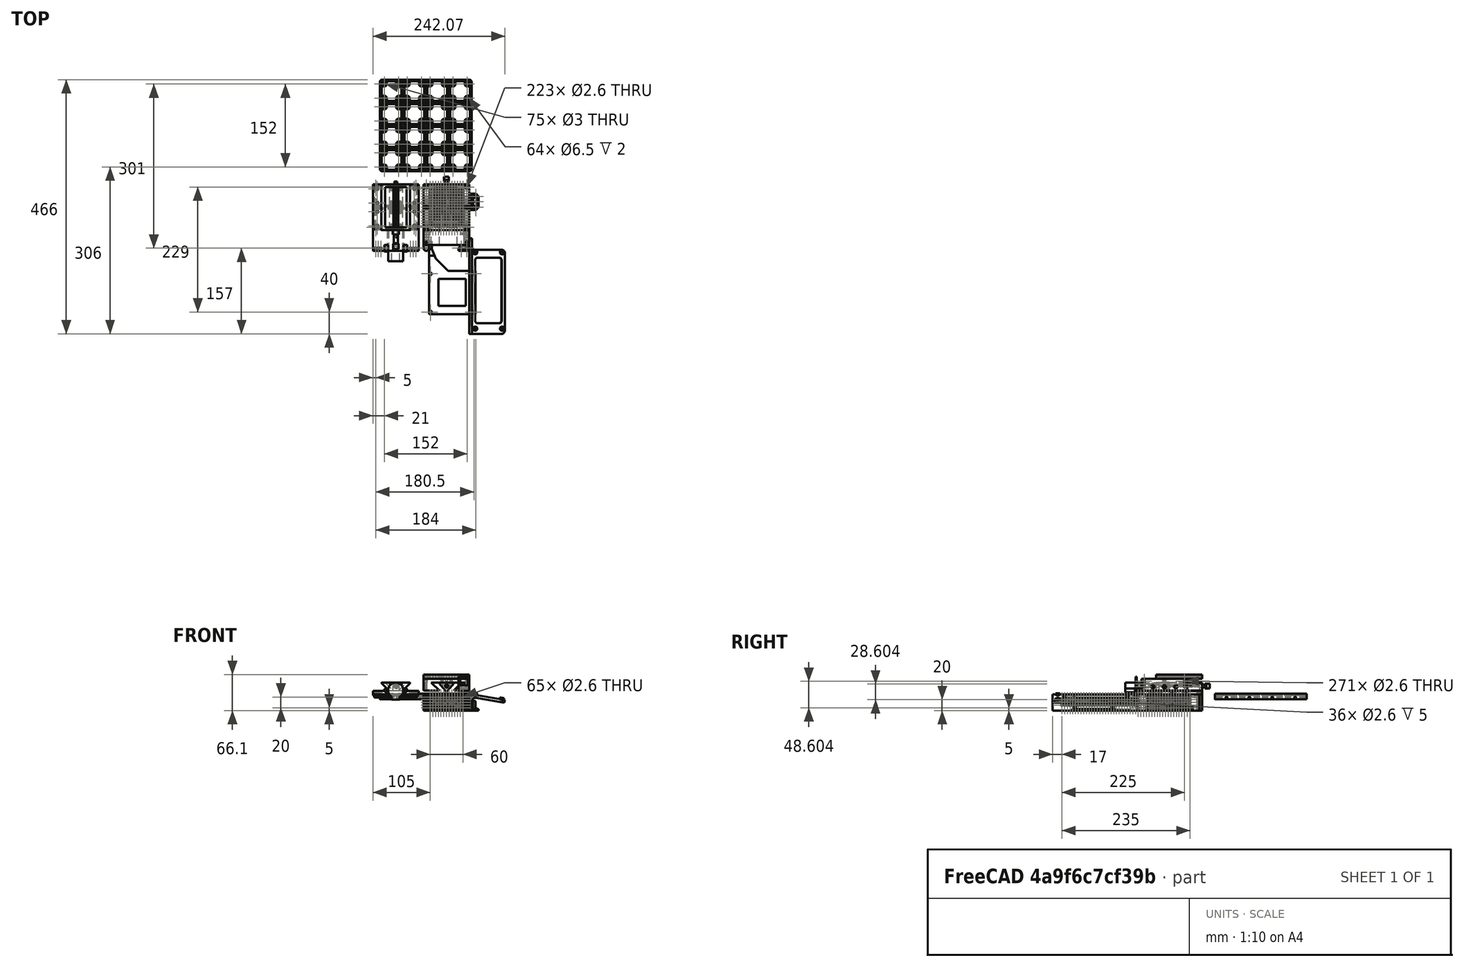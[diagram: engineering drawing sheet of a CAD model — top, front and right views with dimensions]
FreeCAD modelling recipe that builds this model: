
FCSTD DOCUMENT  (FreeCAD 1.0R39109 (Git))
Label: Linear Stage Motorised B Field Version
License: All rights reserved
LicenseURL: https://en.wikipedia.org/wiki/All_rights_reserved
objects: Sketcher::SketchObject×110, PartDesign::Pocket×58, PartDesign::Pad×54, PartDesign::Chamfer×31, PartDesign::Plane×19, PartDesign::Body×18, PartDesign::ShapeBinder×17, PartDesign::Fillet×6, PartDesign::SubShapeBinder×5, PartDesign::LinearPattern×4, PartDesign::Hole×3, PartDesign::FeatureBase×3, PartDesign::Point×1, Part::Part2DObjectPython×1, Part::Helix×1, PartDesign::AdditivePipe×1, Part::FeaturePython×1, App::VarSet×1, PartDesign::FeaturePython×1
note: 758 computed .brp shape members not serialized (recipe doc carries the construction recipe); baked Part::Feature solids carry a one-line shape summary decoded from their .brp

FEATURE [Sketcher::SketchObject] Sketch
  ArcFitTolerance = 1e-06
  AttachmentSupport = -> [XZ_Plane]
  FullyConstrained = true
  MakeInternals = false
  MapMode = 5
  Placement = pos=(0,0,0) rot=(1,0,0;1.5708rad)
  sketch-geometry (8):
    g0: LineSegment StartX=0 StartY=0 StartZ=0 EndX=84 EndY=0 EndZ=0
    g1: LineSegment StartX=0 StartY=0 StartZ=0 EndX=0 EndY=5 EndZ=0
    g2: LineSegment StartX=84 StartY=0 StartZ=0 EndX=84 EndY=5 EndZ=0
    g3: LineSegment StartX=0 StartY=5 StartZ=0 EndX=30 EndY=5 EndZ=0
    g4: LineSegment StartX=84 StartY=5 StartZ=0 EndX=54 EndY=5 EndZ=0
    g5: LineSegment StartX=30 StartY=5 StartZ=0 EndX=15 EndY=20 EndZ=0
    g6: LineSegment StartX=54 StartY=5 StartZ=0 EndX=69 EndY=20 EndZ=0
    g7: LineSegment StartX=15 StartY=20 StartZ=0 EndX=69 EndY=20 EndZ=0
  constraints (24):
    c: Distance(g0) = 84
    c: Distance(g1) = 5
    c: Coincident(g1,g0)
    c: PointOnObject(g1,g-2)
    c: Vertical(g1)
    c: Distance(g2) = 5
    c: Vertical(g2)
    c: Tangent(g0,g-1)
    c: PointOnObject(g2,g0)
    c: PointOnObject(g0,g2)
    c: Coincident(g3,g1)
    c: Horizontal(g3)
    c: Coincident(g4,g2)
    c: Horizontal(g4)
    c: DistanceX(g3,g3) = 30
    c: DistanceX(g4,g4) = 30
    c: Angle(g-1,g5) = 2.35619
    c: Coincident(g5,g3)
    c: Angle(g-1,g6) = 0.785398
    c: Coincident(g6,g4)
    c: DistanceY(g-1,g5) = 20
    c: DistanceY(g-1,g6) = 20
    c: Coincident(g7,g5)
    c: Coincident(g7,g6)
FEATURE [PartDesign::Pad] Pad
  Direction = (0,-1,2e-16)
  Length = 5
  Length2 = 10
  Placement = pos=(0,0,0) rot=(1,0,0;1.5708rad)
  Profile = -> Sketch
  ReferenceAxis = -> Sketch [N_Axis]
  Refine = true
  Suppressed = false
  Type = 0
FEATURE [Sketcher::SketchObject] Sketch001
  ArcFitTolerance = 1e-06
  AttachmentSupport = -> [Pad]
  ExternalGeometry = -> [Pad]
  FullyConstrained = true
  MakeInternals = false
  MapMode = 5
  Placement = pos=(0,-5,0) rot=(1,0,0;1.5708rad)
  sketch-geometry (14):
    g0: LineSegment StartX=15 StartY=20 StartZ=0 EndX=22.5 EndY=20 EndZ=0
    g1: LineSegment [constr] StartX=30 StartY=5 StartZ=0 EndX=37.5 EndY=5 EndZ=0
    g2: LineSegment StartX=22.5 StartY=20 StartZ=0 EndX=37.5 EndY=5 EndZ=0
    g3: LineSegment StartX=69 StartY=20 StartZ=0 EndX=61.5 EndY=20 EndZ=0
    g4: LineSegment [constr] StartX=54 StartY=5 StartZ=0 EndX=46.5 EndY=5 EndZ=0
    g5: LineSegment StartX=46.5 StartY=5 StartZ=0 EndX=61.5 EndY=20 EndZ=0
    g6: LineSegment StartX=46.5 StartY=5 StartZ=0 EndX=37.5 EndY=5 EndZ=0
    g7: LineSegment StartX=15 StartY=20 StartZ=0 EndX=30 EndY=5 EndZ=0
    g8: LineSegment StartX=30 StartY=5 StartZ=0 EndX=0 EndY=5 EndZ=0
    g9: LineSegment StartX=0 StartY=5 StartZ=0 EndX=0 EndY=0 EndZ=0
    g10: LineSegment StartX=0 StartY=0 StartZ=0 EndX=84 EndY=0 EndZ=0
    g11: LineSegment StartX=84 StartY=0 StartZ=0 EndX=84 EndY=5 EndZ=0
    g12: LineSegment StartX=84 StartY=5 StartZ=0 EndX=54 EndY=5 EndZ=0
    g13: LineSegment StartX=54 StartY=5 StartZ=0 EndX=69 EndY=20 EndZ=0
  constraints (32):
    c: Distance(g0) = 7.5
    c: Coincident(g0,g-4)
    c: PointOnObject(g0,g-3)
    c: Distance(g1) = 7.5
    c: Coincident(g1,g-5)
    c: Horizontal(g1)
    c: Coincident(g2,g0)
    c: Coincident(g2,g1)
    c: Distance(g3) = 7.5
    c: Coincident(g3,g-3)
    c: PointOnObject(g3,g-3)
    c: Distance(g4) = 7.5
    c: Coincident(g4,g-6)
    c: Horizontal(g4)
    c: Coincident(g5,g4)
    c: Coincident(g5,g3)
    c: Coincident(g6,g4)
    c: Coincident(g6,g1)
    c: Coincident(g7,g0)
    c: Coincident(g7,g1)
    c: Coincident(g8,g1)
    c: Coincident(g8,g-8)
    c: Coincident(g9,g8)
    c: Coincident(g9,g-1)
    c: Coincident(g10,g9)
    c: Coincident(g10,g-9)
    c: Coincident(g11,g10)
    c: Coincident(g11,g-7)
    c: Coincident(g12,g11)
    c: Coincident(g12,g4)
    c: Coincident(g13,g4)
    c: Coincident(g13,g3)
FEATURE [PartDesign::Pad] Pad001
  BaseFeature = -> Pad
  Direction = (0,-1,2e-16)
  Length = 74
  Length2 = 10
  Placement = pos=(0,0,0) rot=(1,0,0;1.5708rad)
  Profile = -> Sketch001
  ReferenceAxis = -> Sketch001 [N_Axis]
  Refine = true
  Suppressed = false
  Type = 0
FEATURE [Sketcher::SketchObject] Sketch002
  ArcFitTolerance = 1e-06
  AttachmentSupport = -> [Pad001]
  ExternalGeometry = -> [Pad001]
  FullyConstrained = true
  MakeInternals = false
  MapMode = 5
  Placement = pos=(0,-5,0) rot=(1,0,0;1.5708rad)
  sketch-geometry (2):
    g0: LineSegment [constr] StartX=42 StartY=20 StartZ=0 EndX=42 EndY=14 EndZ=0
    g1: Circle CenterX=42 CenterY=14 CenterZ=0 NormalX=0 NormalY=0 NormalZ=1 AngleXU=0 Radius=3
  constraints (5):
    c: Distance(g0) = 6
    c: Symmetric(g-3,g-3,g0)
    c: Vertical(g0)
    c: Diameter(g1) = 6
    c: Coincident(g1,g0)
FEATURE [PartDesign::Hole] Hole
  BaseFeature = -> Pad001
  CustomThreadClearance = 0
  Depth = 25
  DepthType = 0
  Diameter = 6
  DrillForDepth = false
  DrillPoint = 1
  DrillPointAngle = 118
  HoleCutCountersinkAngle = 90
  HoleCutCustomValues = false
  HoleCutDepth = 0
  HoleCutDiameter = 6.1
  HoleCutType = 0
  ModelThread = false
  Placement = pos=(0,0,0) rot=(1,0,0;1.5708rad)
  Profile = -> Sketch002
  Refine = true
  Suppressed = false
  Tapered = false
  TaperedAngle = 90
  ThreadClass = 0
  ThreadDepth = 25
  ThreadDepthType = 0
  ThreadDirection = 0
  ThreadFit = 0
  ThreadSize = 0
  ThreadType = 0
  Threaded = false
  UseCustomThreadClearance = false
FEATURE [Sketcher::SketchObject] Sketch003
  ArcFitTolerance = 1e-06
  AttachmentSupport = -> [Hole]
  ExternalGeometry = -> [Hole]
  FullyConstrained = true
  MakeInternals = false
  MapMode = 5
  Placement = pos=(0,-79,1.74e-14) rot=(1,0,0;1.5708rad)
  sketch-geometry (16):
    g0: LineSegment StartX=15 StartY=20 StartZ=0 EndX=69 EndY=20 EndZ=0
    g1: LineSegment StartX=15 StartY=20 StartZ=0 EndX=30 EndY=5 EndZ=0
    g2: LineSegment StartX=30 StartY=5 StartZ=0 EndX=0 EndY=5 EndZ=0
    g3: LineSegment StartX=0 StartY=5 StartZ=0 EndX=0 EndY=0 EndZ=0
    g4: LineSegment StartX=0 StartY=0 StartZ=0 EndX=84 EndY=0 EndZ=0
    g5: LineSegment StartX=84 StartY=0 StartZ=0 EndX=84 EndY=5 EndZ=0
    g6: LineSegment StartX=84 StartY=5 StartZ=0 EndX=54 EndY=5 EndZ=0
    g7: LineSegment StartX=54 StartY=5 StartZ=0 EndX=69 EndY=20 EndZ=0
    g8: LineSegment [constr] StartX=42 StartY=20 StartZ=0 EndX=42 EndY=14 EndZ=0
    g9: Circle CenterX=42 CenterY=14 CenterZ=0 NormalX=0 NormalY=0 NormalZ=1 AngleXU=0 Radius=3
    g10: LineSegment [constr] StartX=42 StartY=14 StartZ=0 EndX=22.5 EndY=20 EndZ=0
    g11: LineSegment [constr] StartX=42 StartY=14 StartZ=0 EndX=61.5 EndY=20 EndZ=0
    g12: GeomPoint [constr] X=32.25 Y=17 Z=0
    g13: GeomPoint [constr] X=51.75 Y=17 Z=0
    g14: Circle CenterX=32.25 CenterY=17 CenterZ=0 NormalX=0 NormalY=0 NormalZ=1 AngleXU=0 Radius=1.25
    g15: Circle CenterX=51.75 CenterY=17 CenterZ=0 NormalX=0 NormalY=0 NormalZ=1 AngleXU=0 Radius=1.25
  constraints (31):
    c: Coincident(g0,g-4)
    c: Coincident(g0,g-11)
    c: Coincident(g1,g0)
    c: Coincident(g1,g-5)
    c: Coincident(g2,g1)
    c: Coincident(g2,g-6)
    c: Coincident(g3,g2)
    c: Coincident(g3,g-1)
    c: Coincident(g4,g3)
    c: Coincident(g4,g-8)
    c: Coincident(g5,g4)
    c: Coincident(g5,g-9)
    c: Coincident(g6,g5)
    c: Coincident(g6,g-10)
    c: Coincident(g7,g6)
    c: Coincident(g7,g0)
    c: Distance(g8) = 6
    c: Symmetric(g0,g0,g8)
    c: Vertical(g8)
    c: Diameter(g9) = 6
    c: Coincident(g9,g8)
    c: Coincident(g10,g8)
    c: Coincident(g10,g-14)
    c: Coincident(g11,g8)
    c: Coincident(g11,g-12)
    c: Symmetric(g10,g10,g12)
    c: Symmetric(g11,g11,g13)
    c: Diameter(g14) = 2.5
    c: Coincident(g14,g12)
    c: Diameter(g15) = 2.5
    c: Coincident(g15,g13)
FEATURE [PartDesign::Pad] Pad002
  BaseFeature = -> Hole
  Direction = (0,-1,2e-16)
  Length = 5
  Length2 = 10
  Placement = pos=(0,0,0) rot=(1,0,0;1.5708rad)
  Profile = -> Sketch003
  ReferenceAxis = -> Sketch003 [N_Axis]
  Refine = true
  Suppressed = false
  Type = 0
FEATURE [PartDesign::Plane] DatumPlane
  AttachmentSupport = -> [Pad002]
  Length = 131.586
  MapMode = 5
  Placement = pos=(0,0,-5e-16) rot=(1,0,0;3.14159rad)
  ResizeMode = 0
  Width = 139.586
FEATURE [Sketcher::SketchObject] Sketch004
  ArcFitTolerance = 1e-06
  AttachmentSupport = -> [Pad002]
  ExternalGeometry = -> [Pad002]
  FullyConstrained = true
  MakeInternals = false
  MapMode = 5
  Placement = pos=(0,0,-5e-16) rot=(1,0,0;3.14159rad)
  sketch-geometry (23):
    g0: LineSegment [constr] StartX=0 StartY=84 StartZ=0 EndX=84 EndY=0 EndZ=0
    g1: LineSegment [constr] StartX=41.75 StartY=41.75 StartZ=0 EndX=42.25 EndY=41.75 EndZ=0
    g2: LineSegment [constr] StartX=42.25 StartY=41.75 StartZ=0 EndX=42.25 EndY=42.25 EndZ=0
    g3: LineSegment [constr] StartX=42.25 StartY=42.25 StartZ=0 EndX=41.75 EndY=42.25 EndZ=0
    g4: LineSegment [constr] StartX=41.75 StartY=42.25 StartZ=0 EndX=41.75 EndY=41.75 EndZ=0
    g5: GeomPoint [constr] X=42 Y=42 Z=0
    g6: LineSegment [constr] StartX=0 StartY=0 StartZ=0 EndX=84 EndY=84 EndZ=0
    g7: LineSegment StartX=42.25 StartY=42.25 StartZ=0 EndX=83.75 EndY=42.25 EndZ=0
    g8: LineSegment StartX=83.75 StartY=42.25 StartZ=0 EndX=83.75 EndY=83.75 EndZ=0
    g9: LineSegment StartX=83.75 StartY=83.75 StartZ=0 EndX=42.25 EndY=83.75 EndZ=0
    g10: LineSegment StartX=42.25 StartY=83.75 StartZ=0 EndX=42.25 EndY=42.25 EndZ=0
    g11: LineSegment StartX=41.75 StartY=42.25 StartZ=0 EndX=41.75 EndY=83.75 EndZ=0
    g12: LineSegment StartX=41.75 StartY=83.75 StartZ=0 EndX=0.25 EndY=83.75 EndZ=0
    g13: LineSegment StartX=0.25 StartY=83.75 StartZ=0 EndX=0.25 EndY=42.25 EndZ=0
    g14: LineSegment StartX=0.25 StartY=42.25 StartZ=0 EndX=41.75 EndY=42.25 EndZ=0
    g15: LineSegment StartX=42.25 StartY=41.75 StartZ=0 EndX=42.25 EndY=0.25 EndZ=0
    g16: LineSegment StartX=42.25 StartY=0.25 StartZ=0 EndX=83.75 EndY=0.25 EndZ=0
    g17: LineSegment StartX=83.75 StartY=0.25 StartZ=0 EndX=83.75 EndY=41.75 EndZ=0
    g18: LineSegment StartX=83.75 StartY=41.75 StartZ=0 EndX=42.25 EndY=41.75 EndZ=0
    g19: LineSegment StartX=41.75 StartY=41.75 StartZ=0 EndX=0.25 EndY=41.75 EndZ=0
    g20: LineSegment StartX=0.25 StartY=41.75 StartZ=0 EndX=0.25 EndY=0.25 EndZ=0
    g21: LineSegment StartX=0.25 StartY=0.25 StartZ=0 EndX=41.75 EndY=0.25 EndZ=0
    g22: LineSegment StartX=41.75 StartY=0.25 StartZ=0 EndX=41.75 EndY=41.75 EndZ=0
  constraints (61):
    c: Coincident(g0,g-6)
    c: Coincident(g0,g-5)
    c: Coincident(g1,g2)
    c: Coincident(g2,g3)
    c: Coincident(g3,g4)
    c: Coincident(g4,g1)
    c: Horizontal(g1)
    c: Horizontal(g3)
    c: Vertical(g2)
    c: Vertical(g4)
    c: Symmetric(g3,g1,g5)
    c: Distance(g2,g4) = 0.5
    c: Distance(g1,g3) = 0.5
    c: PointOnObject(g5,g0)
    c: Coincident(g6,g-1)
    c: Coincident(g6,g-4)
    c: PointOnObject(g5,g6)
    c: Coincident(g7,g8)
    c: Coincident(g8,g9)
    c: Coincident(g9,g10)
    c: Coincident(g10,g7)
    c: Horizontal(g7)
    c: Horizontal(g9)
    c: Vertical(g8)
    c: Vertical(g10)
    c: Distance(g8,g10) = 41.5
    c: Coincident(g7,g2)
    c: PointOnObject(g8,g6)
    c: Coincident(g11,g12)
    c: Coincident(g12,g13)
    c: Coincident(g13,g14)
    c: Coincident(g14,g11)
    c: Vertical(g11)
    c: Vertical(g13)
    c: Horizontal(g12)
    c: Horizontal(g14)
    c: Distance(g11,g13) = 41.5
    c: Coincident(g11,g3)
    c: PointOnObject(g12,g0)
    c: Coincident(g15,g16)
    c: Coincident(g16,g17)
    c: Coincident(g17,g18)
    c: Coincident(g18,g15)
    c: Vertical(g15)
    c: Vertical(g17)
    c: Horizontal(g16)
    c: Horizontal(g18)
    c: Distance(g15,g17) = 41.5
    c: Coincident(g15,g1)
    c: PointOnObject(g16,g0)
    c: Coincident(g19,g20)
    c: Coincident(g20,g21)
    c: Coincident(g21,g22)
    c: Coincident(g22,g19)
    c: Horizontal(g19)
    c: Horizontal(g21)
    c: Vertical(g20)
    c: Vertical(g22)
    c: Distance(g20,g22) = 41.5
    c: Coincident(g19,g1)
    c: PointOnObject(g20,g6)
FEATURE [PartDesign::Pad] Pad003
  BaseFeature = -> Pad002
  Direction = (0,0,-1)
  Length = 1
  Length2 = 10
  Placement = pos=(0,0,0) rot=(1,0,0;1.5708rad)
  Profile = -> Sketch004
  ReferenceAxis = -> Sketch004 [N_Axis]
  Refine = true
  Suppressed = false
  Type = 0
FEATURE [PartDesign::Plane] DatumPlane001
  AttachmentSupport = -> [Pad003]
  Length = 131.586
  MapMode = 5
  Placement = pos=(0,0,-1) rot=(1,0,0;3.14159rad)
  ResizeMode = 0
  Width = 139.586
FEATURE [Sketcher::SketchObject] Sketch005
  ArcFitTolerance = 1e-06
  AttachmentSupport = -> [DatumPlane001]
  ExternalGeometry = -> [Pad003]
  FullyConstrained = true
  MakeInternals = false
  MapMode = 5
  Placement = pos=(0,0,-1) rot=(1,0,0;3.14159rad)
  sketch-geometry (28):
    g0: LineSegment [constr] StartX=41.75 StartY=42.25 StartZ=0 EndX=0.25 EndY=83.75 EndZ=0
    g1: GeomPoint [constr] X=21 Y=63 Z=0
    g2: LineSegment StartX=2.4 StartY=44.4 StartZ=0 EndX=39.6 EndY=44.4 EndZ=0
    g3: LineSegment StartX=39.6 StartY=44.4 StartZ=0 EndX=39.6 EndY=81.6 EndZ=0
    g4: LineSegment StartX=39.6 StartY=81.6 StartZ=0 EndX=2.4 EndY=81.6 EndZ=0
    g5: LineSegment StartX=2.4 StartY=81.6 StartZ=0 EndX=2.4 EndY=44.4 EndZ=0
    g6: GeomPoint [constr] X=21 Y=63 Z=0
    g7: LineSegment [constr] StartX=42.25 StartY=83.75 StartZ=0 EndX=83.75 EndY=42.25 EndZ=0
    g8: LineSegment [constr] StartX=83.75 StartY=41.75 StartZ=0 EndX=42.25 EndY=0.25 EndZ=0
    g9: LineSegment [constr] StartX=41.75 StartY=0.25 StartZ=0 EndX=0.25 EndY=41.75 EndZ=0
    g10: GeomPoint [constr] X=63 Y=63 Z=0
    g11: GeomPoint [constr] X=63 Y=21 Z=0
    g12: GeomPoint [constr] X=21 Y=21 Z=0
    g13: LineSegment StartX=44.4 StartY=44.4 StartZ=0 EndX=81.6 EndY=44.4 EndZ=0
    g14: LineSegment StartX=81.6 StartY=44.4 StartZ=0 EndX=81.6 EndY=81.6 EndZ=0
    g15: LineSegment StartX=81.6 StartY=81.6 StartZ=0 EndX=44.4 EndY=81.6 EndZ=0
    g16: LineSegment StartX=44.4 StartY=81.6 StartZ=0 EndX=44.4 EndY=44.4 EndZ=0
    g17: GeomPoint [constr] X=63 Y=63 Z=0
    g18: LineSegment StartX=44.4 StartY=2.4 StartZ=0 EndX=81.6 EndY=2.4 EndZ=0
    g19: LineSegment StartX=81.6 StartY=2.4 StartZ=0 EndX=81.6 EndY=39.6 EndZ=0
    g20: LineSegment StartX=81.6 StartY=39.6 StartZ=0 EndX=44.4 EndY=39.6 EndZ=0
    g21: LineSegment StartX=44.4 StartY=39.6 StartZ=0 EndX=44.4 EndY=2.4 EndZ=0
    g22: GeomPoint [constr] X=63 Y=21 Z=0
    g23: LineSegment StartX=2.4 StartY=2.4 StartZ=0 EndX=39.6 EndY=2.4 EndZ=0
    g24: LineSegment StartX=39.6 StartY=2.4 StartZ=0 EndX=39.6 EndY=39.6 EndZ=0
    g25: LineSegment StartX=39.6 StartY=39.6 StartZ=0 EndX=2.4 EndY=39.6 EndZ=0
    g26: LineSegment StartX=2.4 StartY=39.6 StartZ=0 EndX=2.4 EndY=2.4 EndZ=0
    g27: GeomPoint [constr] X=21 Y=21 Z=0
  constraints (60):
    c: Coincident(g0,g-14)
    c: Coincident(g0,g-16)
    c: Symmetric(g0,g0,g1)
    c: Coincident(g2,g3)
    c: Coincident(g3,g4)
    c: Coincident(g4,g5)
    c: Coincident(g5,g2)
    c: Horizontal(g2)
    c: Horizontal(g4)
    c: Vertical(g3)
    c: Vertical(g5)
    c: Symmetric(g4,g2,g6)
    c: Distance(g3,g5) = 37.2
    c: Distance(g2,g4) = 37.2
    c: Coincident(g6,g1)
    c: Coincident(g7,g-18)
    c: Coincident(g7,g-17)
    c: Coincident(g8,g-9)
    c: Coincident(g8,g-10)
    c: Coincident(g9,g-4)
    c: Coincident(g9,g-6)
    c: Symmetric(g7,g7,g10)
    c: Symmetric(g8,g8,g11)
    c: Symmetric(g9,g9,g12)
    c: Coincident(g13,g14)
    c: Coincident(g14,g15)
    c: Coincident(g15,g16)
    c: Coincident(g16,g13)
    c: Horizontal(g13)
    c: Horizontal(g15)
    c: Vertical(g14)
    c: Vertical(g16)
    c: Symmetric(g15,g13,g17)
    c: Distance(g14,g16) = 37.2
    c: Distance(g13,g15) = 37.2
    c: Coincident(g17,g10)
    c: Coincident(g18,g19)
    c: Coincident(g19,g20)
    c: Coincident(g20,g21)
    c: Coincident(g21,g18)
    c: Horizontal(g18)
    c: Horizontal(g20)
    c: Vertical(g19)
    c: Vertical(g21)
    c: Symmetric(g20,g18,g22)
    c: Distance(g19,g21) = 37.2
    c: Coincident(g22,g11)
    c: PointOnObject(g19,g8)
    c: Coincident(g23,g24)
    c: Coincident(g24,g25)
    c: Coincident(g25,g26)
    c: Coincident(g26,g23)
    c: Horizontal(g23)
    c: Horizontal(g25)
    c: Vertical(g24)
    c: Vertical(g26)
    c: Symmetric(g25,g23,g27)
    c: Distance(g24,g26) = 37.2
    c: Distance(g23,g25) = 37.2
    c: Coincident(g27,g12)
FEATURE [PartDesign::Pad] Pad004
  BaseFeature = -> Pad003
  Direction = (0,0,-1)
  Length = 3.5
  Length2 = 10
  Placement = pos=(0,0,0) rot=(1,0,0;1.5708rad)
  Profile = -> Sketch005
  ReferenceAxis = -> Sketch005 [N_Axis]
  Refine = true
  Suppressed = false
  Type = 0
FEATURE [PartDesign::Chamfer] Chamfer
  Angle = 45
  Base = -> Pad004 [Edge114]
  BaseFeature = -> Pad004
  ChamferType = 0
  FlipDirection = false
  Placement = pos=(0,0,0) rot=(1,0,0;1.5708rad)
  Refine = true
  Size = 7
  Size2 = 1
  SupportTransform = false
  Suppressed = false
  UseAllEdges = false
FEATURE [PartDesign::Chamfer] Chamfer001
  Angle = 45
  Base = -> Chamfer [Edge23]
  BaseFeature = -> Chamfer
  ChamferType = 0
  FlipDirection = false
  Placement = pos=(0,0,0) rot=(1,0,0;1.5708rad)
  Refine = true
  Size = 7
  Size2 = 1
  SupportTransform = false
  Suppressed = false
  UseAllEdges = false
FEATURE [PartDesign::Chamfer] Chamfer002
  Angle = 45
  Base = -> Chamfer001 [Edge136,Edge28,Edge143,Edge22,Edge135,Edge128,Edge144,Edge148,Edge140,Edge127,Edge132,Edge138,Edge26,Edge130]
  BaseFeature = -> Chamfer001
  ChamferType = 0
  FlipDirection = false
  Placement = pos=(0,0,0) rot=(1,0,0;1.5708rad)
  Refine = true
  Size = 7
  Size2 = 1
  SupportTransform = false
  Suppressed = false
  UseAllEdges = false
FEATURE [PartDesign::Chamfer] Chamfer003
  Angle = 45
  Base = -> Chamfer002 [Edge77,Edge79,Edge93,Edge81,Edge95,Edge38,Edge76,Edge32,Edge92,Edge84,Edge97,Edge85,Edge87,Edge89,Edge35]
  BaseFeature = -> Chamfer002
  ChamferType = 0
  FlipDirection = false
  Placement = pos=(0,0,0) rot=(1,0,0;1.5708rad)
  Refine = true
  Size = 8
  Size2 = 1
  SupportTransform = false
  Suppressed = false
  UseAllEdges = false
FEATURE [PartDesign::Chamfer] Chamfer004
  Angle = 45
  Base = -> Chamfer003 [Edge231]
  BaseFeature = -> Chamfer003
  ChamferType = 0
  FlipDirection = false
  Placement = pos=(0,0,0) rot=(1,0,0;1.5708rad)
  Refine = true
  Size = 7
  Size2 = 1
  SupportTransform = false
  Suppressed = false
  UseAllEdges = false
FEATURE [PartDesign::Chamfer] Chamfer005
  Angle = 45
  Base = -> Chamfer004 [Edge1,Edge2,Edge4,Edge6,Edge8,Edge7,Edge5,Edge3]
  BaseFeature = -> Chamfer004
  ChamferType = 0
  FlipDirection = false
  Placement = pos=(0,0,0) rot=(1,0,0;1.5708rad)
  Refine = true
  Size = 2
  Size2 = 1
  SupportTransform = false
  Suppressed = false
  UseAllEdges = false
FEATURE [PartDesign::Chamfer] Chamfer006
  Angle = 45
  Base = -> Chamfer005 [Edge60,Edge64,Edge62,Edge58,Edge55,Edge50,Edge52,Edge56]
  BaseFeature = -> Chamfer005
  ChamferType = 0
  FlipDirection = false
  Placement = pos=(0,0,0) rot=(1,0,0;1.5708rad)
  Refine = true
  Size = 0.8
  Size2 = 1
  SupportTransform = false
  Suppressed = false
  UseAllEdges = false
FEATURE [PartDesign::Chamfer] Chamfer007
  Angle = 45
  Base = -> Chamfer006 [Edge207,Edge208,Edge205,Edge206,Edge204,Edge202,Edge203,Edge201]
  BaseFeature = -> Chamfer006
  ChamferType = 0
  FlipDirection = false
  Placement = pos=(0,0,0) rot=(1,0,0;1.5708rad)
  Refine = true
  Size = 2
  Size2 = 1
  SupportTransform = false
  Suppressed = false
  UseAllEdges = false
FEATURE [PartDesign::Chamfer] Chamfer008
  Angle = 45
  Base = -> Chamfer007 [Edge63,Edge64,Edge60,Edge57,Edge52,Edge50,Edge55,Edge59]
  BaseFeature = -> Chamfer007
  ChamferType = 0
  FlipDirection = false
  Placement = pos=(0,0,0) rot=(1,0,0;1.5708rad)
  Refine = true
  Size = 0.8
  Size2 = 1
  SupportTransform = false
  Suppressed = false
  UseAllEdges = false
FEATURE [PartDesign::Chamfer] Chamfer009
  Angle = 45
  Base = -> Chamfer008 [Edge179,Edge177,Edge178,Edge181,Edge180,Edge182,Edge184,Edge183]
  BaseFeature = -> Chamfer008
  ChamferType = 0
  FlipDirection = false
  Placement = pos=(0,0,0) rot=(1,0,0;1.5708rad)
  Refine = true
  Size = 2
  Size2 = 1
  SupportTransform = false
  Suppressed = false
  UseAllEdges = false
FEATURE [PartDesign::Chamfer] Chamfer010
  Angle = 45
  Base = -> Chamfer009 [Edge55,Edge58,Edge62,Edge64,Edge61,Edge56,Edge53,Edge50]
  BaseFeature = -> Chamfer009
  ChamferType = 0
  FlipDirection = false
  Placement = pos=(0,0,0) rot=(1,0,0;1.5708rad)
  Refine = true
  Size = 0.8
  Size2 = 1
  SupportTransform = false
  Suppressed = false
  UseAllEdges = false
FEATURE [PartDesign::Chamfer] Chamfer011
  Angle = 45
  Base = -> Chamfer010 [Edge203,Edge205,Edge201,Edge202,Edge204,Edge206,Edge208,Edge207]
  BaseFeature = -> Chamfer010
  ChamferType = 0
  FlipDirection = false
  Placement = pos=(0,0,0) rot=(1,0,0;1.5708rad)
  Refine = true
  Size = 2
  Size2 = 1
  SupportTransform = false
  Suppressed = false
  UseAllEdges = false
FEATURE [PartDesign::Chamfer] Chamfer012
  Angle = 45
  Base = -> Chamfer011 [Edge62,Edge59,Edge54,Edge50,Edge53,Edge56,Edge61,Edge64]
  BaseFeature = -> Chamfer011
  ChamferType = 0
  FlipDirection = false
  Placement = pos=(0,0,0) rot=(1,0,0;1.5708rad)
  Refine = true
  Size = 0.8
  Size2 = 1
  SupportTransform = false
  Suppressed = false
  UseAllEdges = false
FEATURE [PartDesign::Fillet] Fillet
  Base = -> Chamfer012 [Edge188,Edge187]
  BaseFeature = -> Chamfer012
  Placement = pos=(0,0,0) rot=(1,0,0;1.5708rad)
  Radius = 0.5
  Refine = true
  SupportTransform = false
  Suppressed = false
  UseAllEdges = false
FEATURE [PartDesign::ShapeBinder] ShapeBinder
  Support = -> [Fillet]
  TraceSupport = false
FEATURE [PartDesign::ShapeBinder] CopyFillet
  Placement = pos=(0,-5,2e-15) rot=(0,0,1;0rad)
  TraceSupport = false
FEATURE [PartDesign::Plane] DatumPlane002
  AttachmentSupport = -> [CopyFillet]
  Length = 111.71
  MapMode = 5
  Placement = pos=(0,-84,2e-15) rot=(1,0,0;1.5708rad)
  ResizeMode = 0
  Width = 63.9806
FEATURE [Sketcher::SketchObject] Sketch006
  ArcFitTolerance = 1e-06
  AttachmentSupport = -> [DatumPlane002]
  ExternalGeometry = -> [ShapeBinder]
  FullyConstrained = true
  MakeInternals = false
  MapMode = 5
  Placement = pos=(0,-84,2e-15) rot=(1,0,0;1.5708rad)
  sketch-geometry (16):
    g0: LineSegment [constr] StartX=68.1465 StartY=19.1464 StartZ=0 EndX=69 EndY=20 EndZ=0
    g1: LineSegment [constr] StartX=67.7929 StartY=20 StartZ=0 EndX=69 EndY=20 EndZ=0
    g2: LineSegment [constr] StartX=69 StartY=20 StartZ=0 EndX=69.5 EndY=20 EndZ=0
    g3: LineSegment [constr] StartX=69.5 StartY=20 StartZ=0 EndX=74.5 EndY=20 EndZ=0
    g4: LineSegment [constr] StartX=54 StartY=5 StartZ=0 EndX=54.5 EndY=5 EndZ=0
    g5: LineSegment [constr] StartX=54.5 StartY=5 StartZ=0 EndX=59.5 EndY=5 EndZ=0
    g6: LineSegment [constr] StartX=59.5 StartY=5 StartZ=0 EndX=74.5 EndY=20 EndZ=0
    g7: LineSegment [constr] StartX=54.5 StartY=5 StartZ=0 EndX=69.5 EndY=20 EndZ=0
    g8: LineSegment [constr] StartX=59.5 StartY=5 StartZ=0 EndX=59.8536 EndY=5.35355 EndZ=0
    g9: LineSegment [constr] StartX=54.5 StartY=5 StartZ=0 EndX=54.8536 EndY=5.35355 EndZ=0
    g10: LineSegment [constr] StartX=74.5 StartY=20 StartZ=0 EndX=74.1465 EndY=19.6464 EndZ=0
    g11: LineSegment [constr] StartX=69.5 StartY=20 StartZ=0 EndX=69.1465 EndY=19.6464 EndZ=0
    g12: LineSegment StartX=54.8536 StartY=5.35355 StartZ=0 EndX=59.8536 EndY=5.35355 EndZ=0
    g13: LineSegment StartX=59.8536 StartY=5.35355 StartZ=0 EndX=74.1465 EndY=19.6464 EndZ=0
    g14: LineSegment StartX=74.1465 StartY=19.6464 StartZ=0 EndX=69.1465 EndY=19.6464 EndZ=0
    g15: LineSegment StartX=69.1465 StartY=19.6464 StartZ=0 EndX=54.8536 EndY=5.35355 EndZ=0
  constraints (41):
    c: Coincident(g0,g-3)
    c: Coincident(g1,g-4)
    c: Coincident(g1,g0)
    c: Angle(g-4,g1) = 3.14159
    c: Angle(g-3,g0) = 3.14159
    c: Distance(g2) = 0.5
    c: Coincident(g2,g0)
    c: Horizontal(g2)
    c: Distance(g3) = 5
    c: Coincident(g3,g2)
    c: Horizontal(g3)
    c: Distance(g4) = 0.5
    c: Coincident(g4,g-3)
    c: Horizontal(g4)
    c: Distance(g5) = 5
    c: Coincident(g5,g4)
    c: Horizontal(g5)
    c: Coincident(g6,g5)
    c: Coincident(g6,g3)
    c: Coincident(g7,g4)
    c: Coincident(g7,g2)
    c: Distance(g8) = 0.5
    c: Coincident(g8,g5)
    c: PointOnObject(g8,g6)
    c: Distance(g9) = 0.5
    c: Coincident(g9,g4)
    c: PointOnObject(g9,g7)
    c: Distance(g10) = 0.5
    c: Coincident(g10,g3)
    c: PointOnObject(g10,g6)
    c: Distance(g11) = 0.5
    c: Coincident(g11,g2)
    c: PointOnObject(g11,g7)
    c: Coincident(g12,g9)
    c: Coincident(g12,g8)
    c: Coincident(g13,g8)
    c: Coincident(g13,g10)
    c: Coincident(g14,g10)
    c: Coincident(g14,g11)
    c: Coincident(g15,g11)
    c: Coincident(g15,g9)
FEATURE [PartDesign::Pad] Pad005
  Direction = (0,-1,2e-16)
  Length = 84
  Length2 = 10
  Placement = pos=(0,-84,2e-15) rot=(1,0,0;1.5708rad)
  Profile = -> Sketch006
  ReferenceAxis = -> Sketch006 [N_Axis]
  Refine = true
  Reversed = true
  Suppressed = false
  Type = 0
FEATURE [PartDesign::Plane] DatumPlane003
  AttachmentSupport = -> [Pad005]
  Length = 125.801
  MapMode = 5
  Placement = pos=(27.25,-84,-27.25) rot=(0.92388,0,0.382683;3.14159rad)
  ResizeMode = 0
  Width = 130.341
FEATURE [Sketcher::SketchObject] Sketch007
  ArcFitTolerance = 1e-06
  AttachmentSupport = -> [DatumPlane003]
  ExternalGeometry = -> [Pad005]
  FullyConstrained = true
  MakeInternals = false
  MapMode = 5
  Placement = pos=(27.25,-84,-27.25) rot=(0.92388,0,0.382683;3.14159rad)
  sketch-geometry (8):
    g0: LineSegment [constr] StartX=46.1084 StartY=-42 StartZ=0 EndX=66.3216 EndY=-42 EndZ=0
    g1: LineSegment [constr] StartX=56.215 StartY=-42 StartZ=0 EndX=56.215 EndY=-1.42e-14 EndZ=0
    g2: LineSegment [constr] StartX=56.215 StartY=-42 StartZ=0 EndX=56.215 EndY=-84 EndZ=0
    g3: GeomPoint [constr] X=56.215 Y=-63 Z=0
    g4: GeomPoint [constr] X=56.215 Y=-21 Z=0
    g5: Circle CenterX=56.215 CenterY=-21 CenterZ=0 NormalX=0 NormalY=0 NormalZ=1 AngleXU=0 Radius=1.55
    g6: Circle CenterX=56.215 CenterY=-42 CenterZ=0 NormalX=0 NormalY=0 NormalZ=1 AngleXU=0 Radius=1.55
    g7: Circle CenterX=56.215 CenterY=-63 CenterZ=0 NormalX=0 NormalY=0 NormalZ=1 AngleXU=0 Radius=1.55
  constraints (14):
    c: Symmetric(g-4,g-4,g0)
    c: Symmetric(g-3,g-3,g0)
    c: Symmetric(g0,g0,g1)
    c: Symmetric(g-5,g-5,g1)
    c: Coincident(g2,g1)
    c: Symmetric(g-6,g-6,g2)
    c: Symmetric(g2,g2,g3)
    c: Symmetric(g1,g1,g4)
    c: Diameter(g5) = 3.1
    c: Coincident(g5,g4)
    c: Diameter(g6) = 3.1
    c: Coincident(g6,g1)
    c: Diameter(g7) = 3.1
    c: Coincident(g7,g3)
FEATURE [PartDesign::Pocket] Pocket
  BaseFeature = -> Pad005
  Direction = (-0.707107,0,0.707107)
  Length = 1
  Length2 = 5
  Placement = pos=(0,-84,2e-15) rot=(1,0,0;1.5708rad)
  Profile = -> Sketch007
  ReferenceAxis = -> Sketch007 [N_Axis]
  Refine = true
  Suppressed = false
  Type = 0
FEATURE [PartDesign::Fillet] Fillet001
  Base = -> Pocket [Edge5,Edge10,Edge1,Edge2]
  BaseFeature = -> Pocket
  Placement = pos=(0,-84,2e-15) rot=(1,0,0;1.5708rad)
  Radius = 1
  Refine = true
  SupportTransform = false
  Suppressed = false
  UseAllEdges = false
FEATURE [PartDesign::Fillet] Fillet002
  Base = -> Fillet001 [Edge24,Edge25,Edge23]
  BaseFeature = -> Fillet001
  Placement = pos=(0,-84,2e-15) rot=(1,0,0;1.5708rad)
  Radius = 0.3
  Refine = true
  SupportTransform = false
  Suppressed = false
  UseAllEdges = false
FEATURE [PartDesign::Fillet] Fillet003
  Base = -> Fillet002 [Edge31,Edge37,Edge39]
  BaseFeature = -> Fillet002
  Placement = pos=(0,-84,2e-15) rot=(1,0,0;1.5708rad)
  Radius = 0.3
  Refine = true
  SupportTransform = false
  Suppressed = false
  UseAllEdges = false
FEATURE [PartDesign::Body] Body001  label="Shim"
  AllowCompound = false
  Group = -> [ShapeBinder,DatumPlane002,CopyFillet,Sketch006,Pad005,DatumPlane003,Sketch007,Pocket,Fillet001,Fillet002,Fillet003]
  Origin = -> Origin001
  Tip = -> Fillet003
FEATURE [PartDesign::ShapeBinder] ShapeBinder001
  Support = -> [Fillet]
  TraceSupport = false
FEATURE [PartDesign::ShapeBinder] CopyFillet001
  Placement = pos=(0,-5,2e-15) rot=(0,0,1;0rad)
  TraceSupport = false
FEATURE [PartDesign::Plane] DatumPlane004
  AttachmentSupport = -> [CopyFillet001]
  Length = 124.108
  MapMode = 5
  Placement = pos=(0,-84,2e-15) rot=(1,0,0;1.5708rad)
  ResizeMode = 0
  Width = 67.4619
FEATURE [Sketcher::SketchObject] Sketch008
  ArcFitTolerance = 1e-06
  AttachmentSupport = -> [DatumPlane004]
  ExternalGeometry = -> [ShapeBinder001]
  FullyConstrained = true
  MakeInternals = false
  MapMode = 5
  Placement = pos=(0,-84,2e-15) rot=(1,0,0;1.5708rad)
  sketch-geometry (21):
    g0: LineSegment [constr] StartX=54 StartY=5 StartZ=0 EndX=61 EndY=5 EndZ=0
    g1: LineSegment [constr] StartX=68.1465 StartY=19.1464 StartZ=0 EndX=69 EndY=20 EndZ=0
    g2: LineSegment [constr] StartX=67.7929 StartY=20 StartZ=0 EndX=69 EndY=20 EndZ=0
    g3: LineSegment [constr] StartX=69 StartY=20 StartZ=0 EndX=76 EndY=20 EndZ=0
    g4: LineSegment [constr] StartX=61 StartY=5 StartZ=0 EndX=61.3536 EndY=5.35355 EndZ=0
    g5: LineSegment [constr] StartX=76 StartY=20 StartZ=0 EndX=76.3536 EndY=20.3536 EndZ=0
    g6: LineSegment StartX=76.3536 StartY=20.3536 StartZ=0 EndX=61.3536 EndY=5.35355 EndZ=0
    g7: LineSegment [constr] StartX=84 StartY=5 StartZ=0 EndX=84 EndY=5.5 EndZ=0
    g8: LineSegment StartX=61.3536 StartY=5.35355 StartZ=0 EndX=84 EndY=5.35355 EndZ=0
    g9: LineSegment StartX=84 StartY=5.35355 StartZ=0 EndX=84 EndY=25.3536 EndZ=0
    g10: LineSegment [constr] StartX=30 StartY=5 StartZ=0 EndX=29.5 EndY=5 EndZ=0
    g11: LineSegment [constr] StartX=16.2071 StartY=20 StartZ=0 EndX=14.5 EndY=20 EndZ=0
    g12: LineSegment [constr] StartX=29.5 StartY=5 StartZ=0 EndX=14.5 EndY=20 EndZ=0
    g13: LineSegment [constr] StartX=14.5 StartY=20 StartZ=0 EndX=14.1465 EndY=20.3536 EndZ=0
    g14: LineSegment [constr] StartX=29.5 StartY=5 StartZ=0 EndX=29.1464 EndY=5.35355 EndZ=0
    g15: LineSegment StartX=29.1464 StartY=5.35355 StartZ=0 EndX=14.1465 EndY=20.3536 EndZ=0
    g16: LineSegment [constr] StartX=0 StartY=5 StartZ=0 EndX=0 EndY=15 EndZ=0
    g17: LineSegment StartX=29.1464 StartY=5.35355 StartZ=0 EndX=0 EndY=5.35355 EndZ=0
    g18: LineSegment StartX=0 StartY=5.35355 StartZ=0 EndX=0 EndY=25.3536 EndZ=0
    g19: LineSegment StartX=0 StartY=25.3536 StartZ=0 EndX=84 EndY=25.3536 EndZ=0
    g20: LineSegment StartX=14.1465 StartY=20.3536 StartZ=0 EndX=76.3536 EndY=20.3536 EndZ=0
  constraints (58):
    c: Distance(g0) = 7
    c: Coincident(g0,g-8)
    c: PointOnObject(g0,g-8)
    c: Coincident(g1,g-7)
    c: Coincident(g2,g-6)
    c: Coincident(g2,g1)
    c: Parallel(g2,g-6)
    c: Parallel(g1,g-7)
    c: Distance(g3) = 7
    c: Coincident(g3,g1)
    c: Parallel(g3,g-6)
    c: Distance(g4) = 0.5
    c: Coincident(g4,g0)
    c: Parallel(g-7,g4)
    c: Distance(g5) = 0.5
    c: Coincident(g5,g3)
    c: Parallel(g5,g1)
    c: Coincident(g6,g5)
    c: Coincident(g6,g4)
    c: Distance(g7) = 0.5
    c: Coincident(g7,g-9)
    c: Vertical(g7)
    c: Coincident(g8,g4)
    c: PointOnObject(g8,g7)
    c: Horizontal(g8)
    c: Distance(g9) = 20
    c: Coincident(g9,g8)
    c: Vertical(g9)
    c: Distance(g10) = 0.5
    c: Coincident(g10,g-5)
    c: PointOnObject(g10,g-3)
    c: Coincident(g11,g-6)
    c: Horizontal(g11)
    c: Coincident(g12,g10)
    c: PointOnObject(g12,g11)
    c: Parallel(g12,g-5)
    c: PointOnObject(g11,g12)
    c: Distance(g13) = 0.5
    c: Coincident(g13,g11)
    c: Parallel(g12,g13)
    c: Distance(g14) = 0.5
    c: Coincident(g14,g10)
    c: PointOnObject(g14,g12)
    c: Coincident(g15,g14)
    c: Coincident(g15,g13)
    c: Distance(g16) = 10
    c: Coincident(g16,g-4)
    c: PointOnObject(g16,g-2)
    c: Coincident(g17,g14)
    c: PointOnObject(g17,g16)
    c: Parallel(g17,g-3)
    c: Distance(g18) = 20
    c: Coincident(g18,g17)
    c: PointOnObject(g18,g-2)
    c: Coincident(g19,g18)
    c: Coincident(g19,g9)
    c: Coincident(g20,g13)
    c: Coincident(g20,g5)
FEATURE [PartDesign::Pad] Pad006
  Direction = (0,-1,2e-16)
  Length = 84
  Length2 = 10
  Placement = pos=(0,-84,2e-15) rot=(1,0,0;1.5708rad)
  Profile = -> Sketch008
  ReferenceAxis = -> Sketch008 [N_Axis]
  Refine = true
  Reversed = true
  Suppressed = false
  Type = 0
FEATURE [Sketcher::SketchObject] Sketch009
  ArcFitTolerance = 1e-06
  AttachmentSupport = -> [Pad006]
  ExternalGeometry = -> [Pad006]
  FullyConstrained = true
  MakeInternals = false
  MapMode = 5
  Placement = pos=(84,-84,2e-15) rot=(0.707107,0,0.707107;3.14159rad)
  sketch-geometry (11):
    g0: GeomPoint [constr] X=25.3536 Y=-42 Z=0
    g1: GeomPoint [constr] X=5.35355 Y=-42 Z=0
    g2: LineSegment [constr] StartX=5.35355 StartY=-42 StartZ=0 EndX=25.3536 EndY=-42 EndZ=0
    g3: LineSegment [constr] StartX=5.35355 StartY=-42 StartZ=0 EndX=12.3536 EndY=-42 EndZ=0
    g4: LineSegment [constr] StartX=12.3536 StartY=-42 StartZ=0 EndX=12.3536 EndY=-7.1e-15 EndZ=0
    g5: LineSegment [constr] StartX=12.3536 StartY=-42 StartZ=0 EndX=12.3536 EndY=-84 EndZ=0
    g6: GeomPoint [constr] X=12.3536 Y=-21 Z=0
    g7: GeomPoint [constr] X=12.3536 Y=-63 Z=0
    g8: Circle CenterX=12.3536 CenterY=-21 CenterZ=0 NormalX=0 NormalY=0 NormalZ=1 AngleXU=0 Radius=1.325
    g9: Circle CenterX=12.3536 CenterY=-42 CenterZ=0 NormalX=0 NormalY=0 NormalZ=1 AngleXU=0 Radius=1.325
    g10: Circle CenterX=12.3536 CenterY=-63 CenterZ=0 NormalX=0 NormalY=0 NormalZ=1 AngleXU=0 Radius=1.325
  constraints (21):
    c: Symmetric(g-3,g-3,g0)
    c: Symmetric(g-5,g-5,g1)
    c: Coincident(g2,g1)
    c: Coincident(g2,g0)
    c: Distance(g3) = 7
    c: Coincident(g3,g1)
    c: PointOnObject(g3,g2)
    c: Coincident(g4,g3)
    c: PointOnObject(g4,g-6)
    c: Parallel(g4,g-5)
    c: Coincident(g5,g3)
    c: PointOnObject(g5,g-4)
    c: Vertical(g5)
    c: Symmetric(g4,g4,g6)
    c: Symmetric(g5,g5,g7)
    c: Diameter(g8) = 2.65
    c: Coincident(g8,g6)
    c: Diameter(g9) = 2.65
    c: Coincident(g9,g3)
    c: Diameter(g10) = 2.65
    c: Coincident(g10,g7)
FEATURE [PartDesign::Pocket] Pocket001
  BaseFeature = -> Pad006
  Direction = (-1,0,2e-16)
  Length = 20
  Length2 = 5
  Placement = pos=(0,-84,2e-15) rot=(1,0,0;1.5708rad)
  Profile = -> Sketch009
  ReferenceAxis = -> Sketch009 [N_Axis]
  Refine = true
  Suppressed = false
  Type = 0
FEATURE [Sketcher::SketchObject] Sketch010
  ArcFitTolerance = 1e-06
  AttachmentSupport = -> [Pocket001]
  ExternalGeometry = -> [Pocket001]
  FullyConstrained = true
  MakeInternals = false
  MapMode = 5
  Placement = pos=(7.71195e-08,-84,20.3536) rot=(1,0,0;3.14159rad)
  sketch-geometry (8):
    g0: LineSegment [constr] StartX=14.1465 StartY=0 StartZ=0 EndX=41.9965 EndY=0 EndZ=0
    g1: LineSegment [constr] StartX=41.9965 StartY=0 StartZ=0 EndX=41.9965 EndY=-84 EndZ=0
    g2: GeomPoint [constr] X=41.9965 Y=-42 Z=0
    g3: LineSegment StartX=35.4965 StartY=-47 StartZ=0 EndX=48.4965 EndY=-47 EndZ=0
    g4: LineSegment StartX=48.4965 StartY=-47 StartZ=0 EndX=48.4965 EndY=-37 EndZ=0
    g5: LineSegment StartX=48.4965 StartY=-37 StartZ=0 EndX=35.4965 EndY=-37 EndZ=0
    g6: LineSegment StartX=35.4965 StartY=-37 StartZ=0 EndX=35.4965 EndY=-47 EndZ=0
    g7: GeomPoint [constr] X=41.9965 Y=-42 Z=0
  constraints (19):
    c: Distance(g0) = 27.85
    c: Coincident(g0,g-3)
    c: PointOnObject(g0,g-3)
    c: Coincident(g1,g0)
    c: PointOnObject(g1,g-4)
    c: Vertical(g1)
    c: Symmetric(g1,g1,g2)
    c: Coincident(g3,g4)
    c: Coincident(g4,g5)
    c: Coincident(g5,g6)
    c: Coincident(g6,g3)
    c: Horizontal(g3)
    c: Horizontal(g5)
    c: Vertical(g4)
    c: Vertical(g6)
    c: Symmetric(g5,g3,g7)
    c: Distance(g4,g6) = 13
    c: Distance(g3,g5) = 10
    c: Coincident(g7,g2)
FEATURE [PartDesign::Pocket] Pocket002
  BaseFeature = -> Pocket001
  Direction = (3.78899e-09,0,1)
  Length = 0.5
  Length2 = 5
  Placement = pos=(0,-84,2e-15) rot=(1,0,0;1.5708rad)
  Profile = -> Sketch010
  ReferenceAxis = -> Sketch010 [N_Axis]
  Refine = true
  Suppressed = false
  Type = 0
FEATURE [Sketcher::SketchObject] Sketch011
  ArcFitTolerance = 1e-06
  AttachmentSupport = -> [Pocket002]
  FullyConstrained = true
  MakeInternals = false
  MapMode = 5
  Placement = pos=(7.9014e-08,-84,20.8536) rot=(1,0,0;3.14159rad)
  sketch-geometry (2):
    g0: LineSegment [constr] StartX=41.9965 StartY=-37 StartZ=0 EndX=41.9965 EndY=-47 EndZ=0
    g1: Circle CenterX=41.9965 CenterY=-42 CenterZ=0 NormalX=0 NormalY=0 NormalZ=1 AngleXU=0 Radius=1.55
  constraints (4):
    c: Symmetric(g-3,g-3,g0)
    c: Symmetric(g-5,g-5,g0)
    c: Diameter(g1) = 3.1
    c: Symmetric(g0,g0,g1)
FEATURE [PartDesign::Pocket] Pocket003
  BaseFeature = -> Pocket002
  Direction = (3.78899e-09,0,1)
  Length = 5
  Length2 = 5
  Placement = pos=(0,-84,2e-15) rot=(1,0,0;1.5708rad)
  Profile = -> Sketch011
  ReferenceAxis = -> Sketch011 [N_Axis]
  Refine = true
  Suppressed = false
  Type = 0
FEATURE [Sketcher::SketchObject] Sketch012
  ArcFitTolerance = 1e-06
  AttachmentSupport = -> [Pocket003]
  ExternalGeometry = -> [Pocket003]
  FullyConstrained = true
  MakeInternals = false
  MapMode = 5
  Placement = pos=(7.11416e-08,-84,25.3536) rot=(0,0,1;3.14159rad)
  sketch-geometry (20):
    g0: LineSegment [constr] StartX=-84 StartY=1.42e-14 StartZ=0 EndX=-84 EndY=-5 EndZ=0
    g1: LineSegment [constr] StartX=-84 StartY=-5 StartZ=0 EndX=-79 EndY=-5 EndZ=0
    g2: LineSegment [constr] StartX=-79 StartY=-5 StartZ=0 EndX=-79 EndY=1.42e-14 EndZ=0
    g3: LineSegment [constr] StartX=-79 StartY=1.42e-14 StartZ=0 EndX=-84 EndY=1.42e-14 EndZ=0
    g4: LineSegment [constr] StartX=-84 StartY=-84 StartZ=0 EndX=-79 EndY=-84 EndZ=0
    g5: LineSegment [constr] StartX=-79 StartY=-84 StartZ=0 EndX=-79 EndY=-79 EndZ=0
    g6: LineSegment [constr] StartX=-79 StartY=-79 StartZ=0 EndX=-84 EndY=-79 EndZ=0
    g7: LineSegment [constr] StartX=-84 StartY=-79 StartZ=0 EndX=-84 EndY=-84 EndZ=0
    g8: LineSegment [constr] StartX=0 StartY=0 StartZ=0 EndX=-5 EndY=0 EndZ=0
    g9: LineSegment [constr] StartX=-5 StartY=0 StartZ=0 EndX=-5 EndY=-5 EndZ=0
    g10: LineSegment [constr] StartX=-5 StartY=-5 StartZ=0 EndX=0 EndY=-5 EndZ=0
    g11: LineSegment [constr] StartX=0 StartY=-5 StartZ=0 EndX=0 EndY=0 EndZ=0
    g12: LineSegment [constr] StartX=7.11416e-08 StartY=-84 StartZ=0 EndX=7.11416e-08 EndY=-79 EndZ=0
    g13: LineSegment [constr] StartX=7.11416e-08 StartY=-79 StartZ=0 EndX=-5 EndY=-79 EndZ=0
    g14: LineSegment [constr] StartX=-5 StartY=-79 StartZ=0 EndX=-5 EndY=-84 EndZ=0
    g15: LineSegment [constr] StartX=-5 StartY=-84 StartZ=0 EndX=7.11416e-08 EndY=-84 EndZ=0
    g16: Circle CenterX=-79 CenterY=-5 CenterZ=0 NormalX=0 NormalY=0 NormalZ=1 AngleXU=0 Radius=1.35
    g17: Circle CenterX=-79 CenterY=-79 CenterZ=0 NormalX=0 NormalY=0 NormalZ=1 AngleXU=0 Radius=1.35
    g18: Circle CenterX=-5 CenterY=-79 CenterZ=0 NormalX=0 NormalY=0 NormalZ=1 AngleXU=0 Radius=1.35
    g19: Circle CenterX=-5 CenterY=-5 CenterZ=0 NormalX=0 NormalY=0 NormalZ=1 AngleXU=0 Radius=1.35
  constraints (52):
    c: Coincident(g0,g1)
    c: Coincident(g1,g2)
    c: Coincident(g2,g3)
    c: Coincident(g3,g0)
    c: Vertical(g0)
    c: Vertical(g2)
    c: Horizontal(g1)
    c: Horizontal(g3)
    c: Distance(g0,g2) = 5
    c: Distance(g1,g3) = 5
    c: Coincident(g0,g-4)
    c: Coincident(g4,g5)
    c: Coincident(g5,g6)
    c: Coincident(g6,g7)
    c: Coincident(g7,g4)
    c: Horizontal(g4)
    c: Horizontal(g6)
    c: Vertical(g5)
    c: Vertical(g7)
    c: Distance(g5,g7) = 5
    c: Distance(g4,g6) = 5
    c: Coincident(g4,g-6)
    c: Coincident(g8,g9)
    c: Coincident(g9,g10)
    c: Coincident(g10,g11)
    c: Coincident(g11,g8)
    c: Horizontal(g8)
    c: Horizontal(g10)
    c: Vertical(g9)
    c: Vertical(g11)
    c: Distance(g9,g11) = 5
    c: Distance(g8,g10) = 5
    c: Coincident(g8,g-1)
    c: Coincident(g12,g13)
    c: Coincident(g13,g14)
    c: Coincident(g14,g15)
    c: Coincident(g15,g12)
    c: Vertical(g12)
    c: Vertical(g14)
    c: Horizontal(g13)
    c: Horizontal(g15)
    c: Distance(g12,g14) = 5
    c: Distance(g13,g15) = 5
    c: Coincident(g12,g-6)
    c: Diameter(g16) = 2.7
    c: Coincident(g16,g1)
    c: Diameter(g17) = 2.7
    c: Coincident(g17,g5)
    c: Diameter(g18) = 2.7
    c: Coincident(g18,g13)
    c: Diameter(g19) = 2.7
    c: Coincident(g19,g9)
FEATURE [PartDesign::Pocket] Pocket004
  BaseFeature = -> Pocket003
  Direction = (-2.80598e-09,0,-1)
  Length = 5
  Length2 = 5
  Placement = pos=(0,-84,2e-15) rot=(1,0,0;1.5708rad)
  Profile = -> Sketch012
  ReferenceAxis = -> Sketch012 [N_Axis]
  Refine = true
  Suppressed = false
  Type = 0
FEATURE [Sketcher::SketchObject] Sketch013
  ArcFitTolerance = 1e-06
  AttachmentSupport = -> [Pocket004]
  ExternalGeometry = -> [Pocket004]
  FullyConstrained = true
  MakeInternals = false
  MapMode = 5
  Placement = pos=(7.11416e-08,-84,25.3536) rot=(0,0,1;3.14159rad)
  sketch-geometry (4):
    g0: LineSegment [constr] StartX=7.11416e-08 StartY=-42 StartZ=0 EndX=-5 EndY=-42 EndZ=0
    g1: Circle CenterX=-5 CenterY=-42 CenterZ=0 NormalX=0 NormalY=0 NormalZ=1 AngleXU=0 Radius=1.35
    g2: LineSegment [constr] StartX=-84 StartY=-42 StartZ=0 EndX=-79 EndY=-42 EndZ=0
    g3: Circle CenterX=-79 CenterY=-42 CenterZ=0 NormalX=0 NormalY=0 NormalZ=1 AngleXU=0 Radius=1.35
  constraints (10):
    c: Distance(g0) = 5
    c: Symmetric(g-3,g-3,g0)
    c: Horizontal(g0)
    c: Diameter(g1) = 2.7
    c: Coincident(g1,g0)
    c: Distance(g2) = 5
    c: Symmetric(g-4,g-4,g2)
    c: Horizontal(g2)
    c: Diameter(g3) = 2.7
    c: Coincident(g3,g2)
FEATURE [PartDesign::Pocket] Pocket005
  BaseFeature = -> Pocket004
  Direction = (-2.80598e-09,0,-1)
  Length = 22
  Length2 = 5
  Placement = pos=(0,-84,2e-15) rot=(1,0,0;1.5708rad)
  Profile = -> Sketch013
  ReferenceAxis = -> Sketch013 [N_Axis]
  Refine = true
  Suppressed = false
  Type = 0
FEATURE [PartDesign::ShapeBinder] CopyPocket005
  Placement = pos=(0,-84,2e-15) rot=(1,0,0;1.5708rad)
  TraceSupport = false
FEATURE [PartDesign::Plane] DatumPlane005
  AttachmentSupport = -> [CopyPocket005]
  Length = 91.117
  MapMode = 5
  Placement = pos=(7.9014e-08,-84,20.8536) rot=(1,0,0;3.14159rad)
  ResizeMode = 0
  Width = 126.87
FEATURE [Sketcher::SketchObject] Sketch014
  ArcFitTolerance = 1e-06
  AttachmentSupport = -> [DatumPlane005]
  FullyConstrained = true
  MakeInternals = false
  MapMode = 5
  Placement = pos=(7.9014e-08,-84,20.8536) rot=(1,0,0;3.14159rad)
  sketch-geometry (6):
    g0: Circle CenterX=41.9965 CenterY=-42 CenterZ=0 NormalX=0 NormalY=0 NormalZ=1 AngleXU=0 Radius=1.35
    g1: LineSegment StartX=35.7465 StartY=-46.75 StartZ=0 EndX=48.2465 EndY=-46.75 EndZ=0
    g2: LineSegment StartX=48.2465 StartY=-46.75 StartZ=0 EndX=48.2465 EndY=-37.25 EndZ=0
    g3: LineSegment StartX=48.2465 StartY=-37.25 StartZ=0 EndX=35.7465 EndY=-37.25 EndZ=0
    g4: LineSegment StartX=35.7465 StartY=-37.25 StartZ=0 EndX=35.7465 EndY=-46.75 EndZ=0
    g5: GeomPoint [constr] X=41.9965 Y=-42 Z=0
  constraints (14):
    c: Diameter(g0) = 2.7
    c: Coincident(g0,g-4)
    c: Coincident(g1,g2)
    c: Coincident(g2,g3)
    c: Coincident(g3,g4)
    c: Coincident(g4,g1)
    c: Horizontal(g1)
    c: Horizontal(g3)
    c: Vertical(g2)
    c: Vertical(g4)
    c: Symmetric(g3,g1,g5)
    c: Distance(g2,g4) = 12.5
    c: Distance(g1,g3) = 9.5
    c: Coincident(g5,g0)
FEATURE [PartDesign::Pad] Pad007
  Direction = (-3.78899e-09,0,-1)
  Length = 3
  Length2 = 10
  Placement = pos=(7.9014e-08,-84,20.8536) rot=(1,0,0;3.14159rad)
  Profile = -> Sketch014
  ReferenceAxis = -> Sketch014 [N_Axis]
  Refine = true
  Suppressed = false
  Type = 0
FEATURE [Sketcher::SketchObject] Sketch015
  ArcFitTolerance = 1e-06
  AttachmentSupport = -> [Pad007]
  ExternalGeometry = -> [Pad007]
  FullyConstrained = true
  MakeInternals = false
  MapMode = 5
  Placement = pos=(6.7647e-08,-84,17.8536) rot=(1,0,0;3.14159rad)
  sketch-geometry (4):
    g0: LineSegment StartX=35.7465 StartY=-37.25 StartZ=0 EndX=35.7465 EndY=-46.75 EndZ=0
    g1: LineSegment StartX=35.7465 StartY=-46.75 StartZ=0 EndX=48.2465 EndY=-46.75 EndZ=0
    g2: LineSegment StartX=48.2465 StartY=-46.75 StartZ=0 EndX=48.2465 EndY=-37.25 EndZ=0
    g3: LineSegment StartX=48.2465 StartY=-37.25 StartZ=0 EndX=35.7465 EndY=-37.25 EndZ=0
  constraints (10):
    c: Coincident(g0,g1)
    c: Coincident(g1,g2)
    c: Coincident(g2,g3)
    c: Coincident(g3,g0)
    c: Vertical(g0)
    c: Vertical(g2)
    c: Horizontal(g1)
    c: Horizontal(g3)
    c: Coincident(g0,g-6)
    c: Coincident(g1,g-5)
FEATURE [PartDesign::Pad] Pad008
  BaseFeature = -> Pad007
  Direction = (-3.78899e-09,0,-1)
  Length = 8
  Length2 = 10
  Placement = pos=(7.9014e-08,-84,20.8536) rot=(1,0,0;3.14159rad)
  Profile = -> Sketch015
  ReferenceAxis = -> Sketch015 [N_Axis]
  Refine = true
  Suppressed = false
  Type = 0
FEATURE [Sketcher::SketchObject] Sketch016
  ArcFitTolerance = 1e-06
  AttachmentSupport = -> [Pad008]
  ExternalGeometry = -> [Pad008]
  FullyConstrained = true
  MakeInternals = false
  MapMode = 5
  Placement = pos=(7.9014e-08,-46.75,20.8536) rot=(0,0.707107,-0.707107;3.14159rad)
  sketch-geometry (2):
    g0: LineSegment [constr] StartX=-41.9965 StartY=0 StartZ=0 EndX=-41.9965 EndY=7 EndZ=0
    g1: Circle CenterX=-41.9965 CenterY=7 CenterZ=0 NormalX=0 NormalY=0 NormalZ=1 AngleXU=0 Radius=2.5
  constraints (5):
    c: Distance(g0) = 7
    c: Symmetric(g-6,g-6,g0)
    c: Vertical(g0)
    c: Diameter(g1) = 5
    c: Coincident(g1,g0)
FEATURE [PartDesign::Hole] Hole001
  BaseFeature = -> Pad008
  CustomThreadClearance = 0
  Depth = 12.72
  DepthType = 0
  Diameter = 4.2
  DrillForDepth = false
  DrillPoint = 1
  DrillPointAngle = 118
  HoleCutCountersinkAngle = 90
  HoleCutCustomValues = false
  HoleCutDepth = 0
  HoleCutDiameter = 6.1
  HoleCutType = 0
  ModelThread = false
  Placement = pos=(7.9014e-08,-84,20.8536) rot=(1,0,0;3.14159rad)
  Profile = -> Sketch016
  Refine = true
  Suppressed = false
  Tapered = false
  TaperedAngle = 90
  ThreadClass = 0
  ThreadDepth = 12.72
  ThreadDepthType = 0
  ThreadDirection = 0
  ThreadFit = 0
  ThreadSize = 13
  ThreadType = 1
  Threaded = true
  UseCustomThreadClearance = false
FEATURE [Sketcher::SketchObject] Sketch017
  ArcFitTolerance = 1e-06
  AttachmentSupport = -> [Hole001]
  ExternalGeometry = -> [Hole001]
  FullyConstrained = true
  MakeInternals = false
  MapMode = 5
  Placement = pos=(7.9014e-08,-46.75,20.8536) rot=(0,0.707107,-0.707107;3.14159rad)
  sketch-geometry (4):
    g0: LineSegment [constr] StartX=-48.2465 StartY=0 StartZ=0 EndX=-48.2465 EndY=2.5 EndZ=0
    g1: LineSegment [constr] StartX=-35.7465 StartY=0 StartZ=0 EndX=-35.7465 EndY=2.5 EndZ=0
    g2: Circle CenterX=-48.2465 CenterY=2.5 CenterZ=0 NormalX=0 NormalY=0 NormalZ=1 AngleXU=0 Radius=1
    g3: Circle CenterX=-35.7465 CenterY=2.5 CenterZ=0 NormalX=0 NormalY=0 NormalZ=1 AngleXU=0 Radius=1
  constraints (10):
    c: Distance(g0) = 2.5
    c: Coincident(g0,g-6)
    c: PointOnObject(g0,g-3)
    c: Distance(g1) = 2.5
    c: Coincident(g1,g-6)
    c: PointOnObject(g1,g-5)
    c: Diameter(g2) = 2
    c: Coincident(g2,g0)
    c: Diameter(g3) = 2
    c: Coincident(g3,g1)
FEATURE [PartDesign::Pocket] Pocket006
  BaseFeature = -> Hole001
  Direction = (0,1,2e-16)
  Length = 10
  Length2 = 5
  Placement = pos=(7.9014e-08,-84,20.8536) rot=(1,0,0;3.14159rad)
  Profile = -> Sketch017
  ReferenceAxis = -> Sketch017 [N_Axis]
  Refine = true
  Suppressed = false
  Type = 0
FEATURE [PartDesign::Chamfer] Chamfer013
  Angle = 45
  Base = -> Pocket006 [Edge30,Edge29]
  BaseFeature = -> Pocket006
  ChamferType = 0
  FlipDirection = false
  Placement = pos=(7.9014e-08,-84,20.8536) rot=(1,0,0;3.14159rad)
  Refine = true
  Size = 3
  Size2 = 1
  SupportTransform = false
  Suppressed = false
  UseAllEdges = false
FEATURE [PartDesign::Body] Body003  label="PlateThreadBlock OLD"
  AllowCompound = false
  Group = -> [DatumPlane005,CopyPocket005,Sketch014,Pad007,Sketch015,Pad008,Sketch016,Hole001,Sketch017,Pocket006,Chamfer013]
  Origin = -> Origin003
  Tip = -> Chamfer013
FEATURE [PartDesign::FeatureBase] Clone
  BaseFeature = -> Body003
  Suppressed = false
FEATURE [Sketcher::SketchObject] Sketch018
  ArcFitTolerance = 1e-06
  AttachmentSupport = -> [Clone]
  ExternalGeometry = -> [Clone]
  FullyConstrained = true
  MakeInternals = false
  MapMode = 5
  Placement = pos=(0,-46.75,0) rot=(1,0,0;1.5708rad)
  sketch-geometry (1):
    g0: Circle CenterX=41.9965 CenterY=13.8536 CenterZ=0 NormalX=0 NormalY=0 NormalZ=1 AngleXU=0 Radius=2.5
  constraints (2):
    c: Diameter(g0) = 5
    c: Coincident(g0,g-3)
FEATURE [PartDesign::Hole] Hole002
  BaseFeature = -> Clone
  CustomThreadClearance = 0.2
  Depth = 25
  DepthType = 0
  Diameter = 5.2
  DrillForDepth = false
  DrillPoint = 1
  DrillPointAngle = 118
  HoleCutCountersinkAngle = 90
  HoleCutCustomValues = false
  HoleCutDepth = 0
  HoleCutDiameter = 6.1
  HoleCutType = 0
  ModelThread = true
  Profile = -> Sketch018
  Refine = true
  Suppressed = false
  Tapered = false
  TaperedAngle = 90
  ThreadClass = 0
  ThreadDepth = 25
  ThreadDepthType = 0
  ThreadDirection = 0
  ThreadFit = 0
  ThreadSize = 14
  ThreadType = 1
  Threaded = true
  UseCustomThreadClearance = true
FEATURE [PartDesign::ShapeBinder] ShapeBinder003
  Placement = pos=(0,-84,2e-14) rot=(1,0,0;1.5708rad)
  Support = -> [Fillet]
  TraceSupport = false
FEATURE [PartDesign::Plane] DatumPlane006
  AttachmentSupport = -> [ShapeBinder003]
  Length = 61.997
  MapMode = 11
  Placement = pos=(42,-84,14) rot=(0.57735,-0.57735,0.57735;2.0944rad)
  ResizeMode = 0
  Width = 83.9605
FEATURE [Sketcher::SketchObject] Sketch019
  ArcFitTolerance = 1e-06
  AttachmentSupport = -> [DatumPlane006]
  ExternalGeometry = -> [ShapeBinder003]
  FullyConstrained = true
  MakeInternals = false
  MapMode = 5
  Placement = pos=(42,-84,14) rot=(0.57735,-0.57735,0.57735;2.0944rad)
  sketch-geometry (1):
    g0: Circle CenterX=0 CenterY=0 CenterZ=0 NormalX=0 NormalY=0 NormalZ=1 AngleXU=0 Radius=2.9
  constraints (2):
    c: Diameter(g0) = 5.8
    c: Coincident(g0,g-1)
FEATURE [PartDesign::Pad] Pad009
  Direction = (0,-1,0)
  Length = 5
  Length2 = 10
  Placement = pos=(42,-84,14) rot=(0.57735,-0.57735,0.57735;2.0944rad)
  Profile = -> Sketch019
  ReferenceAxis = -> Sketch019 [N_Axis]
  Refine = true
  Reversed = true
  Suppressed = false
  Type = 0
FEATURE [Sketcher::SketchObject] Sketch020
  ArcFitTolerance = 1e-06
  AttachmentSupport = -> [Pad009]
  ExternalGeometry = -> [Pad009]
  FullyConstrained = true
  MakeInternals = false
  MapMode = 5
  Placement = pos=(42,-84,14) rot=(0.57735,-0.57735,0.57735;2.0944rad)
  sketch-geometry (1):
    g0: Circle CenterX=0 CenterY=0 CenterZ=0 NormalX=0 NormalY=0 NormalZ=1 AngleXU=0 Radius=3
  constraints (2):
    c: Diameter(g0) = 6
    c: Coincident(g0,g-1)
FEATURE [PartDesign::Pad] Pad010
  BaseFeature = -> Pad009
  Direction = (0,-1,0)
  Length = 15
  Length2 = 10
  Placement = pos=(42,-84,14) rot=(0.57735,-0.57735,0.57735;2.0944rad)
  Profile = -> Sketch020
  ReferenceAxis = -> Sketch020 [N_Axis]
  Refine = true
  Suppressed = false
  Type = 0
FEATURE [Sketcher::SketchObject] Sketch021
  ArcFitTolerance = 1e-06
  AttachmentSupport = -> [Pad010]
  ExternalGeometry = -> [Pad010]
  FullyConstrained = true
  MakeInternals = false
  MapMode = 5
  Placement = pos=(42,-99,14) rot=(0.57735,-0.57735,0.57735;2.0944rad)
  sketch-geometry (1):
    g0: Circle CenterX=0 CenterY=0 CenterZ=0 NormalX=0 NormalY=0 NormalZ=1 AngleXU=0 Radius=7.5
  constraints (2):
    c: Diameter(g0) = 15
    c: Coincident(g0,g-1)
FEATURE [PartDesign::Pad] Pad011
  BaseFeature = -> Pad010
  Direction = (0,-1,0)
  Length = 20
  Length2 = 10
  Placement = pos=(42,-84,14) rot=(0.57735,-0.57735,0.57735;2.0944rad)
  Profile = -> Sketch021
  ReferenceAxis = -> Sketch021 [N_Axis]
  Refine = true
  Suppressed = false
  Type = 0
FEATURE [Sketcher::SketchObject] Sketch022
  ArcFitTolerance = 1e-06
  AttachmentSupport = -> [Pad011]
  ExternalGeometry = -> [Pad011]
  FullyConstrained = true
  MakeInternals = false
  MapMode = 5
  Placement = pos=(42,-119,14) rot=(0.57735,-0.57735,0.57735;2.0944rad)
  sketch-geometry (17):
    g0: LineSegment [constr] StartX=-5.29923e-11 StartY=5.2929e-11 StartZ=0 EndX=-5.29923e-11 EndY=7.5 EndZ=0
    g1: LineSegment [constr] StartX=-5.29923e-11 StartY=5.2929e-11 StartZ=0 EndX=7.5 EndY=5.2929e-11 EndZ=0
    g2: LineSegment [constr] StartX=-5.29923e-11 StartY=5.2929e-11 StartZ=0 EndX=-5.29923e-11 EndY=-7.5 EndZ=0
    g3: LineSegment [constr] StartX=-5.29923e-11 StartY=5.2929e-11 StartZ=0 EndX=-7.5 EndY=5.2929e-11 EndZ=0
    g4: LineSegment [constr] StartX=-5.29923e-11 StartY=5.2929e-11 StartZ=0 EndX=-5.3033 EndY=5.3033 EndZ=0
    g5: LineSegment [constr] StartX=-5.29923e-11 StartY=5.2929e-11 StartZ=0 EndX=5.3033 EndY=5.3033 EndZ=0
    g6: LineSegment [constr] StartX=-5.29923e-11 StartY=5.2929e-11 StartZ=0 EndX=5.3033 EndY=-5.3033 EndZ=0
    g7: LineSegment [constr] StartX=-5.29923e-11 StartY=5.2929e-11 StartZ=0 EndX=-5.3033 EndY=-5.3033 EndZ=0
    g8: Circle CenterX=-5.3033 CenterY=5.3033 CenterZ=0 NormalX=0 NormalY=0 NormalZ=1 AngleXU=0 Radius=1.34e-13
    g9: Circle CenterX=-5.3033 CenterY=5.3033 CenterZ=0 NormalX=0 NormalY=0 NormalZ=1 AngleXU=0 Radius=1.75
    g10: Circle CenterX=-7.5 CenterY=5.2929e-11 CenterZ=0 NormalX=0 NormalY=0 NormalZ=1 AngleXU=0 Radius=1.75
    g11: Circle CenterX=-5.3033 CenterY=-5.3033 CenterZ=0 NormalX=0 NormalY=0 NormalZ=1 AngleXU=0 Radius=1.75
    g12: Circle CenterX=-5.29923e-11 CenterY=-7.5 CenterZ=0 NormalX=0 NormalY=0 NormalZ=1 AngleXU=0 Radius=1.75
    g13: Circle CenterX=5.3033 CenterY=-5.3033 CenterZ=0 NormalX=0 NormalY=0 NormalZ=1 AngleXU=0 Radius=1.75
    g14: Circle CenterX=7.5 CenterY=5.2929e-11 CenterZ=0 NormalX=0 NormalY=0 NormalZ=1 AngleXU=0 Radius=1.75
    g15: Circle CenterX=5.3033 CenterY=5.3033 CenterZ=0 NormalX=0 NormalY=0 NormalZ=1 AngleXU=0 Radius=1.75
    g16: Circle CenterX=-5.29923e-11 CenterY=7.5 CenterZ=0 NormalX=0 NormalY=0 NormalZ=1 AngleXU=0 Radius=1.75
  constraints (42):
    c: Coincident(g0,g-1)
    c: PointOnObject(g0,g-3)
    c: Vertical(g0)
    c: Coincident(g1,g0)
    c: PointOnObject(g1,g-3)
    c: Horizontal(g1)
    c: Coincident(g2,g0)
    c: PointOnObject(g2,g-3)
    c: Vertical(g2)
    c: Coincident(g3,g0)
    c: PointOnObject(g3,g-3)
    c: Horizontal(g3)
    c: Angle(g-1,g4) = 2.35619
    c: Coincident(g4,g0)
    c: PointOnObject(g4,g-3)
    c: Angle(g-1,g5) = 0.785398
    c: Coincident(g5,g0)
    c: PointOnObject(g5,g-3)
    c: Angle(g-1,g6) = -0.785398
    c: Coincident(g6,g0)
    c: PointOnObject(g6,g-3)
    c: Angle(g-1,g7) = -2.35619
    c: Coincident(g7,g0)
    c: PointOnObject(g7,g-3)
    c: Coincident(g8,g4)
    c: Tangent(g8,g-3)
    c: Diameter(g9) = 3.5
    c: Coincident(g9,g4)
    c: Diameter(g10) = 3.5
    c: Coincident(g10,g3)
    c: Diameter(g11) = 3.5
    c: Coincident(g11,g7)
    c: Diameter(g12) = 3.5
    c: Coincident(g12,g2)
    c: Diameter(g13) = 3.5
    c: Coincident(g13,g6)
    c: Diameter(g14) = 3.5
    c: Coincident(g14,g1)
    c: Diameter(g15) = 3.5
    c: Coincident(g15,g5)
    c: Diameter(g16) = 3.5
    c: Coincident(g16,g0)
FEATURE [PartDesign::Pocket] Pocket007
  BaseFeature = -> Pad011
  Direction = (0,1,0)
  Length = 50
  Length2 = 5
  Placement = pos=(42,-84,14) rot=(0.57735,-0.57735,0.57735;2.0944rad)
  Profile = -> Sketch022
  ReferenceAxis = -> Sketch022 [N_Axis]
  Refine = true
  Suppressed = false
  Type = 1
FEATURE [PartDesign::Fillet] Fillet004
  Base = -> Pocket007 [Edge23]
  BaseFeature = -> Pocket007
  Placement = pos=(42,-84,14) rot=(0.57735,-0.57735,0.57735;2.0944rad)
  Radius = 4
  Refine = true
  SupportTransform = false
  Suppressed = false
  UseAllEdges = false
FEATURE [PartDesign::Point] DatumPoint
  AttacherType = Attacher::AttachEnginePoint
  AttachmentSupport = -> [Fillet004]
  MapMode = 36
  Placement = pos=(42,-79,14) rot=(0.707107,0,0.707107;3.14159rad)
FEATURE [Part::Part2DObjectPython] VThreadProfile  # Draft 2D object (typed FeaturePython)
  Area = 21.5626
  Closed = true
  Continuity = C2
  Deviation = 0.1
  Height = 74
  Helix = Helix
  Instructions = Expand this with the ... button to view instructions | Sweep this object along a helix of the same pitch to produce your thread. | It is recommended to make the helix in the ThreadProfile workbench. | If there is an active Body the ThreadProfile object will be put into it.,If not it can be dragged and dropped into the body later. | If there is an active Body when the helix is made there will be made a ShapeBinder for it | For internal threads you will need to cut the Sweep object out of a cylinder, or if using Part Design sweep it as a Subtractive Pipe. | Always use Frenet mode | I have provided some presets, but it is possible there could be some errors.  Double check for mission critical applications. | Also, the tolerances might be different from what you wish to have.  I believe the internal minor diameters are all minimum and the external are all maximum.
  InternalOrExternal = 1
  MakeFace = true
  MinorDiameter = 4.773
  Parameterization = 1
  Pitch = 1
  Placement = pos=(42,-79,14) rot=(1,0,0;-1.5708rad)
  Points = (66) [(2.37314,0.228827,0),(2.31975,0.451556,0),(2.25136,0.667864,0),(2.16643,0.876642,0),(2.06474,1.07659,0),(1.94661,1.26636,0),(1.81267,1.44463,0),+59 more]
  Presets = 16
  Quality = 11
  ThreadCount = 74
  Variants = 0
  Version = 1.92
  external2S_data = [-0.00461051,-0.00886426,-0.0128148,-0.0165028,-0.0199596,-0.0232105,-0.0262759,-0.0291725,-0.0319145,-0.0345137,-0.0369805,-0.0393235,-0.0415505,-0.0436681,-0.0456823,-0.0475981,-0.0494204,-0.0511532,-0.0528003,-0.0543649,-0.0558502,+698 more]
  external3S_data = [-0.00677828,-0.0128149,-0.0182584,-0.0232106,-0.0277444,-0.0319145,-0.0357632,-0.0393236,-0.0426227,-0.0456823,-0.0485208,-0.0511533,-0.0535928,-0.0558503,-0.0579353,-0.059856,-0.0616195,-0.0632319,-0.0646984,-0.0660239,-0.0672123,+698 more]
  external45_data = [-0.00137363,-0.00271738,-0.00403219,-0.00531893,-0.00657844,-0.00781148,-0.00901878,-0.010201,-0.0113589,-0.012493,-0.0136039,-0.0146921,-0.0157583,-0.0168028,-0.0178261,-0.0188288,-0.0198112,-0.0207738,-0.0217169,-0.0226409,-0.0235462,+698 more]
  external_data = [-0.00235387,-0.00461052,-0.00677828,-0.00886428,-0.0108747,-0.0128149,-0.0146895,-0.0165028,-0.0182584,-0.0199597,-0.0216095,-0.0232106,-0.0247653,-0.0262759,-0.0277444,-0.0291725,-0.0305621,-0.0319145,-0.0332313,-0.0345138,-0.0357632,+698 more]
  internal2S_data = [0,0,0,0,0,0,0,0,0,0,0,0,0,0,0,0,0,0,0,0,0,0,0,0,0,0,0,0,0,0,0,0,0,0,0,0,0,0,0,0,0,0,0,0,0,0,0,0,0,0,0,0,0,0,0,0,0,0,0,0,0,0,0,0,0,0,0,0,0,0,0,0,0,0,0,0,0,0,0,0,0,0,0,0,0,0,0,0,0,0,0.00481128,0.00962256,0.0144338,0.0192451,0.0240564,+624 more]
  internal3S_data = [0,0,0,0,0,0,0,0,0,0,0,0,0,0,0,0,0,0,0,0,0,0,0,0,0,0,0,0,0,0,0,0,0,0,0,0,0,0,0,0,0,0,0,0,0,0,0,0,0,0,0,0,0,0,0,0,0,0,0,0,0.00721688,0.0144338,0.0216506,0.0288675,0.0360844,0.0433013,0.0505181,0.057735,0.0649519,0.0721688,0.0793857,0.0866025,+647 more]
  internal45_data = [0,0,0,0,0,0,0,0,0,0,0,0,0,0,0,0,0,0,0,0,0,0,0,0,0,0,0,0,0,0,0,0,0,0,0,0,0,0,0,0,0,0,0,0,0,0,0,0,0,0,0,0,0,0,0,0,0,0,0,0,0,0,0,0,0,0,0,0,0,0,0,0,0,0,0,0,0,0,0,0,0,0,0,0,0,0,0,0,0,0,0,0,0,0,0,0,0,0,0,0,0,0,0,0,0,0,0,0,0,0,0,0,0,0,0,0,0,0,0,0,+599 more]
  internal_data = [0,0,0,0,0,0,0,0,0,0,0,0,0,0,0,0,0,0,0,0,0,0,0,0,0,0,0,0,0,0,0,0,0,0,0,0,0,0,0,0,0,0,0,0,0,0,0,0,0,0,0,0,0,0,0,0,0,0,0,0,0,0,0,0,0,0,0,0,0,0,0,0,0,0,0,0,0,0,0,0,0,0,0,0,0,0,0,0,0,0,0,0,0,0,0,0,0,0,0,0,0,0,0,0,0,0,0,0,0,0,0,0,0,0,0,0,0,0,0,0,+599 more]
  preset_names = <blob: 3959 chars omitted>
  presets_data = [0,0,0,2.20878,24.1173,24.6888,0.25,0.693,0.729,0.25,0.793,0.829,0.25,0.893,0.929,0.3,1.032,1.075,0.35,1.171,1.221,0.35,1.371,1.421,0.4,1.509,1.567,0.45,1.648,1.713,0.45,1.948,2.013,0.5,2.387,2.459,0.6,2.764,2.85,0.7,3.141,3.242,0.75,3.58,+712 more]
FEATURE [Part::Helix] Helix
  Angle = 0
  AttacherType = Attacher::AttachEngine3D
  Height = 74
  Length = 470.808
  LocalCoord = 0
  Pitch = 1
  Placement = pos=(42,-79,14) rot=(1,0,0;-1.5708rad)
  Radius = 1
  SegmentLength = 1
  Style = 0
  expr: AttachmentOffset = VThreadProfile.AttachmentOffset
  expr: AttachmentSupport = VThreadProfile.AttachmentSupport
  expr: Height = VThreadProfile.ThreadCount * VThreadProfile.Pitch
  expr: MapMode = VThreadProfile.MapMode
  expr: MapPathParameter = VThreadProfile.MapPathParameter
  expr: MapReversed = VThreadProfile.MapReversed
  expr: Pitch = VThreadProfile.Pitch
  expr: SegmentLength = 1
FEATURE [PartDesign::AdditivePipe] AdditivePipe
  AuxilleryCurvelinear = true
  AuxillerySpineTangent = false
  BaseFeature = -> Fillet004
  Binormal = (0,0,0)
  Mode = 2
  Placement = pos=(42,-84,14) rot=(0.57735,-0.57735,0.57735;2.0944rad)
  Profile = -> VThreadProfile
  Refine = true
  Spine = -> Helix [Edge1,Edge2,Edge3,Edge4,Edge5,Edge6,Edge7,Edge8,Edge9,Edge10,Edge11,Edge12,Edge13,Edge14,Edge15,Edge16,Edge17,Edge18,Edge19,Edge20,Edge21,Edge22,Edge23,Edge24,Edge25,Edge26,Edge27,Edge28,Edge29,Edge30,Edge31,Edge32,Edge33,Edge34,Edge35,Edge36,Edge37,Edge38,Edge39,Edge40,+34 more]
  SpineTangent = false
  Suppressed = false
  Transformation = 0
  Transition = 0
FEATURE [PartDesign::ShapeBinder] ShapeBinder004
  Support = -> [Fillet]
  TraceSupport = false
FEATURE [PartDesign::Plane] DatumPlane007
  AttachmentSupport = -> [AdditivePipe]
  Length = 61.9972
  MapMode = 5
  Placement = pos=(42.0014,-4.99998,14) rot=(0.577354,0.577344,0.577354;4.18878rad)
  ResizeMode = 0
  Width = 83.9633
FEATURE [Sketcher::SketchObject] Sketch023
  ArcFitTolerance = 1e-06
  AttachmentSupport = -> [DatumPlane007]
  FullyConstrained = true
  MakeInternals = false
  MapMode = 5
  Placement = pos=(42.0014,-4.99998,14) rot=(0.577354,0.577344,0.577354;4.18878rad)
  sketch-geometry (1):
    g0: Circle CenterX=0 CenterY=0 CenterZ=0 NormalX=0 NormalY=0 NormalZ=1 AngleXU=0 Radius=2.9
  constraints (2):
    c: Diameter(g0) = 5.8
    c: Coincident(g0,g-1)
FEATURE [PartDesign::Pad] Pad012
  BaseFeature = -> AdditivePipe
  Direction = (1.755e-05,1,1.0234e-10)
  Length = 10
  Length2 = 10
  Placement = pos=(42,-84,14) rot=(0.57735,-0.57735,0.57735;2.0944rad)
  Profile = -> Sketch023
  ReferenceAxis = -> Sketch023 [N_Axis]
  Refine = true
  Suppressed = false
  Type = 0
FEATURE [PartDesign::ShapeBinder] CopyPocket008
  Placement = pos=(42,-84,14) rot=(0.57735,-0.57735,0.57735;2.0944rad)
  TraceSupport = false
FEATURE [PartDesign::Plane] DatumPlane008
  AttachmentSupport = -> [CopyPocket008]
  Length = 61.9575
  MapMode = 5
  Placement = pos=(41.9985,5.00002,14) rot=(-0.577347,-0.577357,-0.577347;2.09438rad)
  ResizeMode = 0
  Width = 83.4479
FEATURE [Sketcher::SketchObject] Sketch025
  ArcFitTolerance = 1e-06
  AttachmentSupport = -> [DatumPlane008]
  ExternalGeometry = -> [CopyPocket008]
  FullyConstrained = true
  MakeInternals = false
  MapMode = 5
  Placement = pos=(41.9985,5.00002,14) rot=(-0.577347,-0.577357,-0.577347;2.09438rad)
  sketch-geometry (2):
    g0: Circle CenterX=0 CenterY=0 CenterZ=0 NormalX=0 NormalY=0 NormalZ=1 AngleXU=0 Radius=1.55
    g1: Circle CenterX=0 CenterY=0 CenterZ=0 NormalX=0 NormalY=0 NormalZ=1 AngleXU=0 Radius=4.5
  constraints (4):
    c: Diameter(g0) = 3.1
    c: Coincident(g0,g-1)
    c: Diameter(g1) = 9
    c: Coincident(g1,g0)
FEATURE [PartDesign::Pad] Pad013
  Direction = (-1.75232e-05,1,-4.99912e-10)
  Length = 3
  Length2 = 10
  Placement = pos=(41.9985,5.00002,14) rot=(-0.577347,-0.577357,-0.577347;2.09438rad)
  Profile = -> Sketch025
  ReferenceAxis = -> Sketch025 [N_Axis]
  Refine = true
  Suppressed = false
  Type = 0
FEATURE [PartDesign::Plane] DatumPlane009
  AttachmentSupport = -> [Pad013]
  Length = 61.9575
  MapMode = 5
  Placement = pos=(41.9984,8.00002,14) rot=(-0.577347,-0.577357,-0.577347;2.09438rad)
  ResizeMode = 0
  Width = 83.4479
FEATURE [Sketcher::SketchObject] Sketch026
  ArcFitTolerance = 1e-06
  AttachmentSupport = -> [DatumPlane009]
  ExternalGeometry = -> [Pad013]
  FullyConstrained = true
  MakeInternals = false
  MapMode = 5
  Placement = pos=(41.9984,8.00002,14) rot=(-0.577347,-0.577357,-0.577347;2.09438rad)
  sketch-geometry (2):
    g0: Circle CenterX=0 CenterY=0 CenterZ=0 NormalX=0 NormalY=0 NormalZ=1 AngleXU=0 Radius=4.50001
    g1: Circle CenterX=0 CenterY=0 CenterZ=0 NormalX=0 NormalY=0 NormalZ=1 AngleXU=0 Radius=3.1
  constraints (4):
    c: Coincident(g0,g-1)
    c: Tangent(g0,g-3)
    c: Diameter(g1) = 6.2
    c: Coincident(g1,g0)
FEATURE [PartDesign::Pad] Pad014
  BaseFeature = -> Pad013
  Direction = (-1.75232e-05,1,-4.99912e-10)
  Length = 6
  Length2 = 10
  Placement = pos=(41.9985,5.00002,14) rot=(-0.577347,-0.577357,-0.577347;2.09438rad)
  Profile = -> Sketch026
  ReferenceAxis = -> Sketch026 [N_Axis]
  Refine = true
  Suppressed = false
  Type = 0
FEATURE [PartDesign::Chamfer] Chamfer014
  Angle = 45
  Base = -> Pad014 [Edge11]
  BaseFeature = -> Pad014
  ChamferType = 0
  FlipDirection = false
  Placement = pos=(41.9985,5.00002,14) rot=(-0.577347,-0.577357,-0.577347;2.09438rad)
  Refine = true
  Size = 0.5
  Size2 = 1
  SupportTransform = false
  Suppressed = false
  UseAllEdges = false
FEATURE [PartDesign::Body] Body006  label="Adjuster Cap"
  AllowCompound = false
  Group = -> [DatumPlane008,CopyPocket008,Sketch025,Pad013,DatumPlane009,Sketch026,Pad014,Chamfer014]
  Origin = -> Origin006
  Tip = -> Chamfer014
FEATURE [Sketcher::SketchObject] Sketch027
  ArcFitTolerance = 1e-06
  AttachmentSupport = -> [Fillet]
  ExternalGeometry = -> [Fillet]
  FullyConstrained = true
  MakeInternals = false
  MapMode = 5
  Placement = pos=(0,-84,0) rot=(1,0,0;1.5708rad)
  sketch-geometry (2):
    g0: Circle CenterX=42 CenterY=14 CenterZ=0 NormalX=0 NormalY=0 NormalZ=1 AngleXU=0 Radius=3.125
    g1: Circle CenterX=42 CenterY=14 CenterZ=0 NormalX=0 NormalY=0 NormalZ=1 AngleXU=0 Radius=3.75
  constraints (4):
    c: Coincident(g0,g-3)
    c: Diameter(g1) = 7.5
    c: Coincident(g1,g0)
    c: Diameter(g0) = 6.25
FEATURE [PartDesign::Pad] Pad015
  BaseFeature = -> Fillet
  Direction = (0,-1,2e-16)
  Length = 8
  Length2 = 10
  Placement = pos=(0,0,0) rot=(1,0,0;1.5708rad)
  Profile = -> Sketch027
  ReferenceAxis = -> Sketch027 [N_Axis]
  Refine = true
  Suppressed = false
  Type = 0
FEATURE [PartDesign::Fillet] Fillet005
  Base = -> Pad015 [Edge70]
  BaseFeature = -> Pad015
  Placement = pos=(0,0,0) rot=(1,0,0;1.5708rad)
  Radius = 2
  Refine = true
  SupportTransform = false
  Suppressed = false
  UseAllEdges = false
FEATURE [Sketcher::SketchObject] Sketch030
  ArcFitTolerance = 1e-06
  AttachmentSupport = -> [Pocket005]
  ExternalGeometry = -> [Pocket005]
  FullyConstrained = true
  MakeInternals = false
  MapMode = 5
  Placement = pos=(7.11416e-08,-84,25.3536) rot=(0,0,1;3.14159rad)
  sketch-geometry (11):
    g0: LineSegment StartX=-84 StartY=0 StartZ=0 EndX=-84 EndY=-84 EndZ=0
    g1: LineSegment StartX=-84 StartY=-84 StartZ=0 EndX=7.11416e-08 EndY=-84 EndZ=0
    g2: LineSegment StartX=7.11416e-08 StartY=-84 StartZ=0 EndX=7.11416e-08 EndY=0 EndZ=0
    g3: LineSegment StartX=7.11416e-08 StartY=0 StartZ=0 EndX=-84 EndY=0 EndZ=0
    g4: Circle CenterX=-79 CenterY=-5 CenterZ=0 NormalX=0 NormalY=0 NormalZ=1 AngleXU=0 Radius=1.35
    g5: Circle CenterX=-79 CenterY=-42 CenterZ=0 NormalX=0 NormalY=0 NormalZ=1 AngleXU=0 Radius=1.35
    g6: Circle CenterX=-79 CenterY=-79 CenterZ=0 NormalX=0 NormalY=0 NormalZ=1 AngleXU=0 Radius=1.35
    g7: Circle CenterX=-41.9965 CenterY=-42 CenterZ=0 NormalX=0 NormalY=0 NormalZ=1 AngleXU=0 Radius=1.55
    g8: Circle CenterX=-5 CenterY=-5 CenterZ=0 NormalX=0 NormalY=0 NormalZ=1 AngleXU=0 Radius=1.35
    g9: Circle CenterX=-5 CenterY=-42 CenterZ=0 NormalX=0 NormalY=0 NormalZ=1 AngleXU=0 Radius=1.35
    g10: Circle CenterX=-5 CenterY=-79 CenterZ=0 NormalX=0 NormalY=0 NormalZ=1 AngleXU=0 Radius=1.35
  constraints (24):
    c: Coincident(g0,g1)
    c: Coincident(g1,g2)
    c: Coincident(g2,g3)
    c: Coincident(g3,g0)
    c: Vertical(g0)
    c: Vertical(g2)
    c: Horizontal(g1)
    c: Horizontal(g3)
    c: Coincident(g0,g-7)
    c: Coincident(g1,g-6)
    c: Coincident(g4,g-3)
    c: Equal(g4,g-3)
    c: Coincident(g5,g-10)
    c: Equal(g5,g-10)
    c: Coincident(g6,g-12)
    c: Equal(g6,g-12)
    c: Coincident(g7,g-9)
    c: Equal(g7,g-9)
    c: Coincident(g8,g-11)
    c: Equal(g8,g-11)
    c: Coincident(g9,g-8)
    c: Equal(g9,g-8)
    c: Coincident(g10,g-13)
    c: Equal(g10,g-13)
FEATURE [PartDesign::Pad] Pad016
  BaseFeature = -> Pocket005
  Direction = (2.80598e-09,0,1)
  Length = 2
  Length2 = 10
  Placement = pos=(0,-84,2e-15) rot=(1,0,0;1.5708rad)
  Profile = -> Sketch030
  ReferenceAxis = -> Sketch030 [N_Axis]
  Refine = true
  Suppressed = false
  Type = 0
FEATURE [Sketcher::SketchObject] Sketch031
  ArcFitTolerance = 1e-06
  AttachmentSupport = -> [Pad016]
  ExternalGeometry = -> [Pad016]
  FullyConstrained = true
  MakeInternals = false
  MapMode = 5
  Placement = pos=(7.67535e-08,-84,27.3536) rot=(0,0,1;3.14159rad)
  sketch-geometry (1):
    g0: Circle CenterX=-41.9965 CenterY=-42 CenterZ=0 NormalX=0 NormalY=0 NormalZ=1 AngleXU=0 Radius=3
  constraints (2):
    c: Diameter(g0) = 6
    c: Coincident(g0,g-3)
FEATURE [PartDesign::Pocket] Pocket011
  BaseFeature = -> Pad016
  Direction = (-2.80598e-09,0,-1)
  Length = 4
  Length2 = 5
  Placement = pos=(0,-84,2e-15) rot=(1,0,0;1.5708rad)
  Profile = -> Sketch031
  ReferenceAxis = -> Sketch031 [N_Axis]
  Refine = true
  Suppressed = false
  Type = 0
FEATURE [PartDesign::ShapeBinder] CopyPocket011
  Placement = pos=(0,-84,2e-15) rot=(1,0,0;1.5708rad)
  TraceSupport = false
FEATURE [PartDesign::Plane] DatumPlane010
  AttachmentSupport = -> [CopyPocket011]
  Length = 130.8
  MapMode = 5
  Placement = pos=(7.67535e-08,-84,27.3536) rot=(0,0,1;3.14159rad)
  ResizeMode = 0
  Width = 130.8
FEATURE [Sketcher::SketchObject] Sketch032
  ArcFitTolerance = 1e-06
  AttachmentSupport = -> [DatumPlane010]
  ExternalGeometry = -> [CopyPocket011]
  FullyConstrained = true
  MakeInternals = false
  MapMode = 5
  Placement = pos=(7.67535e-08,-84,27.3536) rot=(0,0,1;3.14159rad)
  sketch-geometry (10):
    g0: Circle CenterX=-79 CenterY=-42 CenterZ=0 NormalX=0 NormalY=0 NormalZ=1 AngleXU=0 Radius=3
    g1: Circle CenterX=-5 CenterY=-42 CenterZ=0 NormalX=0 NormalY=0 NormalZ=1 AngleXU=0 Radius=3
    g2: LineSegment StartX=-84 StartY=0 StartZ=0 EndX=-84 EndY=-84 EndZ=0
    g3: LineSegment StartX=-84 StartY=-84 StartZ=0 EndX=7.11416e-08 EndY=-84 EndZ=0
    g4: LineSegment StartX=7.11416e-08 StartY=-84 StartZ=0 EndX=7.11416e-08 EndY=0 EndZ=0
    g5: LineSegment StartX=7.11416e-08 StartY=0 StartZ=0 EndX=-84 EndY=0 EndZ=0
    g6: Circle CenterX=-79 CenterY=-5 CenterZ=0 NormalX=0 NormalY=0 NormalZ=1 AngleXU=0 Radius=1.6
    g7: Circle CenterX=-79 CenterY=-79 CenterZ=0 NormalX=0 NormalY=0 NormalZ=1 AngleXU=0 Radius=1.6
    g8: Circle CenterX=-5 CenterY=-5 CenterZ=0 NormalX=0 NormalY=0 NormalZ=1 AngleXU=0 Radius=1.6
    g9: Circle CenterX=-5 CenterY=-79 CenterZ=0 NormalX=0 NormalY=0 NormalZ=1 AngleXU=0 Radius=1.6
  constraints (22):
    c: Diameter(g0) = 6
    c: Coincident(g0,g-8)
    c: Diameter(g1) = 6
    c: Coincident(g1,g-10)
    c: Coincident(g2,g3)
    c: Coincident(g3,g4)
    c: Coincident(g4,g5)
    c: Coincident(g5,g2)
    c: Vertical(g2)
    c: Vertical(g4)
    c: Horizontal(g3)
    c: Horizontal(g5)
    c: Coincident(g2,g-4)
    c: Coincident(g3,g-6)
    c: Diameter(g6) = 3.2
    c: Coincident(g6,g-9)
    c: Coincident(g7,g-7)
    c: Diameter(g7) = 3.2
    c: Coincident(g8,g-12)
    c: Coincident(g9,g-11)
    c: Diameter(g9) = 3.2
    c: Diameter(g8) = 3.2
FEATURE [PartDesign::Pad] Pad017
  Direction = (2.80598e-09,0,1)
  Length = 4
  Length2 = 10
  Placement = pos=(7.67535e-08,-84,27.3536) rot=(0,0,1;3.14159rad)
  Profile = -> Sketch032
  ReferenceAxis = -> Sketch032 [N_Axis]
  Refine = true
  Suppressed = false
  Type = 0
FEATURE [Sketcher::SketchObject] Sketch033
  ArcFitTolerance = 1e-06
  AttachmentSupport = -> [Pad017]
  ExternalGeometry = -> [Pad017]
  FullyConstrained = true
  MakeInternals = false
  MapMode = 5
  Placement = pos=(8.79774e-08,-84,31.3536) rot=(0,0,1;3.14159rad)
  sketch-geometry (10):
    g0: Circle CenterX=-79 CenterY=-42 CenterZ=0 NormalX=0 NormalY=0 NormalZ=1 AngleXU=0 Radius=3
    g1: Circle CenterX=-5 CenterY=-42 CenterZ=0 NormalX=0 NormalY=0 NormalZ=1 AngleXU=0 Radius=3
    g2: Circle CenterX=-5 CenterY=-5 CenterZ=0 NormalX=0 NormalY=0 NormalZ=1 AngleXU=0 Radius=3
    g3: Circle CenterX=-5 CenterY=-79 CenterZ=0 NormalX=0 NormalY=0 NormalZ=1 AngleXU=0 Radius=3
    g4: Circle CenterX=-79 CenterY=-79 CenterZ=0 NormalX=0 NormalY=0 NormalZ=1 AngleXU=0 Radius=3
    g5: Circle CenterX=-79 CenterY=-5 CenterZ=0 NormalX=0 NormalY=0 NormalZ=1 AngleXU=0 Radius=3
    g6: LineSegment StartX=-84 StartY=0 StartZ=0 EndX=-84 EndY=-84 EndZ=0
    g7: LineSegment StartX=-84 StartY=-84 StartZ=0 EndX=7.11416e-08 EndY=-84 EndZ=0
    g8: LineSegment StartX=7.11416e-08 StartY=-84 StartZ=0 EndX=7.11416e-08 EndY=0 EndZ=0
    g9: LineSegment StartX=7.11416e-08 StartY=0 StartZ=0 EndX=-84 EndY=0 EndZ=0
  constraints (22):
    c: Coincident(g0,g-8)
    c: Equal(g0,g-8)
    c: Coincident(g1,g-11)
    c: Equal(g1,g-11)
    c: Diameter(g2) = 6
    c: Coincident(g2,g-10)
    c: Diameter(g3) = 6
    c: Coincident(g3,g-12)
    c: Diameter(g4) = 6
    c: Coincident(g4,g-7)
    c: Diameter(g5) = 6
    c: Coincident(g5,g-9)
    c: Coincident(g6,g7)
    c: Coincident(g7,g8)
    c: Coincident(g8,g9)
    c: Coincident(g9,g6)
    c: Vertical(g6)
    c: Vertical(g8)
    c: Horizontal(g7)
    c: Horizontal(g9)
    c: Coincident(g6,g-4)
    c: Coincident(g7,g-6)
FEATURE [PartDesign::Pad] Pad018
  BaseFeature = -> Pad017
  Direction = (2.80598e-09,0,1)
  Length = 3.5
  Length2 = 10
  Placement = pos=(7.67535e-08,-84,27.3536) rot=(0,0,1;3.14159rad)
  Profile = -> Sketch033
  ReferenceAxis = -> Sketch033 [N_Axis]
  Refine = true
  Suppressed = false
  Type = 0
FEATURE [Sketcher::SketchObject] Sketch034
  ArcFitTolerance = 1e-06
  AttachmentSupport = -> [Pad018]
  ExternalGeometry = -> [Pad018]
  FullyConstrained = false
  MakeInternals = false
  MapMode = 5
  Placement = pos=(9.77984e-08,-84,34.8536) rot=(0,0,1;3.14159rad)
  sketch-geometry (212):
    g0: LineSegment [constr] StartX=-42 StartY=-7.1e-15 StartZ=0 EndX=-42 EndY=-84 EndZ=0
    g1: GeomPoint X=-42 Y=-42 Z=0
    g2: Circle CenterX=-42 CenterY=-42 CenterZ=0 NormalX=0 NormalY=0 NormalZ=1 AngleXU=0 Radius=1.3
    g3: Circle CenterX=-37 CenterY=-42 CenterZ=0 NormalX=0 NormalY=0 NormalZ=1 AngleXU=0 Radius=1.3
    g4: Circle CenterX=-32 CenterY=-42 CenterZ=0 NormalX=0 NormalY=0 NormalZ=1 AngleXU=0 Radius=1.3
    g5: Circle CenterX=-27 CenterY=-42 CenterZ=0 NormalX=0 NormalY=0 NormalZ=1 AngleXU=0 Radius=1.3
    g6: Circle CenterX=-22 CenterY=-42 CenterZ=0 NormalX=0 NormalY=0 NormalZ=1 AngleXU=0 Radius=1.3
    g7: Circle CenterX=-17 CenterY=-42 CenterZ=0 NormalX=0 NormalY=0 NormalZ=1 AngleXU=0 Radius=1.3
    g8: Circle CenterX=-12 CenterY=-42 CenterZ=0 NormalX=0 NormalY=0 NormalZ=1 AngleXU=0 Radius=1.3
    g9: GeomPoint X=-42 Y=-37 Z=0
    g10: Circle CenterX=-42 CenterY=-37 CenterZ=0 NormalX=0 NormalY=0 NormalZ=1 AngleXU=0 Radius=1.3
    g11: Circle CenterX=-37 CenterY=-37 CenterZ=0 NormalX=0 NormalY=0 NormalZ=1 AngleXU=0 Radius=1.3
    g12: Circle CenterX=-32 CenterY=-37 CenterZ=0 NormalX=0 NormalY=0 NormalZ=1 AngleXU=0 Radius=1.3
    g13: Circle CenterX=-27 CenterY=-37 CenterZ=0 NormalX=0 NormalY=0 NormalZ=1 AngleXU=0 Radius=1.3
    g14: Circle CenterX=-22 CenterY=-37 CenterZ=0 NormalX=0 NormalY=0 NormalZ=1 AngleXU=0 Radius=1.3
    g15: Circle CenterX=-17 CenterY=-37 CenterZ=0 NormalX=0 NormalY=0 NormalZ=1 AngleXU=0 Radius=1.3
    g16: Circle CenterX=-12 CenterY=-37 CenterZ=0 NormalX=0 NormalY=0 NormalZ=1 AngleXU=0 Radius=1.3
    g17: GeomPoint X=-42 Y=-32 Z=0
    g18: Circle CenterX=-42 CenterY=-32 CenterZ=0 NormalX=0 NormalY=0 NormalZ=1 AngleXU=0 Radius=1.3
    g19: Circle CenterX=-37 CenterY=-32 CenterZ=0 NormalX=0 NormalY=0 NormalZ=1 AngleXU=0 Radius=1.3
    g20: Circle CenterX=-32 CenterY=-32 CenterZ=0 NormalX=0 NormalY=0 NormalZ=1 AngleXU=0 Radius=1.3
    g21: Circle CenterX=-27 CenterY=-32 CenterZ=0 NormalX=0 NormalY=0 NormalZ=1 AngleXU=0 Radius=1.3
    g22: Circle CenterX=-22 CenterY=-32 CenterZ=0 NormalX=0 NormalY=0 NormalZ=1 AngleXU=0 Radius=1.3
    g23: Circle CenterX=-17 CenterY=-32 CenterZ=0 NormalX=0 NormalY=0 NormalZ=1 AngleXU=0 Radius=1.3
    g24: Circle CenterX=-12 CenterY=-32 CenterZ=0 NormalX=0 NormalY=0 NormalZ=1 AngleXU=0 Radius=1.3
    g25: GeomPoint X=-42 Y=-27 Z=0
    g26: Circle CenterX=-42 CenterY=-27 CenterZ=0 NormalX=0 NormalY=0 NormalZ=1 AngleXU=0 Radius=1.3
    g27: Circle CenterX=-37 CenterY=-27 CenterZ=0 NormalX=0 NormalY=0 NormalZ=1 AngleXU=0 Radius=1.3
    g28: Circle CenterX=-32 CenterY=-27 CenterZ=0 NormalX=0 NormalY=0 NormalZ=1 AngleXU=0 Radius=1.3
    g29: Circle CenterX=-27 CenterY=-27 CenterZ=0 NormalX=0 NormalY=0 NormalZ=1 AngleXU=0 Radius=1.3
    g30: Circle CenterX=-22 CenterY=-27 CenterZ=0 NormalX=0 NormalY=0 NormalZ=1 AngleXU=0 Radius=1.3
    g31: Circle CenterX=-17 CenterY=-27 CenterZ=0 NormalX=0 NormalY=0 NormalZ=1 AngleXU=0 Radius=1.3
    g32: Circle CenterX=-12 CenterY=-27 CenterZ=0 NormalX=0 NormalY=0 NormalZ=1 AngleXU=0 Radius=1.3
    g33: GeomPoint X=-42 Y=-22 Z=0
    g34: Circle CenterX=-42 CenterY=-22 CenterZ=0 NormalX=0 NormalY=0 NormalZ=1 AngleXU=0 Radius=1.3
    g35: Circle CenterX=-37 CenterY=-22 CenterZ=0 NormalX=0 NormalY=0 NormalZ=1 AngleXU=0 Radius=1.3
    g36: Circle CenterX=-32 CenterY=-22 CenterZ=0 NormalX=0 NormalY=0 NormalZ=1 AngleXU=0 Radius=1.3
    g37: Circle CenterX=-27 CenterY=-22 CenterZ=0 NormalX=0 NormalY=0 NormalZ=1 AngleXU=0 Radius=1.3
    g38: Circle CenterX=-22 CenterY=-22 CenterZ=0 NormalX=0 NormalY=0 NormalZ=1 AngleXU=0 Radius=1.3
    g39: Circle CenterX=-17 CenterY=-22 CenterZ=0 NormalX=0 NormalY=0 NormalZ=1 AngleXU=0 Radius=1.3
    g40: Circle CenterX=-12 CenterY=-22 CenterZ=0 NormalX=0 NormalY=0 NormalZ=1 AngleXU=0 Radius=1.3
    g41: GeomPoint X=-42 Y=-17 Z=0
    g42: Circle CenterX=-42 CenterY=-17 CenterZ=0 NormalX=0 NormalY=0 NormalZ=1 AngleXU=0 Radius=1.3
    g43: Circle CenterX=-37 CenterY=-17 CenterZ=0 NormalX=0 NormalY=0 NormalZ=1 AngleXU=0 Radius=1.3
    g44: Circle CenterX=-32 CenterY=-17 CenterZ=0 NormalX=0 NormalY=0 NormalZ=1 AngleXU=0 Radius=1.3
    g45: Circle CenterX=-27 CenterY=-17 CenterZ=0 NormalX=0 NormalY=0 NormalZ=1 AngleXU=0 Radius=1.3
    g46: Circle CenterX=-22 CenterY=-17 CenterZ=0 NormalX=0 NormalY=0 NormalZ=1 AngleXU=0 Radius=1.3
    g47: Circle CenterX=-17 CenterY=-17 CenterZ=0 NormalX=0 NormalY=0 NormalZ=1 AngleXU=0 Radius=1.3
    g48: Circle CenterX=-12 CenterY=-17 CenterZ=0 NormalX=0 NormalY=0 NormalZ=1 AngleXU=0 Radius=1.3
    g49: GeomPoint X=-42 Y=-12 Z=0
    g50: Circle CenterX=-42 CenterY=-12 CenterZ=0 NormalX=0 NormalY=0 NormalZ=1 AngleXU=0 Radius=1.3
    g51: Circle CenterX=-37 CenterY=-12 CenterZ=0 NormalX=0 NormalY=0 NormalZ=1 AngleXU=0 Radius=1.3
    g52: Circle CenterX=-32 CenterY=-12 CenterZ=0 NormalX=0 NormalY=0 NormalZ=1 AngleXU=0 Radius=1.3
    g53: Circle CenterX=-27 CenterY=-12 CenterZ=0 NormalX=0 NormalY=0 NormalZ=1 AngleXU=0 Radius=1.3
    g54: Circle CenterX=-22 CenterY=-12 CenterZ=0 NormalX=0 NormalY=0 NormalZ=1 AngleXU=0 Radius=1.3
    g55: Circle CenterX=-17 CenterY=-12 CenterZ=0 NormalX=0 NormalY=0 NormalZ=1 AngleXU=0 Radius=1.3
    g56: Circle CenterX=-12 CenterY=-12 CenterZ=0 NormalX=0 NormalY=0 NormalZ=1 AngleXU=0 Radius=1.3
    g57: GeomPoint X=-42 Y=-7 Z=0
    g58: Circle CenterX=-42 CenterY=-7 CenterZ=0 NormalX=0 NormalY=0 NormalZ=1 AngleXU=0 Radius=1.3
    g59: Circle CenterX=-37 CenterY=-7 CenterZ=0 NormalX=0 NormalY=0 NormalZ=1 AngleXU=0 Radius=1.3
    g60: Circle CenterX=-32 CenterY=-7 CenterZ=0 NormalX=0 NormalY=0 NormalZ=1 AngleXU=0 Radius=1.3
    g61: Circle CenterX=-27 CenterY=-7 CenterZ=0 NormalX=0 NormalY=0 NormalZ=1 AngleXU=0 Radius=1.3
    g62: Circle CenterX=-22 CenterY=-7 CenterZ=0 NormalX=0 NormalY=0 NormalZ=1 AngleXU=0 Radius=1.3
    g63: Circle CenterX=-17 CenterY=-7 CenterZ=0 NormalX=0 NormalY=0 NormalZ=1 AngleXU=0 Radius=1.3
    g64: Circle CenterX=-12 CenterY=-7 CenterZ=0 NormalX=0 NormalY=0 NormalZ=1 AngleXU=0 Radius=1.3
    g65: LineSegment [constr] StartX=-84 StartY=-42 StartZ=0 EndX=7.11416e-08 EndY=-42 EndZ=0
    g66: Circle CenterX=-47 CenterY=-42 CenterZ=0 NormalX=0 NormalY=0 NormalZ=1 AngleXU=0 Radius=1.3
    g67: Circle CenterX=-52 CenterY=-42 CenterZ=0 NormalX=0 NormalY=0 NormalZ=1 AngleXU=0 Radius=1.3
    g68: Circle CenterX=-57 CenterY=-42 CenterZ=0 NormalX=0 NormalY=0 NormalZ=1 AngleXU=0 Radius=1.3
    g69: Circle CenterX=-62 CenterY=-42 CenterZ=0 NormalX=0 NormalY=0 NormalZ=1 AngleXU=0 Radius=1.3
    g70: Circle CenterX=-67 CenterY=-42 CenterZ=0 NormalX=0 NormalY=0 NormalZ=1 AngleXU=0 Radius=1.3
    g71: Circle CenterX=-72 CenterY=-42 CenterZ=0 NormalX=0 NormalY=0 NormalZ=1 AngleXU=0 Radius=1.3
    g72: Circle CenterX=-47 CenterY=-37 CenterZ=0 NormalX=0 NormalY=0 NormalZ=1 AngleXU=0 Radius=1.3
    g73: Circle CenterX=-52 CenterY=-37 CenterZ=0 NormalX=0 NormalY=0 NormalZ=1 AngleXU=0 Radius=1.3
    g74: Circle CenterX=-57 CenterY=-37 CenterZ=0 NormalX=0 NormalY=0 NormalZ=1 AngleXU=0 Radius=1.3
    g75: Circle CenterX=-62 CenterY=-37 CenterZ=0 NormalX=0 NormalY=0 NormalZ=1 AngleXU=0 Radius=1.3
    g76: Circle CenterX=-67 CenterY=-37 CenterZ=0 NormalX=0 NormalY=0 NormalZ=1 AngleXU=0 Radius=1.3
    g77: Circle CenterX=-72 CenterY=-37 CenterZ=0 NormalX=0 NormalY=0 NormalZ=1 AngleXU=0 Radius=1.3
    g78: Circle CenterX=-47 CenterY=-32 CenterZ=0 NormalX=0 NormalY=0 NormalZ=1 AngleXU=0 Radius=1.3
    g79: Circle CenterX=-52 CenterY=-32 CenterZ=0 NormalX=0 NormalY=0 NormalZ=1 AngleXU=0 Radius=1.3
    g80: Circle CenterX=-57 CenterY=-32 CenterZ=0 NormalX=0 NormalY=0 NormalZ=1 AngleXU=0 Radius=1.3
    g81: Circle CenterX=-62 CenterY=-32 CenterZ=0 NormalX=0 NormalY=0 NormalZ=1 AngleXU=0 Radius=1.3
    g82: Circle CenterX=-67 CenterY=-32 CenterZ=0 NormalX=0 NormalY=0 NormalZ=1 AngleXU=0 Radius=1.3
    g83: Circle CenterX=-72 CenterY=-32 CenterZ=0 NormalX=0 NormalY=0 NormalZ=1 AngleXU=0 Radius=1.3
    g84: Circle CenterX=-47 CenterY=-27 CenterZ=0 NormalX=0 NormalY=0 NormalZ=1 AngleXU=0 Radius=1.3
    g85: Circle CenterX=-52 CenterY=-27 CenterZ=0 NormalX=0 NormalY=0 NormalZ=1 AngleXU=0 Radius=1.3
    g86: Circle CenterX=-57 CenterY=-27 CenterZ=0 NormalX=0 NormalY=0 NormalZ=1 AngleXU=0 Radius=1.3
    g87: Circle CenterX=-62 CenterY=-27 CenterZ=0 NormalX=0 NormalY=0 NormalZ=1 AngleXU=0 Radius=1.3
    g88: Circle CenterX=-67 CenterY=-27 CenterZ=0 NormalX=0 NormalY=0 NormalZ=1 AngleXU=0 Radius=1.3
    g89: Circle CenterX=-72 CenterY=-27 CenterZ=0 NormalX=0 NormalY=0 NormalZ=1 AngleXU=0 Radius=1.3
    g90: Circle CenterX=-47 CenterY=-22 CenterZ=0 NormalX=0 NormalY=0 NormalZ=1 AngleXU=0 Radius=1.3
    g91: Circle CenterX=-52 CenterY=-22 CenterZ=0 NormalX=0 NormalY=0 NormalZ=1 AngleXU=0 Radius=1.3
    g92: Circle CenterX=-57 CenterY=-22 CenterZ=0 NormalX=0 NormalY=0 NormalZ=1 AngleXU=0 Radius=1.3
    g93: Circle CenterX=-62 CenterY=-22 CenterZ=0 NormalX=0 NormalY=0 NormalZ=1 AngleXU=0 Radius=1.3
    g94: Circle CenterX=-67 CenterY=-22 CenterZ=0 NormalX=0 NormalY=0 NormalZ=1 AngleXU=0 Radius=1.3
    g95: Circle CenterX=-72 CenterY=-22 CenterZ=0 NormalX=0 NormalY=0 NormalZ=1 AngleXU=0 Radius=1.3
    g96: Circle CenterX=-47 CenterY=-17 CenterZ=0 NormalX=0 NormalY=0 NormalZ=1 AngleXU=0 Radius=1.3
    g97: Circle CenterX=-52 CenterY=-17 CenterZ=0 NormalX=0 NormalY=0 NormalZ=1 AngleXU=0 Radius=1.3
    g98: Circle CenterX=-57 CenterY=-17 CenterZ=0 NormalX=0 NormalY=0 NormalZ=1 AngleXU=0 Radius=1.3
    g99: Circle CenterX=-62 CenterY=-17 CenterZ=0 NormalX=0 NormalY=0 NormalZ=1 AngleXU=0 Radius=1.3
    g100: Circle CenterX=-67 CenterY=-17 CenterZ=0 NormalX=0 NormalY=0 NormalZ=1 AngleXU=0 Radius=1.3
    g101: Circle CenterX=-72 CenterY=-17 CenterZ=0 NormalX=0 NormalY=0 NormalZ=1 AngleXU=0 Radius=1.3
    g102: Circle CenterX=-47 CenterY=-12 CenterZ=0 NormalX=0 NormalY=0 NormalZ=1 AngleXU=0 Radius=1.3
    g103: Circle CenterX=-52 CenterY=-12 CenterZ=0 NormalX=0 NormalY=0 NormalZ=1 AngleXU=0 Radius=1.3
    g104: Circle CenterX=-57 CenterY=-12 CenterZ=0 NormalX=0 NormalY=0 NormalZ=1 AngleXU=0 Radius=1.3
    g105: Circle CenterX=-62 CenterY=-12 CenterZ=0 NormalX=0 NormalY=0 NormalZ=1 AngleXU=0 Radius=1.3
    g106: Circle CenterX=-67 CenterY=-12 CenterZ=0 NormalX=0 NormalY=0 NormalZ=1 AngleXU=0 Radius=1.3
    g107: Circle CenterX=-72 CenterY=-12 CenterZ=0 NormalX=0 NormalY=0 NormalZ=1 AngleXU=0 Radius=1.3
    g108: Circle CenterX=-47 CenterY=-7 CenterZ=0 NormalX=0 NormalY=0 NormalZ=1 AngleXU=0 Radius=1.3
    g109: Circle CenterX=-52 CenterY=-7 CenterZ=0 NormalX=0 NormalY=0 NormalZ=1 AngleXU=0 Radius=1.3
    g110: Circle CenterX=-57 CenterY=-7 CenterZ=0 NormalX=0 NormalY=0 NormalZ=1 AngleXU=0 Radius=1.3
    g111: Circle CenterX=-62 CenterY=-7 CenterZ=0 NormalX=0 NormalY=0 NormalZ=1 AngleXU=0 Radius=1.3
    g112: Circle CenterX=-67 CenterY=-7 CenterZ=0 NormalX=0 NormalY=0 NormalZ=1 AngleXU=0 Radius=1.3
    g113: Circle CenterX=-72 CenterY=-7 CenterZ=0 NormalX=0 NormalY=0 NormalZ=1 AngleXU=0 Radius=1.3
    g114: GeomPoint X=-42 Y=-47 Z=0
    g115: Circle CenterX=-42 CenterY=-47 CenterZ=0 NormalX=0 NormalY=0 NormalZ=1 AngleXU=0 Radius=1.3
    g116: Circle CenterX=-37 CenterY=-47 CenterZ=0 NormalX=0 NormalY=0 NormalZ=1 AngleXU=0 Radius=1.3
    g117: Circle CenterX=-32 CenterY=-47 CenterZ=0 NormalX=0 NormalY=0 NormalZ=1 AngleXU=0 Radius=1.3
    g118: Circle CenterX=-27 CenterY=-47 CenterZ=0 NormalX=0 NormalY=0 NormalZ=1 AngleXU=0 Radius=1.3
    g119: Circle CenterX=-22 CenterY=-47 CenterZ=0 NormalX=0 NormalY=0 NormalZ=1 AngleXU=0 Radius=1.3
    g120: Circle CenterX=-17 CenterY=-47 CenterZ=0 NormalX=0 NormalY=0 NormalZ=1 AngleXU=0 Radius=1.3
    g121: Circle CenterX=-12 CenterY=-47 CenterZ=0 NormalX=0 NormalY=0 NormalZ=1 AngleXU=0 Radius=1.3
    g122: GeomPoint X=-42 Y=-52 Z=0
    g123: Circle CenterX=-42 CenterY=-52 CenterZ=0 NormalX=0 NormalY=0 NormalZ=1 AngleXU=0 Radius=1.3
    g124: Circle CenterX=-37 CenterY=-52 CenterZ=0 NormalX=0 NormalY=0 NormalZ=1 AngleXU=0 Radius=1.3
    g125: Circle CenterX=-32 CenterY=-52 CenterZ=0 NormalX=0 NormalY=0 NormalZ=1 AngleXU=0 Radius=1.3
    g126: Circle CenterX=-27 CenterY=-52 CenterZ=0 NormalX=0 NormalY=0 NormalZ=1 AngleXU=0 Radius=1.3
    g127: Circle CenterX=-22 CenterY=-52 CenterZ=0 NormalX=0 NormalY=0 NormalZ=1 AngleXU=0 Radius=1.3
    g128: Circle CenterX=-17 CenterY=-52 CenterZ=0 NormalX=0 NormalY=0 NormalZ=1 AngleXU=0 Radius=1.3
    g129: Circle CenterX=-12 CenterY=-52 CenterZ=0 NormalX=0 NormalY=0 NormalZ=1 AngleXU=0 Radius=1.3
    g130: GeomPoint X=-42 Y=-57 Z=0
    g131: Circle CenterX=-42 CenterY=-57 CenterZ=0 NormalX=0 NormalY=0 NormalZ=1 AngleXU=0 Radius=1.3
    g132: Circle CenterX=-37 CenterY=-57 CenterZ=0 NormalX=0 NormalY=0 NormalZ=1 AngleXU=0 Radius=1.3
    g133: Circle CenterX=-32 CenterY=-57 CenterZ=0 NormalX=0 NormalY=0 NormalZ=1 AngleXU=0 Radius=1.3
    g134: Circle CenterX=-27 CenterY=-57 CenterZ=0 NormalX=0 NormalY=0 NormalZ=1 AngleXU=0 Radius=1.3
    g135: Circle CenterX=-22 CenterY=-57 CenterZ=0 NormalX=0 NormalY=0 NormalZ=1 AngleXU=0 Radius=1.3
    g136: Circle CenterX=-17 CenterY=-57 CenterZ=0 NormalX=0 NormalY=0 NormalZ=1 AngleXU=0 Radius=1.3
    g137: Circle CenterX=-12 CenterY=-57 CenterZ=0 NormalX=0 NormalY=0 NormalZ=1 AngleXU=0 Radius=1.3
    g138: GeomPoint X=-42 Y=-62 Z=0
    g139: Circle CenterX=-42 CenterY=-62 CenterZ=0 NormalX=0 NormalY=0 NormalZ=1 AngleXU=0 Radius=1.3
    g140: Circle CenterX=-37 CenterY=-62 CenterZ=0 NormalX=0 NormalY=0 NormalZ=1 AngleXU=0 Radius=1.3
    g141: Circle CenterX=-32 CenterY=-62 CenterZ=0 NormalX=0 NormalY=0 NormalZ=1 AngleXU=0 Radius=1.3
    g142: Circle CenterX=-27 CenterY=-62 CenterZ=0 NormalX=0 NormalY=0 NormalZ=1 AngleXU=0 Radius=1.3
    g143: Circle CenterX=-22 CenterY=-62 CenterZ=0 NormalX=0 NormalY=0 NormalZ=1 AngleXU=0 Radius=1.3
    g144: Circle CenterX=-17 CenterY=-62 CenterZ=0 NormalX=0 NormalY=0 NormalZ=1 AngleXU=0 Radius=1.3
    g145: Circle CenterX=-12 CenterY=-62 CenterZ=0 NormalX=0 NormalY=0 NormalZ=1 AngleXU=0 Radius=1.3
    g146: GeomPoint X=-42 Y=-67 Z=0
    g147: Circle CenterX=-42 CenterY=-67 CenterZ=0 NormalX=0 NormalY=0 NormalZ=1 AngleXU=0 Radius=1.3
    g148: Circle CenterX=-37 CenterY=-67 CenterZ=0 NormalX=0 NormalY=0 NormalZ=1 AngleXU=0 Radius=1.3
    g149: Circle CenterX=-32 CenterY=-67 CenterZ=0 NormalX=0 NormalY=0 NormalZ=1 AngleXU=0 Radius=1.3
    g150: Circle CenterX=-27 CenterY=-67 CenterZ=0 NormalX=0 NormalY=0 NormalZ=1 AngleXU=0 Radius=1.3
    g151: Circle CenterX=-22 CenterY=-67 CenterZ=0 NormalX=0 NormalY=0 NormalZ=1 AngleXU=0 Radius=1.3
    g152: Circle CenterX=-17 CenterY=-67 CenterZ=0 NormalX=0 NormalY=0 NormalZ=1 AngleXU=0 Radius=1.3
    g153: Circle CenterX=-12 CenterY=-67 CenterZ=0 NormalX=0 NormalY=0 NormalZ=1 AngleXU=0 Radius=1.3
    g154: GeomPoint X=-42 Y=-72 Z=0
    g155: Circle CenterX=-42 CenterY=-72 CenterZ=0 NormalX=0 NormalY=0 NormalZ=1 AngleXU=0 Radius=1.3
    g156: Circle CenterX=-37 CenterY=-72 CenterZ=0 NormalX=0 NormalY=0 NormalZ=1 AngleXU=0 Radius=1.3
    g157: Circle CenterX=-32 CenterY=-72 CenterZ=0 NormalX=0 NormalY=0 NormalZ=1 AngleXU=0 Radius=1.3
    g158: Circle CenterX=-27 CenterY=-72 CenterZ=0 NormalX=0 NormalY=0 NormalZ=1 AngleXU=0 Radius=1.3
    g159: Circle CenterX=-22 CenterY=-72 CenterZ=0 NormalX=0 NormalY=0 NormalZ=1 AngleXU=0 Radius=1.3
    g160: Circle CenterX=-17 CenterY=-72 CenterZ=0 NormalX=0 NormalY=0 NormalZ=1 AngleXU=0 Radius=1.3
    g161: Circle CenterX=-12 CenterY=-72 CenterZ=0 NormalX=0 NormalY=0 NormalZ=1 AngleXU=0 Radius=1.3
    g162: GeomPoint X=-42 Y=-77 Z=0
    g163: Circle CenterX=-42 CenterY=-77 CenterZ=0 NormalX=0 NormalY=0 NormalZ=1 AngleXU=0 Radius=1.3
    g164: Circle CenterX=-37 CenterY=-77 CenterZ=0 NormalX=0 NormalY=0 NormalZ=1 AngleXU=0 Radius=1.3
    g165: Circle CenterX=-32 CenterY=-77 CenterZ=0 NormalX=0 NormalY=0 NormalZ=1 AngleXU=0 Radius=1.3
    g166: Circle CenterX=-27 CenterY=-77 CenterZ=0 NormalX=0 NormalY=0 NormalZ=1 AngleXU=0 Radius=1.3
    g167: Circle CenterX=-22 CenterY=-77 CenterZ=0 NormalX=0 NormalY=0 NormalZ=1 AngleXU=0 Radius=1.3
    g168: Circle CenterX=-17 CenterY=-77 CenterZ=0 NormalX=0 NormalY=0 NormalZ=1 AngleXU=0 Radius=1.3
    g169: Circle CenterX=-12 CenterY=-77 CenterZ=0 NormalX=0 NormalY=0 NormalZ=1 AngleXU=0 Radius=1.3
    g170: Circle CenterX=-47 CenterY=-47 CenterZ=0 NormalX=0 NormalY=0 NormalZ=1 AngleXU=0 Radius=1.3
    g171: Circle CenterX=-52 CenterY=-47 CenterZ=0 NormalX=0 NormalY=0 NormalZ=1 AngleXU=0 Radius=1.3
    g172: Circle CenterX=-57 CenterY=-47 CenterZ=0 NormalX=0 NormalY=0 NormalZ=1 AngleXU=0 Radius=1.3
    g173: Circle CenterX=-62 CenterY=-47 CenterZ=0 NormalX=0 NormalY=0 NormalZ=1 AngleXU=0 Radius=1.3
    g174: Circle CenterX=-67 CenterY=-47 CenterZ=0 NormalX=0 NormalY=0 NormalZ=1 AngleXU=0 Radius=1.3
    g175: Circle CenterX=-72 CenterY=-47 CenterZ=0 NormalX=0 NormalY=0 NormalZ=1 AngleXU=0 Radius=1.3
    g176: Circle CenterX=-47 CenterY=-52 CenterZ=0 NormalX=0 NormalY=0 NormalZ=1 AngleXU=0 Radius=1.3
    g177: Circle CenterX=-52 CenterY=-52 CenterZ=0 NormalX=0 NormalY=0 NormalZ=1 AngleXU=0 Radius=1.3
    g178: Circle CenterX=-57 CenterY=-52 CenterZ=0 NormalX=0 NormalY=0 NormalZ=1 AngleXU=0 Radius=1.3
    g179: Circle CenterX=-62 CenterY=-52 CenterZ=0 NormalX=0 NormalY=0 NormalZ=1 AngleXU=0 Radius=1.3
    g180: Circle CenterX=-67 CenterY=-52 CenterZ=0 NormalX=0 NormalY=0 NormalZ=1 AngleXU=0 Radius=1.3
    g181: Circle CenterX=-72 CenterY=-52 CenterZ=0 NormalX=0 NormalY=0 NormalZ=1 AngleXU=0 Radius=1.3
    g182: Circle CenterX=-47 CenterY=-57 CenterZ=0 NormalX=0 NormalY=0 NormalZ=1 AngleXU=0 Radius=1.3
    g183: Circle CenterX=-52 CenterY=-57 CenterZ=0 NormalX=0 NormalY=0 NormalZ=1 AngleXU=0 Radius=1.3
    g184: Circle CenterX=-57 CenterY=-57 CenterZ=0 NormalX=0 NormalY=0 NormalZ=1 AngleXU=0 Radius=1.3
    g185: Circle CenterX=-62 CenterY=-57 CenterZ=0 NormalX=0 NormalY=0 NormalZ=1 AngleXU=0 Radius=1.3
    g186: Circle CenterX=-67 CenterY=-57 CenterZ=0 NormalX=0 NormalY=0 NormalZ=1 AngleXU=0 Radius=1.3
    g187: Circle CenterX=-72 CenterY=-57 CenterZ=0 NormalX=0 NormalY=0 NormalZ=1 AngleXU=0 Radius=1.3
    g188: Circle CenterX=-47 CenterY=-62 CenterZ=0 NormalX=0 NormalY=0 NormalZ=1 AngleXU=0 Radius=1.3
    g189: Circle CenterX=-52 CenterY=-62 CenterZ=0 NormalX=0 NormalY=0 NormalZ=1 AngleXU=0 Radius=1.3
    g190: Circle CenterX=-57 CenterY=-62 CenterZ=0 NormalX=0 NormalY=0 NormalZ=1 AngleXU=0 Radius=1.3
    g191: Circle CenterX=-62 CenterY=-62 CenterZ=0 NormalX=0 NormalY=0 NormalZ=1 AngleXU=0 Radius=1.3
    g192: Circle CenterX=-67 CenterY=-62 CenterZ=0 NormalX=0 NormalY=0 NormalZ=1 AngleXU=0 Radius=1.3
    g193: Circle CenterX=-72 CenterY=-62 CenterZ=0 NormalX=0 NormalY=0 NormalZ=1 AngleXU=0 Radius=1.3
    g194: Circle CenterX=-47 CenterY=-67 CenterZ=0 NormalX=0 NormalY=0 NormalZ=1 AngleXU=0 Radius=1.3
    g195: Circle CenterX=-52 CenterY=-67 CenterZ=0 NormalX=0 NormalY=0 NormalZ=1 AngleXU=0 Radius=1.3
    g196: Circle CenterX=-57 CenterY=-67 CenterZ=0 NormalX=0 NormalY=0 NormalZ=1 AngleXU=0 Radius=1.3
    g197: Circle CenterX=-62 CenterY=-67 CenterZ=0 NormalX=0 NormalY=0 NormalZ=1 AngleXU=0 Radius=1.3
    g198: Circle CenterX=-67 CenterY=-67 CenterZ=0 NormalX=0 NormalY=0 NormalZ=1 AngleXU=0 Radius=1.3
    g199: Circle CenterX=-72 CenterY=-67 CenterZ=0 NormalX=0 NormalY=0 NormalZ=1 AngleXU=0 Radius=1.3
    g200: Circle CenterX=-47 CenterY=-72 CenterZ=0 NormalX=0 NormalY=0 NormalZ=1 AngleXU=0 Radius=1.3
    g201: Circle CenterX=-52 CenterY=-72 CenterZ=0 NormalX=0 NormalY=0 NormalZ=1 AngleXU=0 Radius=1.3
    g202: Circle CenterX=-57 CenterY=-72 CenterZ=0 NormalX=0 NormalY=0 NormalZ=1 AngleXU=0 Radius=1.3
    g203: Circle CenterX=-62 CenterY=-72 CenterZ=0 NormalX=0 NormalY=0 NormalZ=1 AngleXU=0 Radius=1.3
    g204: Circle CenterX=-67 CenterY=-72 CenterZ=0 NormalX=0 NormalY=0 NormalZ=1 AngleXU=0 Radius=1.3
    g205: Circle CenterX=-72 CenterY=-72 CenterZ=0 NormalX=0 NormalY=0 NormalZ=1 AngleXU=0 Radius=1.3
    g206: Circle CenterX=-47 CenterY=-77 CenterZ=0 NormalX=0 NormalY=0 NormalZ=1 AngleXU=0 Radius=1.3
    g207: Circle CenterX=-52 CenterY=-77 CenterZ=0 NormalX=0 NormalY=0 NormalZ=1 AngleXU=0 Radius=1.3
    g208: Circle CenterX=-57 CenterY=-77 CenterZ=0 NormalX=0 NormalY=0 NormalZ=1 AngleXU=0 Radius=1.3
    g209: Circle CenterX=-62 CenterY=-77 CenterZ=0 NormalX=0 NormalY=0 NormalZ=1 AngleXU=0 Radius=1.3
    g210: Circle CenterX=-67 CenterY=-77 CenterZ=0 NormalX=0 NormalY=0 NormalZ=1 AngleXU=0 Radius=1.3
    g211: Circle CenterX=-72 CenterY=-77 CenterZ=0 NormalX=0 NormalY=0 NormalZ=1 AngleXU=0 Radius=1.3
  constraints (215):
    c: Symmetric(g-4,g-4,g0)
    c: Symmetric(g-6,g-6,g0)
    c: Symmetric(g0,g0,g1)
    c: Diameter(g2) = 2.6
    c: Coincident(g2,g1)
    c: Diameter(g3) = 2.6
    c: Diameter(g4) = 2.6
    c: Diameter(g5) = 2.6
    c: Diameter(g6) = 2.6
    c: Diameter(g7) = 2.6
    c: Diameter(g8) = 2.6
    c: Diameter(g10) = 2.6
    c: Diameter(g18) = 2.6
    c: Diameter(g26) = 2.6
    c: Diameter(g34) = 2.6
    c: Diameter(g42) = 2.6
    c: Diameter(g50) = 2.6
    c: Diameter(g58) = 2.6
    c: Coincident(g10,g9)
    c: Coincident(g18,g17)
    c: Coincident(g26,g25)
    c: Coincident(g34,g33)
    c: Coincident(g42,g41)
    c: Coincident(g50,g49)
    c: Coincident(g58,g57)
    c: Diameter(g11) = 2.6
    c: Diameter(g19) = 2.6
    c: Diameter(g27) = 2.6
    c: Diameter(g35) = 2.6
    c: Diameter(g43) = 2.6
    c: Diameter(g51) = 2.6
    c: Diameter(g59) = 2.6
    c: Diameter(g12) = 2.6
    c: Diameter(g20) = 2.6
    c: Diameter(g28) = 2.6
    c: Diameter(g36) = 2.6
    c: Diameter(g44) = 2.6
    c: Diameter(g52) = 2.6
    c: Diameter(g60) = 2.6
    c: Diameter(g13) = 2.6
    c: Diameter(g21) = 2.6
    c: Diameter(g29) = 2.6
    c: Diameter(g37) = 2.6
    c: Diameter(g45) = 2.6
    c: Diameter(g53) = 2.6
    c: Diameter(g61) = 2.6
    c: Diameter(g14) = 2.6
    c: Diameter(g22) = 2.6
    c: Diameter(g30) = 2.6
    c: Diameter(g38) = 2.6
    c: Diameter(g46) = 2.6
    c: Diameter(g54) = 2.6
    c: Diameter(g62) = 2.6
    c: Diameter(g15) = 2.6
    c: Diameter(g23) = 2.6
    c: Diameter(g31) = 2.6
    c: Diameter(g39) = 2.6
    c: Diameter(g47) = 2.6
    c: Diameter(g55) = 2.6
    c: Diameter(g63) = 2.6
    c: Diameter(g16) = 2.6
    c: Diameter(g24) = 2.6
    c: Diameter(g32) = 2.6
    c: Diameter(g40) = 2.6
    c: Diameter(g48) = 2.6
    c: Diameter(g56) = 2.6
    c: Diameter(g64) = 2.6
    c: Symmetric(g-3,g-3,g65)
    c: Symmetric(g-5,g-5,g65)
    c: Diameter(g66) = 2.6
    c: Diameter(g67) = 2.6
    c: Diameter(g68) = 2.6
    c: Diameter(g69) = 2.6
    c: Diameter(g70) = 2.6
    c: Diameter(g71) = 2.6
    c: Diameter(g72) = 2.6
    c: Diameter(g78) = 2.6
    c: Diameter(g84) = 2.6
    c: Diameter(g90) = 2.6
    c: Diameter(g96) = 2.6
    c: Diameter(g102) = 2.6
    c: Diameter(g108) = 2.6
    c: Diameter(g73) = 2.6
    c: Diameter(g79) = 2.6
    c: Diameter(g85) = 2.6
    c: Diameter(g91) = 2.6
    c: Diameter(g97) = 2.6
    c: Diameter(g103) = 2.6
    c: Diameter(g109) = 2.6
    c: Diameter(g74) = 2.6
    c: Diameter(g80) = 2.6
    c: Diameter(g86) = 2.6
    c: Diameter(g92) = 2.6
    c: Diameter(g98) = 2.6
    c: Diameter(g104) = 2.6
    c: Diameter(g110) = 2.6
    c: Diameter(g75) = 2.6
    c: Diameter(g81) = 2.6
    c: Diameter(g87) = 2.6
    c: Diameter(g93) = 2.6
    c: Diameter(g99) = 2.6
    c: Diameter(g105) = 2.6
    c: Diameter(g111) = 2.6
    c: Diameter(g76) = 2.6
    c: Diameter(g82) = 2.6
    c: Diameter(g88) = 2.6
    c: Diameter(g94) = 2.6
    c: Diameter(g100) = 2.6
    c: Diameter(g106) = 2.6
    c: Diameter(g112) = 2.6
    c: Diameter(g77) = 2.6
    c: Diameter(g83) = 2.6
    c: Diameter(g89) = 2.6
    c: Diameter(g95) = 2.6
    c: Diameter(g101) = 2.6
    c: Diameter(g107) = 2.6
    c: Diameter(g113) = 2.6
    c: Diameter(g115) = 2.6
    c: Diameter(g123) = 2.6
    c: Diameter(g131) = 2.6
    c: Diameter(g139) = 2.6
    c: Diameter(g147) = 2.6
    c: Diameter(g155) = 2.6
    c: Diameter(g163) = 2.6
    c: Coincident(g115,g114)
    c: Coincident(g123,g122)
    c: Coincident(g131,g130)
    c: Coincident(g139,g138)
    c: Coincident(g147,g146)
    c: Coincident(g155,g154)
    c: Coincident(g163,g162)
    c: Diameter(g116) = 2.6
    c: Diameter(g124) = 2.6
    c: Diameter(g132) = 2.6
    c: Diameter(g140) = 2.6
    c: Diameter(g148) = 2.6
    c: Diameter(g156) = 2.6
    c: Diameter(g164) = 2.6
    c: Diameter(g117) = 2.6
    c: Diameter(g125) = 2.6
    c: Diameter(g133) = 2.6
    c: Diameter(g141) = 2.6
    c: Diameter(g149) = 2.6
    c: Diameter(g157) = 2.6
    c: Diameter(g165) = 2.6
    c: Diameter(g118) = 2.6
    c: Diameter(g126) = 2.6
    c: Diameter(g134) = 2.6
    c: Diameter(g142) = 2.6
    c: Diameter(g150) = 2.6
    c: Diameter(g158) = 2.6
    c: Diameter(g166) = 2.6
    c: Diameter(g119) = 2.6
    c: Diameter(g127) = 2.6
    c: Diameter(g135) = 2.6
    c: Diameter(g143) = 2.6
    c: Diameter(g151) = 2.6
    c: Diameter(g159) = 2.6
    c: Diameter(g167) = 2.6
    c: Diameter(g120) = 2.6
    c: Diameter(g128) = 2.6
    c: Diameter(g136) = 2.6
    c: Diameter(g144) = 2.6
    c: Diameter(g152) = 2.6
    c: Diameter(g160) = 2.6
    c: Diameter(g168) = 2.6
    c: Diameter(g121) = 2.6
    c: Diameter(g129) = 2.6
    c: Diameter(g137) = 2.6
    c: Diameter(g145) = 2.6
    c: Diameter(g153) = 2.6
    c: Diameter(g161) = 2.6
    c: Diameter(g169) = 2.6
    c: Diameter(g170) = 2.6
    c: Diameter(g176) = 2.6
    c: Diameter(g182) = 2.6
    c: Diameter(g188) = 2.6
    c: Diameter(g194) = 2.6
    c: Diameter(g200) = 2.6
    c: Diameter(g206) = 2.6
    c: Diameter(g171) = 2.6
    c: Diameter(g177) = 2.6
    c: Diameter(g183) = 2.6
    c: Diameter(g189) = 2.6
    c: Diameter(g195) = 2.6
    c: Diameter(g201) = 2.6
    c: Diameter(g207) = 2.6
    c: Diameter(g172) = 2.6
    c: Diameter(g178) = 2.6
    c: Diameter(g184) = 2.6
    c: Diameter(g190) = 2.6
    c: Diameter(g196) = 2.6
    c: Diameter(g202) = 2.6
    c: Diameter(g208) = 2.6
    c: Diameter(g173) = 2.6
    c: Diameter(g179) = 2.6
    c: Diameter(g185) = 2.6
    c: Diameter(g191) = 2.6
    c: Diameter(g197) = 2.6
    c: Diameter(g203) = 2.6
    c: Diameter(g209) = 2.6
    c: Diameter(g174) = 2.6
    c: Diameter(g180) = 2.6
    c: Diameter(g186) = 2.6
    c: Diameter(g192) = 2.6
    c: Diameter(g198) = 2.6
    c: Diameter(g204) = 2.6
    c: Diameter(g210) = 2.6
    c: Diameter(g175) = 2.6
    c: Diameter(g181) = 2.6
    c: Diameter(g187) = 2.6
    c: Diameter(g193) = 2.6
    c: Diameter(g199) = 2.6
    c: Diameter(g205) = 2.6
    c: Diameter(g211) = 2.6
FEATURE [PartDesign::Pocket] Pocket012
  BaseFeature = -> Pad018
  Direction = (-2.80598e-09,0,-1)
  Length = 8
  Length2 = 5
  Placement = pos=(7.67535e-08,-84,27.3536) rot=(0,0,1;3.14159rad)
  Profile = -> Sketch034
  ReferenceAxis = -> Sketch034 [N_Axis]
  Refine = true
  Suppressed = false
  Type = 0
FEATURE [PartDesign::Body] Body008  label="M3 5mm Spaced Mounting Plate"
  AllowCompound = false
  Group = -> [DatumPlane010,CopyPocket011,Sketch032,Pad017,Sketch033,Pad018,Sketch034,Pocket012]
  Origin = -> Origin008
  Tip = -> Pocket012
FEATURE [Sketcher::SketchObject] Sketch035
  ArcFitTolerance = 1e-06
  AttachmentSupport = -> [Pad012]
  FullyConstrained = true
  MakeInternals = false
  MapMode = 5
  Placement = pos=(42.0016,5.00002,14) rot=(0.577354,0.577344,0.577354;4.18878rad)
  sketch-geometry (1):
    g0: Circle CenterX=0 CenterY=0 CenterZ=0 NormalX=0 NormalY=0 NormalZ=1 AngleXU=0 Radius=1.35
  constraints (2):
    c: Diameter(g0) = 2.7
    c: Coincident(g0,g-1)
FEATURE [PartDesign::Pocket] Pocket013
  BaseFeature = -> Pad012
  Direction = (-1.755e-05,-1,-1.0234e-10)
  Length = 5
  Length2 = 5
  Placement = pos=(42,-84,14) rot=(0.57735,-0.57735,0.57735;2.0944rad)
  Profile = -> Sketch035
  ReferenceAxis = -> Sketch035 [N_Axis]
  Refine = true
  Suppressed = false
  Type = 0
FEATURE [Sketcher::SketchObject] Sketch036
  ArcFitTolerance = 1e-06
  AttachmentSupport = -> [Pocket013]
  ExternalGeometry = -> [Pocket013]
  FullyConstrained = true
  MakeInternals = false
  MapMode = 5
  Placement = pos=(42.0016,5.00002,14) rot=(0.577354,0.577344,0.577354;4.18878rad)
  sketch-geometry (2):
    g0: Circle CenterX=0 CenterY=0 CenterZ=0 NormalX=0 NormalY=0 NormalZ=1 AngleXU=0 Radius=2.5
    g1: Circle CenterX=0 CenterY=0 CenterZ=0 NormalX=0 NormalY=0 NormalZ=1 AngleXU=0 Radius=2.9
  constraints (4):
    c: Diameter(g0) = 5
    c: Coincident(g0,g-1)
    c: Coincident(g1,g0)
    c: Tangent(g1,g-3)
FEATURE [PartDesign::Pocket] Pocket014
  BaseFeature = -> Pocket013
  Direction = (-1.755e-05,-1,-1.0234e-10)
  Length = 10
  Length2 = 5
  Placement = pos=(42,-84,14) rot=(0.57735,-0.57735,0.57735;2.0944rad)
  Profile = -> Sketch036
  ReferenceAxis = -> Sketch036 [N_Axis]
  Refine = true
  Suppressed = false
  Type = 0
FEATURE [Sketcher::SketchObject] Sketch037
  ArcFitTolerance = 1e-06
  AttachmentSupport = -> [Pocket011]
  FullyConstrained = true
  MakeInternals = false
  MapMode = 5
  Placement = pos=(84,-84,-1.80021e-08) rot=(0.707107,0,0.707107;3.14159rad)
  sketch-geometry (3):
    g0: Circle CenterX=12.3536 CenterY=-21 CenterZ=0 NormalX=0 NormalY=0 NormalZ=1 AngleXU=0 Radius=3
    g1: Circle CenterX=12.3536 CenterY=-42 CenterZ=0 NormalX=0 NormalY=0 NormalZ=1 AngleXU=0 Radius=3
    g2: Circle CenterX=12.3536 CenterY=-63 CenterZ=0 NormalX=0 NormalY=0 NormalZ=1 AngleXU=0 Radius=3
  constraints (6):
    c: Diameter(g0) = 6
    c: Coincident(g0,g-3)
    c: Diameter(g1) = 6
    c: Coincident(g1,g-4)
    c: Diameter(g2) = 6
    c: Coincident(g2,g-5)
FEATURE [PartDesign::Pocket] Pocket015
  BaseFeature = -> Pocket011
  Direction = (-1,0,2.14311e-10)
  Length = 7
  Length2 = 5
  Placement = pos=(0,-84,2e-15) rot=(1,0,0;1.5708rad)
  Profile = -> Sketch037
  ReferenceAxis = -> Sketch037 [N_Axis]
  Refine = true
  Suppressed = false
  Type = 0
FEATURE [Sketcher::SketchObject] Sketch038
  ArcFitTolerance = 1e-06
  AttachmentSupport = -> [Fillet005]
  ExternalGeometry = -> [Fillet005]
  FullyConstrained = false
  MakeInternals = false
  MapMode = 5
  Placement = pos=(0,0,0) rot=(0.707107,0,-0.707107;3.14159rad)
  sketch-geometry (332):
    g0: LineSegment [constr] StartX=-5 StartY=0 StartZ=0 EndX=-5 EndY=1 EndZ=0
    g1: LineSegment StartX=-5 StartY=1 StartZ=0 EndX=-3.00761 EndY=1.17431 EndZ=0
    g2: LineSegment StartX=-5 StartY=1 StartZ=0 EndX=-3.00761 EndY=0.825689 EndZ=0
    g3: LineSegment StartX=-3.00761 StartY=0.825689 StartZ=0 EndX=-3.00761 EndY=1.17431 EndZ=0
    g4: LineSegment [constr] StartX=-5 StartY=1 StartZ=0 EndX=-5 EndY=2 EndZ=0
    g5: LineSegment StartX=-5 StartY=2 StartZ=0 EndX=-3.00761 EndY=2.17431 EndZ=0
    g6: LineSegment StartX=-5 StartY=2 StartZ=0 EndX=-3.00761 EndY=1.82569 EndZ=0
    g7: LineSegment StartX=-3.00761 StartY=1.82569 StartZ=0 EndX=-3.00761 EndY=2.17431 EndZ=0
    g8: LineSegment [constr] StartX=-5 StartY=2 StartZ=0 EndX=-5 EndY=3 EndZ=0
    g9: LineSegment StartX=-5 StartY=3 StartZ=0 EndX=-3.00761 EndY=3.17431 EndZ=0
    g10: LineSegment StartX=-5 StartY=3 StartZ=0 EndX=-3.00761 EndY=2.82569 EndZ=0
    g11: LineSegment StartX=-3.00761 StartY=2.82569 StartZ=0 EndX=-3.00761 EndY=3.17431 EndZ=0
    g12: LineSegment [constr] StartX=-5 StartY=3 StartZ=0 EndX=-5 EndY=4 EndZ=0
    g13: LineSegment StartX=-5 StartY=4 StartZ=0 EndX=-3.00761 EndY=4.17431 EndZ=0
    g14: LineSegment StartX=-5 StartY=4 StartZ=0 EndX=-3.00761 EndY=3.82569 EndZ=0
    g15: LineSegment StartX=-3.00761 StartY=3.82569 StartZ=0 EndX=-3.00761 EndY=4.17431 EndZ=0
    g16: LineSegment [constr] StartX=-5 StartY=4 StartZ=0 EndX=-5 EndY=5 EndZ=0
    g17: LineSegment StartX=-5 StartY=5 StartZ=0 EndX=-3.00761 EndY=5.17431 EndZ=0
    g18: LineSegment StartX=-5 StartY=5 StartZ=0 EndX=-3.00761 EndY=4.82569 EndZ=0
    g19: LineSegment StartX=-3.00761 StartY=4.82569 StartZ=0 EndX=-3.00761 EndY=5.17431 EndZ=0
    g20: LineSegment [constr] StartX=-5 StartY=5 StartZ=0 EndX=-5 EndY=6 EndZ=0
    g21: LineSegment StartX=-5 StartY=6 StartZ=0 EndX=-3.00761 EndY=6.17431 EndZ=0
    g22: LineSegment StartX=-5 StartY=6 StartZ=0 EndX=-3.00761 EndY=5.82569 EndZ=0
    g23: LineSegment StartX=-3.00761 StartY=5.82569 StartZ=0 EndX=-3.00761 EndY=6.17431 EndZ=0
    g24: LineSegment [constr] StartX=-5 StartY=6 StartZ=0 EndX=-5 EndY=7 EndZ=0
    g25: LineSegment StartX=-5 StartY=7 StartZ=0 EndX=-3.00761 EndY=7.17431 EndZ=0
    g26: LineSegment StartX=-5 StartY=7 StartZ=0 EndX=-3.00761 EndY=6.82569 EndZ=0
    g27: LineSegment StartX=-3.00761 StartY=6.82569 StartZ=0 EndX=-3.00761 EndY=7.17431 EndZ=0
    g28: LineSegment [constr] StartX=-5 StartY=7 StartZ=0 EndX=-5 EndY=8 EndZ=0
    g29: LineSegment StartX=-5 StartY=8 StartZ=0 EndX=-3.00761 EndY=8.17431 EndZ=0
    g30: LineSegment StartX=-5 StartY=8 StartZ=0 EndX=-3.00761 EndY=7.82569 EndZ=0
    g31: LineSegment StartX=-3.00761 StartY=7.82569 StartZ=0 EndX=-3.00761 EndY=8.17431 EndZ=0
    g32: LineSegment [constr] StartX=-5 StartY=8 StartZ=0 EndX=-5 EndY=9 EndZ=0
    g33: LineSegment StartX=-5 StartY=9 StartZ=0 EndX=-3.00761 EndY=9.17431 EndZ=0
    g34: LineSegment StartX=-5 StartY=9 StartZ=0 EndX=-3.00761 EndY=8.82569 EndZ=0
    g35: LineSegment StartX=-3.00761 StartY=8.82569 StartZ=0 EndX=-3.00761 EndY=9.17431 EndZ=0
    g36: LineSegment [constr] StartX=-5 StartY=9 StartZ=0 EndX=-5 EndY=10 EndZ=0
    g37: LineSegment StartX=-5 StartY=10 StartZ=0 EndX=-3.00761 EndY=10.1743 EndZ=0
    g38: LineSegment StartX=-5 StartY=10 StartZ=0 EndX=-3.00761 EndY=9.82569 EndZ=0
    g39: LineSegment StartX=-3.00761 StartY=9.82569 StartZ=0 EndX=-3.00761 EndY=10.1743 EndZ=0
    g40: LineSegment [constr] StartX=-5 StartY=10 StartZ=0 EndX=-5 EndY=11 EndZ=0
    g41: LineSegment StartX=-5 StartY=11 StartZ=0 EndX=-3.00761 EndY=11.1743 EndZ=0
    g42: LineSegment StartX=-5 StartY=11 StartZ=0 EndX=-3.00761 EndY=10.8257 EndZ=0
    g43: LineSegment StartX=-3.00761 StartY=10.8257 StartZ=0 EndX=-3.00761 EndY=11.1743 EndZ=0
    g44: LineSegment [constr] StartX=-5 StartY=11 StartZ=0 EndX=-5 EndY=12 EndZ=0
    g45: LineSegment StartX=-5 StartY=12 StartZ=0 EndX=-3.00761 EndY=12.1743 EndZ=0
    g46: LineSegment StartX=-5 StartY=12 StartZ=0 EndX=-3.00761 EndY=11.8257 EndZ=0
    g47: LineSegment StartX=-3.00761 StartY=11.8257 StartZ=0 EndX=-3.00761 EndY=12.1743 EndZ=0
    g48: LineSegment [constr] StartX=-5 StartY=12 StartZ=0 EndX=-5 EndY=13 EndZ=0
    g49: LineSegment StartX=-5 StartY=13 StartZ=0 EndX=-3.00761 EndY=13.1743 EndZ=0
    g50: LineSegment StartX=-5 StartY=13 StartZ=0 EndX=-3.00761 EndY=12.8257 EndZ=0
    g51: LineSegment StartX=-3.00761 StartY=12.8257 StartZ=0 EndX=-3.00761 EndY=13.1743 EndZ=0
    g52: LineSegment [constr] StartX=-5 StartY=13 StartZ=0 EndX=-5 EndY=14 EndZ=0
    g53: LineSegment StartX=-5 StartY=14 StartZ=0 EndX=-3.00761 EndY=14.1743 EndZ=0
    g54: LineSegment StartX=-5 StartY=14 StartZ=0 EndX=-3.00761 EndY=13.8257 EndZ=0
    g55: LineSegment StartX=-3.00761 StartY=13.8257 StartZ=0 EndX=-3.00761 EndY=14.1743 EndZ=0
    g56: LineSegment [constr] StartX=-5 StartY=14 StartZ=0 EndX=-5 EndY=15 EndZ=0
    g57: LineSegment StartX=-5 StartY=15 StartZ=0 EndX=-3.00761 EndY=15.1743 EndZ=0
    g58: LineSegment StartX=-5 StartY=15 StartZ=0 EndX=-3.00761 EndY=14.8257 EndZ=0
    g59: LineSegment StartX=-3.00761 StartY=14.8257 StartZ=0 EndX=-3.00761 EndY=15.1743 EndZ=0
    g60: LineSegment [constr] StartX=-5 StartY=15 StartZ=0 EndX=-5 EndY=16 EndZ=0
    g61: LineSegment StartX=-5 StartY=16 StartZ=0 EndX=-3.00761 EndY=16.1743 EndZ=0
    g62: LineSegment StartX=-5 StartY=16 StartZ=0 EndX=-3.00761 EndY=15.8257 EndZ=0
    g63: LineSegment StartX=-3.00761 StartY=15.8257 StartZ=0 EndX=-3.00761 EndY=16.1743 EndZ=0
    g64: LineSegment [constr] StartX=-5 StartY=16 StartZ=0 EndX=-5 EndY=17 EndZ=0
    g65: LineSegment StartX=-5 StartY=17 StartZ=0 EndX=-3.00761 EndY=17.1743 EndZ=0
    g66: LineSegment StartX=-5 StartY=17 StartZ=0 EndX=-3.00761 EndY=16.8257 EndZ=0
    g67: LineSegment StartX=-3.00761 StartY=16.8257 StartZ=0 EndX=-3.00761 EndY=17.1743 EndZ=0
    g68: LineSegment [constr] StartX=-5 StartY=17 StartZ=0 EndX=-5 EndY=18 EndZ=0
    g69: LineSegment StartX=-5 StartY=18 StartZ=0 EndX=-3.00761 EndY=18.1743 EndZ=0
    g70: LineSegment StartX=-5 StartY=18 StartZ=0 EndX=-3.00761 EndY=17.8257 EndZ=0
    g71: LineSegment StartX=-3.00761 StartY=17.8257 StartZ=0 EndX=-3.00761 EndY=18.1743 EndZ=0
    g72: LineSegment [constr] StartX=-5 StartY=18 StartZ=0 EndX=-5 EndY=19 EndZ=0
    g73: LineSegment StartX=-5 StartY=19 StartZ=0 EndX=-3.00761 EndY=19.1743 EndZ=0
    g74: LineSegment StartX=-5 StartY=19 StartZ=0 EndX=-3.00761 EndY=18.8257 EndZ=0
    g75: LineSegment StartX=-3.00761 StartY=18.8257 StartZ=0 EndX=-3.00761 EndY=19.1743 EndZ=0
    g76: LineSegment [constr] StartX=-5 StartY=19 StartZ=0 EndX=-5 EndY=20 EndZ=0
    g77: LineSegment StartX=-5 StartY=20 StartZ=0 EndX=-3.00761 EndY=20.1743 EndZ=0
    g78: LineSegment StartX=-5 StartY=20 StartZ=0 EndX=-3.00761 EndY=19.8257 EndZ=0
    g79: LineSegment StartX=-3.00761 StartY=19.8257 StartZ=0 EndX=-3.00761 EndY=20.1743 EndZ=0
    g80: LineSegment [constr] StartX=-5 StartY=20 StartZ=0 EndX=-5 EndY=21 EndZ=0
    g81: LineSegment StartX=-5 StartY=21 StartZ=0 EndX=-3.00761 EndY=21.1743 EndZ=0
    g82: LineSegment StartX=-5 StartY=21 StartZ=0 EndX=-3.00761 EndY=20.8257 EndZ=0
    g83: LineSegment StartX=-3.00761 StartY=20.8257 StartZ=0 EndX=-3.00761 EndY=21.1743 EndZ=0
    g84: LineSegment [constr] StartX=-5 StartY=21 StartZ=0 EndX=-5 EndY=22 EndZ=0
    g85: LineSegment StartX=-5 StartY=22 StartZ=0 EndX=-3.00761 EndY=22.1743 EndZ=0
    g86: LineSegment StartX=-5 StartY=22 StartZ=0 EndX=-3.00761 EndY=21.8257 EndZ=0
    g87: LineSegment StartX=-3.00761 StartY=21.8257 StartZ=0 EndX=-3.00761 EndY=22.1743 EndZ=0
    g88: LineSegment [constr] StartX=-5 StartY=22 StartZ=0 EndX=-5 EndY=23 EndZ=0
    g89: LineSegment StartX=-5 StartY=23 StartZ=0 EndX=-3.00761 EndY=23.1743 EndZ=0
    g90: LineSegment StartX=-5 StartY=23 StartZ=0 EndX=-3.00761 EndY=22.8257 EndZ=0
    g91: LineSegment StartX=-3.00761 StartY=22.8257 StartZ=0 EndX=-3.00761 EndY=23.1743 EndZ=0
    g92: LineSegment [constr] StartX=-5 StartY=23 StartZ=0 EndX=-5 EndY=24 EndZ=0
    g93: LineSegment StartX=-5 StartY=24 StartZ=0 EndX=-3.00761 EndY=24.1743 EndZ=0
    g94: LineSegment StartX=-5 StartY=24 StartZ=0 EndX=-3.00761 EndY=23.8257 EndZ=0
    g95: LineSegment StartX=-3.00761 StartY=23.8257 StartZ=0 EndX=-3.00761 EndY=24.1743 EndZ=0
    g96: LineSegment [constr] StartX=-5 StartY=24 StartZ=0 EndX=-5 EndY=25 EndZ=0
    g97: LineSegment StartX=-5 StartY=25 StartZ=0 EndX=-3.00761 EndY=25.1743 EndZ=0
    g98: LineSegment StartX=-5 StartY=25 StartZ=0 EndX=-3.00761 EndY=24.8257 EndZ=0
    g99: LineSegment StartX=-3.00761 StartY=24.8257 StartZ=0 EndX=-3.00761 EndY=25.1743 EndZ=0
    g100: LineSegment [constr] StartX=-5 StartY=25 StartZ=0 EndX=-5 EndY=26 EndZ=0
    g101: LineSegment StartX=-5 StartY=26 StartZ=0 EndX=-3.00761 EndY=26.1743 EndZ=0
    g102: LineSegment StartX=-5 StartY=26 StartZ=0 EndX=-3.00761 EndY=25.8257 EndZ=0
    g103: LineSegment StartX=-3.00761 StartY=25.8257 StartZ=0 EndX=-3.00761 EndY=26.1743 EndZ=0
    g104: LineSegment [constr] StartX=-5 StartY=26 StartZ=0 EndX=-5 EndY=27 EndZ=0
    g105: LineSegment StartX=-5 StartY=27 StartZ=0 EndX=-3.00761 EndY=27.1743 EndZ=0
    g106: LineSegment StartX=-5 StartY=27 StartZ=0 EndX=-3.00761 EndY=26.8257 EndZ=0
    g107: LineSegment StartX=-3.00761 StartY=26.8257 StartZ=0 EndX=-3.00761 EndY=27.1743 EndZ=0
    g108: LineSegment [constr] StartX=-5 StartY=27 StartZ=0 EndX=-5 EndY=28 EndZ=0
    g109: LineSegment StartX=-5 StartY=28 StartZ=0 EndX=-3.00761 EndY=28.1743 EndZ=0
    g110: LineSegment StartX=-5 StartY=28 StartZ=0 EndX=-3.00761 EndY=27.8257 EndZ=0
    g111: LineSegment StartX=-3.00761 StartY=27.8257 StartZ=0 EndX=-3.00761 EndY=28.1743 EndZ=0
    g112: LineSegment [constr] StartX=-5 StartY=28 StartZ=0 EndX=-5 EndY=29 EndZ=0
    g113: LineSegment StartX=-5 StartY=29 StartZ=0 EndX=-3.00761 EndY=29.1743 EndZ=0
    g114: LineSegment StartX=-5 StartY=29 StartZ=0 EndX=-3.00761 EndY=28.8257 EndZ=0
    g115: LineSegment StartX=-3.00761 StartY=28.8257 StartZ=0 EndX=-3.00761 EndY=29.1743 EndZ=0
    g116: LineSegment [constr] StartX=-5 StartY=29 StartZ=0 EndX=-5 EndY=30 EndZ=0
    g117: LineSegment StartX=-5 StartY=30 StartZ=0 EndX=-3.00761 EndY=30.1743 EndZ=0
    g118: LineSegment StartX=-5 StartY=30 StartZ=0 EndX=-3.00761 EndY=29.8257 EndZ=0
    g119: LineSegment StartX=-3.00761 StartY=29.8257 StartZ=0 EndX=-3.00761 EndY=30.1743 EndZ=0
    g120: LineSegment [constr] StartX=-5 StartY=30 StartZ=0 EndX=-5 EndY=31 EndZ=0
    g121: LineSegment StartX=-5 StartY=31 StartZ=0 EndX=-3.00761 EndY=31.1743 EndZ=0
    g122: LineSegment StartX=-5 StartY=31 StartZ=0 EndX=-3.00761 EndY=30.8257 EndZ=0
    g123: LineSegment StartX=-3.00761 StartY=30.8257 StartZ=0 EndX=-3.00761 EndY=31.1743 EndZ=0
    g124: LineSegment [constr] StartX=-5 StartY=31 StartZ=0 EndX=-5 EndY=32 EndZ=0
    g125: LineSegment StartX=-5 StartY=32 StartZ=0 EndX=-3.00761 EndY=32.1743 EndZ=0
    g126: LineSegment StartX=-5 StartY=32 StartZ=0 EndX=-3.00761 EndY=31.8257 EndZ=0
    g127: LineSegment StartX=-3.00761 StartY=31.8257 StartZ=0 EndX=-3.00761 EndY=32.1743 EndZ=0
    g128: LineSegment [constr] StartX=-5 StartY=32 StartZ=0 EndX=-5 EndY=33 EndZ=0
    g129: LineSegment StartX=-5 StartY=33 StartZ=0 EndX=-3.00761 EndY=33.1743 EndZ=0
    g130: LineSegment StartX=-5 StartY=33 StartZ=0 EndX=-3.00761 EndY=32.8257 EndZ=0
    g131: LineSegment StartX=-3.00761 StartY=32.8257 StartZ=0 EndX=-3.00761 EndY=33.1743 EndZ=0
    g132: LineSegment [constr] StartX=-5 StartY=33 StartZ=0 EndX=-5 EndY=34 EndZ=0
    g133: LineSegment StartX=-5 StartY=34 StartZ=0 EndX=-3.00761 EndY=34.1743 EndZ=0
    g134: LineSegment StartX=-5 StartY=34 StartZ=0 EndX=-3.00761 EndY=33.8257 EndZ=0
    g135: LineSegment StartX=-3.00761 StartY=33.8257 StartZ=0 EndX=-3.00761 EndY=34.1743 EndZ=0
    g136: LineSegment [constr] StartX=-5 StartY=34 StartZ=0 EndX=-5 EndY=35 EndZ=0
    g137: LineSegment StartX=-5 StartY=35 StartZ=0 EndX=-3.00761 EndY=35.1743 EndZ=0
    g138: LineSegment StartX=-5 StartY=35 StartZ=0 EndX=-3.00761 EndY=34.8257 EndZ=0
    g139: LineSegment StartX=-3.00761 StartY=34.8257 StartZ=0 EndX=-3.00761 EndY=35.1743 EndZ=0
    g140: LineSegment [constr] StartX=-5 StartY=35 StartZ=0 EndX=-5 EndY=36 EndZ=0
    g141: LineSegment StartX=-5 StartY=36 StartZ=0 EndX=-3.00761 EndY=36.1743 EndZ=0
    g142: LineSegment StartX=-5 StartY=36 StartZ=0 EndX=-3.00761 EndY=35.8257 EndZ=0
    g143: LineSegment StartX=-3.00761 StartY=35.8257 StartZ=0 EndX=-3.00761 EndY=36.1743 EndZ=0
    g144: LineSegment [constr] StartX=-5 StartY=36 StartZ=0 EndX=-5 EndY=37 EndZ=0
    g145: LineSegment StartX=-5 StartY=37 StartZ=0 EndX=-3.00761 EndY=37.1743 EndZ=0
    g146: LineSegment StartX=-5 StartY=37 StartZ=0 EndX=-3.00761 EndY=36.8257 EndZ=0
    g147: LineSegment StartX=-3.00761 StartY=36.8257 StartZ=0 EndX=-3.00761 EndY=37.1743 EndZ=0
    g148: LineSegment [constr] StartX=-5 StartY=37 StartZ=0 EndX=-5 EndY=38 EndZ=0
    g149: LineSegment StartX=-5 StartY=38 StartZ=0 EndX=-3.00761 EndY=38.1743 EndZ=0
    g150: LineSegment StartX=-5 StartY=38 StartZ=0 EndX=-3.00761 EndY=37.8257 EndZ=0
    g151: LineSegment StartX=-3.00761 StartY=37.8257 StartZ=0 EndX=-3.00761 EndY=38.1743 EndZ=0
    g152: LineSegment [constr] StartX=-5 StartY=38 StartZ=0 EndX=-5 EndY=39 EndZ=0
    g153: LineSegment StartX=-5 StartY=39 StartZ=0 EndX=-3.00761 EndY=39.1743 EndZ=0
    g154: LineSegment StartX=-5 StartY=39 StartZ=0 EndX=-3.00761 EndY=38.8257 EndZ=0
    g155: LineSegment StartX=-3.00761 StartY=38.8257 StartZ=0 EndX=-3.00761 EndY=39.1743 EndZ=0
    g156: LineSegment [constr] StartX=-5 StartY=39 StartZ=0 EndX=-5 EndY=40 EndZ=0
    g157: LineSegment StartX=-5 StartY=40 StartZ=0 EndX=-3.00761 EndY=40.1743 EndZ=0
    g158: LineSegment StartX=-5 StartY=40 StartZ=0 EndX=-3.00761 EndY=39.8257 EndZ=0
    g159: LineSegment StartX=-3.00761 StartY=39.8257 StartZ=0 EndX=-3.00761 EndY=40.1743 EndZ=0
    g160: LineSegment [constr] StartX=-5 StartY=40 StartZ=0 EndX=-5 EndY=41 EndZ=0
    g161: LineSegment StartX=-5 StartY=41 StartZ=0 EndX=-3.00761 EndY=41.1743 EndZ=0
    g162: LineSegment StartX=-5 StartY=41 StartZ=0 EndX=-3.00761 EndY=40.8257 EndZ=0
    g163: LineSegment StartX=-3.00761 StartY=40.8257 StartZ=0 EndX=-3.00761 EndY=41.1743 EndZ=0
    g164: LineSegment [constr] StartX=-5 StartY=41 StartZ=0 EndX=-5 EndY=42 EndZ=0
    g165: LineSegment StartX=-5 StartY=42 StartZ=0 EndX=-3.00761 EndY=42.1743 EndZ=0
    g166: LineSegment StartX=-5 StartY=42 StartZ=0 EndX=-3.00761 EndY=41.8257 EndZ=0
    g167: LineSegment StartX=-3.00761 StartY=41.8257 StartZ=0 EndX=-3.00761 EndY=42.1743 EndZ=0
    g168: LineSegment [constr] StartX=-5 StartY=42 StartZ=0 EndX=-5 EndY=43 EndZ=0
    g169: LineSegment StartX=-5 StartY=43 StartZ=0 EndX=-3.00761 EndY=43.1743 EndZ=0
    g170: LineSegment StartX=-5 StartY=43 StartZ=0 EndX=-3.00761 EndY=42.8257 EndZ=0
    g171: LineSegment StartX=-3.00761 StartY=42.8257 StartZ=0 EndX=-3.00761 EndY=43.1743 EndZ=0
    g172: LineSegment [constr] StartX=-5 StartY=43 StartZ=0 EndX=-5 EndY=44 EndZ=0
    g173: LineSegment StartX=-5 StartY=44 StartZ=0 EndX=-3.00761 EndY=44.1743 EndZ=0
    g174: LineSegment StartX=-5 StartY=44 StartZ=0 EndX=-3.00761 EndY=43.8257 EndZ=0
    g175: LineSegment StartX=-3.00761 StartY=43.8257 StartZ=0 EndX=-3.00761 EndY=44.1743 EndZ=0
    g176: LineSegment [constr] StartX=-5 StartY=44 StartZ=0 EndX=-5 EndY=45 EndZ=0
    g177: LineSegment StartX=-5 StartY=45 StartZ=0 EndX=-3.00761 EndY=45.1743 EndZ=0
    g178: LineSegment StartX=-5 StartY=45 StartZ=0 EndX=-3.00761 EndY=44.8257 EndZ=0
    g179: LineSegment StartX=-3.00761 StartY=44.8257 StartZ=0 EndX=-3.00761 EndY=45.1743 EndZ=0
    g180: LineSegment [constr] StartX=-5 StartY=45 StartZ=0 EndX=-5 EndY=46 EndZ=0
    g181: LineSegment StartX=-5 StartY=46 StartZ=0 EndX=-3.00761 EndY=46.1743 EndZ=0
    g182: LineSegment StartX=-5 StartY=46 StartZ=0 EndX=-3.00761 EndY=45.8257 EndZ=0
    g183: LineSegment StartX=-3.00761 StartY=45.8257 StartZ=0 EndX=-3.00761 EndY=46.1743 EndZ=0
    g184: LineSegment [constr] StartX=-5 StartY=46 StartZ=0 EndX=-5 EndY=47 EndZ=0
    g185: LineSegment StartX=-5 StartY=47 StartZ=0 EndX=-3.00761 EndY=47.1743 EndZ=0
    g186: LineSegment StartX=-5 StartY=47 StartZ=0 EndX=-3.00761 EndY=46.8257 EndZ=0
    g187: LineSegment StartX=-3.00761 StartY=46.8257 StartZ=0 EndX=-3.00761 EndY=47.1743 EndZ=0
    g188: LineSegment [constr] StartX=-5 StartY=47 StartZ=0 EndX=-5 EndY=48 EndZ=0
    g189: LineSegment StartX=-5 StartY=48 StartZ=0 EndX=-3.00761 EndY=48.1743 EndZ=0
    g190: LineSegment StartX=-5 StartY=48 StartZ=0 EndX=-3.00761 EndY=47.8257 EndZ=0
    g191: LineSegment StartX=-3.00761 StartY=47.8257 StartZ=0 EndX=-3.00761 EndY=48.1743 EndZ=0
    g192: LineSegment [constr] StartX=-5 StartY=48 StartZ=0 EndX=-5 EndY=49 EndZ=0
    g193: LineSegment StartX=-5 StartY=49 StartZ=0 EndX=-3.00761 EndY=49.1743 EndZ=0
    g194: LineSegment StartX=-5 StartY=49 StartZ=0 EndX=-3.00761 EndY=48.8257 EndZ=0
    g195: LineSegment StartX=-3.00761 StartY=48.8257 StartZ=0 EndX=-3.00761 EndY=49.1743 EndZ=0
    g196: LineSegment [constr] StartX=-5 StartY=49 StartZ=0 EndX=-5 EndY=50 EndZ=0
    g197: LineSegment StartX=-5 StartY=50 StartZ=0 EndX=-3.00761 EndY=50.1743 EndZ=0
    g198: LineSegment StartX=-5 StartY=50 StartZ=0 EndX=-3.00761 EndY=49.8257 EndZ=0
    g199: LineSegment StartX=-3.00761 StartY=49.8257 StartZ=0 EndX=-3.00761 EndY=50.1743 EndZ=0
    g200: LineSegment [constr] StartX=-5 StartY=50 StartZ=0 EndX=-5 EndY=51 EndZ=0
    g201: LineSegment StartX=-5 StartY=51 StartZ=0 EndX=-3.00761 EndY=51.1743 EndZ=0
    g202: LineSegment StartX=-5 StartY=51 StartZ=0 EndX=-3.00761 EndY=50.8257 EndZ=0
    g203: LineSegment StartX=-3.00761 StartY=50.8257 StartZ=0 EndX=-3.00761 EndY=51.1743 EndZ=0
    g204: LineSegment [constr] StartX=-5 StartY=51 StartZ=0 EndX=-5 EndY=52 EndZ=0
    g205: LineSegment StartX=-5 StartY=52 StartZ=0 EndX=-3.00761 EndY=52.1743 EndZ=0
    g206: LineSegment StartX=-5 StartY=52 StartZ=0 EndX=-3.00761 EndY=51.8257 EndZ=0
    g207: LineSegment StartX=-3.00761 StartY=51.8257 StartZ=0 EndX=-3.00761 EndY=52.1743 EndZ=0
    g208: LineSegment [constr] StartX=-5 StartY=52 StartZ=0 EndX=-5 EndY=53 EndZ=0
    g209: LineSegment StartX=-5 StartY=53 StartZ=0 EndX=-3.00761 EndY=53.1743 EndZ=0
    g210: LineSegment StartX=-5 StartY=53 StartZ=0 EndX=-3.00761 EndY=52.8257 EndZ=0
    g211: LineSegment StartX=-3.00761 StartY=52.8257 StartZ=0 EndX=-3.00761 EndY=53.1743 EndZ=0
    g212: LineSegment [constr] StartX=-5 StartY=53 StartZ=0 EndX=-5 EndY=54 EndZ=0
    g213: LineSegment StartX=-5 StartY=54 StartZ=0 EndX=-3.00761 EndY=54.1743 EndZ=0
    g214: LineSegment StartX=-5 StartY=54 StartZ=0 EndX=-3.00761 EndY=53.8257 EndZ=0
    g215: LineSegment StartX=-3.00761 StartY=53.8257 StartZ=0 EndX=-3.00761 EndY=54.1743 EndZ=0
    g216: LineSegment [constr] StartX=-5 StartY=54 StartZ=0 EndX=-5 EndY=55 EndZ=0
    g217: LineSegment StartX=-5 StartY=55 StartZ=0 EndX=-3.00761 EndY=55.1743 EndZ=0
    g218: LineSegment StartX=-5 StartY=55 StartZ=0 EndX=-3.00761 EndY=54.8257 EndZ=0
    g219: LineSegment StartX=-3.00761 StartY=54.8257 StartZ=0 EndX=-3.00761 EndY=55.1743 EndZ=0
    g220: LineSegment [constr] StartX=-5 StartY=55 StartZ=0 EndX=-5 EndY=56 EndZ=0
    g221: LineSegment StartX=-5 StartY=56 StartZ=0 EndX=-3.00761 EndY=56.1743 EndZ=0
    g222: LineSegment StartX=-5 StartY=56 StartZ=0 EndX=-3.00761 EndY=55.8257 EndZ=0
    g223: LineSegment StartX=-3.00761 StartY=55.8257 StartZ=0 EndX=-3.00761 EndY=56.1743 EndZ=0
    g224: LineSegment [constr] StartX=-5 StartY=56 StartZ=0 EndX=-5 EndY=57 EndZ=0
    g225: LineSegment StartX=-5 StartY=57 StartZ=0 EndX=-3.00761 EndY=57.1743 EndZ=0
    g226: LineSegment StartX=-5 StartY=57 StartZ=0 EndX=-3.00761 EndY=56.8257 EndZ=0
    g227: LineSegment StartX=-3.00761 StartY=56.8257 StartZ=0 EndX=-3.00761 EndY=57.1743 EndZ=0
    g228: LineSegment [constr] StartX=-5 StartY=57 StartZ=0 EndX=-5 EndY=58 EndZ=0
    g229: LineSegment StartX=-5 StartY=58 StartZ=0 EndX=-3.00761 EndY=58.1743 EndZ=0
    g230: LineSegment StartX=-5 StartY=58 StartZ=0 EndX=-3.00761 EndY=57.8257 EndZ=0
    g231: LineSegment StartX=-3.00761 StartY=57.8257 StartZ=0 EndX=-3.00761 EndY=58.1743 EndZ=0
    g232: LineSegment [constr] StartX=-5 StartY=58 StartZ=0 EndX=-5 EndY=59 EndZ=0
    g233: LineSegment StartX=-5 StartY=59 StartZ=0 EndX=-3.00761 EndY=59.1743 EndZ=0
    g234: LineSegment StartX=-5 StartY=59 StartZ=0 EndX=-3.00761 EndY=58.8257 EndZ=0
    g235: LineSegment StartX=-3.00761 StartY=58.8257 StartZ=0 EndX=-3.00761 EndY=59.1743 EndZ=0
    g236: LineSegment [constr] StartX=-5 StartY=59 StartZ=0 EndX=-5 EndY=60 EndZ=0
    g237: LineSegment StartX=-5 StartY=60 StartZ=0 EndX=-3.00761 EndY=60.1743 EndZ=0
    g238: LineSegment StartX=-5 StartY=60 StartZ=0 EndX=-3.00761 EndY=59.8257 EndZ=0
    g239: LineSegment StartX=-3.00761 StartY=59.8257 StartZ=0 EndX=-3.00761 EndY=60.1743 EndZ=0
    g240: LineSegment [constr] StartX=-5 StartY=60 StartZ=0 EndX=-5 EndY=61 EndZ=0
    g241: LineSegment StartX=-5 StartY=61 StartZ=0 EndX=-3.00761 EndY=61.1743 EndZ=0
    g242: LineSegment StartX=-5 StartY=61 StartZ=0 EndX=-3.00761 EndY=60.8257 EndZ=0
    g243: LineSegment StartX=-3.00761 StartY=60.8257 StartZ=0 EndX=-3.00761 EndY=61.1743 EndZ=0
    g244: LineSegment [constr] StartX=-5 StartY=61 StartZ=0 EndX=-5 EndY=62 EndZ=0
    g245: LineSegment StartX=-5 StartY=62 StartZ=0 EndX=-3.00761 EndY=62.1743 EndZ=0
    g246: LineSegment StartX=-5 StartY=62 StartZ=0 EndX=-3.00761 EndY=61.8257 EndZ=0
    g247: LineSegment StartX=-3.00761 StartY=61.8257 StartZ=0 EndX=-3.00761 EndY=62.1743 EndZ=0
    g248: LineSegment [constr] StartX=-5 StartY=62 StartZ=0 EndX=-5 EndY=63 EndZ=0
    g249: LineSegment StartX=-5 StartY=63 StartZ=0 EndX=-3.00761 EndY=63.1743 EndZ=0
    g250: LineSegment StartX=-5 StartY=63 StartZ=0 EndX=-3.00761 EndY=62.8257 EndZ=0
    g251: LineSegment StartX=-3.00761 StartY=62.8257 StartZ=0 EndX=-3.00761 EndY=63.1743 EndZ=0
    g252: LineSegment [constr] StartX=-5 StartY=63 StartZ=0 EndX=-5 EndY=64 EndZ=0
    g253: LineSegment StartX=-5 StartY=64 StartZ=0 EndX=-3.00761 EndY=64.1743 EndZ=0
    g254: LineSegment StartX=-5 StartY=64 StartZ=0 EndX=-3.00761 EndY=63.8257 EndZ=0
    g255: LineSegment StartX=-3.00761 StartY=63.8257 StartZ=0 EndX=-3.00761 EndY=64.1743 EndZ=0
    g256: LineSegment [constr] StartX=-5 StartY=64 StartZ=0 EndX=-5 EndY=65 EndZ=0
    g257: LineSegment StartX=-5 StartY=65 StartZ=0 EndX=-3.00761 EndY=65.1743 EndZ=0
    g258: LineSegment StartX=-5 StartY=65 StartZ=0 EndX=-3.00761 EndY=64.8257 EndZ=0
    g259: LineSegment StartX=-3.00761 StartY=64.8257 StartZ=0 EndX=-3.00761 EndY=65.1743 EndZ=0
    g260: LineSegment [constr] StartX=-5 StartY=65 StartZ=0 EndX=-5 EndY=66 EndZ=0
    g261: LineSegment StartX=-5 StartY=66 StartZ=0 EndX=-3.00761 EndY=66.1743 EndZ=0
    g262: LineSegment StartX=-5 StartY=66 StartZ=0 EndX=-3.00761 EndY=65.8257 EndZ=0
    g263: LineSegment StartX=-3.00761 StartY=65.8257 StartZ=0 EndX=-3.00761 EndY=66.1743 EndZ=0
    g264: LineSegment [constr] StartX=-5 StartY=66 StartZ=0 EndX=-5 EndY=67 EndZ=0
    g265: LineSegment StartX=-5 StartY=67 StartZ=0 EndX=-3.00761 EndY=67.1743 EndZ=0
    g266: LineSegment StartX=-5 StartY=67 StartZ=0 EndX=-3.00761 EndY=66.8257 EndZ=0
    g267: LineSegment StartX=-3.00761 StartY=66.8257 StartZ=0 EndX=-3.00761 EndY=67.1743 EndZ=0
    g268: LineSegment [constr] StartX=-5 StartY=67 StartZ=0 EndX=-5 EndY=68 EndZ=0
    g269: LineSegment StartX=-5 StartY=68 StartZ=0 EndX=-3.00761 EndY=68.1743 EndZ=0
    g270: LineSegment StartX=-5 StartY=68 StartZ=0 EndX=-3.00761 EndY=67.8257 EndZ=0
    g271: LineSegment StartX=-3.00761 StartY=67.8257 StartZ=0 EndX=-3.00761 EndY=68.1743 EndZ=0
    g272: LineSegment [constr] StartX=-5 StartY=68 StartZ=0 EndX=-5 EndY=69 EndZ=0
    g273: LineSegment StartX=-5 StartY=69 StartZ=0 EndX=-3.00761 EndY=69.1743 EndZ=0
    g274: LineSegment StartX=-5 StartY=69 StartZ=0 EndX=-3.00761 EndY=68.8257 EndZ=0
    g275: LineSegment StartX=-3.00761 StartY=68.8257 StartZ=0 EndX=-3.00761 EndY=69.1743 EndZ=0
    g276: LineSegment [constr] StartX=-5 StartY=69 StartZ=0 EndX=-5 EndY=70 EndZ=0
    g277: LineSegment StartX=-5 StartY=70 StartZ=0 EndX=-3.00761 EndY=70.1743 EndZ=0
    g278: LineSegment StartX=-5 StartY=70 StartZ=0 EndX=-3.00761 EndY=69.8257 EndZ=0
    g279: LineSegment StartX=-3.00761 StartY=69.8257 StartZ=0 EndX=-3.00761 EndY=70.1743 EndZ=0
    g280: LineSegment [constr] StartX=-5 StartY=70 StartZ=0 EndX=-5 EndY=71 EndZ=0
    g281: LineSegment StartX=-5 StartY=71 StartZ=0 EndX=-3.00761 EndY=71.1743 EndZ=0
    g282: LineSegment StartX=-5 StartY=71 StartZ=0 EndX=-3.00761 EndY=70.8257 EndZ=0
    g283: LineSegment StartX=-3.00761 StartY=70.8257 StartZ=0 EndX=-3.00761 EndY=71.1743 EndZ=0
    g284: LineSegment [constr] StartX=-5 StartY=71 StartZ=0 EndX=-5 EndY=72 EndZ=0
    g285: LineSegment StartX=-5 StartY=72 StartZ=0 EndX=-3.00761 EndY=72.1743 EndZ=0
    g286: LineSegment StartX=-5 StartY=72 StartZ=0 EndX=-3.00761 EndY=71.8257 EndZ=0
    g287: LineSegment StartX=-3.00761 StartY=71.8257 StartZ=0 EndX=-3.00761 EndY=72.1743 EndZ=0
    g288: LineSegment [constr] StartX=-5 StartY=72 StartZ=0 EndX=-5 EndY=73 EndZ=0
    g289: LineSegment StartX=-5 StartY=73 StartZ=0 EndX=-3.00761 EndY=73.1743 EndZ=0
    g290: LineSegment StartX=-5 StartY=73 StartZ=0 EndX=-3.00761 EndY=72.8257 EndZ=0
    g291: LineSegment StartX=-3.00761 StartY=72.8257 StartZ=0 EndX=-3.00761 EndY=73.1743 EndZ=0
    g292: LineSegment [constr] StartX=-5 StartY=73 StartZ=0 EndX=-5 EndY=74 EndZ=0
    g293: LineSegment StartX=-5 StartY=74 StartZ=0 EndX=-3.00761 EndY=74.1743 EndZ=0
    g294: LineSegment StartX=-5 StartY=74 StartZ=0 EndX=-3.00761 EndY=73.8257 EndZ=0
    g295: LineSegment StartX=-3.00761 StartY=73.8257 StartZ=0 EndX=-3.00761 EndY=74.1743 EndZ=0
    g296: LineSegment [constr] StartX=-5 StartY=74 StartZ=0 EndX=-5 EndY=75 EndZ=0
    g297: LineSegment StartX=-5 StartY=75 StartZ=0 EndX=-3.00761 EndY=75.1743 EndZ=0
    g298: LineSegment StartX=-5 StartY=75 StartZ=0 EndX=-3.00761 EndY=74.8257 EndZ=0
    g299: LineSegment StartX=-3.00761 StartY=74.8257 StartZ=0 EndX=-3.00761 EndY=75.1743 EndZ=0
    g300: LineSegment [constr] StartX=-5 StartY=75 StartZ=0 EndX=-5 EndY=76 EndZ=0
    g301: LineSegment StartX=-5 StartY=76 StartZ=0 EndX=-3.00761 EndY=76.1743 EndZ=0
    g302: LineSegment StartX=-5 StartY=76 StartZ=0 EndX=-3.00761 EndY=75.8257 EndZ=0
    g303: LineSegment StartX=-3.00761 StartY=75.8257 StartZ=0 EndX=-3.00761 EndY=76.1743 EndZ=0
    g304: LineSegment [constr] StartX=-5 StartY=76 StartZ=0 EndX=-5 EndY=77 EndZ=0
    g305: LineSegment StartX=-5 StartY=77 StartZ=0 EndX=-3.00761 EndY=77.1743 EndZ=0
    g306: LineSegment StartX=-5 StartY=77 StartZ=0 EndX=-3.00761 EndY=76.8257 EndZ=0
    g307: LineSegment StartX=-3.00761 StartY=76.8257 StartZ=0 EndX=-3.00761 EndY=77.1743 EndZ=0
    g308: LineSegment [constr] StartX=-5 StartY=77 StartZ=0 EndX=-5 EndY=78 EndZ=0
    g309: LineSegment StartX=-5 StartY=78 StartZ=0 EndX=-3.00761 EndY=78.1743 EndZ=0
    g310: LineSegment StartX=-5 StartY=78 StartZ=0 EndX=-3.00761 EndY=77.8257 EndZ=0
    g311: LineSegment StartX=-3.00761 StartY=77.8257 StartZ=0 EndX=-3.00761 EndY=78.1743 EndZ=0
    g312: LineSegment [constr] StartX=-5 StartY=78 StartZ=0 EndX=-5 EndY=79 EndZ=0
    g313: LineSegment StartX=-5 StartY=79 StartZ=0 EndX=-3.00761 EndY=79.1743 EndZ=0
    g314: LineSegment StartX=-5 StartY=79 StartZ=0 EndX=-3.00761 EndY=78.8257 EndZ=0
    g315: LineSegment StartX=-3.00761 StartY=78.8257 StartZ=0 EndX=-3.00761 EndY=79.1743 EndZ=0
    g316: LineSegment [constr] StartX=-5 StartY=79 StartZ=0 EndX=-5 EndY=80 EndZ=0
    g317: LineSegment StartX=-5 StartY=80 StartZ=0 EndX=-3.00761 EndY=80.1743 EndZ=0
    g318: LineSegment StartX=-5 StartY=80 StartZ=0 EndX=-3.00761 EndY=79.8257 EndZ=0
    g319: LineSegment StartX=-3.00761 StartY=79.8257 StartZ=0 EndX=-3.00761 EndY=80.1743 EndZ=0
    g320: LineSegment [constr] StartX=-5 StartY=80 StartZ=0 EndX=-5 EndY=81 EndZ=0
    g321: LineSegment StartX=-5 StartY=81 StartZ=0 EndX=-3.00761 EndY=81.1743 EndZ=0
    g322: LineSegment StartX=-5 StartY=81 StartZ=0 EndX=-3.00761 EndY=80.8257 EndZ=0
    g323: LineSegment StartX=-3.00761 StartY=80.8257 StartZ=0 EndX=-3.00761 EndY=81.1743 EndZ=0
    g324: LineSegment [constr] StartX=-5 StartY=81 StartZ=0 EndX=-5 EndY=82 EndZ=0
    g325: LineSegment StartX=-5 StartY=82 StartZ=0 EndX=-3.00761 EndY=82.1743 EndZ=0
    g326: LineSegment StartX=-5 StartY=82 StartZ=0 EndX=-3.00761 EndY=81.8257 EndZ=0
    g327: LineSegment StartX=-3.00761 StartY=81.8257 StartZ=0 EndX=-3.00761 EndY=82.1743 EndZ=0
    g328: LineSegment [constr] StartX=-5 StartY=82 StartZ=0 EndX=-5 EndY=83 EndZ=0
    g329: LineSegment StartX=-5 StartY=83 StartZ=0 EndX=-3.00761 EndY=83.1743 EndZ=0
    g330: LineSegment StartX=-5 StartY=83 StartZ=0 EndX=-3.00761 EndY=82.8257 EndZ=0
    g331: LineSegment StartX=-3.00761 StartY=82.8257 StartZ=0 EndX=-3.00761 EndY=83.1743 EndZ=0
  constraints (339):
    c: Distance(g0) = 1
    c: Coincident(g0,g-4)
    c: PointOnObject(g0,g-3)
    c: Distance(g1) = 2
    c: Angle(g-1,g1) = 0.0872665
    c: Coincident(g1,g0)
    c: Distance(g2) = 2
    c: Angle(g-1,g2) = -0.0872665
    c: Coincident(g2,g0)
    c: Coincident(g3,g2)
    c: Coincident(g3,g1)
    c: Coincident(g5,g4)
    c: Coincident(g9,g8)
    c: Coincident(g13,g12)
    c: Coincident(g17,g16)
    c: Coincident(g21,g20)
    c: Coincident(g25,g24)
    c: Coincident(g29,g28)
    c: Coincident(g33,g32)
    c: Coincident(g37,g36)
    c: Coincident(g41,g40)
    c: Coincident(g45,g44)
    c: Coincident(g49,g48)
    c: Coincident(g53,g52)
    c: Coincident(g57,g56)
    c: Coincident(g61,g60)
    c: Coincident(g65,g64)
    c: Coincident(g69,g68)
    c: Coincident(g73,g72)
    c: Coincident(g77,g76)
    c: Coincident(g81,g80)
    c: Coincident(g85,g84)
    c: Coincident(g89,g88)
    c: Coincident(g93,g92)
    c: Coincident(g97,g96)
    c: Coincident(g101,g100)
    c: Coincident(g105,g104)
    c: Coincident(g109,g108)
    c: Coincident(g113,g112)
    c: Coincident(g117,g116)
    c: Coincident(g121,g120)
    c: Coincident(g125,g124)
    c: Coincident(g129,g128)
    c: Coincident(g133,g132)
    c: Coincident(g137,g136)
    c: Coincident(g141,g140)
    c: Coincident(g145,g144)
    c: Coincident(g149,g148)
    c: Coincident(g153,g152)
    c: Coincident(g157,g156)
    c: Coincident(g161,g160)
    c: Coincident(g165,g164)
    c: Coincident(g169,g168)
    c: Coincident(g173,g172)
    c: Coincident(g177,g176)
    c: Coincident(g181,g180)
    c: Coincident(g185,g184)
    c: Coincident(g189,g188)
    c: Coincident(g193,g192)
    c: Coincident(g197,g196)
    c: Coincident(g201,g200)
    c: Coincident(g205,g204)
    c: Coincident(g209,g208)
    c: Coincident(g213,g212)
    c: Coincident(g217,g216)
    c: Coincident(g221,g220)
    c: Coincident(g225,g224)
    c: Coincident(g229,g228)
    c: Coincident(g233,g232)
    c: Coincident(g237,g236)
    c: Coincident(g241,g240)
    c: Coincident(g245,g244)
    c: Coincident(g249,g248)
    c: Coincident(g253,g252)
    c: Coincident(g257,g256)
    c: Coincident(g261,g260)
    c: Coincident(g265,g264)
    c: Coincident(g269,g268)
    c: Coincident(g273,g272)
    c: Coincident(g277,g276)
    c: Coincident(g281,g280)
    c: Coincident(g285,g284)
    c: Coincident(g289,g288)
    c: Coincident(g293,g292)
    c: Coincident(g297,g296)
    c: Coincident(g301,g300)
    c: Coincident(g305,g304)
    c: Coincident(g309,g308)
    c: Coincident(g313,g312)
    c: Coincident(g317,g316)
    c: Coincident(g321,g320)
    c: Coincident(g325,g324)
    c: Coincident(g329,g328)
    c: Coincident(g6,g4)
    c: Coincident(g10,g8)
    c: Coincident(g14,g12)
    c: Coincident(g18,g16)
    c: Coincident(g22,g20)
    c: Coincident(g26,g24)
    c: Coincident(g30,g28)
    c: Coincident(g34,g32)
    c: Coincident(g38,g36)
    c: Coincident(g42,g40)
    c: Coincident(g46,g44)
    c: Coincident(g50,g48)
    c: Coincident(g54,g52)
    c: Coincident(g58,g56)
    c: Coincident(g62,g60)
    c: Coincident(g66,g64)
    c: Coincident(g70,g68)
    c: Coincident(g74,g72)
    c: Coincident(g78,g76)
    c: Coincident(g82,g80)
    c: Coincident(g86,g84)
    c: Coincident(g90,g88)
    c: Coincident(g94,g92)
    c: Coincident(g98,g96)
    c: Coincident(g102,g100)
    c: Coincident(g106,g104)
    c: Coincident(g110,g108)
    c: Coincident(g114,g112)
    c: Coincident(g118,g116)
    c: Coincident(g122,g120)
    c: Coincident(g126,g124)
    c: Coincident(g130,g128)
    c: Coincident(g134,g132)
    c: Coincident(g138,g136)
    c: Coincident(g142,g140)
    c: Coincident(g146,g144)
    c: Coincident(g150,g148)
    c: Coincident(g154,g152)
    c: Coincident(g158,g156)
    c: Coincident(g162,g160)
    c: Coincident(g166,g164)
    c: Coincident(g170,g168)
    c: Coincident(g174,g172)
    c: Coincident(g178,g176)
    c: Coincident(g182,g180)
    c: Coincident(g186,g184)
    c: Coincident(g190,g188)
    c: Coincident(g194,g192)
    c: Coincident(g198,g196)
    c: Coincident(g202,g200)
    c: Coincident(g206,g204)
    c: Coincident(g210,g208)
    c: Coincident(g214,g212)
    c: Coincident(g218,g216)
    c: Coincident(g222,g220)
    c: Coincident(g226,g224)
    c: Coincident(g230,g228)
    c: Coincident(g234,g232)
    c: Coincident(g238,g236)
    c: Coincident(g242,g240)
    c: Coincident(g246,g244)
    c: Coincident(g250,g248)
    c: Coincident(g254,g252)
    c: Coincident(g258,g256)
    c: Coincident(g262,g260)
    c: Coincident(g266,g264)
    c: Coincident(g270,g268)
    c: Coincident(g274,g272)
    c: Coincident(g278,g276)
    c: Coincident(g282,g280)
    c: Coincident(g286,g284)
    c: Coincident(g290,g288)
    c: Coincident(g294,g292)
    c: Coincident(g298,g296)
    c: Coincident(g302,g300)
    c: Coincident(g306,g304)
    c: Coincident(g310,g308)
    c: Coincident(g314,g312)
    c: Coincident(g318,g316)
    c: Coincident(g322,g320)
    c: Coincident(g326,g324)
    c: Coincident(g330,g328)
    c: Coincident(g7,g6)
    c: Coincident(g11,g10)
    c: Coincident(g15,g14)
    c: Coincident(g19,g18)
    c: Coincident(g23,g22)
    c: Coincident(g27,g26)
    c: Coincident(g31,g30)
    c: Coincident(g35,g34)
    c: Coincident(g39,g38)
    c: Coincident(g43,g42)
    c: Coincident(g47,g46)
    c: Coincident(g51,g50)
    c: Coincident(g55,g54)
    c: Coincident(g59,g58)
    c: Coincident(g63,g62)
    c: Coincident(g67,g66)
    c: Coincident(g71,g70)
    c: Coincident(g75,g74)
    c: Coincident(g79,g78)
    c: Coincident(g83,g82)
    c: Coincident(g87,g86)
    c: Coincident(g91,g90)
    c: Coincident(g95,g94)
    c: Coincident(g99,g98)
    c: Coincident(g103,g102)
    c: Coincident(g107,g106)
    c: Coincident(g111,g110)
    c: Coincident(g115,g114)
    c: Coincident(g119,g118)
    c: Coincident(g123,g122)
    c: Coincident(g127,g126)
    c: Coincident(g131,g130)
    c: Coincident(g135,g134)
    c: Coincident(g139,g138)
    c: Coincident(g143,g142)
    c: Coincident(g147,g146)
    c: Coincident(g151,g150)
    c: Coincident(g155,g154)
    c: Coincident(g159,g158)
    c: Coincident(g163,g162)
    c: Coincident(g167,g166)
    c: Coincident(g171,g170)
    c: Coincident(g175,g174)
    c: Coincident(g179,g178)
    c: Coincident(g183,g182)
    c: Coincident(g187,g186)
    c: Coincident(g191,g190)
    c: Coincident(g195,g194)
    c: Coincident(g199,g198)
    c: Coincident(g203,g202)
    c: Coincident(g207,g206)
    c: Coincident(g211,g210)
    c: Coincident(g215,g214)
    c: Coincident(g219,g218)
    c: Coincident(g223,g222)
    c: Coincident(g227,g226)
    c: Coincident(g231,g230)
    c: Coincident(g235,g234)
    c: Coincident(g239,g238)
    c: Coincident(g243,g242)
    c: Coincident(g247,g246)
    c: Coincident(g251,g250)
    c: Coincident(g255,g254)
    c: Coincident(g259,g258)
    c: Coincident(g263,g262)
    c: Coincident(g267,g266)
    c: Coincident(g271,g270)
    c: Coincident(g275,g274)
    c: Coincident(g279,g278)
    c: Coincident(g283,g282)
    c: Coincident(g287,g286)
    c: Coincident(g291,g290)
    c: Coincident(g295,g294)
    c: Coincident(g299,g298)
    c: Coincident(g303,g302)
    c: Coincident(g307,g306)
    c: Coincident(g311,g310)
    c: Coincident(g315,g314)
    c: Coincident(g319,g318)
    c: Coincident(g323,g322)
    c: Coincident(g327,g326)
    c: Coincident(g331,g330)
    c: Coincident(g7,g5)
    c: Coincident(g11,g9)
    c: Coincident(g15,g13)
    c: Coincident(g19,g17)
    c: Coincident(g23,g21)
    c: Coincident(g27,g25)
    c: Coincident(g31,g29)
    c: Coincident(g35,g33)
    c: Coincident(g39,g37)
    c: Coincident(g43,g41)
    c: Coincident(g47,g45)
    c: Coincident(g51,g49)
    c: Coincident(g55,g53)
    c: Coincident(g59,g57)
    c: Coincident(g63,g61)
    c: Coincident(g67,g65)
    c: Coincident(g71,g69)
    c: Coincident(g75,g73)
    c: Coincident(g79,g77)
    c: Coincident(g83,g81)
    c: Coincident(g87,g85)
    c: Coincident(g91,g89)
    c: Coincident(g95,g93)
    c: Coincident(g99,g97)
    c: Coincident(g103,g101)
    c: Coincident(g107,g105)
    c: Coincident(g111,g109)
    c: Coincident(g115,g113)
    c: Coincident(g119,g117)
    c: Coincident(g123,g121)
    c: Coincident(g127,g125)
    c: Coincident(g131,g129)
    c: Coincident(g135,g133)
    c: Coincident(g139,g137)
    c: Coincident(g143,g141)
    c: Coincident(g147,g145)
    c: Coincident(g151,g149)
    c: Coincident(g155,g153)
    c: Coincident(g159,g157)
    c: Coincident(g163,g161)
    c: Coincident(g167,g165)
    c: Coincident(g171,g169)
    c: Coincident(g175,g173)
    c: Coincident(g179,g177)
    c: Coincident(g183,g181)
    c: Coincident(g187,g185)
    c: Coincident(g191,g189)
    c: Coincident(g195,g193)
    c: Coincident(g199,g197)
    c: Coincident(g203,g201)
    c: Coincident(g207,g205)
    c: Coincident(g211,g209)
    c: Coincident(g215,g213)
    c: Coincident(g219,g217)
    c: Coincident(g223,g221)
    c: Coincident(g227,g225)
    c: Coincident(g231,g229)
    c: Coincident(g235,g233)
    c: Coincident(g239,g237)
    c: Coincident(g243,g241)
    c: Coincident(g247,g245)
    c: Coincident(g251,g249)
    c: Coincident(g255,g253)
    c: Coincident(g259,g257)
    c: Coincident(g263,g261)
    c: Coincident(g267,g265)
    c: Coincident(g271,g269)
    c: Coincident(g275,g273)
    c: Coincident(g279,g277)
    c: Coincident(g283,g281)
    c: Coincident(g287,g285)
    c: Coincident(g291,g289)
    c: Coincident(g295,g293)
    c: Coincident(g299,g297)
    c: Coincident(g303,g301)
    c: Coincident(g307,g305)
    c: Coincident(g311,g309)
    c: Coincident(g315,g313)
    c: Coincident(g319,g317)
    c: Coincident(g323,g321)
    c: Coincident(g327,g325)
    c: Coincident(g331,g329)
FEATURE [PartDesign::Pocket] Pocket016
  BaseFeature = -> Fillet005
  Direction = (1,0,2e-16)
  Length = 0.5
  Length2 = 5
  Placement = pos=(0,0,0) rot=(1,0,0;1.5708rad)
  Profile = -> Sketch038
  ReferenceAxis = -> Sketch038 [N_Axis]
  Refine = true
  Suppressed = false
  Type = 0
FEATURE [Sketcher::SketchObject] Sketch039
  ArcFitTolerance = 1e-06
  AttachmentSupport = -> [Pocket015]
  ExternalGeometry = -> [Pocket015]
  FullyConstrained = false
  MakeInternals = false
  MapMode = 5
  Placement = pos=(-1.2282e-09,-84,2e-15) rot=(-0.707107,0,0.707107;3.14159rad)
  sketch-geometry (68):
    g0: LineSegment [constr] StartX=-5.35355 StartY=-84 StartZ=0 EndX=-5.35355 EndY=-75 EndZ=0
    g1: LineSegment StartX=-5.35355 StartY=-75 StartZ=0 EndX=-7.34594 EndY=-74.8257 EndZ=0
    g2: LineSegment StartX=-5.35355 StartY=-75 StartZ=0 EndX=-7.34594 EndY=-75.1743 EndZ=0
    g3: LineSegment StartX=-7.34594 StartY=-75.1743 StartZ=0 EndX=-7.34594 EndY=-74.8257 EndZ=0
    g4: LineSegment StartX=-5.35355 StartY=-75.9 StartZ=0 EndX=-7.34594 EndY=-75.7257 EndZ=0
    g5: LineSegment StartX=-5.35355 StartY=-75.9 StartZ=0 EndX=-7.34594 EndY=-76.0743 EndZ=0
    g6: LineSegment StartX=-7.34594 StartY=-76.0743 StartZ=0 EndX=-7.34594 EndY=-75.7257 EndZ=0
    g7: LineSegment StartX=-5.35355 StartY=-76.8 StartZ=0 EndX=-7.34594 EndY=-76.6257 EndZ=0
    g8: LineSegment StartX=-5.35355 StartY=-76.8 StartZ=0 EndX=-7.34594 EndY=-76.9743 EndZ=0
    g9: LineSegment StartX=-7.34594 StartY=-76.9743 StartZ=0 EndX=-7.34594 EndY=-76.6257 EndZ=0
    g10: LineSegment StartX=-5.35355 StartY=-77.7 StartZ=0 EndX=-7.34594 EndY=-77.5257 EndZ=0
    g11: LineSegment StartX=-5.35355 StartY=-77.7 StartZ=0 EndX=-7.34594 EndY=-77.8743 EndZ=0
    g12: LineSegment StartX=-7.34594 StartY=-77.8743 StartZ=0 EndX=-7.34594 EndY=-77.5257 EndZ=0
    g13: LineSegment StartX=-5.35355 StartY=-78.6 StartZ=0 EndX=-7.34594 EndY=-78.4257 EndZ=0
    g14: LineSegment StartX=-5.35355 StartY=-78.6 StartZ=0 EndX=-7.34594 EndY=-78.7743 EndZ=0
    g15: LineSegment StartX=-7.34594 StartY=-78.7743 StartZ=0 EndX=-7.34594 EndY=-78.4257 EndZ=0
    g16: LineSegment StartX=-5.35355 StartY=-79.5 StartZ=0 EndX=-7.34594 EndY=-79.3257 EndZ=0
    g17: LineSegment StartX=-5.35355 StartY=-79.5 StartZ=0 EndX=-7.34594 EndY=-79.6743 EndZ=0
    g18: LineSegment StartX=-7.34594 StartY=-79.6743 StartZ=0 EndX=-7.34594 EndY=-79.3257 EndZ=0
    g19: LineSegment StartX=-5.35355 StartY=-80.4 StartZ=0 EndX=-7.34594 EndY=-80.2257 EndZ=0
    g20: LineSegment StartX=-5.35355 StartY=-80.4 StartZ=0 EndX=-7.34594 EndY=-80.5743 EndZ=0
    g21: LineSegment StartX=-7.34594 StartY=-80.5743 StartZ=0 EndX=-7.34594 EndY=-80.2257 EndZ=0
    g22: LineSegment StartX=-5.35355 StartY=-81.3 StartZ=0 EndX=-7.34594 EndY=-81.1257 EndZ=0
    g23: LineSegment StartX=-5.35355 StartY=-81.3 StartZ=0 EndX=-7.34594 EndY=-81.4743 EndZ=0
    g24: LineSegment StartX=-7.34594 StartY=-81.4743 StartZ=0 EndX=-7.34594 EndY=-81.1257 EndZ=0
    g25: LineSegment StartX=-5.35355 StartY=-82.2 StartZ=0 EndX=-7.34594 EndY=-82.0257 EndZ=0
    g26: LineSegment StartX=-5.35355 StartY=-82.2 StartZ=0 EndX=-7.34594 EndY=-82.3743 EndZ=0
    g27: LineSegment StartX=-7.34594 StartY=-82.3743 StartZ=0 EndX=-7.34594 EndY=-82.0257 EndZ=0
    g28: LineSegment StartX=-5.35355 StartY=-83.1 StartZ=0 EndX=-7.34594 EndY=-82.9257 EndZ=0
    g29: LineSegment StartX=-5.35355 StartY=-83.1 StartZ=0 EndX=-7.34594 EndY=-83.2743 EndZ=0
    g30: LineSegment StartX=-7.34594 StartY=-83.2743 StartZ=0 EndX=-7.34594 EndY=-82.9257 EndZ=0
    g31: LineSegment [constr] StartX=-5.35355 StartY=0 StartZ=0 EndX=-5.35355 EndY=-9 EndZ=0
    g32: LineSegment StartX=-5.35355 StartY=-9 StartZ=0 EndX=-7.34594 EndY=-9.17431 EndZ=0
    g33: LineSegment StartX=-5.35355 StartY=-9 StartZ=0 EndX=-7.34594 EndY=-8.82569 EndZ=0
    g34: LineSegment StartX=-7.34594 StartY=-8.82569 StartZ=0 EndX=-7.34594 EndY=-9.17431 EndZ=0
    g35: LineSegment StartX=-5.35355 StartY=-8.1 StartZ=0 EndX=-7.34594 EndY=-8.27431 EndZ=0
    g36: LineSegment StartX=-5.35355 StartY=-8.1 StartZ=0 EndX=-7.34594 EndY=-7.92569 EndZ=0
    g37: LineSegment StartX=-7.34594 StartY=-7.92569 StartZ=0 EndX=-7.34594 EndY=-8.27431 EndZ=0
    g38: LineSegment StartX=-5.35355 StartY=-7.2 StartZ=0 EndX=-7.34594 EndY=-7.37431 EndZ=0
    g39: LineSegment StartX=-5.35355 StartY=-7.2 StartZ=0 EndX=-7.34594 EndY=-7.02569 EndZ=0
    g40: LineSegment StartX=-7.34594 StartY=-7.02569 StartZ=0 EndX=-7.34594 EndY=-7.37431 EndZ=0
    g41: LineSegment StartX=-5.35355 StartY=-6.3 StartZ=0 EndX=-7.34594 EndY=-6.47431 EndZ=0
    g42: LineSegment StartX=-5.35355 StartY=-6.3 StartZ=0 EndX=-7.34594 EndY=-6.12569 EndZ=0
    g43: LineSegment StartX=-7.34594 StartY=-6.12569 StartZ=0 EndX=-7.34594 EndY=-6.47431 EndZ=0
    g44: LineSegment StartX=-5.35355 StartY=-5.4 StartZ=0 EndX=-7.34594 EndY=-5.57431 EndZ=0
    g45: LineSegment StartX=-5.35355 StartY=-5.4 StartZ=0 EndX=-7.34594 EndY=-5.22569 EndZ=0
    g46: LineSegment StartX=-7.34594 StartY=-5.22569 StartZ=0 EndX=-7.34594 EndY=-5.57431 EndZ=0
    g47: LineSegment StartX=-5.35355 StartY=-4.5 StartZ=0 EndX=-7.34594 EndY=-4.67431 EndZ=0
    g48: LineSegment StartX=-5.35355 StartY=-4.5 StartZ=0 EndX=-7.34594 EndY=-4.32569 EndZ=0
    g49: LineSegment StartX=-7.34594 StartY=-4.32569 StartZ=0 EndX=-7.34594 EndY=-4.67431 EndZ=0
    g50: LineSegment StartX=-5.35355 StartY=-3.6 StartZ=0 EndX=-7.34594 EndY=-3.77431 EndZ=0
    g51: LineSegment StartX=-5.35355 StartY=-3.6 StartZ=0 EndX=-7.34594 EndY=-3.42569 EndZ=0
    g52: LineSegment StartX=-7.34594 StartY=-3.42569 StartZ=0 EndX=-7.34594 EndY=-3.77431 EndZ=0
    g53: LineSegment StartX=-5.35355 StartY=-2.7 StartZ=0 EndX=-7.34594 EndY=-2.87431 EndZ=0
    g54: LineSegment StartX=-5.35355 StartY=-2.7 StartZ=0 EndX=-7.34594 EndY=-2.52569 EndZ=0
    g55: LineSegment StartX=-7.34594 StartY=-2.52569 StartZ=0 EndX=-7.34594 EndY=-2.87431 EndZ=0
    g56: LineSegment StartX=-5.35355 StartY=-1.8 StartZ=0 EndX=-7.34594 EndY=-1.97431 EndZ=0
    g57: LineSegment StartX=-5.35355 StartY=-1.8 StartZ=0 EndX=-7.34594 EndY=-1.62569 EndZ=0
    g58: LineSegment StartX=-7.34594 StartY=-1.62569 StartZ=0 EndX=-7.34594 EndY=-1.97431 EndZ=0
    g59: LineSegment StartX=-5.35355 StartY=-0.9 StartZ=0 EndX=-7.34594 EndY=-1.07431 EndZ=0
    g60: LineSegment StartX=-5.35355 StartY=-0.9 StartZ=0 EndX=-7.34594 EndY=-0.725689 EndZ=0
    g61: LineSegment StartX=-7.34594 StartY=-0.725689 StartZ=0 EndX=-7.34594 EndY=-1.07431 EndZ=0
    g62: LineSegment StartX=-5.35355 StartY=-84 StartZ=0 EndX=-7.34594 EndY=-83.8257 EndZ=0
    g63: LineSegment StartX=-7.34594 StartY=-83.8257 StartZ=0 EndX=-7.34594 EndY=-84 EndZ=0
    g64: LineSegment StartX=-7.34594 StartY=-84 StartZ=0 EndX=-5.35355 EndY=-84 EndZ=0
    g65: LineSegment StartX=-5.35355 StartY=0 StartZ=0 EndX=-7.34594 EndY=-0.174312 EndZ=0
    g66: LineSegment StartX=-7.34594 StartY=-0.174312 StartZ=0 EndX=-7.34594 EndY=0 EndZ=0
    g67: LineSegment StartX=-7.34594 StartY=0 StartZ=0 EndX=-5.35355 EndY=0 EndZ=0
  constraints (74):
    c: Distance(g0) = 9
    c: Coincident(g0,g-4)
    c: PointOnObject(g0,g-3)
    c: Distance(g1) = 2
    c: Angle(g-1,g1) = 3.05433
    c: Coincident(g1,g0)
    c: Distance(g2) = 2
    c: Angle(g-1,g2) = -3.05433
    c: Coincident(g2,g0)
    c: Coincident(g3,g2)
    c: Coincident(g3,g1)
    c: Coincident(g6,g5)
    c: Coincident(g9,g8)
    c: Coincident(g12,g11)
    c: Coincident(g15,g14)
    c: Coincident(g18,g17)
    c: Coincident(g21,g20)
    c: Coincident(g24,g23)
    c: Coincident(g27,g26)
    c: Coincident(g30,g29)
    c: Coincident(g6,g4)
    c: Coincident(g9,g7)
    c: Coincident(g12,g10)
    c: Coincident(g15,g13)
    c: Coincident(g18,g16)
    c: Coincident(g21,g19)
    c: Coincident(g24,g22)
    c: Coincident(g27,g25)
    c: Coincident(g30,g28)
    c: Distance(g31) = 9
    c: Coincident(g31,g-3)
    c: PointOnObject(g31,g-3)
    c: Distance(g32) = 2
    c: Angle(g-1,g32) = -3.05433
    c: Coincident(g32,g31)
    c: Distance(g33) = 2
    c: Angle(g-1,g33) = 3.05433
    c: Coincident(g33,g31)
    c: Coincident(g34,g33)
    c: Coincident(g34,g32)
    c: Coincident(g37,g36)
    c: Coincident(g40,g39)
    c: Coincident(g43,g42)
    c: Coincident(g46,g45)
    c: Coincident(g49,g48)
    c: Coincident(g52,g51)
    c: Coincident(g55,g54)
    c: Coincident(g58,g57)
    c: Coincident(g61,g60)
    c: Coincident(g37,g35)
    c: Coincident(g40,g38)
    c: Coincident(g43,g41)
    c: Coincident(g46,g44)
    c: Coincident(g49,g47)
    c: Coincident(g52,g50)
    c: Coincident(g55,g53)
    c: Coincident(g58,g56)
    c: Coincident(g61,g59)
    c: Distance(g62) = 2
    c: Angle(g-1,g62) = 3.05433
    c: Coincident(g62,g0)
    c: Coincident(g63,g62)
    c: PointOnObject(g63,g-4)
    c: Vertical(g63)
    c: Coincident(g64,g63)
    c: Coincident(g64,g0)
    c: Distance(g65) = 2
    c: Angle(g-1,g65) = -3.05433
    c: Coincident(g65,g31)
    c: Coincident(g66,g65)
    c: Vertical(g66)
    c: Coincident(g67,g66)
    c: Coincident(g67,g31)
    c: Horizontal(g67)
FEATURE [PartDesign::Pocket] Pocket017
  BaseFeature = -> Pocket015
  Direction = (1,0,-2.14311e-10)
  Length = 0.5
  Length2 = 5
  Placement = pos=(0,-84,2e-15) rot=(1,0,0;1.5708rad)
  Profile = -> Sketch039
  ReferenceAxis = -> Sketch039 [N_Axis]
  Refine = true
  Suppressed = false
  Type = 0
FEATURE [Sketcher::SketchObject] Sketch040
  ArcFitTolerance = 1e-06
  AttachmentSupport = -> [Hole002]
  ExternalGeometry = -> [Hole002]
  FullyConstrained = true
  MakeInternals = false
  MapMode = 5
  Placement = pos=(3.7335e-08,0,9.85355) rot=(1,0,0;3.14159rad)
  sketch-geometry (4):
    g0: LineSegment StartX=38.7465 StartY=46.75 StartZ=0 EndX=38.7465 EndY=37.25 EndZ=0
    g1: LineSegment StartX=38.7465 StartY=37.25 StartZ=0 EndX=45.2465 EndY=37.25 EndZ=0
    g2: LineSegment StartX=45.2465 StartY=37.25 StartZ=0 EndX=45.2465 EndY=46.75 EndZ=0
    g3: LineSegment StartX=45.2465 StartY=46.75 StartZ=0 EndX=38.7465 EndY=46.75 EndZ=0
  constraints (10):
    c: Coincident(g0,g1)
    c: Coincident(g1,g2)
    c: Coincident(g2,g3)
    c: Coincident(g3,g0)
    c: Vertical(g0)
    c: Vertical(g2)
    c: Horizontal(g1)
    c: Horizontal(g3)
    c: Coincident(g0,g-5)
    c: Coincident(g1,g-6)
FEATURE [PartDesign::Pad] Pad019
  BaseFeature = -> Hole002
  Direction = (-3.78899e-09,0,-1)
  Length = 4.65
  Length2 = 10
  Profile = -> Sketch040
  ReferenceAxis = -> Sketch040 [N_Axis]
  Refine = true
  Suppressed = false
  Type = 0
FEATURE [PartDesign::Chamfer] Chamfer015
  Angle = 45
  Base = -> Pad019 [Edge6]
  BaseFeature = -> Pad019
  ChamferType = 0
  FlipDirection = false
  Refine = true
  Size = 4
  Size2 = 1
  SupportTransform = false
  Suppressed = false
  UseAllEdges = false
FEATURE [PartDesign::Chamfer] Chamfer016
  Angle = 45
  Base = -> Chamfer015 [Edge47]
  BaseFeature = -> Chamfer015
  ChamferType = 0
  FlipDirection = false
  Refine = true
  Size = 4
  Size2 = 1
  SupportTransform = false
  Suppressed = false
  UseAllEdges = false
FEATURE [Sketcher::SketchObject] Sketch041
  ArcFitTolerance = 1e-06
  AttachmentSupport = -> [Chamfer016]
  ExternalGeometry = -> [Chamfer016]
  FullyConstrained = true
  MakeInternals = false
  MapMode = 5
  Placement = pos=(0,-37.25,0) rot=(0,0.707107,0.707107;3.14159rad)
  sketch-geometry (4):
    g0: LineSegment StartX=-48.2465 StartY=20.8536 StartZ=0 EndX=-48.2465 EndY=6.85355 EndZ=0
    g1: LineSegment StartX=-48.2465 StartY=6.85355 StartZ=0 EndX=-46.2465 EndY=6.85355 EndZ=0
    g2: LineSegment StartX=-46.2465 StartY=6.85355 StartZ=0 EndX=-46.2465 EndY=20.8536 EndZ=0
    g3: LineSegment StartX=-46.2465 StartY=20.8536 StartZ=0 EndX=-48.2465 EndY=20.8536 EndZ=0
  constraints (11):
    c: Coincident(g0,g1)
    c: Coincident(g1,g2)
    c: Coincident(g2,g3)
    c: Coincident(g3,g0)
    c: Vertical(g0)
    c: Vertical(g2)
    c: Horizontal(g1)
    c: Horizontal(g3)
    c: Distance(g0,g2) = 2
    c: Distance(g1,g3) = 14
    c: Coincident(g0,g-11)
FEATURE [PartDesign::Pocket] Pocket018
  BaseFeature = -> Chamfer016
  Direction = (0,-1,2e-16)
  Length = 10
  Length2 = 5
  Profile = -> Sketch041
  ReferenceAxis = -> Sketch041 [N_Axis]
  Refine = true
  Suppressed = false
  Type = 0
FEATURE [Sketcher::SketchObject] Sketch043
  ArcFitTolerance = 1e-06
  AttachmentSupport = -> [Pocket018]
  ExternalGeometry = -> [Pocket018]
  FullyConstrained = true
  MakeInternals = false
  MapMode = 5
  Placement = pos=(0,-37.25,0) rot=(0,0.707107,0.707107;3.14159rad)
  sketch-geometry (4):
    g0: LineSegment StartX=-35.7465 StartY=20.8536 StartZ=0 EndX=-37.7465 EndY=20.8536 EndZ=0
    g1: LineSegment StartX=-37.7465 StartY=20.8536 StartZ=0 EndX=-37.7465 EndY=7.85355 EndZ=0
    g2: LineSegment StartX=-37.7465 StartY=7.85355 StartZ=0 EndX=-35.7465 EndY=7.85355 EndZ=0
    g3: LineSegment StartX=-35.7465 StartY=7.85355 StartZ=0 EndX=-35.7465 EndY=20.8536 EndZ=0
  constraints (11):
    c: Coincident(g0,g1)
    c: Coincident(g1,g2)
    c: Coincident(g2,g3)
    c: Coincident(g3,g0)
    c: Horizontal(g0)
    c: Horizontal(g2)
    c: Vertical(g1)
    c: Vertical(g3)
    c: Distance(g1,g3) = 2
    c: Distance(g0,g2) = 13
    c: Coincident(g0,g-4)
FEATURE [PartDesign::Pocket] Pocket019
  BaseFeature = -> Pocket018
  Direction = (0,-1,2e-16)
  Length = 10
  Length2 = 5
  Profile = -> Sketch043
  ReferenceAxis = -> Sketch043 [N_Axis]
  Refine = true
  Suppressed = false
  Type = 0
FEATURE [Sketcher::SketchObject] Sketch044
  ArcFitTolerance = 1e-06
  AttachmentSupport = -> [Pocket019]
  ExternalGeometry = -> [Pocket019]
  FullyConstrained = true
  MakeInternals = false
  MapMode = 5
  Placement = pos=(0,-37.25,0) rot=(0,0.707107,0.707107;3.14159rad)
  sketch-geometry (4):
    g0: LineSegment StartX=-46.2465 StartY=20.8536 StartZ=0 EndX=-54.2465 EndY=20.8536 EndZ=0
    g1: LineSegment StartX=-54.2465 StartY=20.8536 StartZ=0 EndX=-54.2465 EndY=16.8536 EndZ=0
    g2: LineSegment StartX=-46.2465 StartY=8.26777 StartZ=0 EndX=-46.2465 EndY=20.8536 EndZ=0
    g3: LineSegment StartX=-54.2465 StartY=16.8536 StartZ=0 EndX=-46.2465 EndY=8.26777 EndZ=0
  constraints (10):
    c: Distance(g0) = 8
    c: Coincident(g0,g-4)
    c: Horizontal(g0)
    c: Distance(g1) = 4
    c: Coincident(g1,g0)
    c: Vertical(g1)
    c: Coincident(g2,g0)
    c: Coincident(g3,g1)
    c: Coincident(g3,g2)
    c: Coincident(g-4,g2)
FEATURE [PartDesign::Pad] Pad020
  BaseFeature = -> Pocket019
  Direction = (0,1,-2e-16)
  Length = 9.5
  Length2 = 10
  Profile = -> Sketch044
  ReferenceAxis = -> Sketch044 [N_Axis]
  Refine = true
  Reversed = true
  Suppressed = false
  Type = 0
FEATURE [Sketcher::SketchObject] Sketch045
  ArcFitTolerance = 1e-06
  AttachmentSupport = -> [Pad020]
  ExternalGeometry = -> [Pad020]
  FullyConstrained = true
  MakeInternals = false
  MapMode = 5
  Placement = pos=(2.2e-14,-37.25,1.23e-14) rot=(0,0.707107,0.707107;3.14159rad)
  sketch-geometry (4):
    g0: LineSegment StartX=-37.7465 StartY=20.8536 StartZ=0 EndX=-29.7465 EndY=20.8536 EndZ=0
    g1: LineSegment StartX=-29.7465 StartY=20.8536 StartZ=0 EndX=-29.7465 EndY=16.8536 EndZ=0
    g2: LineSegment StartX=-29.7465 StartY=16.8536 StartZ=0 EndX=-37.7465 EndY=8.26777 EndZ=0
    g3: LineSegment StartX=-37.7465 StartY=8.26777 StartZ=0 EndX=-37.7465 EndY=20.8536 EndZ=0
  constraints (10):
    c: Distance(g0) = 8
    c: Coincident(g0,g-4)
    c: Horizontal(g0)
    c: Distance(g1) = 4
    c: Coincident(g1,g0)
    c: Vertical(g1)
    c: Coincident(g2,g1)
    c: Coincident(g2,g-6)
    c: Coincident(g3,g2)
    c: Coincident(g3,g0)
FEATURE [PartDesign::Pad] Pad021
  BaseFeature = -> Pad020
  Direction = (0,1,-2e-16)
  Length = 9.5
  Length2 = 10
  Profile = -> Sketch045
  ReferenceAxis = -> Sketch045 [N_Axis]
  Refine = true
  Reversed = true
  Suppressed = false
  Type = 0
FEATURE [Sketcher::SketchObject] Sketch046
  ArcFitTolerance = 1e-06
  AttachmentSupport = -> [Pad021]
  ExternalGeometry = -> [Pad021]
  FullyConstrained = true
  MakeInternals = false
  MapMode = 5
  Placement = pos=(8.12e-14,-37.25,0) rot=(0,0.707107,0.707107;3.14159rad)
  sketch-geometry (2):
    g0: GeomPoint [constr] X=-54.2465 Y=18.8536 Z=0
    g1: Circle CenterX=-54.2465 CenterY=18.8536 CenterZ=0 NormalX=0 NormalY=0 NormalZ=1 AngleXU=0 Radius=1
  constraints (3):
    c: Symmetric(g-3,g-3,g0)
    c: Diameter(g1) = 2
    c: Coincident(g1,g0)
FEATURE [PartDesign::Pocket] Pocket020
  BaseFeature = -> Pad021
  Direction = (2.2e-15,-1,2e-16)
  Length = 10
  Length2 = 5
  Profile = -> Sketch046
  ReferenceAxis = -> Sketch046 [N_Axis]
  Refine = true
  Suppressed = false
  Type = 0
FEATURE [Sketcher::SketchObject] Sketch047
  ArcFitTolerance = 1e-06
  AttachmentSupport = -> [Pocket020]
  ExternalGeometry = -> [Pocket020]
  FullyConstrained = true
  MakeInternals = false
  MapMode = 5
  Placement = pos=(8.12e-14,-37.25,0) rot=(0,0.707107,0.707107;3.14159rad)
  sketch-geometry (2):
    g0: GeomPoint X=-29.7465 Y=18.8536 Z=0
    g1: Circle CenterX=-29.7465 CenterY=18.8536 CenterZ=0 NormalX=0 NormalY=0 NormalZ=1 AngleXU=0 Radius=1
  constraints (3):
    c: Symmetric(g-3,g-3,g0)
    c: Diameter(g1) = 2
    c: Coincident(g1,g0)
FEATURE [PartDesign::Pocket] Pocket021
  BaseFeature = -> Pocket020
  Direction = (2.2e-15,-1,2e-16)
  Length = 11
  Length2 = 5
  Profile = -> Sketch047
  ReferenceAxis = -> Sketch047 [N_Axis]
  Refine = true
  Suppressed = false
  Type = 0
FEATURE [Sketcher::SketchObject] Sketch048
  ArcFitTolerance = 1e-06
  AttachmentSupport = -> [Pocket021]
  ExternalGeometry = -> [Pocket021]
  FullyConstrained = true
  MakeInternals = false
  MapMode = 5
  Placement = pos=(6.7647e-08,0,17.8536) rot=(0,0,1;0rad)
  sketch-geometry (1):
    g0: Circle CenterX=41.9965 CenterY=-42 CenterZ=0 NormalX=0 NormalY=0 NormalZ=1 AngleXU=0 Radius=1.35
  constraints (2):
    c: Coincident(g0,g-3)
    c: Equal(g0,g-3)
FEATURE [PartDesign::Pad] Pad022
  BaseFeature = -> Pocket021
  Direction = (3.78899e-09,0,1)
  Length = 3
  Length2 = 10
  Profile = -> Sketch048
  ReferenceAxis = -> Sketch048 [N_Axis]
  Refine = true
  Suppressed = false
  Type = 0
FEATURE [Sketcher::SketchObject] Sketch049
  ArcFitTolerance = 1e-06
  AttachmentSupport = -> [Pad022]
  ExternalGeometry = -> [Pad022]
  FullyConstrained = true
  MakeInternals = false
  MapMode = 5
  Placement = pos=(3.93837e-08,0,20.8536) rot=(0,0,1;0rad)
  sketch-geometry (8):
    g0: GeomPoint X=33.7465 Y=-37.25 Z=0
    g1: GeomPoint X=33.7465 Y=-46.75 Z=0
    g2: GeomPoint X=50.2465 Y=-46.75 Z=0
    g3: GeomPoint X=50.2465 Y=-37.25 Z=0
    g4: LineSegment [constr] StartX=33.7465 StartY=-37.25 StartZ=0 EndX=33.7465 EndY=-46.75 EndZ=0
    g5: LineSegment [constr] StartX=50.2465 StartY=-37.25 StartZ=0 EndX=50.2465 EndY=-46.75 EndZ=0
    g6: Circle CenterX=33.7465 CenterY=-42 CenterZ=0 NormalX=0 NormalY=0 NormalZ=1 AngleXU=0 Radius=1.35
    g7: Circle CenterX=50.2465 CenterY=-42 CenterZ=0 NormalX=0 NormalY=0 NormalZ=1 AngleXU=0 Radius=1.35
  constraints (12):
    c: Symmetric(g-3,g-3,g0)
    c: Symmetric(g-6,g-6,g1)
    c: Symmetric(g-5,g-5,g2)
    c: Symmetric(g-4,g-4,g3)
    c: Coincident(g4,g0)
    c: Coincident(g4,g1)
    c: Coincident(g5,g3)
    c: Coincident(g5,g2)
    c: Diameter(g6) = 2.7
    c: Symmetric(g4,g4,g6)
    c: Diameter(g7) = 2.7
    c: Symmetric(g5,g5,g7)
FEATURE [PartDesign::Pocket] Pocket022
  BaseFeature = -> Pad022
  Direction = (-1.88858e-09,0,-1)
  Length = 13
  Length2 = 5
  Profile = -> Sketch049
  ReferenceAxis = -> Sketch049 [N_Axis]
  Refine = true
  Suppressed = false
  Type = 0
FEATURE [Sketcher::SketchObject] Sketch050
  ArcFitTolerance = 1e-06
  AttachmentSupport = -> [Pocket017]
  FullyConstrained = true
  MakeInternals = false
  MapMode = 5
  Placement = pos=(7.71195e-08,-84,20.3536) rot=(1,0,0;3.14159rad)
  sketch-geometry (10):
    g0: LineSegment [constr] StartX=35.4965 StartY=-37 StartZ=0 EndX=29.6465 EndY=-37 EndZ=0
    g1: LineSegment [constr] StartX=48.4965 StartY=-37 StartZ=0 EndX=54.3465 EndY=-37 EndZ=0
    g2: LineSegment StartX=29.6465 StartY=-37 StartZ=0 EndX=29.6465 EndY=-47 EndZ=0
    g3: LineSegment StartX=29.6465 StartY=-47 StartZ=0 EndX=35.4965 EndY=-47 EndZ=0
    g4: LineSegment StartX=35.4965 StartY=-47 StartZ=0 EndX=35.4965 EndY=-37 EndZ=0
    g5: LineSegment StartX=35.4965 StartY=-37 StartZ=0 EndX=29.6465 EndY=-37 EndZ=0
    g6: LineSegment StartX=54.3465 StartY=-37 StartZ=0 EndX=48.4965 EndY=-37 EndZ=0
    g7: LineSegment StartX=48.4965 StartY=-37 StartZ=0 EndX=48.4965 EndY=-47 EndZ=0
    g8: LineSegment StartX=48.4965 StartY=-47 StartZ=0 EndX=54.3465 EndY=-47 EndZ=0
    g9: LineSegment StartX=54.3465 StartY=-47 StartZ=0 EndX=54.3465 EndY=-37 EndZ=0
  constraints (26):
    c: Distance(g0) = 5.85
    c: Coincident(g0,g-4)
    c: Horizontal(g0)
    c: Distance(g1) = 5.85
    c: Coincident(g1,g-5)
    c: Horizontal(g1)
    c: Coincident(g2,g3)
    c: Coincident(g3,g4)
    c: Coincident(g4,g5)
    c: Coincident(g5,g2)
    c: Vertical(g2)
    c: Vertical(g4)
    c: Horizontal(g3)
    c: Horizontal(g5)
    c: Coincident(g2,g0)
    c: Coincident(g3,g-6)
    c: Coincident(g6,g7)
    c: Coincident(g7,g8)
    c: Coincident(g8,g9)
    c: Coincident(g9,g6)
    c: Horizontal(g6)
    c: Horizontal(g8)
    c: Vertical(g7)
    c: Vertical(g9)
    c: Coincident(g6,g1)
    c: Coincident(g7,g-6)
FEATURE [PartDesign::Pocket] Pocket023
  BaseFeature = -> Pocket017
  Direction = (3.78899e-09,1.1e-15,1)
  Length = 0.5
  Length2 = 5
  Placement = pos=(0,-84,2e-15) rot=(1,0,0;1.5708rad)
  Profile = -> Sketch050
  ReferenceAxis = -> Sketch050 [N_Axis]
  Refine = true
  Suppressed = false
  Type = 0
FEATURE [Sketcher::SketchObject] Sketch051
  ArcFitTolerance = 1e-06
  AttachmentSupport = -> [Pocket023]
  ExternalGeometry = -> [Pocket023]
  FullyConstrained = true
  MakeInternals = false
  MapMode = 5
  Placement = pos=(7.9014e-08,-84,20.8536) rot=(1,0,0;3.14159rad)
  sketch-geometry (4):
    g0: LineSegment [constr] StartX=41.9965 StartY=-42 StartZ=0 EndX=50.2465 EndY=-42 EndZ=0
    g1: LineSegment [constr] StartX=41.9965 StartY=-42 StartZ=0 EndX=33.7465 EndY=-42 EndZ=0
    g2: Circle CenterX=33.7465 CenterY=-42 CenterZ=0 NormalX=0 NormalY=0 NormalZ=1 AngleXU=0 Radius=1.5
    g3: Circle CenterX=50.2465 CenterY=-42 CenterZ=0 NormalX=0 NormalY=0 NormalZ=1 AngleXU=0 Radius=1.5
  constraints (10):
    c: Distance(g0) = 8.25
    c: Coincident(g0,g-3)
    c: Horizontal(g0)
    c: Distance(g1) = 8.25
    c: Coincident(g1,g0)
    c: Horizontal(g1)
    c: Diameter(g2) = 3
    c: Coincident(g2,g1)
    c: Diameter(g3) = 3
    c: Coincident(g3,g0)
FEATURE [PartDesign::Pocket] Pocket024
  BaseFeature = -> Pocket023
  Direction = (3.78899e-09,1.2e-15,1)
  Length = 11
  Length2 = 5
  Placement = pos=(0,-84,2e-15) rot=(1,0,0;1.5708rad)
  Profile = -> Sketch051
  ReferenceAxis = -> Sketch051 [N_Axis]
  Refine = true
  Suppressed = false
  Type = 0
FEATURE [Sketcher::SketchObject] Sketch052
  ArcFitTolerance = 1e-06
  AttachmentSupport = -> [Pocket024]
  ExternalGeometry = -> [Pocket024]
  FullyConstrained = true
  MakeInternals = false
  MapMode = 5
  Placement = pos=(6.55296e-08,-84,23.3536) rot=(0,0,1;3.14159rad)
  sketch-geometry (2):
    g0: Circle CenterX=-41.9965 CenterY=-42 CenterZ=0 NormalX=0 NormalY=0 NormalZ=1 AngleXU=0 Radius=1.55
    g1: Circle CenterX=-41.9965 CenterY=-42 CenterZ=0 NormalX=0 NormalY=0 NormalZ=1 AngleXU=0 Radius=3
  constraints (4):
    c: Diameter(g0) = 3.1
    c: Coincident(g0,g-4)
    c: Diameter(g1) = 6
    c: Coincident(g1,g0)
FEATURE [PartDesign::Pad] Pad023
  BaseFeature = -> Pocket024
  Direction = (2.80598e-09,0,1)
  Length = 4
  Length2 = 10
  Placement = pos=(0,-84,2e-15) rot=(1,0,0;1.5708rad)
  Profile = -> Sketch052
  ReferenceAxis = -> Sketch052 [N_Axis]
  Refine = true
  Suppressed = false
  Type = 0
FEATURE [Sketcher::SketchObject] Sketch053
  ArcFitTolerance = 1e-06
  AttachmentSupport = -> [Pad023]
  ExternalGeometry = -> [Pad023]
  FullyConstrained = true
  MakeInternals = false
  MapMode = 5
  Placement = pos=(7.67535e-08,-84,27.3536) rot=(0,0,1;3.14159rad)
  sketch-geometry (2):
    g0: Circle CenterX=-50.2465 CenterY=-42 CenterZ=0 NormalX=0 NormalY=0 NormalZ=1 AngleXU=0 Radius=3
    g1: Circle CenterX=-33.7465 CenterY=-42 CenterZ=0 NormalX=0 NormalY=0 NormalZ=1 AngleXU=0 Radius=3
  constraints (4):
    c: Diameter(g0) = 6
    c: Coincident(g0,g-4)
    c: Diameter(g1) = 6
    c: Coincident(g1,g-3)
FEATURE [PartDesign::Pocket] Pocket025
  BaseFeature = -> Pad023
  Direction = (-2.80598e-09,0,-1)
  Length = 3.5
  Length2 = 5
  Placement = pos=(0,-84,2e-15) rot=(1,0,0;1.5708rad)
  Profile = -> Sketch053
  ReferenceAxis = -> Sketch053 [N_Axis]
  Refine = true
  Suppressed = false
  Type = 0
FEATURE [Sketcher::SketchObject] Sketch054
  ArcFitTolerance = 1e-06
  AttachmentSupport = -> [Pocket022]
  ExternalGeometry = -> [Pocket022]
  FullyConstrained = true
  MakeInternals = false
  MapMode = 5
  Placement = pos=(3.93837e-08,0,20.8536) rot=(0,0,1;0rad)
  sketch-geometry (8):
    g0: GeomPoint X=41.9965 Y=-37.25 Z=0
    g1: GeomPoint X=41.9965 Y=-46.75 Z=0
    g2: LineSegment [constr] StartX=41.9965 StartY=-37.25 StartZ=0 EndX=41.9965 EndY=-46.75 EndZ=0
    g3: GeomPoint [constr] X=41.9965 Y=-42 Z=0
    g4: LineSegment StartX=41.9965 StartY=-41 StartZ=0 EndX=41.1304 EndY=-42.5 EndZ=0
    g5: LineSegment StartX=41.1304 StartY=-42.5 StartZ=0 EndX=42.8625 EndY=-42.5 EndZ=0
    g6: LineSegment StartX=42.8625 StartY=-42.5 StartZ=0 EndX=41.9965 EndY=-41 EndZ=0
    g7: Circle [constr] CenterX=41.9965 CenterY=-42 CenterZ=0 NormalX=0 NormalY=0 NormalZ=1 AngleXU=0 Radius=1
  constraints (16):
    c: Symmetric(g-3,g-3,g0)
    c: Symmetric(g-4,g-4,g1)
    c: Coincident(g2,g0)
    c: Coincident(g2,g1)
    c: Symmetric(g2,g2,g3)
    c: Coincident(g4,g5)
    c: Coincident(g5,g6)
    c: Coincident(g6,g4)
    c: Equal(g4,g5)
    c: Equal(g4,g6)
    c: PointOnObject(g4,g7)
    c: PointOnObject(g5,g7)
    c: PointOnObject(g6,g7)
    c: Radius(g7) = 1
    c: Coincident(g7,g3)
    c: PointOnObject(g6,g2)
FEATURE [PartDesign::Pocket] Pocket026
  BaseFeature = -> Pocket022
  Direction = (-1.88858e-09,0,-1)
  Length = 0.5
  Length2 = 5
  Profile = -> Sketch054
  ReferenceAxis = -> Sketch054 [N_Axis]
  Refine = true
  Suppressed = false
  Type = 0
FEATURE [PartDesign::Body] Body004  label="Thread Block Modelled"
  AllowCompound = false
  Group = -> [Clone,Sketch018,Hole002,Sketch040,Pad019,Chamfer015,Chamfer016,Sketch041,Pocket018,Sketch043,Pocket019,Sketch044,Pad020,Sketch045,Pad021,Sketch046,Pocket020,Sketch047,Pocket021,Sketch048,Pad022,Sketch049,Pocket022,Sketch054,Pocket026]
  Origin = -> Origin004
  Placement = pos=(0,-23,0) rot=(0,0,1;0rad)
  Tip = -> Pocket026
FEATURE [Sketcher::SketchObject] Sketch055
  ArcFitTolerance = 1e-06
  AttachmentSupport = -> [Pocket014]
  ExternalGeometry = -> [Pocket014]
  FullyConstrained = true
  MakeInternals = false
  MapMode = 5
  Placement = pos=(42,-84,14) rot=(0.57735,0.57735,0.57735;4.18879rad)
  sketch-geometry (2):
    g0: Circle CenterX=0 CenterY=-0.03 CenterZ=0 NormalX=0 NormalY=0 NormalZ=1 AngleXU=0 Radius=3.03
    g1: Circle CenterX=0 CenterY=-0.03 CenterZ=0 NormalX=0 NormalY=0 NormalZ=1 AngleXU=0 Radius=3.75
  constraints (5):
    c: PointOnObject(g0,g-2)
    c: Tangent(g0,g-3)
    c: Diameter(g0) = 6.06
    c: Diameter(g1) = 7.5
    c: Coincident(g1,g0)
FEATURE [PartDesign::Pad] Pad024
  BaseFeature = -> Pocket014
  Direction = (0,1,0)
  Length = 21
  Length2 = 10
  Placement = pos=(42,-84,14) rot=(0.57735,-0.57735,0.57735;2.0944rad)
  Profile = -> Sketch055
  ReferenceAxis = -> Sketch055 [N_Axis]
  Refine = true
  Reversed = true
  Suppressed = false
  Type = 0
FEATURE [Sketcher::SketchObject] Sketch056
  ArcFitTolerance = 1e-06
  AttachmentSupport = -> [Pad024]
  ExternalGeometry = -> [Pad024]
  FullyConstrained = true
  MakeInternals = false
  MapMode = 5
  Placement = pos=(42,-84,14) rot=(0.57735,0.57735,0.57735;4.18879rad)
  sketch-geometry (2):
    g0: Circle CenterX=0 CenterY=0 CenterZ=0 NormalX=0 NormalY=0 NormalZ=1 AngleXU=0 Radius=2.9
    g1: Circle CenterX=0 CenterY=-0.03 CenterZ=0 NormalX=0 NormalY=0 NormalZ=1 AngleXU=0 Radius=3.75
  constraints (4):
    c: Coincident(g0,g-1)
    c: Diameter(g0) = 5.8
    c: Coincident(g1,g-3)
    c: Equal(g1,g-3)
FEATURE [PartDesign::Pocket] Pocket027
  BaseFeature = -> Pad024
  Direction = (0,-1,0)
  Length = 8
  Length2 = 5
  Placement = pos=(42,-84,14) rot=(0.57735,-0.57735,0.57735;2.0944rad)
  Profile = -> Sketch056
  ReferenceAxis = -> Sketch056 [N_Axis]
  Refine = true
  Suppressed = false
  Type = 0
FEATURE [Part::FeaturePython] BinBase  label="2u Gridfinity Base Plate"  # WARN: FeaturePython — macro-defined, semantics opaque (R4)
  BaseProfileBottomChamfer = 0.8
  BaseProfileHeight = 4.75
  BaseProfileTopChamfer = 2.15
  BaseProfileVerticalSection = 1.8
  BinBottomRadius = 0.8
  BinOuterRadius = 3.75
  BinUnit = 41.5
  BinVerticalRadius = 1.6
  CustomHeight = 42
  GridSize = 42
  HeightUnitValue = 7
  HeightUnits = 1
  MagnetHoleDepth = 2.4
  MagnetHoleDiameter = 6.5
  MagnetHoleDistanceFromEdge = 8
  MagnetHoles = true
  NonStandardHeight = false
  Placement = pos=(-72,-63,-2) rot=(0,0,1;0rad)
  ScrewHoleDepth = 6
  ScrewHoleDiameter = 3
  ScrewHoles = true
  SequentialBridgingLayerHeight = 0.2
  StackingLip = false
  StackingLipBottomChamfer = 0.7
  StackingLipTopChamfer = 1.5
  StackingLipTopLedge = 0.4
  StackingLipVerticalSection = 1.8
  Tolerance = 0.25
  TotalHeight = 7
  WallThickness = 1
  version = 0.6.0
  xGridUnits = 2
  xTotalWidth = 83.5
  yGridUnits = 2
  yTotalWidth = 83.5
FEATURE [PartDesign::ShapeBinder] CopyBinBase
  Placement = pos=(-72,-63,-2) rot=(0,0,1;0rad)
  TraceSupport = false
FEATURE [PartDesign::Plane] DatumPlane011
  AttachmentSupport = -> [CopyBinBase]
  Length = 186.287
  MapMode = 5
  Placement = pos=(-72,-63,-9) rot=(1,0,0;3.14159rad)
  ResizeMode = 0
  Width = 177.287
FEATURE [PartDesign::SubShapeBinder] Binder
  BindCopyOnChange = 0
  BindMode = 0
  ClaimChildren = false
  Context = -> Body007 [Binder.]
  Fuse = false
  MakeFace = true
  OffsetFill = false
  OffsetIntersection = false
  OffsetJoinType = 0
  OffsetOpenResult = false
  PartialLoad = false
  Refine = true
  Relative = true
  Support = -> [BinBase]
  _Version = 2
FEATURE [PartDesign::SubShapeBinder] Binder001
  BindCopyOnChange = 0
  BindMode = 0
  ClaimChildren = false
  Context = -> Body007 [Binder001.]
  Fuse = false
  MakeFace = true
  OffsetFill = false
  OffsetIntersection = false
  OffsetJoinType = 0
  OffsetOpenResult = false
  PartialLoad = false
  Refine = true
  Relative = true
  Support = -> [BinBase[Face242]]
  _Version = 2
FEATURE [PartDesign::SubShapeBinder] Binder002
  BindCopyOnChange = 0
  BindMode = 0
  ClaimChildren = false
  Context = -> Body007 [Binder002.]
  Fuse = false
  MakeFace = true
  OffsetFill = false
  OffsetIntersection = false
  OffsetJoinType = 0
  OffsetOpenResult = false
  PartialLoad = false
  Refine = true
  Relative = true
  Support = -> [BinBase[Face2]]
  _Version = 2
FEATURE [PartDesign::SubShapeBinder] Binder003
  BindCopyOnChange = 0
  BindMode = 0
  ClaimChildren = false
  Context = -> Body007 [Binder003.]
  Fuse = false
  MakeFace = true
  OffsetFill = false
  OffsetIntersection = false
  OffsetJoinType = 0
  OffsetOpenResult = false
  PartialLoad = false
  Refine = true
  Relative = true
  Support = -> [BinBase[Face236]]
  _Version = 2
FEATURE [PartDesign::SubShapeBinder] Binder004
  BindCopyOnChange = 0
  BindMode = 0
  ClaimChildren = false
  Context = -> Body007 [Binder004.]
  Fuse = false
  MakeFace = true
  OffsetFill = false
  OffsetIntersection = false
  OffsetJoinType = 0
  OffsetOpenResult = false
  PartialLoad = false
  Refine = true
  Relative = true
  Support = -> [BinBase[Face234]]
  _Version = 2
FEATURE [Sketcher::SketchObject] Sketch060
  ArcFitTolerance = 1e-06
  AttachmentSupport = -> [DatumPlane011]
  ExternalGeometry = -> [Binder004,Binder001,Binder003,Binder002]
  FullyConstrained = true
  MakeInternals = false
  MapMode = 5
  Placement = pos=(-72,-63,-9) rot=(1,0,0;3.14159rad)
  sketch-geometry (8):
    g0: Circle CenterX=80 CenterY=13 CenterZ=0 NormalX=0 NormalY=0 NormalZ=1 AngleXU=0 Radius=1.3
    g1: Circle CenterX=80 CenterY=-13 CenterZ=0 NormalX=0 NormalY=0 NormalZ=1 AngleXU=0 Radius=1.3
    g2: Circle CenterX=80 CenterY=-29 CenterZ=0 NormalX=0 NormalY=0 NormalZ=1 AngleXU=0 Radius=1.3
    g3: Circle CenterX=80 CenterY=-55 CenterZ=0 NormalX=0 NormalY=0 NormalZ=1 AngleXU=0 Radius=1.3
    g4: Circle CenterX=148 CenterY=-55 CenterZ=0 NormalX=0 NormalY=0 NormalZ=1 AngleXU=0 Radius=1.3
    g5: Circle CenterX=148 CenterY=-29 CenterZ=0 NormalX=0 NormalY=0 NormalZ=1 AngleXU=0 Radius=1.3
    g6: Circle CenterX=148 CenterY=-13 CenterZ=0 NormalX=0 NormalY=0 NormalZ=1 AngleXU=0 Radius=1.3
    g7: Circle CenterX=148 CenterY=13 CenterZ=0 NormalX=0 NormalY=0 NormalZ=1 AngleXU=0 Radius=1.3
  constraints (16):
    c: Diameter(g0) = 2.6
    c: Coincident(g0,g-3)
    c: Diameter(g1) = 2.6
    c: Coincident(g1,g-8)
    c: Diameter(g2) = 2.6
    c: Coincident(g2,g-7)
    c: Diameter(g3) = 2.6
    c: Coincident(g3,g-6)
    c: Diameter(g4) = 2.6
    c: Coincident(g4,g-5)
    c: Diameter(g5) = 2.6
    c: Coincident(g5,g-10)
    c: Diameter(g6) = 2.6
    c: Coincident(g6,g-9)
    c: Diameter(g7) = 2.6
    c: Coincident(g7,g-4)
FEATURE [Sketcher::SketchObject] Sketch061
  ArcFitTolerance = 1e-06
  AttachmentSupport = -> [Pocket016]
  ExternalGeometry = -> [Pocket016]
  FullyConstrained = true
  MakeInternals = false
  MapMode = 5
  Placement = pos=(84,0,0) rot=(0.707107,0,0.707107;3.14159rad)
  expr: Constraints[19] = VarSet.HoleDiameter
  sketch-geometry (9):
    g0: LineSegment [constr] StartX=5 StartY=84 StartZ=0 EndX=5 EndY=56 EndZ=0
    g1: LineSegment [constr] StartX=5 StartY=56 StartZ=0 EndX=5 EndY=28 EndZ=0
    g2: LineSegment [constr] StartX=5 StartY=28 StartZ=0 EndX=5 EndY=0 EndZ=0
    g3: LineSegment [constr] StartX=5 StartY=56 StartZ=0 EndX=0 EndY=56 EndZ=0
    g4: LineSegment [constr] StartX=5 StartY=28 StartZ=0 EndX=0 EndY=28 EndZ=0
    g5: GeomPoint X=2.5 Y=56 Z=0
    g6: GeomPoint X=2.5 Y=28 Z=0
    g7: Circle CenterX=2.5 CenterY=56 CenterZ=0 NormalX=0 NormalY=0 NormalZ=1 AngleXU=0 Radius=1.3
    g8: Circle CenterX=2.5 CenterY=28 CenterZ=0 NormalX=0 NormalY=0 NormalZ=1 AngleXU=0 Radius=1.3
  constraints (20):
    c: Coincident(g0,g-4)
    c: PointOnObject(g0,g-4)
    c: Coincident(g1,g0)
    c: PointOnObject(g1,g-4)
    c: Coincident(g2,g1)
    c: Coincident(g2,g-4)
    c: Equal(g0,g1)
    c: Equal(g1,g2)
    c: Coincident(g3,g0)
    c: PointOnObject(g3,g-5)
    c: Horizontal(g3)
    c: Coincident(g4,g1)
    c: PointOnObject(g4,g-5)
    c: Horizontal(g4)
    c: Symmetric(g3,g3,g5)
    c: Symmetric(g4,g4,g6)
    c: Coincident(g7,g5)
    c: Coincident(g8,g6)
    c: Equal(g7,g8)
    c: Diameter(g8) = 2.6
FEATURE [App::VarSet] VarSet
  HoleDepth = 6
  HoleDiameter = 2.6
FEATURE [PartDesign::Pocket] Pocket031
  BaseFeature = -> Pocket016
  Direction = (-1,0,2e-16)
  Length = 6
  Length2 = 5
  Placement = pos=(0,0,0) rot=(1,0,0;1.5708rad)
  Profile = -> Sketch061
  ReferenceAxis = -> Sketch061 [N_Axis]
  Refine = true
  Suppressed = false
  Type = 0
  expr: Length = VarSet.HoleDepth
FEATURE [Sketcher::SketchObject] Sketch062
  ArcFitTolerance = 1e-06
  AttachmentSupport = -> [Pocket031]
  ExternalGeometry = -> [Pocket031]
  FullyConstrained = true
  MakeInternals = false
  MapMode = 5
  Placement = pos=(0,0,0) rot=(0.707107,0,-0.707107;3.14159rad)
  expr: Constraints[19] = VarSet.HoleDiameter
  sketch-geometry (9):
    g0: LineSegment [constr] StartX=-5 StartY=84 StartZ=0 EndX=-5 EndY=56 EndZ=0
    g1: LineSegment [constr] StartX=-5 StartY=56 StartZ=0 EndX=-5 EndY=28 EndZ=0
    g2: LineSegment [constr] StartX=-5 StartY=28 StartZ=0 EndX=-5 EndY=0 EndZ=0
    g3: LineSegment [constr] StartX=-5 StartY=56 StartZ=0 EndX=0 EndY=56 EndZ=0
    g4: LineSegment [constr] StartX=-5 StartY=28 StartZ=0 EndX=0 EndY=28 EndZ=0
    g5: GeomPoint [constr] X=-2.5 Y=56 Z=0
    g6: GeomPoint [constr] X=-2.5 Y=28 Z=0
    g7: Circle CenterX=-2.5 CenterY=56 CenterZ=0 NormalX=0 NormalY=0 NormalZ=1 AngleXU=0 Radius=1.3
    g8: Circle CenterX=-2.5 CenterY=28 CenterZ=0 NormalX=0 NormalY=0 NormalZ=1 AngleXU=0 Radius=1.3
  constraints (20):
    c: Coincident(g0,g-3)
    c: Vertical(g0)
    c: Coincident(g1,g0)
    c: Vertical(g1)
    c: Coincident(g2,g1)
    c: Coincident(g2,g-5)
    c: Equal(g2,g1)
    c: Equal(g1,g0)
    c: Coincident(g3,g0)
    c: PointOnObject(g3,g-4)
    c: Horizontal(g3)
    c: Coincident(g4,g1)
    c: PointOnObject(g4,g-4)
    c: Horizontal(g4)
    c: Symmetric(g3,g3,g5)
    c: Symmetric(g4,g4,g6)
    c: Coincident(g7,g5)
    c: Coincident(g8,g6)
    c: Equal(g8,g7)
    c: Diameter(g7) = 2.6
FEATURE [PartDesign::Pocket] Pocket032
  BaseFeature = -> Pocket031
  Direction = (1,0,2e-16)
  Length = 6
  Length2 = 5
  Placement = pos=(0,0,0) rot=(1,0,0;1.5708rad)
  Profile = -> Sketch062
  ReferenceAxis = -> Sketch062 [N_Axis]
  Refine = true
  Suppressed = false
  Type = 0
  expr: Length = VarSet.HoleDepth
FEATURE [Sketcher::SketchObject] Sketch063
  ArcFitTolerance = 1e-06
  AttachmentSupport = -> [Pocket032]
  ExternalGeometry = -> [Pocket032]
  FullyConstrained = true
  MakeInternals = false
  MapMode = 5
  Placement = pos=(0,-84,0) rot=(1,0,0;1.5708rad)
  expr: Constraints[19] = VarSet.HoleDiameter
  sketch-geometry (9):
    g0: LineSegment [constr] StartX=0 StartY=5 StartZ=0 EndX=28 EndY=5 EndZ=0
    g1: LineSegment [constr] StartX=28 StartY=5 StartZ=0 EndX=56 EndY=5 EndZ=0
    g2: LineSegment [constr] StartX=56 StartY=5 StartZ=0 EndX=84 EndY=5 EndZ=0
    g3: LineSegment [constr] StartX=28 StartY=5 StartZ=0 EndX=28 EndY=0 EndZ=0
    g4: LineSegment [constr] StartX=56 StartY=5 StartZ=0 EndX=56 EndY=0 EndZ=0
    g5: GeomPoint [constr] X=28 Y=2.5 Z=0
    g6: GeomPoint [constr] X=56 Y=2.5 Z=0
    g7: Circle CenterX=28 CenterY=2.5 CenterZ=0 NormalX=0 NormalY=0 NormalZ=1 AngleXU=0 Radius=1.3
    g8: Circle CenterX=56 CenterY=2.5 CenterZ=0 NormalX=0 NormalY=0 NormalZ=1 AngleXU=0 Radius=1.3
  constraints (20):
    c: Coincident(g0,g-3)
    c: Horizontal(g0)
    c: Coincident(g1,g0)
    c: Horizontal(g1)
    c: Coincident(g2,g1)
    c: Coincident(g2,g-4)
    c: Equal(g2,g1)
    c: Equal(g1,g0)
    c: Coincident(g3,g0)
    c: PointOnObject(g3,g-5)
    c: Vertical(g3)
    c: Coincident(g4,g1)
    c: PointOnObject(g4,g-5)
    c: Vertical(g4)
    c: Symmetric(g3,g3,g5)
    c: Symmetric(g4,g4,g6)
    c: Coincident(g7,g5)
    c: Coincident(g8,g6)
    c: Equal(g7,g8)
    c: Diameter(g7) = 2.6
FEATURE [PartDesign::Pocket] Pocket033
  BaseFeature = -> Pocket032
  Direction = (0,1,-2e-16)
  Length = 6
  Length2 = 5
  Placement = pos=(0,0,0) rot=(1,0,0;1.5708rad)
  Profile = -> Sketch063
  ReferenceAxis = -> Sketch063 [N_Axis]
  Refine = true
  Suppressed = false
  Type = 0
  expr: Length = VarSet.HoleDepth
FEATURE [Sketcher::SketchObject] Sketch064
  ArcFitTolerance = 1e-06
  AttachmentSupport = -> [Pocket033]
  ExternalGeometry = -> [Pocket033]
  FullyConstrained = true
  MakeInternals = false
  MapMode = 5
  Placement = pos=(0,1.7e-15,0) rot=(-1,0,0;1.5708rad)
  expr: Constraints[19] = VarSet.HoleDiameter
  sketch-geometry (9):
    g0: LineSegment [constr] StartX=0 StartY=-5 StartZ=0 EndX=28 EndY=-5 EndZ=0
    g1: LineSegment [constr] StartX=28 StartY=-5 StartZ=0 EndX=56 EndY=-5 EndZ=0
    g2: LineSegment [constr] StartX=56 StartY=-5 StartZ=0 EndX=84 EndY=-5 EndZ=0
    g3: LineSegment [constr] StartX=28 StartY=-5 StartZ=0 EndX=28 EndY=0 EndZ=0
    g4: LineSegment [constr] StartX=56 StartY=-5 StartZ=0 EndX=56 EndY=0 EndZ=0
    g5: GeomPoint [constr] X=28 Y=-2.5 Z=0
    g6: GeomPoint [constr] X=56 Y=-2.5 Z=0
    g7: Circle CenterX=28 CenterY=-2.5 CenterZ=0 NormalX=0 NormalY=0 NormalZ=1 AngleXU=0 Radius=1.3
    g8: Circle CenterX=56 CenterY=-2.5 CenterZ=0 NormalX=0 NormalY=0 NormalZ=1 AngleXU=0 Radius=1.3
  constraints (20):
    c: Coincident(g-4,g0)
    c: Horizontal(g0)
    c: Coincident(g0,g1)
    c: Horizontal(g1)
    c: Coincident(g1,g2)
    c: Coincident(g2,g-5)
    c: Equal(g0,g1)
    c: Equal(g1,g2)
    c: Coincident(g3,g0)
    c: PointOnObject(g3,g-3)
    c: Vertical(g3)
    c: Coincident(g4,g1)
    c: PointOnObject(g4,g-3)
    c: Vertical(g4)
    c: Symmetric(g3,g3,g5)
    c: Symmetric(g4,g4,g6)
    c: Coincident(g7,g5)
    c: Coincident(g8,g6)
    c: Equal(g7,g8)
    c: Diameter(g7) = 2.6
FEATURE [PartDesign::Pocket] Pocket034
  BaseFeature = -> Pocket033
  Direction = (0,-1,-2e-16)
  Length = 6
  Length2 = 5
  Placement = pos=(0,0,0) rot=(1,0,0;1.5708rad)
  Profile = -> Sketch064
  ReferenceAxis = -> Sketch064 [N_Axis]
  Refine = true
  Suppressed = false
  Type = 0
  expr: Length = VarSet.HoleDepth
FEATURE [PartDesign::Body] Body  label="Base with Integrated Gridfinity"
  AllowCompound = false
  Group = -> [Sketch,Pad,Sketch001,Pad001,Sketch002,Hole,Sketch003,Pad002,DatumPlane,Sketch004,Pad003,DatumPlane001,Sketch005,Pad004,Chamfer,Chamfer001,Chamfer002,Chamfer003,Chamfer004,Chamfer005,Chamfer006,Chamfer007,Chamfer008,Chamfer009,Chamfer010,Chamfer011,Chamfer012,Fillet,Sketch027,Pad015,Fillet005,Sketch038,Pocket016,Sketch061,VarSet,Pocket031,Sketch062,Pocket032,Sketch063,Pocket033,Sketch064,Pocket034]
  Origin = -> Origin
  Tip = -> Pocket034
FEATURE [PartDesign::FeatureBase] Clone001
  BaseFeature = -> Body
  Suppressed = false
FEATURE [Sketcher::SketchObject] Sketch028
  ArcFitTolerance = 1e-06
  AttachmentSupport = -> [Clone001]
  ExternalGeometry = -> [Clone001]
  FullyConstrained = true
  MakeInternals = false
  MapMode = 5
  Placement = pos=(0,1.7e-15,0) rot=(0,0.707107,0.707107;3.14159rad)
  sketch-geometry (4):
    g0: LineSegment StartX=-84 StartY=0 StartZ=0 EndX=-84 EndY=-7 EndZ=0
    g1: LineSegment StartX=-84 StartY=-7 StartZ=0 EndX=0 EndY=-7 EndZ=0
    g2: LineSegment StartX=0 StartY=-7 StartZ=0 EndX=0 EndY=0 EndZ=0
    g3: LineSegment StartX=0 StartY=0 StartZ=0 EndX=-84 EndY=0 EndZ=0
  constraints (11):
    c: Coincident(g0,g1)
    c: Coincident(g1,g2)
    c: Coincident(g2,g3)
    c: Coincident(g3,g0)
    c: Vertical(g0)
    c: Vertical(g2)
    c: Horizontal(g1)
    c: Horizontal(g3)
    c: Distance(g1,g3) = 7
    c: Coincident(g0,g-4)
    c: PointOnObject(g1,g-2)
FEATURE [PartDesign::Pocket] Pocket009
  BaseFeature = -> Clone001
  Direction = (0,-1,2e-16)
  Length = 5
  Length2 = 5
  Profile = -> Sketch028
  ReferenceAxis = -> Sketch028 [N_Axis]
  Refine = true
  Suppressed = false
  Type = 1
FEATURE [Sketcher::SketchObject] Sketch029
  ArcFitTolerance = 1e-06
  AttachmentSupport = -> [Pocket009]
  ExternalGeometry = -> [Pocket009]
  FullyConstrained = true
  MakeInternals = false
  MapMode = 5
  Placement = pos=(0,0,3e-16) rot=(1,0,0;3.14159rad)
  sketch-geometry (20):
    g0: LineSegment [constr] StartX=0 StartY=84 StartZ=0 EndX=0 EndY=79 EndZ=0
    g1: LineSegment [constr] StartX=0 StartY=79 StartZ=0 EndX=5 EndY=79 EndZ=0
    g2: LineSegment [constr] StartX=5 StartY=79 StartZ=0 EndX=5 EndY=84 EndZ=0
    g3: LineSegment [constr] StartX=5 StartY=84 StartZ=0 EndX=0 EndY=84 EndZ=0
    g4: LineSegment [constr] StartX=0 StartY=0 StartZ=0 EndX=5 EndY=0 EndZ=0
    g5: LineSegment [constr] StartX=5 StartY=0 StartZ=0 EndX=5 EndY=5 EndZ=0
    g6: LineSegment [constr] StartX=5 StartY=5 StartZ=0 EndX=0 EndY=5 EndZ=0
    g7: LineSegment [constr] StartX=0 StartY=5 StartZ=0 EndX=0 EndY=0 EndZ=0
    g8: LineSegment [constr] StartX=84 StartY=0 StartZ=0 EndX=84 EndY=5 EndZ=0
    g9: LineSegment [constr] StartX=84 StartY=5 StartZ=0 EndX=79 EndY=5 EndZ=0
    g10: LineSegment [constr] StartX=79 StartY=5 StartZ=0 EndX=79 EndY=0 EndZ=0
    g11: LineSegment [constr] StartX=79 StartY=0 StartZ=0 EndX=84 EndY=0 EndZ=0
    g12: LineSegment [constr] StartX=84 StartY=84 StartZ=0 EndX=79 EndY=84 EndZ=0
    g13: LineSegment [constr] StartX=79 StartY=84 StartZ=0 EndX=79 EndY=79 EndZ=0
    g14: LineSegment [constr] StartX=79 StartY=79 StartZ=0 EndX=84 EndY=79 EndZ=0
    g15: LineSegment [constr] StartX=84 StartY=79 StartZ=0 EndX=84 EndY=84 EndZ=0
    g16: Circle CenterX=5 CenterY=79 CenterZ=0 NormalX=0 NormalY=0 NormalZ=1 AngleXU=0 Radius=1.5
    g17: Circle CenterX=5 CenterY=5 CenterZ=0 NormalX=0 NormalY=0 NormalZ=1 AngleXU=0 Radius=1.5
    g18: Circle CenterX=79 CenterY=5 CenterZ=0 NormalX=0 NormalY=0 NormalZ=1 AngleXU=0 Radius=1.5
    g19: Circle CenterX=79 CenterY=79 CenterZ=0 NormalX=0 NormalY=0 NormalZ=1 AngleXU=0 Radius=1.5
  constraints (52):
    c: Coincident(g0,g1)
    c: Coincident(g1,g2)
    c: Coincident(g2,g3)
    c: Coincident(g3,g0)
    c: Vertical(g0)
    c: Vertical(g2)
    c: Horizontal(g1)
    c: Horizontal(g3)
    c: Distance(g0,g2) = 5
    c: Distance(g1,g3) = 5
    c: Coincident(g0,g-4)
    c: Coincident(g4,g5)
    c: Coincident(g5,g6)
    c: Coincident(g6,g7)
    c: Coincident(g7,g4)
    c: Horizontal(g4)
    c: Horizontal(g6)
    c: Vertical(g5)
    c: Vertical(g7)
    c: Distance(g5,g7) = 5
    c: Distance(g4,g6) = 5
    c: Coincident(g4,g-1)
    c: Coincident(g8,g9)
    c: Coincident(g9,g10)
    c: Coincident(g10,g11)
    c: Coincident(g11,g8)
    c: Vertical(g8)
    c: Vertical(g10)
    c: Horizontal(g9)
    c: Horizontal(g11)
    c: Distance(g8,g10) = 5
    c: Distance(g9,g11) = 5
    c: Coincident(g8,g-6)
    c: Coincident(g12,g13)
    c: Coincident(g13,g14)
    c: Coincident(g14,g15)
    c: Coincident(g15,g12)
    c: Horizontal(g12)
    c: Horizontal(g14)
    c: Vertical(g13)
    c: Vertical(g15)
    c: Distance(g13,g15) = 5
    c: Distance(g12,g14) = 5
    c: Coincident(g12,g-6)
    c: Diameter(g16) = 3
    c: Coincident(g16,g1)
    c: Diameter(g17) = 3
    c: Coincident(g17,g5)
    c: Diameter(g18) = 3
    c: Coincident(g18,g9)
    c: Diameter(g19) = 3
    c: Coincident(g19,g13)
FEATURE [PartDesign::Pocket] Pocket010
  BaseFeature = -> Pocket009
  Direction = (0,0,1)
  Length = 4
  Length2 = 5
  Profile = -> Sketch029
  ReferenceAxis = -> Sketch029 [N_Axis]
  Refine = true
  Suppressed = false
  Type = 0
FEATURE [Sketcher::SketchObject] Sketch057
  ArcFitTolerance = 1e-06
  AttachmentSupport = -> [Pocket010]
  ExternalGeometry = -> [Pocket010]
  FullyConstrained = true
  MakeInternals = false
  MapMode = 5
  Placement = pos=(0,0,3e-16) rot=(1,0,0;3.14159rad)
  sketch-geometry (4):
    g0: Circle CenterX=5 CenterY=79 CenterZ=0 NormalX=0 NormalY=0 NormalZ=1 AngleXU=0 Radius=1.5
    g1: Circle CenterX=79 CenterY=79 CenterZ=0 NormalX=0 NormalY=0 NormalZ=1 AngleXU=0 Radius=1.5
    g2: Circle CenterX=79 CenterY=5 CenterZ=0 NormalX=0 NormalY=0 NormalZ=1 AngleXU=0 Radius=1.5
    g3: Circle CenterX=5 CenterY=5 CenterZ=0 NormalX=0 NormalY=0 NormalZ=1 AngleXU=0 Radius=1.5
  constraints (8):
    c: Coincident(g0,g-3)
    c: Equal(g0,g-3)
    c: Coincident(g1,g-4)
    c: Equal(g1,g-4)
    c: Coincident(g2,g-5)
    c: Equal(g2,g-5)
    c: Coincident(g3,g-6)
    c: Equal(g3,g-6)
FEATURE [PartDesign::Pocket] Pocket028
  BaseFeature = -> Pocket010
  Direction = (0,0,1)
  Length = 10
  Length2 = 5
  Profile = -> Sketch057
  ReferenceAxis = -> Sketch057 [N_Axis]
  Refine = true
  Suppressed = false
  Type = 0
FEATURE [Sketcher::SketchObject] Sketch058
  ArcFitTolerance = 1e-06
  AttachmentSupport = -> [Pocket028]
  ExternalGeometry = -> [Pocket028]
  FullyConstrained = true
  MakeInternals = false
  MapMode = 5
  Placement = pos=(0,2.2e-15,5) rot=(0,0,1;0rad)
  sketch-geometry (4):
    g0: Circle CenterX=5 CenterY=-5 CenterZ=0 NormalX=0 NormalY=0 NormalZ=1 AngleXU=0 Radius=3
    g1: Circle CenterX=5 CenterY=-79 CenterZ=0 NormalX=0 NormalY=0 NormalZ=1 AngleXU=0 Radius=3
    g2: Circle CenterX=79 CenterY=-79 CenterZ=0 NormalX=0 NormalY=0 NormalZ=1 AngleXU=0 Radius=3
    g3: Circle CenterX=79 CenterY=-5 CenterZ=0 NormalX=0 NormalY=0 NormalZ=1 AngleXU=0 Radius=3
  constraints (8):
    c: Diameter(g0) = 6
    c: Coincident(g0,g-3)
    c: Diameter(g1) = 6
    c: Coincident(g1,g-4)
    c: Diameter(g2) = 6
    c: Coincident(g2,g-5)
    c: Diameter(g3) = 6
    c: Coincident(g3,g-6)
FEATURE [PartDesign::Pocket] Pocket029
  BaseFeature = -> Pocket028
  Direction = (0,0,-1)
  Length = 3.25
  Length2 = 5
  Profile = -> Sketch058
  ReferenceAxis = -> Sketch058 [N_Axis]
  Refine = true
  Suppressed = false
  Type = 0
FEATURE [Sketcher::SketchObject] Sketch059
  ArcFitTolerance = 1e-06
  AttachmentSupport = -> [Pocket029]
  ExternalGeometry = -> [Pocket029]
  FullyConstrained = true
  MakeInternals = false
  MapMode = 5
  Placement = pos=(0,0,3e-16) rot=(1,0,0;3.14159rad)
  sketch-geometry (8):
    g0: LineSegment StartX=0 StartY=84 StartZ=0 EndX=0 EndY=0 EndZ=0
    g1: LineSegment StartX=0 StartY=0 StartZ=0 EndX=84 EndY=0 EndZ=0
    g2: LineSegment StartX=84 StartY=0 StartZ=0 EndX=84 EndY=84 EndZ=0
    g3: LineSegment StartX=84 StartY=84 StartZ=0 EndX=0 EndY=84 EndZ=0
    g4: Circle CenterX=79 CenterY=5 CenterZ=0 NormalX=0 NormalY=0 NormalZ=1 AngleXU=0 Radius=1.5
    g5: Circle CenterX=5 CenterY=5 CenterZ=0 NormalX=0 NormalY=0 NormalZ=1 AngleXU=0 Radius=1.5
    g6: Circle CenterX=5 CenterY=79 CenterZ=0 NormalX=0 NormalY=0 NormalZ=1 AngleXU=0 Radius=1.5
    g7: Circle CenterX=79 CenterY=79 CenterZ=0 NormalX=0 NormalY=0 NormalZ=1 AngleXU=0 Radius=1.5
  constraints (18):
    c: Coincident(g0,g1)
    c: Coincident(g1,g2)
    c: Coincident(g2,g3)
    c: Coincident(g3,g0)
    c: Vertical(g0)
    c: Vertical(g2)
    c: Horizontal(g1)
    c: Horizontal(g3)
    c: Coincident(g0,g-3)
    c: Coincident(g1,g-4)
    c: Coincident(g4,g-8)
    c: Equal(g4,g-8)
    c: Coincident(g5,g-5)
    c: Equal(g5,g-5)
    c: Coincident(g6,g-6)
    c: Equal(g6,g-6)
    c: Coincident(g7,g-7)
    c: Equal(g7,g-7)
FEATURE [PartDesign::Pad] Pad025
  BaseFeature = -> Pocket029
  Direction = (0,0,-1)
  Length = 1.25
  Length2 = 10
  Profile = -> Sketch059
  ReferenceAxis = -> Sketch059 [N_Axis]
  Refine = true
  Suppressed = false
  Type = 0
FEATURE [PartDesign::Pocket] Pocket030
  BaseFeature = -> Pad025
  Direction = (0,0,1)
  Length = 12
  Length2 = 5
  Profile = -> Sketch060
  ReferenceAxis = -> Sketch060 [N_Axis]
  Refine = true
  Suppressed = false
  Type = 1
FEATURE [PartDesign::FeatureBase] BaseFeature
  BaseFeature = -> BinBase
  Suppressed = false
FEATURE [PartDesign::Pocket] Pocket035
  BaseFeature = -> BaseFeature
  Direction = (0,0,1)
  Length = 5
  Length2 = 5
  Profile = -> BaseFeature [Face632,Face631,Face636,Face635,Face232,Face231,Face630,Face629]
  Refine = true
  Suppressed = false
  Type = 2
FEATURE [PartDesign::Body] Body009  label="Gridfinity Bolt On Base"
  AllowCompound = false
  BaseFeature = -> BinBase
  Group = -> [BaseFeature,Pocket035]
  Origin = -> Origin009
  Placement = pos=(-72,-63,0) rot=(0,0,1;0rad)
  Tip = -> Pocket035
FEATURE [PartDesign::FeaturePython] ScrewTogetherBaseplate  # WARN: FeaturePython — macro-defined, semantics opaque (R4)
  BaseProfileBottomChamfer = 0.7
  BaseProfileHeight = 4.25
  BaseProfileTopChamfer = 1.75
  BaseProfileVerticalSection = 1.8
  BaseThickness = 6.4
  BaseplateProfileTotalHeight = 0
  BaseplateTopLedgeWidth = 0.4
  BinBottomRadius = 1.15
  BinOuterRadius = 4
  BinVerticalRadius = 1.85
  Clearance = 0.25
  ConnectionHoleDiameter = 3.2
  GridSize = 42
  HeightUnitValue = 7
  MagnetBaseHole = 3
  MagnetBottomChamfer = 2
  MagnetChamfer = 0.4
  MagnetEdgeThickness = 1.2
  MagnetHoleDepth = 2.4
  MagnetHoleDiameter = 6.5
  MagnetHoleDistanceFromEdge = 8
  MagnetHolesShape = 0
  ScrewHoleDiameter = 3
  SmallFillet = 1
  Suppressed = false
  TotalHeight = 10.65
  version = 0.8.0
  xGridUnits = 4
  xTotalWidth = 168
  yGridUnits = 4
  yTotalWidth = 168
FEATURE [PartDesign::Body] Body010  label="Gridfinity Bolt Together Mesh"
  AllowCompound = false
  Group = -> [ScrewTogetherBaseplate]
  Origin = -> Origin010
  Placement = pos=(-59,45,0) rot=(0,0,1;0rad)
  Tip = -> ScrewTogetherBaseplate
FEATURE [Sketcher::SketchObject] Sketch065
  ArcFitTolerance = 1e-06
  AttachmentSupport = -> [Pocket030]
  ExternalGeometry = -> [Pocket030]
  FullyConstrained = true
  MakeInternals = false
  MapMode = 5
  Placement = pos=(0,-84,-8.9e-14) rot=(1,0,0;1.5708rad)
  sketch-geometry (6):
    g0: Circle CenterX=28 CenterY=2.5 CenterZ=0 NormalX=0 NormalY=0 NormalZ=1 AngleXU=0 Radius=1.3
    g1: Circle CenterX=56 CenterY=2.5 CenterZ=0 NormalX=0 NormalY=0 NormalZ=1 AngleXU=0 Radius=1.3
    g2: LineSegment StartX=0 StartY=5 StartZ=0 EndX=0 EndY=-1.25 EndZ=0
    g3: LineSegment StartX=0 StartY=-1.25 StartZ=0 EndX=84 EndY=-1.25 EndZ=0
    g4: LineSegment StartX=84 StartY=-1.25 StartZ=0 EndX=84 EndY=5 EndZ=0
    g5: LineSegment StartX=84 StartY=5 StartZ=0 EndX=0 EndY=5 EndZ=0
  constraints (14):
    c: Coincident(g0,g-8)
    c: Equal(g0,g-8)
    c: Coincident(g1,g-7)
    c: Equal(g1,g-7)
    c: Coincident(g2,g3)
    c: Coincident(g3,g4)
    c: Coincident(g4,g5)
    c: Coincident(g5,g2)
    c: Vertical(g2)
    c: Vertical(g4)
    c: Horizontal(g3)
    c: Horizontal(g5)
    c: Coincident(g2,g-5)
    c: Coincident(g3,g-3)
FEATURE [PartDesign::Pad] Pad026
  BaseFeature = -> Pocket030
  Direction = (0,-1,-1.1e-15)
  Length = 38
  Length2 = 10
  Profile = -> Sketch065
  ReferenceAxis = -> Sketch065 [N_Axis]
  Refine = true
  Suppressed = false
  Type = 0
FEATURE [Sketcher::SketchObject] Sketch066
  ArcFitTolerance = 1e-06
  AttachmentSupport = -> [Pocket027]
  FullyConstrained = true
  MakeInternals = false
  MapMode = 5
  Placement = pos=(42,-119,14) rot=(0.57735,-0.57735,0.57735;2.0944rad)
  sketch-geometry (2):
    g0: Circle CenterX=0 CenterY=0 CenterZ=0 NormalX=0 NormalY=0 NormalZ=1 AngleXU=0 Radius=3.75
    g1: Circle CenterX=0 CenterY=0 CenterZ=0 NormalX=0 NormalY=0 NormalZ=1 AngleXU=0 Radius=8.25
  constraints (4):
    c: Coincident(g0,g-1)
    c: Diameter(g1) = 16.5
    c: Coincident(g1,g0)
    c: Diameter(g0) = 7.5
FEATURE [PartDesign::Pocket] Pocket036
  BaseFeature = -> Pocket027
  Direction = (0,1,0)
  Length = 25
  Length2 = 5
  Placement = pos=(42,-84,14) rot=(0.57735,-0.57735,0.57735;2.0944rad)
  Profile = -> Sketch066
  ReferenceAxis = -> Sketch066 [N_Axis]
  Refine = true
  Suppressed = false
  Type = 1
FEATURE [Sketcher::SketchObject] Sketch067
  ArcFitTolerance = 1e-06
  AttachmentSupport = -> [Pocket036]
  FullyConstrained = true
  MakeInternals = false
  MapMode = 5
  Placement = pos=(42,-119,14) rot=(0.57735,-0.57735,0.57735;2.0944rad)
  sketch-geometry (5):
    g0: LineSegment StartX=-1.55 StartY=-2.55 StartZ=0 EndX=1.55 EndY=-2.55 EndZ=0
    g1: LineSegment StartX=1.55 StartY=-2.55 StartZ=0 EndX=1.55 EndY=2.55 EndZ=0
    g2: LineSegment StartX=1.55 StartY=2.55 StartZ=0 EndX=-1.55 EndY=2.55 EndZ=0
    g3: LineSegment StartX=-1.55 StartY=2.55 StartZ=0 EndX=-1.55 EndY=-2.55 EndZ=0
    g4: GeomPoint [constr] X=0 Y=0 Z=0
  constraints (12):
    c: Coincident(g0,g1)
    c: Coincident(g1,g2)
    c: Coincident(g2,g3)
    c: Coincident(g3,g0)
    c: Horizontal(g0)
    c: Horizontal(g2)
    c: Vertical(g1)
    c: Vertical(g3)
    c: Symmetric(g2,g0,g4)
    c: Distance(g1,g3) = 3.1
    c: Distance(g0,g2) = 5.1
    c: Coincident(g4,g-1)
FEATURE [PartDesign::Pocket] Pocket037
  BaseFeature = -> Pocket036
  Direction = (0,1,0)
  Length = 6
  Length2 = 5
  Placement = pos=(42,-84,14) rot=(0.57735,-0.57735,0.57735;2.0944rad)
  Profile = -> Sketch067
  ReferenceAxis = -> Sketch067 [N_Axis]
  Refine = true
  Suppressed = false
  Type = 0
FEATURE [Sketcher::SketchObject] Sketch068
  ArcFitTolerance = 1e-06
  AttachmentSupport = -> [Pocket037]
  ExternalGeometry = -> [Pocket037]
  FullyConstrained = true
  MakeInternals = false
  MapMode = 5
  Placement = pos=(42,-119,14) rot=(0.57735,-0.57735,0.57735;2.0944rad)
  sketch-geometry (2):
    g0: Circle CenterX=0 CenterY=0 CenterZ=0 NormalX=0 NormalY=0 NormalZ=1 AngleXU=0 Radius=5
    g1: Circle CenterX=0 CenterY=0 CenterZ=0 NormalX=0 NormalY=0 NormalZ=1 AngleXU=0 Radius=3.75
  constraints (4):
    c: Diameter(g0) = 10
    c: Coincident(g0,g-1)
    c: Coincident(g1,g0)
    c: Diameter(g1) = 7.5
FEATURE [PartDesign::Pad] Pad027
  BaseFeature = -> Pocket037
  Direction = (0,-1,0)
  Length = 10
  Length2 = 10
  Placement = pos=(42,-84,14) rot=(0.57735,-0.57735,0.57735;2.0944rad)
  Profile = -> Sketch068
  ReferenceAxis = -> Sketch068 [N_Axis]
  Refine = true
  Reversed = true
  Suppressed = false
  Type = 0
FEATURE [PartDesign::Chamfer] Chamfer017
  Angle = 45
  Base = -> Pad027 [Edge106]
  BaseFeature = -> Pad027
  ChamferType = 0
  FlipDirection = false
  Placement = pos=(42,-84,14) rot=(0.57735,-0.57735,0.57735;2.0944rad)
  Refine = true
  Size = 1
  Size2 = 1
  SupportTransform = false
  Suppressed = false
  UseAllEdges = false
FEATURE [PartDesign::Body] Body005  label="Adjuster"
  AllowCompound = false
  Group = -> [ShapeBinder003,DatumPlane006,Sketch019,Pad009,Sketch020,Pad010,Sketch021,Pad011,Sketch022,Pocket007,Fillet004,DatumPoint,VThreadProfile,Helix,AdditivePipe,ShapeBinder004,DatumPlane007,Sketch023,Pad012,Sketch035,Pocket013,Sketch036,Pocket014,Sketch055,Pad024,Sketch056,Pocket027,Sketch066,Pocket036,Sketch067,Pocket037,Sketch068,Pad027,Chamfer017]
  Origin = -> Origin005
  Placement = pos=(-93,0,0) rot=(0,0,1;0rad)
  Tip = -> Chamfer017
FEATURE [PartDesign::ShapeBinder] CopyChamfer017
  Placement = pos=(42,-84,14) rot=(0.57735,-0.57735,0.57735;2.0944rad)
  TraceSupport = false
FEATURE [PartDesign::Plane] DatumPlane012
  AttachmentSupport = -> [CopyChamfer017]
  Length = 63.2646
  MapMode = 5
  Placement = pos=(42,-119,14) rot=(0.57735,-0.57735,0.57735;2.0944rad)
  ResizeMode = 0
  Width = 101.239
FEATURE [Sketcher::SketchObject] Sketch069
  ArcFitTolerance = 1e-06
  AttachmentSupport = -> [DatumPlane012]
  FullyConstrained = true
  MakeInternals = false
  MapMode = 5
  Placement = pos=(42,-119,14) rot=(0.57735,-0.57735,0.57735;2.0944rad)
  sketch-geometry (9):
    g0: ArcOfCircle CenterX=0 CenterY=0 CenterZ=0 NormalX=0 NormalY=0 NormalZ=1 AngleXU=0 Radius=2.5 StartAngle=0.927295 EndAngle=2.2143
    g1: LineSegment [constr] StartX=-1.5 StartY=-2.5 StartZ=0 EndX=1.5 EndY=-2.5 EndZ=0
    g2: LineSegment [constr] StartX=1.5 StartY=-2.5 StartZ=0 EndX=1.5 EndY=2.5 EndZ=0
    g3: LineSegment [constr] StartX=1.5 StartY=2.5 StartZ=0 EndX=-1.5 EndY=2.5 EndZ=0
    g4: LineSegment [constr] StartX=-1.5 StartY=2.5 StartZ=0 EndX=-1.5 EndY=-2.5 EndZ=0
    g5: GeomPoint [constr] X=0 Y=0 Z=0
    g6: ArcOfCircle CenterX=0 CenterY=0 CenterZ=0 NormalX=0 NormalY=0 NormalZ=1 AngleXU=0 Radius=2.5 StartAngle=4.06889 EndAngle=5.35589
    g7: LineSegment StartX=-1.5 StartY=2 StartZ=0 EndX=-1.5 EndY=-2 EndZ=0
    g8: LineSegment StartX=1.5 StartY=-2 StartZ=0 EndX=1.5 EndY=2 EndZ=0
  constraints (24):
    c: Diameter(g0) = 5
    c: Coincident(g0,g-1)
    c: Coincident(g1,g2)
    c: Coincident(g2,g3)
    c: Coincident(g3,g4)
    c: Coincident(g4,g1)
    c: Horizontal(g1)
    c: Horizontal(g3)
    c: Vertical(g2)
    c: Vertical(g4)
    c: Symmetric(g3,g1,g5)
    c: Distance(g2,g4) = 3
    c: Distance(g1,g3) = 5
    c: Coincident(g5,g0)
    c: PointOnObject(g6,g2)
    c: PointOnObject(g0,g2)
    c: Equal(g0,g6)
    c: PointOnObject(g0,g4)
    c: PointOnObject(g6,g4)
    c: Coincident(g0,g6)
    c: Coincident(g7,g0)
    c: Coincident(g7,g6)
    c: Coincident(g8,g6)
    c: Coincident(g8,g0)
FEATURE [PartDesign::Pad] Pad028
  Direction = (0,-1,0)
  Length = 6
  Length2 = 10
  Placement = pos=(42,-119,14) rot=(0.57735,-0.57735,0.57735;2.0944rad)
  Profile = -> Sketch069
  ReferenceAxis = -> Sketch069 [N_Axis]
  Refine = true
  Reversed = true
  Suppressed = false
  Type = 0
FEATURE [Sketcher::SketchObject] Sketch070
  ArcFitTolerance = 1e-06
  AttachmentSupport = -> [Pad028]
  FullyConstrained = true
  MakeInternals = false
  MapMode = 5
  Placement = pos=(42,-119,14) rot=(0.57735,-0.57735,0.57735;2.0944rad)
  sketch-geometry (1):
    g0: Circle CenterX=0 CenterY=0 CenterZ=0 NormalX=0 NormalY=0 NormalZ=1 AngleXU=0 Radius=2.5
  constraints (2):
    c: Diameter(g0) = 5
    c: Coincident(g0,g-1)
FEATURE [PartDesign::Pad] Pad029
  BaseFeature = -> Pad028
  Direction = (0,-1,0)
  Length = 1.5
  Length2 = 10
  Placement = pos=(42,-119,14) rot=(0.57735,-0.57735,0.57735;2.0944rad)
  Profile = -> Sketch070
  ReferenceAxis = -> Sketch070 [N_Axis]
  Refine = true
  Suppressed = false
  Type = 0
FEATURE [Sketcher::SketchObject] Sketch071
  ArcFitTolerance = 1e-06
  AttachmentSupport = -> [Pad029]
  FullyConstrained = true
  MakeInternals = false
  MapMode = 5
  Placement = pos=(42,-120.5,14) rot=(0.57735,-0.57735,0.57735;2.0944rad)
  sketch-geometry (1):
    g0: Circle CenterX=0 CenterY=0 CenterZ=0 NormalX=0 NormalY=0 NormalZ=1 AngleXU=0 Radius=4.75
  constraints (2):
    c: Diameter(g0) = 9.5
    c: Coincident(g0,g-1)
FEATURE [PartDesign::Pad] Pad030
  BaseFeature = -> Pad029
  Direction = (0,-1,0)
  Length = 1.5
  Length2 = 10
  Placement = pos=(42,-119,14) rot=(0.57735,-0.57735,0.57735;2.0944rad)
  Profile = -> Sketch071
  ReferenceAxis = -> Sketch071 [N_Axis]
  Refine = true
  Suppressed = false
  Type = 0
FEATURE [Sketcher::SketchObject] Sketch072
  ArcFitTolerance = 1e-06
  AttachmentSupport = -> [Pad030]
  FullyConstrained = true
  MakeInternals = false
  MapMode = 5
  Placement = pos=(42,-122,14) rot=(0.57735,-0.57735,0.57735;2.0944rad)
  sketch-geometry (18):
    g0: LineSegment [constr] StartX=0 StartY=0 StartZ=0 EndX=-8 EndY=0 EndZ=0
    g1: LineSegment [constr] StartX=-8 StartY=0 StartZ=0 EndX=-8 EndY=17.5 EndZ=0
    g2: LineSegment [constr] StartX=-8 StartY=0 StartZ=0 EndX=-8 EndY=-17.5 EndZ=0
    g3: Circle CenterX=-8 CenterY=17.5 CenterZ=0 NormalX=0 NormalY=0 NormalZ=1 AngleXU=0 Radius=2
    g4: Circle CenterX=-8 CenterY=-17.5 CenterZ=0 NormalX=0 NormalY=0 NormalZ=1 AngleXU=0 Radius=2
    g5: ArcOfCircle CenterX=-8 CenterY=17.5 CenterZ=0 NormalX=0 NormalY=0 NormalZ=1 AngleXU=0 Radius=3.5 StartAngle=0 EndAngle=3.14159
    g6: ArcOfCircle [constr] CenterX=-8 CenterY=0 CenterZ=0 NormalX=0 NormalY=0 NormalZ=1 AngleXU=0 Radius=14 StartAngle=1.82348 EndAngle=7.6013
    g7: LineSegment [constr] StartX=-8 StartY=-17.5 StartZ=0 EndX=-11.5 EndY=-17.5 EndZ=0
    g8: LineSegment [constr] StartX=-8 StartY=-17.5 StartZ=0 EndX=-4.5 EndY=-17.5 EndZ=0
    g9: LineSegment [constr] StartX=-8 StartY=17.5 StartZ=0 EndX=-4.5 EndY=17.5 EndZ=0
    g10: LineSegment [constr] StartX=-8 StartY=17.5 StartZ=0 EndX=-11.5 EndY=17.5 EndZ=0
    g11: LineSegment StartX=-4.5 StartY=17.5 StartZ=0 EndX=-4.5 EndY=13.5554 EndZ=0
    g12: LineSegment StartX=-11.5 StartY=17.5 StartZ=0 EndX=-11.5 EndY=13.5554 EndZ=0
    g13: ArcOfCircle CenterX=-8 CenterY=0 CenterZ=0 NormalX=0 NormalY=0 NormalZ=1 AngleXU=0 Radius=14 StartAngle=1.82348 EndAngle=4.45971
    g14: ArcOfCircle CenterX=-8 CenterY=0 CenterZ=0 NormalX=0 NormalY=0 NormalZ=1 AngleXU=0 Radius=14 StartAngle=4.96507 EndAngle=7.6013
    g15: ArcOfCircle CenterX=-8 CenterY=-17.5 CenterZ=0 NormalX=0 NormalY=0 NormalZ=1 AngleXU=0 Radius=3.5 StartAngle=3.14159 EndAngle=6.28319
    g16: LineSegment StartX=-11.5 StartY=-13.5554 StartZ=0 EndX=-11.5 EndY=-17.5 EndZ=0
    g17: LineSegment StartX=-4.5 StartY=-13.5554 StartZ=0 EndX=-4.5 EndY=-17.5 EndZ=0
  constraints (50):
    c: Distance(g0) = 8
    c: Coincident(g0,g-1)
    c: PointOnObject(g0,g-1)
    c: Coincident(g1,g0)
    c: Vertical(g1)
    c: Coincident(g2,g0)
    c: Vertical(g2)
    c: DistanceY(g1,g1) = 17.5
    c: Equal(g1,g2)
    c: Diameter(g3) = 4
    c: Coincident(g3,g1)
    c: Diameter(g4) = 4
    c: Coincident(g4,g2)
    c: Diameter(g5) = 7
    c: Coincident(g5,g1)
    c: Diameter(g6) = 28
    c: Coincident(g6,g0)
    c: Coincident(g7,g2)
    c: Horizontal(g7)
    c: Coincident(g8,g2)
    c: Horizontal(g8)
    c: Coincident(g9,g1)
    c: Horizontal(g9)
    c: Coincident(g10,g1)
    c: Horizontal(g10)
    c: PointOnObject(g13,g6)
    c: Coincident(g11,g9)
    c: Vertical(g11)
    c: Coincident(g12,g10)
    c: Vertical(g12)
    c: Coincident(g5,g9)
    c: Coincident(g5,g10)
    c: Coincident(g6,g12)
    c: Coincident(g6,g11)
    c: Coincident(g13,g0)
    c: PointOnObject(g13,g12)
    c: Coincident(g14,g6)
    c: Coincident(g14,g0)
    c: DistanceX(g8,g8) = 3.5
    c: Vertical(g14,g8)
    c: Vertical(g13,g7)
    c: Coincident(g15,g2)
    c: Coincident(g15,g8)
    c: Coincident(g15,g7)
    c: Coincident(g16,g13)
    c: Coincident(g16,g7)
    c: Coincident(g17,g14)
    c: Coincident(g17,g8)
    c: Vertical(g17)
    c: Tangent(g17,g15)
FEATURE [PartDesign::Pad] Pad031
  BaseFeature = -> Pad030
  Direction = (0,-1,0)
  Length = 19
  Length2 = 10
  Placement = pos=(42,-119,14) rot=(0.57735,-0.57735,0.57735;2.0944rad)
  Profile = -> Sketch072
  ReferenceAxis = -> Sketch072 [N_Axis]
  Refine = true
  Suppressed = false
  Type = 0
FEATURE [Sketcher::SketchObject] Sketch073
  ArcFitTolerance = 1e-06
  AttachmentSupport = -> [Pad031]
  ExternalGeometry = -> [Pad031]
  FullyConstrained = true
  MakeInternals = false
  MapMode = 5
  Placement = pos=(42,-141,14) rot=(0.57735,-0.57735,0.57735;2.0944rad)
  sketch-geometry (7):
    g0: LineSegment [constr] StartX=0 StartY=0 StartZ=0 EndX=-8 EndY=0 EndZ=0
    g1: LineSegment [constr] StartX=-8 StartY=0 StartZ=0 EndX=-25 EndY=0 EndZ=0
    g2: LineSegment StartX=-25 StartY=0 StartZ=0 EndX=-25 EndY=7.3 EndZ=0
    g3: LineSegment StartX=-25 StartY=0 StartZ=0 EndX=-25 EndY=-7.3 EndZ=0
    g4: LineSegment StartX=-25 StartY=7.3 StartZ=0 EndX=-19.9461 EndY=7.3 EndZ=0
    g5: LineSegment StartX=-25 StartY=-7.3 StartZ=0 EndX=-19.9461 EndY=-7.3 EndZ=0
    g6: LineSegment StartX=-19.9461 StartY=-7.3 StartZ=0 EndX=-19.9461 EndY=7.3 EndZ=0
  constraints (20):
    c: Distance(g0) = 8
    c: Coincident(g0,g-1)
    c: PointOnObject(g0,g-1)
    c: Distance(g1) = 17
    c: Coincident(g1,g0)
    c: PointOnObject(g1,g-1)
    c: Distance(g2) = 7.3
    c: Coincident(g2,g1)
    c: Vertical(g2)
    c: Coincident(g3,g1)
    c: Vertical(g3)
    c: Equal(g2,g3)
    c: Coincident(g4,g2)
    c: PointOnObject(g4,g-3)
    c: Horizontal(g4)
    c: Coincident(g5,g3)
    c: PointOnObject(g5,g-3)
    c: Horizontal(g5)
    c: Coincident(g6,g5)
    c: Coincident(g6,g4)
FEATURE [PartDesign::Pad] Pad032
  BaseFeature = -> Pad031
  Direction = (0,-1,0)
  Length = 10
  Length2 = 10
  Placement = pos=(42,-119,14) rot=(0.57735,-0.57735,0.57735;2.0944rad)
  Profile = -> Sketch073
  ReferenceAxis = -> Sketch073 [N_Axis]
  Refine = true
  Reversed = true
  Suppressed = false
  Type = 3
  UpToFace = -> Pad031 [Face9]
FEATURE [Sketcher::SketchObject] Sketch074
  ArcFitTolerance = 1e-06
  AttachmentSupport = -> [Pad032]
  ExternalGeometry = -> [Pad032]
  FullyConstrained = true
  MakeInternals = false
  MapMode = 5
  Placement = pos=(42,-141,14) rot=(0.57735,-0.57735,0.57735;2.0944rad)
  sketch-geometry (10):
    g0: LineSegment StartX=-11.5 StartY=21.4446 StartZ=0 EndX=-11.5 EndY=13.5554 EndZ=0
    g1: LineSegment StartX=-11.5 StartY=13.5554 StartZ=0 EndX=-4.5 EndY=13.5554 EndZ=0
    g2: LineSegment StartX=-4.5 StartY=13.5554 StartZ=0 EndX=-4.5 EndY=21.4446 EndZ=0
    g3: LineSegment StartX=-4.5 StartY=21.4446 StartZ=0 EndX=-11.5 EndY=21.4446 EndZ=0
    g4: GeomPoint [constr] X=-8 Y=17.5 Z=0
    g5: LineSegment StartX=-11.5 StartY=-21.4446 StartZ=0 EndX=-4.5 EndY=-21.4446 EndZ=0
    g6: LineSegment StartX=-4.5 StartY=-21.4446 StartZ=0 EndX=-4.5 EndY=-13.5554 EndZ=0
    g7: LineSegment StartX=-4.5 StartY=-13.5554 StartZ=0 EndX=-11.5 EndY=-13.5554 EndZ=0
    g8: LineSegment StartX=-11.5 StartY=-13.5554 StartZ=0 EndX=-11.5 EndY=-21.4446 EndZ=0
    g9: GeomPoint [constr] X=-8 Y=-17.5 Z=0
  constraints (22):
    c: Coincident(g0,g1)
    c: Coincident(g1,g2)
    c: Coincident(g2,g3)
    c: Coincident(g3,g0)
    c: Vertical(g0)
    c: Vertical(g2)
    c: Horizontal(g1)
    c: Horizontal(g3)
    c: Symmetric(g2,g0,g4)
    c: Coincident(g4,g-3)
    c: Coincident(g1,g-5)
    c: Coincident(g5,g6)
    c: Coincident(g6,g7)
    c: Coincident(g7,g8)
    c: Coincident(g8,g5)
    c: Horizontal(g5)
    c: Horizontal(g7)
    c: Vertical(g6)
    c: Vertical(g8)
    c: Symmetric(g7,g5,g9)
    c: Coincident(g9,g-4)
    c: Coincident(g6,g-5)
FEATURE [PartDesign::Pocket] Pocket038
  BaseFeature = -> Pad032
  Direction = (0,1,0)
  Length = 18
  Length2 = 5
  Placement = pos=(42,-119,14) rot=(0.57735,-0.57735,0.57735;2.0944rad)
  Profile = -> Sketch074
  ReferenceAxis = -> Sketch074 [N_Axis]
  Refine = true
  Suppressed = false
  Type = 0
FEATURE [PartDesign::Body] Body011  label="28BYJ-48 Stepper Motor"
  AllowCompound = false
  Group = -> [DatumPlane012,CopyChamfer017,Sketch069,Pad028,Sketch070,Pad029,Sketch071,Pad030,Sketch072,Pad031,Sketch073,Pad032,Sketch074,Pocket038]
  Origin = -> Origin011
  Placement = pos=(-93,0,0) rot=(0,0,1;0rad)
  Tip = -> Pocket038
FEATURE [Sketcher::SketchObject] Sketch075
  ArcFitTolerance = 1e-06
  AttachmentSupport = -> [Pad026]
  ExternalGeometry = -> [Pad026]
  FullyConstrained = true
  MakeInternals = false
  MapMode = 5
  Placement = pos=(0,-122,0) rot=(1,0,0;1.5708rad)
  sketch-geometry (14):
    g0: GeomPoint X=42 Y=5 Z=0
    g1: LineSegment [constr] StartX=42 StartY=5 StartZ=0 EndX=24.5 EndY=5 EndZ=0
    g2: LineSegment [constr] StartX=42 StartY=5 StartZ=0 EndX=59.5 EndY=5 EndZ=0
    g3: LineSegment [constr] StartX=24.5 StartY=5 StartZ=0 EndX=24.5 EndY=6 EndZ=0
    g4: LineSegment [constr] StartX=59.5 StartY=5 StartZ=0 EndX=59.5 EndY=6 EndZ=0
    g5: Circle CenterX=24.5 CenterY=6 CenterZ=0 NormalX=0 NormalY=0 NormalZ=1 AngleXU=0 Radius=1.7
    g6: Circle CenterX=59.5 CenterY=6 CenterZ=0 NormalX=0 NormalY=0 NormalZ=1 AngleXU=0 Radius=1.7
    g7: GeomPoint [constr] X=42 Y=5 Z=0
    g8: Circle CenterX=24.5 CenterY=6 CenterZ=0 NormalX=0 NormalY=0 NormalZ=1 AngleXU=0 Radius=3.64975
    g9: Circle CenterX=59.5 CenterY=6 CenterZ=0 NormalX=0 NormalY=0 NormalZ=1 AngleXU=0 Radius=3.64975
    g10: GeomPoint X=20.9899 Y=5 Z=0
    g11: GeomPoint X=28.0101 Y=5 Z=0
    g12: GeomPoint X=55.9899 Y=5 Z=0
    g13: GeomPoint X=63.0101 Y=5 Z=0
  constraints (30):
    c: Symmetric(g-3,g-3,g0)
    c: Distance(g1) = 17.5
    c: Coincident(g1,g0)
    c: PointOnObject(g1,g-3)
    c: Coincident(g2,g0)
    c: PointOnObject(g2,g-3)
    c: Equal(g1,g2)
    c: Distance(g3) = 1
    c: Coincident(g3,g1)
    c: Vertical(g3)
    c: Coincident(g4,g2)
    c: Vertical(g4)
    c: Equal(g3,g4)
    c: Diameter(g5) = 3.4
    c: Coincident(g5,g3)
    c: Coincident(g6,g4)
    c: Equal(g6,g5)
    c: Coincident(g7,g0)
    c: Coincident(g8,g3)
    c: Tangent(g8,g-5)
    c: Coincident(g9,g4)
    c: Tangent(g9,g-4)
    c: PointOnObject(g10,g8)
    c: PointOnObject(g11,g8)
    c: PointOnObject(g12,g2)
    c: PointOnObject(g13,g-3)
    c: PointOnObject(g13,g9)
    c: PointOnObject(g12,g9)
    c: PointOnObject(g10,g-3)
    c: PointOnObject(g11,g1)
FEATURE [PartDesign::Pad] Pad033
  BaseFeature = -> Pad026
  Direction = (0,-1,2e-16)
  Length = 11
  Length2 = 10
  Profile = -> Sketch075
  ReferenceAxis = -> Sketch075 [N_Axis]
  Refine = true
  Reversed = true
  Suppressed = false
  Type = 0
FEATURE [Sketcher::SketchObject] Sketch076
  ArcFitTolerance = 1e-06
  AttachmentSupport = -> [Pad033]
  ExternalGeometry = -> [Pad033]
  FullyConstrained = true
  MakeInternals = false
  MapMode = 5
  Placement = pos=(0,-122,9.27e-14) rot=(1,0,0;1.5708rad)
  sketch-geometry (2):
    g0: Circle CenterX=24.5 CenterY=6 CenterZ=0 NormalX=0 NormalY=0 NormalZ=1 AngleXU=0 Radius=1.7
    g1: Circle CenterX=59.5 CenterY=6 CenterZ=0 NormalX=0 NormalY=0 NormalZ=1 AngleXU=0 Radius=1.7
  constraints (4):
    c: Coincident(g0,g-3)
    c: Equal(g0,g-3)
    c: Coincident(g1,g-4)
    c: Equal(g1,g-4)
FEATURE [PartDesign::Pocket] Pocket039
  BaseFeature = -> Pad033
  Direction = (0,1,-2e-16)
  Length = 0
  Length2 = 5
  Profile = -> Sketch076
  ReferenceAxis = -> Sketch076 [N_Axis]
  Refine = true
  Suppressed = false
  Type = 3
  UpToFace = -> Pad033 [Face25]
FEATURE [PartDesign::ShapeBinder] CopyPocket039
  TraceSupport = false
FEATURE [PartDesign::Plane] DatumPlane013
  AttachmentSupport = -> [CopyPocket039]
  Length = 134.316
  MapMode = 5
  Placement = pos=(0,1.2e-15,-1.25) rot=(1,0,0;3.14159rad)
  ResizeMode = 0
  Width = 172.316
FEATURE [Sketcher::SketchObject] Sketch077
  ArcFitTolerance = 1e-06
  AttachmentSupport = -> [DatumPlane013]
  ExternalGeometry = -> [CopyPocket039]
  FullyConstrained = true
  MakeInternals = false
  MapMode = 5
  Placement = pos=(0,1.2e-15,-1.25) rot=(1,0,0;3.14159rad)
  sketch-geometry (15):
    g0: Circle CenterX=5 CenterY=79 CenterZ=0 NormalX=0 NormalY=0 NormalZ=1 AngleXU=0 Radius=1.3
    g1: Circle CenterX=79 CenterY=79 CenterZ=0 NormalX=0 NormalY=0 NormalZ=1 AngleXU=0 Radius=1.3
    g2: Circle CenterX=79 CenterY=5 CenterZ=0 NormalX=0 NormalY=0 NormalZ=1 AngleXU=0 Radius=1.3
    g3: Circle CenterX=5 CenterY=5 CenterZ=0 NormalX=0 NormalY=0 NormalZ=1 AngleXU=0 Radius=1.3
    g4: LineSegment StartX=0 StartY=122 StartZ=0 EndX=0 EndY=0 EndZ=0
    g5: LineSegment StartX=0 StartY=0 StartZ=0 EndX=84 EndY=1.2e-15 EndZ=0
    g6: LineSegment StartX=84 StartY=1.2e-15 StartZ=0 EndX=84 EndY=122 EndZ=0
    g7: LineSegment StartX=84 StartY=122 StartZ=0 EndX=74 EndY=122 EndZ=0
    g8: LineSegment StartX=0 StartY=122 StartZ=0 EndX=10 EndY=122 EndZ=0
    g9: LineSegment [constr] StartX=42 StartY=4e-16 StartZ=0 EndX=42 EndY=10 EndZ=0
    g10: LineSegment [constr] StartX=42 StartY=10 StartZ=0 EndX=0 EndY=10 EndZ=0
    g11: LineSegment [constr] StartX=42 StartY=10 StartZ=0 EndX=84 EndY=10 EndZ=0
    g12: LineSegment StartX=10 StartY=122 StartZ=0 EndX=10 EndY=10 EndZ=0
    g13: LineSegment StartX=74 StartY=122 StartZ=0 EndX=74 EndY=10 EndZ=0
    g14: LineSegment StartX=74 StartY=10 StartZ=0 EndX=10 EndY=10 EndZ=0
  constraints (37):
    c: Coincident(g0,g-5)
    c: Coincident(g1,g-6)
    c: Coincident(g2,g-4)
    c: Coincident(g3,g-3)
    c: Diameter(g3) = 2.6
    c: Equal(g2,g1)
    c: Equal(g1,g0)
    c: Equal(g0,g3)
    c: Coincident(g4,g-10)
    c: Coincident(g4,g-1)
    c: Coincident(g5,g4)
    c: Coincident(g5,g-9)
    c: Coincident(g6,g5)
    c: Coincident(g6,g-10)
    c: Distance(g7) = 10
    c: Coincident(g7,g6)
    c: PointOnObject(g7,g-10)
    c: Distance(g8) = 10
    c: Coincident(g8,g4)
    c: PointOnObject(g8,g-10)
    c: Distance(g9) = 10
    c: Symmetric(g5,g5,g9)
    c: Vertical(g9)
    c: Coincident(g10,g9)
    c: PointOnObject(g10,g4)
    c: Horizontal(g10)
    c: Coincident(g11,g9)
    c: PointOnObject(g11,g6)
    c: Horizontal(g11)
    c: Coincident(g12,g8)
    c: PointOnObject(g12,g10)
    c: Vertical(g12)
    c: Coincident(g13,g7)
    c: PointOnObject(g13,g11)
    c: Vertical(g13)
    c: Coincident(g14,g13)
    c: Coincident(g14,g12)
FEATURE [PartDesign::Pad] Pad034
  Direction = (0,0,-1)
  Length = 30
  Length2 = 10
  Placement = pos=(0,1.2e-15,-1.25) rot=(1,0,0;3.14159rad)
  Profile = -> Sketch077
  ReferenceAxis = -> Sketch077 [N_Axis]
  Refine = true
  Suppressed = false
  Type = 0
FEATURE [Sketcher::SketchObject] Sketch078
  ArcFitTolerance = 1e-06
  AttachmentSupport = -> [Pad034]
  ExternalGeometry = -> [Pad034,CopyPocket039]
  FullyConstrained = true
  MakeInternals = false
  MapMode = 5
  Placement = pos=(0,1.2e-15,-1.25) rot=(0.57735,0.57735,-0.57735;4.18879rad)
  sketch-geometry (11):
    g0: LineSegment [constr] StartX=-122 StartY=30 StartZ=0 EndX=-122 EndY=25 EndZ=0
    g1: LineSegment [constr] StartX=-122 StartY=25 StartZ=0 EndX=-117 EndY=25 EndZ=0
    g2: Circle CenterX=-117 CenterY=25 CenterZ=0 NormalX=0 NormalY=0 NormalZ=1 AngleXU=0 Radius=1.3
    g3: LineSegment [constr] StartX=-117 StartY=25 StartZ=0 EndX=-117 EndY=20 EndZ=0
    g4: LineSegment [constr] StartX=-117 StartY=20 StartZ=0 EndX=-117 EndY=15 EndZ=0
    g5: LineSegment [constr] StartX=-117 StartY=15 StartZ=0 EndX=-117 EndY=10 EndZ=0
    g6: LineSegment [constr] StartX=-117 StartY=10 StartZ=0 EndX=-117 EndY=5 EndZ=0
    g7: Circle CenterX=-117 CenterY=20 CenterZ=0 NormalX=0 NormalY=0 NormalZ=1 AngleXU=0 Radius=1.3
    g8: Circle CenterX=-117 CenterY=15 CenterZ=0 NormalX=0 NormalY=0 NormalZ=1 AngleXU=0 Radius=1.3
    g9: Circle CenterX=-117 CenterY=10 CenterZ=0 NormalX=0 NormalY=0 NormalZ=1 AngleXU=0 Radius=1.3
    g10: Circle CenterX=-117 CenterY=5 CenterZ=0 NormalX=0 NormalY=0 NormalZ=1 AngleXU=0 Radius=1.3
  constraints (28):
    c: Distance(g0) = 5
    c: Coincident(g0,g-4)
    c: PointOnObject(g0,g-4)
    c: Distance(g1) = 5
    c: Coincident(g1,g0)
    c: Horizontal(g1)
    c: Diameter(g2) = 2.6
    c: Coincident(g2,g1)
    c: Distance(g3) = 5
    c: Coincident(g3,g1)
    c: Vertical(g3)
    c: Distance(g4) = 5
    c: Coincident(g4,g3)
    c: Vertical(g4)
    c: Distance(g5) = 5
    c: Coincident(g5,g4)
    c: Vertical(g5)
    c: Distance(g6) = 5
    c: Coincident(g6,g5)
    c: Vertical(g6)
    c: Coincident(g7,g3)
    c: Coincident(g8,g4)
    c: Coincident(g9,g5)
    c: Coincident(g10,g6)
    c: Equal(g7,g8)
    c: Equal(g8,g9)
    c: Equal(g9,g10)
    c: Equal(g10,g2)
FEATURE [PartDesign::Pocket] Pocket040
  BaseFeature = -> Pad034
  Direction = (1,0,0)
  Length = 5
  Length2 = 5
  Placement = pos=(0,1.2e-15,-1.25) rot=(1,0,0;3.14159rad)
  Profile = -> Sketch078
  ReferenceAxis = -> Sketch078 [N_Axis]
  Refine = true
  Suppressed = false
  Type = 1
FEATURE [PartDesign::LinearPattern] LinearPattern
  BaseFeature = -> Pocket040
  Direction = -> Sketch078 [H_Axis]
  Length = 95
  Mode = 0
  Occurrences = 20
  Offset = 5
  Originals = -> [Pocket040]
  Placement = pos=(0,1.2e-15,-1.25) rot=(1,0,0;3.14159rad)
  Refine = true
  Suppressed = false
  TransformMode = 0
FEATURE [Sketcher::SketchObject] Sketch079
  ArcFitTolerance = 1e-06
  AttachmentSupport = -> [LinearPattern]
  ExternalGeometry = -> [LinearPattern]
  FullyConstrained = true
  MakeInternals = false
  MapMode = 5
  Placement = pos=(0,1e-15,-1.25) rot=(-1,0,0;1.5708rad)
  sketch-geometry (14):
    g0: LineSegment [constr] StartX=0 StartY=30 StartZ=0 EndX=0 EndY=25 EndZ=0
    g1: LineSegment [constr] StartX=0 StartY=25 StartZ=0 EndX=42 EndY=25 EndZ=0
    g2: LineSegment [constr] StartX=42 StartY=25 StartZ=0 EndX=42 EndY=30 EndZ=0
    g3: LineSegment [constr] StartX=42 StartY=30 StartZ=0 EndX=0 EndY=30 EndZ=0
    g4: Circle CenterX=42 CenterY=25 CenterZ=0 NormalX=0 NormalY=0 NormalZ=1 AngleXU=0 Radius=1.3
    g5: LineSegment [constr] StartX=42 StartY=25 StartZ=0 EndX=42 EndY=20 EndZ=0
    g6: LineSegment [constr] StartX=42 StartY=20 StartZ=0 EndX=42 EndY=15 EndZ=0
    g7: LineSegment [constr] StartX=42 StartY=15 StartZ=0 EndX=42 EndY=10 EndZ=0
    g8: LineSegment [constr] StartX=42 StartY=10 StartZ=0 EndX=42 EndY=5 EndZ=0
    g9: Circle CenterX=42 CenterY=20 CenterZ=0 NormalX=0 NormalY=0 NormalZ=1 AngleXU=0 Radius=1.3
    g10: Circle CenterX=42 CenterY=15 CenterZ=0 NormalX=0 NormalY=0 NormalZ=1 AngleXU=0 Radius=1.3
    g11: Circle CenterX=42 CenterY=10 CenterZ=0 NormalX=0 NormalY=0 NormalZ=1 AngleXU=0 Radius=1.3
    g12: Circle CenterX=42 CenterY=5 CenterZ=0 NormalX=0 NormalY=0 NormalZ=1 AngleXU=0 Radius=1.3
    g13: GeomPoint X=42 Y=30 Z=0
  constraints (33):
    c: Coincident(g0,g1)
    c: Coincident(g1,g2)
    c: Coincident(g2,g3)
    c: Coincident(g3,g0)
    c: Vertical(g0)
    c: Vertical(g2)
    c: Horizontal(g1)
    c: Distance(g1,g3) = 5
    c: Coincident(g0,g-4)
    c: Coincident(g4,g1)
    c: Diameter(g4) = 2.6
    c: Distance(g5) = 5
    c: Coincident(g5,g1)
    c: Vertical(g5)
    c: Distance(g6) = 5
    c: Coincident(g6,g5)
    c: Vertical(g6)
    c: Distance(g7) = 5
    c: Coincident(g7,g6)
    c: Parallel(g7,g6)
    c: Distance(g8) = 5
    c: Coincident(g8,g7)
    c: Vertical(g8)
    c: Coincident(g9,g5)
    c: Coincident(g10,g6)
    c: Coincident(g11,g7)
    c: Coincident(g12,g8)
    c: Equal(g11,g12)
    c: Equal(g12,g10)
    c: Equal(g10,g9)
    c: Equal(g9,g4)
    c: Symmetric(g-3,g-3,g13)
    c: Coincident(g2,g13)
FEATURE [PartDesign::Pocket] Pocket041
  BaseFeature = -> LinearPattern
  Direction = (0,-1,-2e-16)
  Length = 5
  Length2 = 5
  Placement = pos=(0,1.2e-15,-1.25) rot=(1,0,0;3.14159rad)
  Profile = -> Sketch079
  ReferenceAxis = -> Sketch079 [N_Axis]
  Refine = true
  Suppressed = false
  Type = 1
FEATURE [PartDesign::LinearPattern] LinearPattern001
  BaseFeature = -> Pocket041
  Direction = -> Sketch079 [H_Axis]
  Length = 30
  Mode = 0
  Occurrences = 7
  Offset = 5
  Originals = -> [Pocket041]
  Placement = pos=(0,1.2e-15,-1.25) rot=(1,0,0;3.14159rad)
  Refine = true
  Suppressed = false
  TransformMode = 0
FEATURE [PartDesign::LinearPattern] LinearPattern002
  BaseFeature = -> LinearPattern001
  Direction = -> Sketch079 [H_Axis]
  Length = 30
  Mode = 0
  Occurrences = 7
  Offset = 5
  Originals = -> [Pocket041]
  Placement = pos=(0,1.2e-15,-1.25) rot=(1,0,0;3.14159rad)
  Refine = true
  Reversed = true
  Suppressed = false
  TransformMode = 0
FEATURE [PartDesign::Chamfer] Chamfer018
  Angle = 45
  Base = -> LinearPattern002 [Edge4,Edge128]
  BaseFeature = -> LinearPattern002
  ChamferType = 0
  FlipDirection = false
  Placement = pos=(0,1.2e-15,-1.25) rot=(1,0,0;3.14159rad)
  Refine = true
  Size = 5
  Size2 = 1
  SupportTransform = false
  Suppressed = false
  UseAllEdges = false
FEATURE [PartDesign::Chamfer] Chamfer019
  Angle = 45
  Base = -> Chamfer018 [Edge472,Edge573,Edge120,Edge3]
  BaseFeature = -> Chamfer018
  ChamferType = 0
  FlipDirection = false
  Placement = pos=(0,1.2e-15,-1.25) rot=(1,0,0;3.14159rad)
  Refine = true
  Size = 3
  Size2 = 1
  SupportTransform = false
  Suppressed = false
  UseAllEdges = false
FEATURE [PartDesign::Body] Body012  label="Motorised Stage Base"
  AllowCompound = false
  Group = -> [DatumPlane013,CopyPocket039,Sketch077,Pad034,Sketch078,Pocket040,LinearPattern,Sketch079,Pocket041,LinearPattern001,LinearPattern002,Chamfer018,Chamfer019]
  Origin = -> Origin012
  Tip = -> Chamfer019
FEATURE [PartDesign::ShapeBinder] CopyChamfer019
  Placement = pos=(0,1.2e-15,-1.25) rot=(1,0,0;3.14159rad)
  TraceSupport = false
FEATURE [PartDesign::Plane] DatumPlane014
  AttachmentSupport = -> [CopyChamfer019]
  Length = 84.7279
  MapMode = 5
  Placement = pos=(84,1.2e-15,-1.25) rot=(0.57735,-0.57735,0.57735;4.18879rad)
  ResizeMode = 0
  Width = 68.9779
FEATURE [Sketcher::SketchObject] Sketch080
  ArcFitTolerance = 1e-06
  AttachmentSupport = -> [DatumPlane014]
  ExternalGeometry = -> [CopyChamfer019]
  FullyConstrained = true
  MakeInternals = false
  MapMode = 5
  Placement = pos=(84,1.2e-15,-1.25) rot=(0.57735,-0.57735,0.57735;4.18879rad)
  sketch-geometry (10):
    g0: LineSegment [constr] StartX=22 StartY=25 StartZ=0 EndX=22 EndY=30 EndZ=0
    g1: LineSegment [constr] StartX=42 StartY=25 StartZ=0 EndX=42 EndY=30 EndZ=0
    g2: LineSegment [constr] StartX=42 StartY=30 StartZ=0 EndX=47 EndY=30 EndZ=0
    g3: LineSegment [constr] StartX=22 StartY=30 StartZ=0 EndX=17 EndY=30 EndZ=0
    g4: LineSegment StartX=17 StartY=30 StartZ=0 EndX=17 EndY=22.5 EndZ=0
    g5: LineSegment StartX=17 StartY=22.5 StartZ=0 EndX=47 EndY=22.5 EndZ=0
    g6: LineSegment StartX=47 StartY=22.5 StartZ=0 EndX=47 EndY=30 EndZ=0
    g7: LineSegment StartX=47 StartY=30 StartZ=0 EndX=17 EndY=30 EndZ=0
    g8: Circle CenterX=22 CenterY=25 CenterZ=0 NormalX=0 NormalY=0 NormalZ=1 AngleXU=0 Radius=1.5
    g9: Circle CenterX=42 CenterY=25 CenterZ=0 NormalX=0 NormalY=0 NormalZ=1 AngleXU=0 Radius=1.5
  constraints (26):
    c: Coincident(g0,g-3)
    c: PointOnObject(g0,g-5)
    c: Vertical(g0)
    c: Coincident(g1,g-4)
    c: PointOnObject(g1,g-5)
    c: Vertical(g1)
    c: Distance(g2) = 5
    c: Coincident(g2,g1)
    c: PointOnObject(g2,g-5)
    c: Distance(g3) = 5
    c: Coincident(g3,g0)
    c: PointOnObject(g3,g-5)
    c: Distance(g4) = 7.5
    c: Vertical(g4)
    c: Coincident(g4,g3)
    c: Coincident(g4,g5)
    c: Horizontal(g5)
    c: Coincident(g5,g6)
    c: Coincident(g6,g2)
    c: Vertical(g6)
    c: Coincident(g6,g7)
    c: Coincident(g7,g3)
    c: Diameter(g8) = 3
    c: Coincident(g8,g0)
    c: Diameter(g9) = 3
    c: Coincident(g9,g1)
FEATURE [PartDesign::Pad] Pad035
  Direction = (1,0,0)
  Length = 3
  Length2 = 10
  Placement = pos=(84,1.2e-15,-1.25) rot=(0.57735,-0.57735,0.57735;4.18879rad)
  Profile = -> Sketch080
  ReferenceAxis = -> Sketch080 [N_Axis]
  Refine = true
  Suppressed = false
  Type = 0
FEATURE [Sketcher::SketchObject] Sketch081
  ArcFitTolerance = 1e-06
  AttachmentSupport = -> [Pad035]
  ExternalGeometry = -> [Pad035]
  FullyConstrained = true
  MakeInternals = false
  MapMode = 5
  Placement = pos=(87,1.2e-15,-1.25) rot=(0.57735,-0.57735,0.57735;4.18879rad)
  sketch-geometry (8):
    g0: ArcOfCircle CenterX=22 CenterY=25 CenterZ=0 NormalX=0 NormalY=0 NormalZ=1 AngleXU=0 Radius=3 StartAngle=5.29807 EndAngle=10.4099
    g1: ArcOfCircle CenterX=42 CenterY=25 CenterZ=0 NormalX=0 NormalY=0 NormalZ=1 AngleXU=0 Radius=3 StartAngle=5.29807 EndAngle=10.4099
    g2: LineSegment StartX=47 StartY=22.5 StartZ=0 EndX=43.6583 EndY=22.5 EndZ=0
    g3: LineSegment StartX=40.3417 StartY=22.5 StartZ=0 EndX=23.6583 EndY=22.5 EndZ=0
    g4: LineSegment StartX=20.3417 StartY=22.5 StartZ=0 EndX=17 EndY=22.5 EndZ=0
    g5: LineSegment StartX=17 StartY=22.5 StartZ=0 EndX=17 EndY=30 EndZ=0
    g6: LineSegment StartX=17 StartY=30 StartZ=0 EndX=47 EndY=30 EndZ=0
    g7: LineSegment StartX=47 StartY=30 StartZ=0 EndX=47 EndY=22.5 EndZ=0
  constraints (22):
    c: Diameter(g0) = 6
    c: Coincident(g0,g-3)
    c: Diameter(g1) = 6
    c: Coincident(g1,g-4)
    c: Coincident(g2,g-6)
    c: Coincident(g4,g-7)
    c: PointOnObject(g0,g4)
    c: PointOnObject(g1,g3)
    c: Coincident(g2,g1)
    c: PointOnObject(g3,g1)
    c: Coincident(g3,g0)
    c: PointOnObject(g4,g0)
    c: Horizontal(g0,g1)
    c: PointOnObject(g1,g-6)
    c: PointOnObject(g0,g-6)
    c: PointOnObject(g1,g-6)
    c: Coincident(g5,g4)
    c: Coincident(g5,g-8)
    c: Coincident(g6,g5)
    c: Coincident(g6,g-8)
    c: Coincident(g7,g6)
    c: Coincident(g7,g2)
FEATURE [PartDesign::Pad] Pad036
  BaseFeature = -> Pad035
  Direction = (1,0,0)
  Length = 4
  Length2 = 10
  Placement = pos=(84,1.2e-15,-1.25) rot=(0.57735,-0.57735,0.57735;4.18879rad)
  Profile = -> Sketch081
  ReferenceAxis = -> Sketch081 [N_Axis]
  Refine = true
  Suppressed = false
  Type = 0
FEATURE [Sketcher::SketchObject] Sketch082
  ArcFitTolerance = 1e-06
  AttachmentSupport = -> [Pad036]
  ExternalGeometry = -> [Pad036]
  FullyConstrained = true
  MakeInternals = false
  MapMode = 5
  Placement = pos=(91,1.2e-15,-1.25) rot=(0.57735,-0.57735,0.57735;4.18879rad)
  sketch-geometry (10):
    g0: GeomPoint [constr] X=17 Y=26.25 Z=0
    g1: LineSegment [constr] StartX=17 StartY=26.25 StartZ=0 EndX=47 EndY=26.25 EndZ=0
    g2: ArcOfCircle CenterX=22 CenterY=25 CenterZ=0 NormalX=0 NormalY=0 NormalZ=1 AngleXU=0 Radius=3 StartAngle=0.429775 EndAngle=2.71182
    g3: ArcOfCircle CenterX=42 CenterY=25 CenterZ=0 NormalX=0 NormalY=0 NormalZ=1 AngleXU=0 Radius=3 StartAngle=0.429775 EndAngle=2.71182
    g4: LineSegment StartX=17 StartY=26.25 StartZ=0 EndX=19.2728 EndY=26.25 EndZ=0
    g5: LineSegment StartX=17 StartY=26.25 StartZ=0 EndX=17 EndY=30 EndZ=0
    g6: LineSegment StartX=17 StartY=30 StartZ=0 EndX=47 EndY=30 EndZ=0
    g7: LineSegment StartX=47 StartY=30 StartZ=0 EndX=47 EndY=26.25 EndZ=0
    g8: LineSegment StartX=44.7272 StartY=26.25 StartZ=0 EndX=47 EndY=26.25 EndZ=0
    g9: LineSegment StartX=24.7272 StartY=26.25 StartZ=0 EndX=39.2728 EndY=26.25 EndZ=0
  constraints (23):
    c: Symmetric(g-3,g-3,g0)
    c: Coincident(g1,g0)
    c: Symmetric(g-5,g-5,g1)
    c: Coincident(g2,g-6)
    c: Equal(g2,g-6)
    c: Coincident(g3,g-7)
    c: Equal(g3,g-7)
    c: Coincident(g4,g0)
    c: Coincident(g8,g1)
    c: Coincident(g5,g0)
    c: Coincident(g5,g-4)
    c: Coincident(g6,g5)
    c: Coincident(g6,g-5)
    c: Coincident(g7,g6)
    c: Coincident(g7,g1)
    c: PointOnObject(g3,g1)
    c: PointOnObject(g3,g1)
    c: PointOnObject(g2,g1)
    c: PointOnObject(g2,g1)
    c: Coincident(g9,g3)
    c: Coincident(g9,g2)
    c: Coincident(g4,g2)
    c: Coincident(g8,g3)
FEATURE [PartDesign::Pad] Pad037
  BaseFeature = -> Pad036
  Direction = (1,0,0)
  Length = 10
  Length2 = 10
  Placement = pos=(84,1.2e-15,-1.25) rot=(0.57735,-0.57735,0.57735;4.18879rad)
  Profile = -> Sketch082
  ReferenceAxis = -> Sketch082 [N_Axis]
  Refine = true
  Suppressed = false
  Type = 0
FEATURE [Sketcher::SketchObject] Sketch083
  ArcFitTolerance = 1e-06
  AttachmentSupport = -> [Pad037]
  ExternalGeometry = -> [Pad037]
  FullyConstrained = true
  MakeInternals = false
  MapMode = 5
  Placement = pos=(84,-5.1e-15,-27.5) rot=(0,0,-1;1.5708rad)
  sketch-geometry (7):
    g0: LineSegment [constr] StartX=17 StartY=17 StartZ=0 EndX=17 EndY=12 EndZ=0
    g1: LineSegment [constr] StartX=17 StartY=12 StartZ=0 EndX=47 EndY=12 EndZ=0
    g2: GeomPoint [constr] X=32 Y=12 Z=0
    g3: LineSegment [constr] StartX=32 StartY=12 StartZ=0 EndX=42 EndY=12 EndZ=0
    g4: LineSegment [constr] StartX=32 StartY=12 StartZ=0 EndX=22 EndY=12 EndZ=0
    g5: Circle CenterX=22 CenterY=12 CenterZ=0 NormalX=0 NormalY=0 NormalZ=1 AngleXU=0 Radius=3
    g6: Circle CenterX=42 CenterY=12 CenterZ=0 NormalX=0 NormalY=0 NormalZ=1 AngleXU=0 Radius=3
  constraints (15):
    c: Coincident(g0,g-5)
    c: Symmetric(g-5,g-5,g0)
    c: Coincident(g1,g0)
    c: Symmetric(g-7,g-7,g1)
    c: Symmetric(g1,g1,g2)
    c: Distance(g3) = 10
    c: Coincident(g3,g2)
    c: PointOnObject(g3,g1)
    c: Distance(g4) = 10
    c: Coincident(g4,g2)
    c: PointOnObject(g4,g1)
    c: Diameter(g5) = 6
    c: Coincident(g5,g4)
    c: Diameter(g6) = 6
    c: Coincident(g6,g3)
FEATURE [PartDesign::Pocket] Pocket042
  BaseFeature = -> Pad037
  Direction = (0,0,-1)
  Length = 2
  Length2 = 5
  Placement = pos=(84,1.2e-15,-1.25) rot=(0.57735,-0.57735,0.57735;4.18879rad)
  Profile = -> Sketch083
  ReferenceAxis = -> Sketch083 [N_Axis]
  Refine = true
  Suppressed = false
  Type = 0
FEATURE [Sketcher::SketchObject] Sketch084
  ArcFitTolerance = 1e-06
  AttachmentSupport = -> [Pocket042]
  ExternalGeometry = -> [Pocket042]
  FullyConstrained = true
  MakeInternals = false
  MapMode = 5
  Placement = pos=(84,1.2e-15,-29.5) rot=(0,0,-1;1.5708rad)
  sketch-geometry (2):
    g0: Circle CenterX=22 CenterY=12 CenterZ=0 NormalX=0 NormalY=0 NormalZ=1 AngleXU=0 Radius=1.5
    g1: Circle CenterX=42 CenterY=12 CenterZ=0 NormalX=0 NormalY=0 NormalZ=1 AngleXU=0 Radius=1.5
  constraints (4):
    c: Diameter(g0) = 3
    c: Coincident(g0,g-3)
    c: Diameter(g1) = 3
    c: Coincident(g1,g-4)
FEATURE [PartDesign::Pocket] Pocket043
  BaseFeature = -> Pocket042
  Direction = (0,0,-1)
  Length = 4
  Length2 = 5
  Placement = pos=(84,1.2e-15,-1.25) rot=(0.57735,-0.57735,0.57735;4.18879rad)
  Profile = -> Sketch084
  ReferenceAxis = -> Sketch084 [N_Axis]
  Refine = true
  Suppressed = false
  Type = 0
FEATURE [PartDesign::Chamfer] Chamfer020
  Angle = 45
  Base = -> Pocket043 [Edge10,Edge23]
  BaseFeature = -> Pocket043
  ChamferType = 0
  FlipDirection = false
  Placement = pos=(84,1.2e-15,-1.25) rot=(0.57735,-0.57735,0.57735;4.18879rad)
  Refine = true
  Size = 5
  Size2 = 1
  SupportTransform = false
  Suppressed = false
  UseAllEdges = false
FEATURE [Sketcher::SketchObject] Sketch085
  ArcFitTolerance = 1e-06
  AttachmentSupport = -> [Chamfer020]
  ExternalGeometry = -> [Chamfer020]
  FullyConstrained = true
  MakeInternals = false
  MapMode = 5
  Placement = pos=(84,-5.1e-15,-27.5) rot=(0,0,-1;1.5708rad)
  sketch-geometry (3):
    g0: GeomPoint X=32 Y=17 Z=0
    g1: LineSegment [constr] StartX=32 StartY=17 StartZ=0 EndX=32 EndY=12 EndZ=0
    g2: Circle CenterX=32 CenterY=12 CenterZ=0 NormalX=0 NormalY=0 NormalZ=1 AngleXU=0 Radius=1.5
  constraints (6):
    c: Symmetric(g-3,g-3,g0)
    c: Distance(g1) = 5
    c: Coincident(g1,g0)
    c: Perpendicular(g-3,g1)
    c: Diameter(g2) = 3
    c: Coincident(g2,g1)
FEATURE [PartDesign::Pocket] Pocket044
  BaseFeature = -> Chamfer020
  Direction = (0,0,-1)
  Length = 5
  Length2 = 5
  Placement = pos=(84,1.2e-15,-1.25) rot=(0.57735,-0.57735,0.57735;4.18879rad)
  Profile = -> Sketch085
  ReferenceAxis = -> Sketch085 [N_Axis]
  Refine = true
  Suppressed = false
  Type = 0
FEATURE [PartDesign::Chamfer] Chamfer021
  Angle = 45
  Base = -> Pocket044 [Edge30,Edge26,Edge16]
  BaseFeature = -> Pocket044
  ChamferType = 0
  FlipDirection = false
  Placement = pos=(84,1.2e-15,-1.25) rot=(0.57735,-0.57735,0.57735;4.18879rad)
  Refine = true
  Size = 3.74
  Size2 = 1
  SupportTransform = false
  Suppressed = false
  UseAllEdges = false
FEATURE [PartDesign::Chamfer] Chamfer022
  Angle = 45
  Base = -> Chamfer021 [Edge70]
  BaseFeature = -> Chamfer021
  ChamferType = 0
  FlipDirection = false
  Placement = pos=(84,1.2e-15,-1.25) rot=(0.57735,-0.57735,0.57735;4.18879rad)
  Refine = true
  Size = 2
  Size2 = 1
  SupportTransform = false
  Suppressed = false
  UseAllEdges = false
FEATURE [PartDesign::Body] Body013  label="5mm grid boltdown"
  AllowCompound = false
  Group = -> [DatumPlane014,CopyChamfer019,Sketch080,Pad035,Sketch081,Pad036,Sketch082,Pad037,Sketch083,Pocket042,Sketch084,Pocket043,Chamfer020,Sketch085,Pocket044,Chamfer021,Chamfer022]
  Origin = -> Origin013
  Tip = -> Chamfer022
FEATURE [Sketcher::SketchObject] Sketch086
  ArcFitTolerance = 1e-06
  AttachmentSupport = -> [Pocket025]
  ExternalGeometry = -> [Pocket025]
  FullyConstrained = true
  MakeInternals = false
  MapMode = 5
  Placement = pos=(84,-84,-1.80021e-08) rot=(0.707107,0,0.707107;3.14159rad)
  sketch-geometry (7):
    g0: LineSegment [constr] StartX=27.3536 StartY=-1.42e-14 StartZ=0 EndX=27.3536 EndY=-5 EndZ=0
    g1: LineSegment [constr] StartX=27.3536 StartY=-5 StartZ=0 EndX=22.3536 EndY=-5 EndZ=0
    g2: LineSegment [constr] StartX=22.3536 StartY=-5 StartZ=0 EndX=17.3536 EndY=-5 EndZ=0
    g3: LineSegment [constr] StartX=17.3536 StartY=-5 StartZ=0 EndX=12.3536 EndY=-5 EndZ=0
    g4: Circle CenterX=12.3536 CenterY=-5 CenterZ=0 NormalX=0 NormalY=0 NormalZ=1 AngleXU=0 Radius=1.3
    g5: Circle CenterX=17.3536 CenterY=-5 CenterZ=0 NormalX=0 NormalY=0 NormalZ=1 AngleXU=0 Radius=1.3
    g6: Circle CenterX=22.3536 CenterY=-5 CenterZ=0 NormalX=0 NormalY=0 NormalZ=1 AngleXU=0 Radius=1.3
  constraints (18):
    c: Distance(g0) = 5
    c: PointOnObject(g0,g-4)
    c: Coincident(g0,g-5)
    c: Distance(g1) = 5
    c: Horizontal(g1)
    c: Coincident(g1,g0)
    c: Distance(g2) = 5
    c: Coincident(g2,g1)
    c: Horizontal(g2)
    c: Distance(g3) = 5
    c: Coincident(g3,g2)
    c: Horizontal(g3)
    c: Diameter(g4) = 2.6
    c: Coincident(g4,g3)
    c: Diameter(g5) = 2.6
    c: Coincident(g5,g2)
    c: Diameter(g6) = 2.6
    c: Coincident(g6,g1)
FEATURE [PartDesign::Pocket] Pocket045
  BaseFeature = -> Pocket025
  Direction = (-1,0,2.14311e-10)
  Length = 5
  Length2 = 5
  Placement = pos=(0,-84,2e-15) rot=(1,0,0;1.5708rad)
  Profile = -> Sketch086
  ReferenceAxis = -> Sketch086 [N_Axis]
  Refine = true
  Suppressed = false
  Type = 0
FEATURE [Sketcher::SketchObject] Sketch087
  ArcFitTolerance = 1e-06
  AttachmentSupport = -> [Pocket045]
  ExternalGeometry = -> [Pocket045]
  FullyConstrained = true
  MakeInternals = false
  MapMode = 5
  Placement = pos=(-1.2282e-09,-84,2e-15) rot=(-0.707107,0,0.707107;3.14159rad)
  sketch-geometry (7):
    g0: LineSegment [constr] StartX=-27.3536 StartY=-1.42e-14 StartZ=0 EndX=-27.3536 EndY=-5 EndZ=0
    g1: LineSegment [constr] StartX=-27.3536 StartY=-5 StartZ=0 EndX=-22.3536 EndY=-5 EndZ=0
    g2: LineSegment [constr] StartX=-22.3536 StartY=-5 StartZ=0 EndX=-17.3536 EndY=-5 EndZ=0
    g3: LineSegment [constr] StartX=-17.3536 StartY=-5 StartZ=0 EndX=-12.3536 EndY=-5 EndZ=0
    g4: Circle CenterX=-22.3536 CenterY=-5 CenterZ=0 NormalX=0 NormalY=0 NormalZ=1 AngleXU=0 Radius=1.3
    g5: Circle CenterX=-17.3536 CenterY=-5 CenterZ=0 NormalX=0 NormalY=0 NormalZ=1 AngleXU=0 Radius=1.3
    g6: Circle CenterX=-12.3536 CenterY=-5 CenterZ=0 NormalX=0 NormalY=0 NormalZ=1 AngleXU=0 Radius=1.3
  constraints (18):
    c: Distance(g0) = 5
    c: Coincident(g0,g-3)
    c: PointOnObject(g0,g-3)
    c: Distance(g1) = 5
    c: Coincident(g1,g0)
    c: Horizontal(g1)
    c: Distance(g2) = 5
    c: Coincident(g2,g1)
    c: Horizontal(g2)
    c: Distance(g3) = 5
    c: Coincident(g3,g2)
    c: Horizontal(g3)
    c: Diameter(g4) = 2.6
    c: Coincident(g4,g1)
    c: Diameter(g5) = 2.6
    c: Coincident(g5,g2)
    c: Diameter(g6) = 2.6
    c: Coincident(g6,g3)
FEATURE [PartDesign::Pocket] Pocket046
  BaseFeature = -> Pocket045
  Direction = (1,0,-2.14311e-10)
  Length = 5
  Length2 = 5
  Placement = pos=(0,-84,2e-15) rot=(1,0,0;1.5708rad)
  Profile = -> Sketch087
  ReferenceAxis = -> Sketch087 [N_Axis]
  Refine = true
  Suppressed = false
  Type = 0
FEATURE [Sketcher::SketchObject] Sketch088
  ArcFitTolerance = 1e-06
  AttachmentSupport = -> [Pocket046]
  ExternalGeometry = -> [Pocket046]
  FullyConstrained = true
  MakeInternals = false
  MapMode = 5
  Placement = pos=(84,-84,-1.80021e-08) rot=(0.707107,0,0.707107;3.14159rad)
  sketch-geometry (7):
    g0: LineSegment [constr] StartX=27.3536 StartY=-84 StartZ=0 EndX=27.3536 EndY=-79 EndZ=0
    g1: LineSegment [constr] StartX=27.3536 StartY=-79 StartZ=0 EndX=22.3536 EndY=-79 EndZ=0
    g2: LineSegment [constr] StartX=22.3536 StartY=-79 StartZ=0 EndX=17.3536 EndY=-79 EndZ=0
    g3: LineSegment [constr] StartX=17.3536 StartY=-79 StartZ=0 EndX=12.3536 EndY=-79 EndZ=0
    g4: Circle CenterX=12.3536 CenterY=-79 CenterZ=0 NormalX=0 NormalY=0 NormalZ=1 AngleXU=0 Radius=1.3
    g5: Circle CenterX=17.3536 CenterY=-79 CenterZ=0 NormalX=0 NormalY=0 NormalZ=1 AngleXU=0 Radius=1.3
    g6: Circle CenterX=22.3536 CenterY=-79 CenterZ=0 NormalX=0 NormalY=0 NormalZ=1 AngleXU=0 Radius=1.3
  constraints (18):
    c: Distance(g0) = 5
    c: Coincident(g0,g-3)
    c: PointOnObject(g0,g-3)
    c: Distance(g1) = 5
    c: Coincident(g1,g0)
    c: Horizontal(g1)
    c: Distance(g2) = 5
    c: Coincident(g2,g1)
    c: Horizontal(g2)
    c: Distance(g3) = 5
    c: Coincident(g3,g2)
    c: Horizontal(g3)
    c: Diameter(g4) = 2.6
    c: Coincident(g4,g3)
    c: Diameter(g5) = 2.6
    c: Coincident(g5,g2)
    c: Diameter(g6) = 2.6
    c: Coincident(g6,g1)
FEATURE [PartDesign::Pocket] Pocket047
  BaseFeature = -> Pocket046
  Direction = (-1,0,2.14311e-10)
  Length = 5
  Length2 = 5
  Placement = pos=(0,-84,2e-15) rot=(1,0,0;1.5708rad)
  Profile = -> Sketch088
  ReferenceAxis = -> Sketch088 [N_Axis]
  Refine = true
  Suppressed = false
  Type = 0
FEATURE [Sketcher::SketchObject] Sketch089
  ArcFitTolerance = 1e-06
  AttachmentSupport = -> [Pocket047]
  ExternalGeometry = -> [Pocket047]
  FullyConstrained = true
  MakeInternals = false
  MapMode = 5
  Placement = pos=(-1.2282e-09,-84,2e-15) rot=(-0.707107,0,0.707107;3.14159rad)
  sketch-geometry (7):
    g0: LineSegment [constr] StartX=-27.3536 StartY=-84 StartZ=0 EndX=-27.3536 EndY=-79 EndZ=0
    g1: LineSegment [constr] StartX=-27.3536 StartY=-79 StartZ=0 EndX=-22.3536 EndY=-79 EndZ=0
    g2: LineSegment [constr] StartX=-22.3536 StartY=-79 StartZ=0 EndX=-17.3536 EndY=-79 EndZ=0
    g3: LineSegment [constr] StartX=-17.3536 StartY=-79 StartZ=0 EndX=-12.3536 EndY=-79 EndZ=0
    g4: Circle CenterX=-22.3536 CenterY=-79 CenterZ=0 NormalX=0 NormalY=0 NormalZ=1 AngleXU=0 Radius=1.3
    g5: Circle CenterX=-17.3536 CenterY=-79 CenterZ=0 NormalX=0 NormalY=0 NormalZ=1 AngleXU=0 Radius=1.3
    g6: Circle CenterX=-12.3536 CenterY=-79 CenterZ=0 NormalX=0 NormalY=0 NormalZ=1 AngleXU=0 Radius=1.3
  constraints (18):
    c: Distance(g0) = 5
    c: Coincident(g0,g-3)
    c: PointOnObject(g0,g-3)
    c: Distance(g1) = 5
    c: Coincident(g1,g0)
    c: Horizontal(g1)
    c: Distance(g2) = 5
    c: Coincident(g2,g1)
    c: Horizontal(g2)
    c: Distance(g3) = 5
    c: Coincident(g3,g2)
    c: Horizontal(g3)
    c: Diameter(g4) = 2.6
    c: Coincident(g4,g1)
    c: Diameter(g5) = 2.6
    c: Coincident(g5,g2)
    c: Diameter(g6) = 2.6
    c: Coincident(g6,g3)
FEATURE [PartDesign::Pocket] Pocket048
  BaseFeature = -> Pocket047
  Direction = (1,0,-2.14311e-10)
  Length = 5
  Length2 = 5
  Placement = pos=(0,-84,2e-15) rot=(1,0,0;1.5708rad)
  Profile = -> Sketch089
  ReferenceAxis = -> Sketch089 [N_Axis]
  Refine = true
  Suppressed = false
  Type = 0
FEATURE [PartDesign::Body] Body002  label="Upper"
  AllowCompound = false
  Group = -> [ShapeBinder001,DatumPlane004,CopyFillet001,Sketch008,Pad006,Sketch009,Pocket001,Sketch010,Pocket002,Sketch011,Pocket003,Sketch012,Pocket004,Sketch013,Pocket005,Sketch030,Pad016,Sketch031,Pocket011,Sketch037,Pocket015,Sketch039,Pocket017,Sketch050,Pocket023,Sketch051,Pocket024,Sketch052,Pad023,Sketch053,Pocket025,Sketch086,Pocket045,Sketch087,Pocket046,Sketch088,Pocket047,Sketch089,Pocket048]
  Origin = -> Origin002
  Placement = pos=(0,-27,0) rot=(0,0,1;0rad)
  Tip = -> Pocket048
FEATURE [Sketcher::SketchObject] Sketch090
  ArcFitTolerance = 1e-06
  AttachmentSupport = -> [Pocket039]
  ExternalGeometry = -> [Pocket039]
  FullyConstrained = true
  MakeInternals = false
  MapMode = 5
  Placement = pos=(0,-4e-15,5) rot=(0,0,1;0rad)
  sketch-geometry (14):
    g0: LineSegment [constr] StartX=0 StartY=-122 StartZ=0 EndX=0 EndY=-117 EndZ=0
    g1: LineSegment [constr] StartX=84 StartY=-122 StartZ=0 EndX=84 EndY=-117 EndZ=0
    g2: LineSegment [constr] StartX=84 StartY=-117 StartZ=0 EndX=79 EndY=-117 EndZ=0
    g3: LineSegment [constr] StartX=79 StartY=-117 StartZ=0 EndX=74 EndY=-117 EndZ=0
    g4: LineSegment [constr] StartX=74 StartY=-117 StartZ=0 EndX=69 EndY=-117 EndZ=0
    g5: LineSegment [constr] StartX=0 StartY=-117 StartZ=0 EndX=5 EndY=-117 EndZ=0
    g6: LineSegment [constr] StartX=5 StartY=-117 StartZ=0 EndX=10 EndY=-117 EndZ=0
    g7: LineSegment [constr] StartX=10 StartY=-117 StartZ=0 EndX=15 EndY=-117 EndZ=0
    g8: Circle CenterX=15 CenterY=-117 CenterZ=0 NormalX=0 NormalY=0 NormalZ=1 AngleXU=0 Radius=1.3
    g9: Circle CenterX=10 CenterY=-117 CenterZ=0 NormalX=0 NormalY=0 NormalZ=1 AngleXU=0 Radius=1.3
    g10: Circle CenterX=5 CenterY=-117 CenterZ=0 NormalX=0 NormalY=0 NormalZ=1 AngleXU=0 Radius=1.3
    g11: Circle CenterX=69 CenterY=-117 CenterZ=0 NormalX=0 NormalY=0 NormalZ=1 AngleXU=0 Radius=1.3
    g12: Circle CenterX=74 CenterY=-117 CenterZ=0 NormalX=0 NormalY=0 NormalZ=1 AngleXU=0 Radius=1.3
    g13: Circle CenterX=79 CenterY=-117 CenterZ=0 NormalX=0 NormalY=0 NormalZ=1 AngleXU=0 Radius=1.3
  constraints (36):
    c: Distance(g0) = 5
    c: Coincident(g0,g-6)
    c: PointOnObject(g0,g-6)
    c: Distance(g1) = 5
    c: Coincident(g1,g-4)
    c: PointOnObject(g1,g-4)
    c: Distance(g2) = 5
    c: Coincident(g2,g1)
    c: Horizontal(g2)
    c: Distance(g3) = 5
    c: Coincident(g3,g2)
    c: Horizontal(g3)
    c: Distance(g4) = 5
    c: Coincident(g4,g3)
    c: Horizontal(g4)
    c: Distance(g5) = 5
    c: Coincident(g5,g0)
    c: Horizontal(g5)
    c: Distance(g6) = 5
    c: Coincident(g6,g5)
    c: Horizontal(g6)
    c: Distance(g7) = 5
    c: Coincident(g7,g6)
    c: Horizontal(g7)
    c: Coincident(g8,g7)
    c: Coincident(g9,g6)
    c: Diameter(g10) = 2.6
    c: Coincident(g10,g5)
    c: Coincident(g11,g4)
    c: Coincident(g12,g3)
    c: Coincident(g13,g2)
    c: Equal(g10,g9)
    c: Equal(g9,g8)
    c: Equal(g8,g11)
    c: Equal(g11,g12)
    c: Equal(g12,g13)
FEATURE [PartDesign::Pocket] Pocket049
  BaseFeature = -> Pocket039
  Direction = (0,0,-1)
  Length = 5
  Length2 = 5
  Profile = -> Sketch090
  ReferenceAxis = -> Sketch090 [N_Axis]
  Refine = true
  Suppressed = false
  Type = 1
FEATURE [PartDesign::ShapeBinder] CopyPocket049
  TraceSupport = false
FEATURE [PartDesign::Plane] DatumPlane015
  AttachmentSupport = -> [CopyPocket049]
  Length = 134.316
  MapMode = 5
  Placement = pos=(0,-4e-15,5) rot=(0,0,1;0rad)
  ResizeMode = 0
  Width = 172.316
FEATURE [Sketcher::SketchObject] Sketch091
  ArcFitTolerance = 1e-06
  AttachmentSupport = -> [DatumPlane015]
  ExternalGeometry = -> [CopyPocket049]
  FullyConstrained = true
  MakeInternals = false
  MapMode = 5
  Placement = pos=(0,-4e-15,5) rot=(0,0,1;0rad)
  sketch-geometry (6):
    g0: Circle CenterX=79 CenterY=-117 CenterZ=0 NormalX=0 NormalY=0 NormalZ=1 AngleXU=0 Radius=1.5
    g1: Circle CenterX=69 CenterY=-117 CenterZ=0 NormalX=0 NormalY=0 NormalZ=1 AngleXU=0 Radius=1.5
    g2: LineSegment StartX=84 StartY=-122 StartZ=0 EndX=84 EndY=-112 EndZ=0
    g3: LineSegment StartX=84 StartY=-112 StartZ=0 EndX=64 EndY=-112 EndZ=0
    g4: LineSegment StartX=64 StartY=-112 StartZ=0 EndX=64 EndY=-122 EndZ=0
    g5: LineSegment StartX=64 StartY=-122 StartZ=0 EndX=84 EndY=-122 EndZ=0
  constraints (15):
    c: Coincident(g0,g-10)
    c: Coincident(g1,g-8)
    c: Equal(g1,g0)
    c: Coincident(g2,g3)
    c: Coincident(g3,g4)
    c: Coincident(g4,g5)
    c: Coincident(g5,g2)
    c: Vertical(g2)
    c: Vertical(g4)
    c: Horizontal(g3)
    c: Horizontal(g5)
    c: Distance(g2,g4) = 20
    c: Distance(g3,g5) = 10
    c: Coincident(g2,g-4)
    c: Diameter(g1) = 3
FEATURE [PartDesign::Pad] Pad038
  Direction = (0,0,1)
  Length = 3
  Length2 = 10
  Placement = pos=(0,-4e-15,5) rot=(0,0,1;0rad)
  Profile = -> Sketch091
  ReferenceAxis = -> Sketch091 [N_Axis]
  Refine = true
  Suppressed = false
  Type = 0
FEATURE [Sketcher::SketchObject] Sketch092
  ArcFitTolerance = 1e-06
  AttachmentSupport = -> [Pad038]
  ExternalGeometry = -> [Pad038]
  FullyConstrained = true
  MakeInternals = false
  MapMode = 5
  Placement = pos=(0,-4e-15,8) rot=(0,0,1;0rad)
  sketch-geometry (5):
    g0: LineSegment [constr] StartX=64 StartY=-112 StartZ=0 EndX=64 EndY=-119.5 EndZ=0
    g1: LineSegment StartX=64 StartY=-119.5 StartZ=0 EndX=84 EndY=-119.5 EndZ=0
    g2: LineSegment StartX=64 StartY=-119.5 StartZ=0 EndX=64 EndY=-121 EndZ=0
    g3: LineSegment StartX=64 StartY=-121 StartZ=0 EndX=84 EndY=-121 EndZ=0
    g4: LineSegment StartX=84 StartY=-121 StartZ=0 EndX=84 EndY=-119.5 EndZ=0
  constraints (14):
    c: Distance(g0) = 7.5
    c: Coincident(g0,g-4)
    c: Vertical(g0)
    c: Coincident(g1,g0)
    c: PointOnObject(g1,g-5)
    c: Horizontal(g1)
    c: Distance(g2) = 1.5
    c: Coincident(g2,g0)
    c: Vertical(g2)
    c: Coincident(g3,g2)
    c: PointOnObject(g3,g-5)
    c: Horizontal(g3)
    c: Coincident(g4,g3)
    c: Coincident(g4,g1)
FEATURE [PartDesign::Pad] Pad039
  BaseFeature = -> Pad038
  Direction = (0,0,1)
  Length = 23
  Length2 = 10
  Placement = pos=(0,-4e-15,5) rot=(0,0,1;0rad)
  Profile = -> Sketch092
  ReferenceAxis = -> Sketch092 [N_Axis]
  Refine = true
  Suppressed = false
  Type = 0
FEATURE [Sketcher::SketchObject] Sketch093
  ArcFitTolerance = 1e-06
  AttachmentSupport = -> [Pad039]
  ExternalGeometry = -> [Pad039]
  FullyConstrained = true
  MakeInternals = false
  MapMode = 5
  Placement = pos=(0,-121,5) rot=(1,0,0;1.5708rad)
  sketch-geometry (7):
    g0: GeomPoint X=74 Y=26 Z=0
    g1: LineSegment [constr] StartX=74 StartY=26 StartZ=0 EndX=74 EndY=17 EndZ=0
    g2: LineSegment StartX=67 StartY=10 StartZ=0 EndX=81 EndY=10 EndZ=0
    g3: LineSegment StartX=81 StartY=10 StartZ=0 EndX=81 EndY=24 EndZ=0
    g4: LineSegment StartX=81 StartY=24 StartZ=0 EndX=67 EndY=24 EndZ=0
    g5: LineSegment StartX=67 StartY=24 StartZ=0 EndX=67 EndY=10 EndZ=0
    g6: GeomPoint [constr] X=74 Y=17 Z=0
  constraints (16):
    c: Symmetric(g-3,g-3,g0)
    c: Distance(g1) = 9
    c: Coincident(g1,g0)
    c: Vertical(g1)
    c: Coincident(g2,g3)
    c: Coincident(g3,g4)
    c: Coincident(g4,g5)
    c: Coincident(g5,g2)
    c: Horizontal(g2)
    c: Horizontal(g4)
    c: Vertical(g3)
    c: Vertical(g5)
    c: Symmetric(g4,g2,g6)
    c: Distance(g3,g5) = 14
    c: Distance(g2,g4) = 14
    c: Coincident(g6,g1)
FEATURE [PartDesign::Pocket] Pocket050
  BaseFeature = -> Pad039
  Direction = (0,1,-2e-16)
  Length = 5
  Length2 = 5
  Placement = pos=(0,-4e-15,5) rot=(0,0,1;0rad)
  Profile = -> Sketch093
  ReferenceAxis = -> Sketch093 [N_Axis]
  Refine = true
  Suppressed = false
  Type = 1
FEATURE [PartDesign::Pad] Pad040
  BaseFeature = -> Pocket050
  Direction = (0,-1,0)
  Length = 10
  Length2 = 10
  Placement = pos=(0,-4e-15,5) rot=(0,0,1;0rad)
  Profile = -> Pocket050 [Face9]
  Refine = true
  Suppressed = false
  Type = 3
  UpToFace = -> Pocket050 [Face6]
FEATURE [PartDesign::Chamfer] Chamfer023
  Angle = 45
  Base = -> Pad040 [Edge2,Edge1]
  BaseFeature = -> Pad040
  ChamferType = 0
  FlipDirection = false
  Placement = pos=(0,-4e-15,5) rot=(0,0,1;0rad)
  Refine = true
  Size = 5
  Size2 = 1
  SupportTransform = false
  Suppressed = false
  UseAllEdges = false
FEATURE [PartDesign::Body] Body014  label="CherryMXHolder"
  AllowCompound = false
  Group = -> [DatumPlane015,CopyPocket049,Sketch091,Pad038,Sketch092,Pad039,Sketch093,Pocket050,Pad040,Chamfer023]
  Origin = -> Origin014
  Tip = -> Chamfer023
FEATURE [Sketcher::SketchObject] Sketch094
  ArcFitTolerance = 1e-06
  AttachmentSupport = -> [Pocket049]
  ExternalGeometry = -> [Pocket049]
  FullyConstrained = true
  MakeInternals = false
  MapMode = 5
  Placement = pos=(0,-84,-8.9e-14) rot=(1,0,0;1.5708rad)
  sketch-geometry (7):
    g0: Circle CenterX=42 CenterY=14 CenterZ=0 NormalX=0 NormalY=0 NormalZ=1 AngleXU=0 Radius=3.125
    g1: ArcOfCircle CenterX=42 CenterY=14 CenterZ=0 NormalX=0 NormalY=0 NormalZ=1 AngleXU=0 Radius=5.75 StartAngle=0 EndAngle=3.14159
    g2: GeomPoint [constr] X=36.25 Y=14 Z=0
    g3: GeomPoint [constr] X=47.75 Y=14 Z=0
    g4: LineSegment StartX=36.25 StartY=14 StartZ=0 EndX=36.25 EndY=5 EndZ=0
    g5: LineSegment StartX=47.75 StartY=14 StartZ=0 EndX=47.75 EndY=5 EndZ=0
    g6: LineSegment StartX=47.75 StartY=5 StartZ=0 EndX=36.25 EndY=5 EndZ=0
  constraints (16):
    c: Coincident(g0,g-5)
    c: Equal(g0,g-5)
    c: Coincident(g1,g0)
    c: Tangent(g-4,g1)
    c: Horizontal(g3,g0)
    c: Horizontal(g0,g2)
    c: Coincident(g4,g2)
    c: PointOnObject(g4,g-6)
    c: Perpendicular(g-6,g4)
    c: Coincident(g5,g3)
    c: PointOnObject(g5,g-6)
    c: Vertical(g5)
    c: Coincident(g6,g5)
    c: Coincident(g6,g4)
    c: Coincident(g1,g4)
    c: Coincident(g1,g5)
FEATURE [PartDesign::Pad] Pad041
  BaseFeature = -> Pocket049
  Direction = (0,-1,-1.1e-15)
  Length = 8
  Length2 = 10
  Profile = -> Sketch094
  ReferenceAxis = -> Sketch094 [N_Axis]
  Refine = true
  Suppressed = false
  Type = 0
FEATURE [PartDesign::Body] Body007  label="Base"
  AllowCompound = false
  Group = -> [Clone001,Sketch028,Pocket009,Sketch029,Pocket010,Sketch057,Pocket028,Sketch058,Pocket029,Sketch059,Pad025,DatumPlane011,CopyBinBase,Binder,Binder001,Binder002,Binder003,Binder004,Sketch060,Pocket030,Sketch065,Pad026,Sketch075,Pad033,Sketch076,Pocket039,Sketch090,Pocket049,Sketch094,Pad041]
  Origin = -> Origin007
  Placement = pos=(-93,0,0) rot=(0,0,1;0rad)
  Tip = -> Pad041
FEATURE [PartDesign::ShapeBinder] CopyChamfer020
  Placement = pos=(0,1e-15,-1.25) rot=(1,0,0;3.14159rad)
  TraceSupport = false
FEATURE [PartDesign::Plane] DatumPlane016
  AttachmentSupport = -> [CopyChamfer020]
  Length = 92.8744
  MapMode = 5
  Placement = pos=(10,1e-15,-1.25) rot=(0.57735,-0.57735,0.57735;4.18879rad)
  ResizeMode = 0
  Width = 69.6244
FEATURE [Sketcher::SketchObject] Sketch095
  ArcFitTolerance = 1e-06
  AttachmentSupport = -> [DatumPlane016]
  ExternalGeometry = -> [CopyChamfer020]
  FullyConstrained = true
  MakeInternals = false
  MapMode = 5
  Placement = pos=(10,1e-15,-1.25) rot=(0.57735,-0.57735,0.57735;4.18879rad)
  sketch-geometry (16):
    g0: Circle CenterX=22 CenterY=25 CenterZ=0 NormalX=0 NormalY=0 NormalZ=1 AngleXU=0 Radius=1.3
    g1: Circle CenterX=52 CenterY=25 CenterZ=0 NormalX=0 NormalY=0 NormalZ=1 AngleXU=0 Radius=1.3
    g2: LineSegment [constr] StartX=19.5 StartY=22.5 StartZ=0 EndX=24.5 EndY=22.5 EndZ=0
    g3: LineSegment [constr] StartX=24.5 StartY=22.5 StartZ=0 EndX=24.5 EndY=27.5 EndZ=0
    g4: LineSegment [constr] StartX=24.5 StartY=27.5 StartZ=0 EndX=19.5 EndY=27.5 EndZ=0
    g5: LineSegment [constr] StartX=19.5 StartY=27.5 StartZ=0 EndX=19.5 EndY=22.5 EndZ=0
    g6: GeomPoint [constr] X=22 Y=25 Z=0
    g7: LineSegment [constr] StartX=49.5 StartY=22.5 StartZ=0 EndX=54.5 EndY=22.5 EndZ=0
    g8: LineSegment [constr] StartX=54.5 StartY=22.5 StartZ=0 EndX=54.5 EndY=27.5 EndZ=0
    g9: LineSegment [constr] StartX=54.5 StartY=27.5 StartZ=0 EndX=49.5 EndY=27.5 EndZ=0
    g10: LineSegment [constr] StartX=49.5 StartY=27.5 StartZ=0 EndX=49.5 EndY=22.5 EndZ=0
    g11: GeomPoint [constr] X=52 Y=25 Z=0
    g12: LineSegment StartX=19.5 StartY=22.5 StartZ=0 EndX=54.5 EndY=22.5 EndZ=0
    g13: LineSegment StartX=54.5 StartY=22.5 StartZ=0 EndX=54.5 EndY=30 EndZ=0
    g14: LineSegment StartX=19.5 StartY=22.5 StartZ=0 EndX=19.5 EndY=30 EndZ=0
    g15: LineSegment StartX=19.5 StartY=30 StartZ=0 EndX=54.5 EndY=30 EndZ=0
  constraints (38):
    c: Coincident(g0,g-4)
    c: Equal(g0,g-4)
    c: Coincident(g1,g-7)
    c: Equal(g1,g-7)
    c: Coincident(g2,g3)
    c: Coincident(g3,g4)
    c: Coincident(g4,g5)
    c: Coincident(g5,g2)
    c: Horizontal(g2)
    c: Horizontal(g4)
    c: Vertical(g3)
    c: Vertical(g5)
    c: Symmetric(g4,g2,g6)
    c: Distance(g3,g5) = 5
    c: Distance(g2,g4) = 5
    c: Coincident(g6,g0)
    c: Coincident(g7,g8)
    c: Coincident(g8,g9)
    c: Coincident(g9,g10)
    c: Coincident(g10,g7)
    c: Horizontal(g7)
    c: Horizontal(g9)
    c: Vertical(g8)
    c: Vertical(g10)
    c: Symmetric(g9,g7,g11)
    c: Distance(g8,g10) = 5
    c: Distance(g7,g9) = 5
    c: Coincident(g11,g1)
    c: Coincident(g12,g2)
    c: Coincident(g12,g7)
    c: Coincident(g13,g7)
    c: PointOnObject(g13,g-3)
    c: Vertical(g13)
    c: Coincident(g14,g2)
    c: PointOnObject(g14,g-3)
    c: Vertical(g14)
    c: Coincident(g15,g14)
    c: Coincident(g15,g13)
FEATURE [PartDesign::Pad] Pad042
  Direction = (1,0,0)
  Length = 3
  Length2 = 10
  Placement = pos=(10,1e-15,-1.25) rot=(0.57735,-0.57735,0.57735;4.18879rad)
  Profile = -> Sketch095
  ReferenceAxis = -> Sketch095 [N_Axis]
  Refine = true
  Suppressed = false
  Type = 0
FEATURE [Sketcher::SketchObject] Sketch096
  ArcFitTolerance = 1e-06
  AttachmentSupport = -> [Pad042]
  ExternalGeometry = -> [Pad042]
  FullyConstrained = true
  MakeInternals = false
  MapMode = 5
  Placement = pos=(13,1e-15,-1.25) rot=(0.57735,-0.57735,0.57735;4.18879rad)
  sketch-geometry (4):
    g0: LineSegment StartX=19.5 StartY=30 StartZ=0 EndX=19.5 EndY=22.5 EndZ=0
    g1: LineSegment StartX=19.5 StartY=22.5 StartZ=0 EndX=54.5 EndY=22.5 EndZ=0
    g2: LineSegment StartX=54.5 StartY=22.5 StartZ=0 EndX=54.5 EndY=30 EndZ=0
    g3: LineSegment StartX=54.5 StartY=30 StartZ=0 EndX=19.5 EndY=30 EndZ=0
  constraints (10):
    c: Coincident(g0,g1)
    c: Coincident(g1,g2)
    c: Coincident(g2,g3)
    c: Coincident(g3,g0)
    c: Vertical(g0)
    c: Vertical(g2)
    c: Horizontal(g1)
    c: Horizontal(g3)
    c: Coincident(g0,g-4)
    c: Coincident(g1,g-3)
FEATURE [PartDesign::Pad] Pad043
  BaseFeature = -> Pad042
  Direction = (1,0,0)
  Length = 35
  Length2 = 10
  Placement = pos=(10,1e-15,-1.25) rot=(0.57735,-0.57735,0.57735;4.18879rad)
  Profile = -> Sketch096
  ReferenceAxis = -> Sketch096 [N_Axis]
  Refine = true
  Suppressed = false
  Type = 0
FEATURE [Sketcher::SketchObject] Sketch097
  ArcFitTolerance = 1e-06
  AttachmentSupport = -> [Pad043]
  ExternalGeometry = -> [Pad043,CopyChamfer020]
  FullyConstrained = true
  MakeInternals = false
  MapMode = 5
  Placement = pos=(10,1e-15,-23.75) rot=(0,0,-1;1.5708rad)
  sketch-geometry (11):
    g0: LineSegment [constr] StartX=22.25 StartY=5.5 StartZ=0 EndX=51.75 EndY=5.5 EndZ=0
    g1: LineSegment [constr] StartX=51.75 StartY=5.5 StartZ=0 EndX=51.75 EndY=32.5 EndZ=0
    g2: LineSegment [constr] StartX=51.75 StartY=32.5 StartZ=0 EndX=22.25 EndY=32.5 EndZ=0
    g3: LineSegment [constr] StartX=22.25 StartY=32.5 StartZ=0 EndX=22.25 EndY=5.5 EndZ=0
    g4: GeomPoint [constr] X=37 Y=19 Z=0
    g5: GeomPoint X=37 Y=38 Z=0
    g6: GeomPoint X=19.5 Y=19 Z=0
    g7: Circle CenterX=22.25 CenterY=32.5 CenterZ=0 NormalX=0 NormalY=0 NormalZ=1 AngleXU=0 Radius=1.3
    g8: Circle CenterX=51.75 CenterY=32.5 CenterZ=0 NormalX=0 NormalY=0 NormalZ=1 AngleXU=0 Radius=1.3
    g9: Circle CenterX=51.75 CenterY=5.5 CenterZ=0 NormalX=0 NormalY=0 NormalZ=1 AngleXU=0 Radius=1.3
    g10: Circle CenterX=22.25 CenterY=5.5 CenterZ=0 NormalX=0 NormalY=0 NormalZ=1 AngleXU=0 Radius=1.3
  constraints (23):
    c: Coincident(g0,g1)
    c: Coincident(g1,g2)
    c: Coincident(g2,g3)
    c: Coincident(g3,g0)
    c: Horizontal(g0)
    c: Horizontal(g2)
    c: Vertical(g1)
    c: Vertical(g3)
    c: Symmetric(g2,g0,g4)
    c: Distance(g1,g3) = 29.5
    c: Distance(g0,g2) = 27
    c: Symmetric(g-3,g-3,g5)
    c: Symmetric(g-4,g-4,g6)
    c: Vertical(g4,g5)
    c: Horizontal(g4,g6)
    c: Diameter(g7) = 2.6
    c: Coincident(g7,g2)
    c: Coincident(g8,g1)
    c: Coincident(g9,g0)
    c: Coincident(g10,g0)
    c: Equal(g10,g7)
    c: Equal(g7,g8)
    c: Equal(g8,g9)
FEATURE [PartDesign::Pocket] Pocket051
  BaseFeature = -> Pad043
  Direction = (0,0,-1)
  Length = 5
  Length2 = 5
  Placement = pos=(10,1e-15,-1.25) rot=(0.57735,-0.57735,0.57735;4.18879rad)
  Profile = -> Sketch097
  ReferenceAxis = -> Sketch097 [N_Axis]
  Refine = true
  Suppressed = false
  Type = 1
FEATURE [Sketcher::SketchObject] Sketch098
  ArcFitTolerance = 1e-06
  AttachmentSupport = -> [Pocket051]
  ExternalGeometry = -> [Pocket051]
  FullyConstrained = true
  MakeInternals = false
  MapMode = 5
  Placement = pos=(10,1e-15,-23.75) rot=(0,0,-1;1.5708rad)
  sketch-geometry (7):
    g0: LineSegment StartX=24.5 StartY=6.5 StartZ=0 EndX=49.5 EndY=6.5 EndZ=0
    g1: LineSegment StartX=49.5 StartY=6.5 StartZ=0 EndX=49.5 EndY=31.5 EndZ=0
    g2: LineSegment StartX=49.5 StartY=31.5 StartZ=0 EndX=24.5 EndY=31.5 EndZ=0
    g3: LineSegment StartX=24.5 StartY=31.5 StartZ=0 EndX=24.5 EndY=6.5 EndZ=0
    g4: GeomPoint [constr] X=37 Y=19 Z=0
    g5: GeomPoint X=37 Y=38 Z=0
    g6: GeomPoint X=54.5 Y=19 Z=0
  constraints (15):
    c: Coincident(g0,g1)
    c: Coincident(g1,g2)
    c: Coincident(g2,g3)
    c: Coincident(g3,g0)
    c: Horizontal(g0)
    c: Horizontal(g2)
    c: Vertical(g1)
    c: Vertical(g3)
    c: Symmetric(g2,g0,g4)
    c: Distance(g1,g3) = 25
    c: Distance(g0,g2) = 25
    c: Symmetric(g-4,g-4,g5)
    c: Symmetric(g-3,g-3,g6)
    c: Horizontal(g4,g6)
    c: Vertical(g4,g5)
FEATURE [PartDesign::Pocket] Pocket052
  BaseFeature = -> Pocket051
  Direction = (0,0,-1)
  Length = 5
  Length2 = 5
  Placement = pos=(10,1e-15,-1.25) rot=(0.57735,-0.57735,0.57735;4.18879rad)
  Profile = -> Sketch098
  ReferenceAxis = -> Sketch098 [N_Axis]
  Refine = true
  Suppressed = false
  Type = 1
FEATURE [PartDesign::Chamfer] Chamfer024
  Angle = 45
  Base = -> Pocket052 [Edge19,Edge30]
  BaseFeature = -> Pocket052
  ChamferType = 0
  FlipDirection = false
  Placement = pos=(10,1e-15,-1.25) rot=(0.57735,-0.57735,0.57735;4.18879rad)
  Refine = true
  Size = 4
  Size2 = 1
  SupportTransform = false
  Suppressed = false
  UseAllEdges = false
FEATURE [PartDesign::Chamfer] Chamfer025
  Angle = 45
  Base = -> Chamfer024 [Edge37,Edge40,Edge35,Edge38]
  BaseFeature = -> Chamfer024
  ChamferType = 0
  FlipDirection = false
  Placement = pos=(10,1e-15,-1.25) rot=(0.57735,-0.57735,0.57735;4.18879rad)
  Refine = true
  Size = 3
  Size2 = 1
  SupportTransform = false
  Suppressed = false
  UseAllEdges = false
FEATURE [PartDesign::Body] Body015  label="ULN2003 Module Mount"
  AllowCompound = false
  Group = -> [DatumPlane016,CopyChamfer020,Sketch095,Pad042,Sketch096,Pad043,Sketch097,Pocket051,Sketch098,Pocket052,Chamfer024,Chamfer025]
  Origin = -> Origin015
  Tip = -> Chamfer025
FEATURE [PartDesign::ShapeBinder] CopyChamfer021
  Placement = pos=(0,1e-15,-1.25) rot=(1,0,0;3.14159rad)
  TraceSupport = false
FEATURE [PartDesign::Plane] DatumPlane017
  AttachmentSupport = -> [CopyChamfer021]
  Length = 324.937
  MapMode = 5
  Placement = pos=(84,1e-15,-1.25) rot=(0.57735,-0.57735,0.57735;4.18879rad)
  ResizeMode = 0
  Width = 82.1874
FEATURE [Sketcher::SketchObject] Sketch099
  ArcFitTolerance = 1e-06
  AttachmentSupport = -> [DatumPlane017]
  ExternalGeometry = -> [CopyChamfer021]
  FullyConstrained = true
  MakeInternals = false
  MapMode = 5
  Placement = pos=(84,1e-15,-1.25) rot=(0.57735,-0.57735,0.57735;4.18879rad)
  sketch-geometry (14):
    g0: Circle CenterX=102 CenterY=5 CenterZ=0 NormalX=0 NormalY=0 NormalZ=1 AngleXU=0 Radius=1.3
    g1: Circle CenterX=117 CenterY=5 CenterZ=0 NormalX=0 NormalY=0 NormalZ=1 AngleXU=0 Radius=1.3
    g2: Circle CenterX=117 CenterY=25 CenterZ=0 NormalX=0 NormalY=0 NormalZ=1 AngleXU=0 Radius=1.3
    g3: Circle CenterX=102 CenterY=25 CenterZ=0 NormalX=0 NormalY=0 NormalZ=1 AngleXU=0 Radius=1.3
    g4: LineSegment [constr] StartX=117 StartY=5 StartZ=0 EndX=102 EndY=5 EndZ=0
    g5: LineSegment [constr] StartX=102 StartY=5 StartZ=0 EndX=102 EndY=25 EndZ=0
    g6: LineSegment [constr] StartX=119 StartY=0 StartZ=0 EndX=119 EndY=30 EndZ=0
    g7: LineSegment StartX=119 StartY=30 StartZ=0 EndX=99 EndY=30 EndZ=0
    g8: LineSegment StartX=99 StartY=30 StartZ=0 EndX=99 EndY=0 EndZ=0
    g9: LineSegment StartX=99 StartY=0 StartZ=0 EndX=119 EndY=0 EndZ=0
    g10: LineSegment StartX=119 StartY=0 StartZ=0 EndX=129 EndY=0 EndZ=0
    g11: LineSegment StartX=129 StartY=0 StartZ=0 EndX=129 EndY=30 EndZ=0
    g12: LineSegment StartX=129 StartY=30 StartZ=0 EndX=119 EndY=30 EndZ=0
    g13: LineSegment [constr] StartX=119 StartY=30 StartZ=0 EndX=119 EndY=0 EndZ=0
  constraints (34):
    c: Coincident(g0,g-5)
    c: Equal(g0,g-5)
    c: Coincident(g1,g-4)
    c: Equal(g1,g-4)
    c: Coincident(g2,g-7)
    c: Equal(g2,g-7)
    c: Coincident(g3,g-6)
    c: Equal(g3,g-6)
    c: Coincident(g4,g1)
    c: Coincident(g4,g0)
    c: Coincident(g5,g0)
    c: Coincident(g5,g3)
    c: Coincident(g6,g7)
    c: Coincident(g7,g8)
    c: Coincident(g8,g9)
    c: Coincident(g9,g6)
    c: Vertical(g6)
    c: Vertical(g8)
    c: Horizontal(g7)
    c: Horizontal(g9)
    c: Distance(g6,g8) = 20
    c: Coincident(g6,g-3)
    c: PointOnObject(g7,g-8)
    c: Coincident(g10,g11)
    c: Coincident(g11,g12)
    c: Coincident(g12,g13)
    c: Coincident(g13,g10)
    c: Horizontal(g10)
    c: Horizontal(g12)
    c: Vertical(g11)
    c: Vertical(g13)
    c: Distance(g11,g13) = 10
    c: Distance(g10,g12) = 30
    c: Coincident(g10,g6)
FEATURE [PartDesign::Pad] Pad044
  Direction = (1,0,0)
  Length = 5
  Length2 = 10
  Placement = pos=(84,1e-15,-1.25) rot=(0.57735,-0.57735,0.57735;4.18879rad)
  Profile = -> Sketch099
  ReferenceAxis = -> Sketch099 [N_Axis]
  Refine = true
  Suppressed = false
  Type = 0
FEATURE [Sketcher::SketchObject] Sketch100
  ArcFitTolerance = 1e-06
  AttachmentSupport = -> [Pad044]
  ExternalGeometry = -> [Pad044]
  FullyConstrained = true
  MakeInternals = false
  MapMode = 5
  Placement = pos=(84,-129,-1.25) rot=(0.57735,0.57735,-0.57735;2.0944rad)
  sketch-geometry (7):
    g0: LineSegment StartX=0 StartY=5 StartZ=0 EndX=10.5925 EndY=65.0733 EndZ=0
    g1: LineSegment StartX=10.5925 StartY=65.0733 StartZ=0 EndX=15.5166 EndY=64.205 EndZ=0
    g2: LineSegment StartX=15.5166 StartY=64.205 StartZ=0 EndX=6.40736 EndY=12.5441 EndZ=0
    g3: LineSegment [constr] StartX=12.7376 StartY=5 StartZ=0 EndX=30 EndY=5 EndZ=0
    g4: ArcOfCircle CenterX=12.7376 CenterY=11.4279 CenterZ=0 NormalX=0 NormalY=0 NormalZ=1 AngleXU=0 Radius=6.42788 StartAngle=2.96706 EndAngle=4.71239
    g5: GeomPoint [constr] X=5.07713 Y=5 Z=0
    g6: LineSegment StartX=12.7376 StartY=5 StartZ=0 EndX=0 EndY=5 EndZ=0
  constraints (17):
    c: Distance(g0) = 61
    c: Angle(g-1,g0) = 1.39626
    c: Coincident(g0,g-3)
    c: Distance(g1) = 5
    c: Coincident(g1,g0)
    c: Perpendicular(g0,g1)
    c: Coincident(g2,g1)
    c: PointOnObject(g5,g-3)
    c: Parallel(g2,g0)
    c: Coincident(g3,g-3)
    c: PointOnObject(g5,g2)
    c: PointOnObject(g5,g3)
    c: Tangent(g2,g4) = -1.5708
    c: Tangent(g3,g4) = -1.5708
    c: Distance(g4,g5) = 10
    c: Coincident(g6,g3)
    c: Coincident(g6,g0)
FEATURE [PartDesign::Pad] Pad045
  BaseFeature = -> Pad044
  Direction = (0,-1,0)
  Length = 9
  Length2 = 10
  Placement = pos=(84,1e-15,-1.25) rot=(0.57735,-0.57735,0.57735;4.18879rad)
  Profile = -> Sketch100
  ReferenceAxis = -> Sketch100 [N_Axis]
  Refine = true
  Reversed = true
  Suppressed = false
  Type = 0
FEATURE [Sketcher::SketchObject] Sketch101
  ArcFitTolerance = 1e-06
  AttachmentSupport = -> [Pad045]
  ExternalGeometry = -> [Pad045]
  FullyConstrained = true
  MakeInternals = false
  MapMode = 5
  Placement = pos=(84.1508,1e-15,-0.39495) rot=(-0.086827,0.086827,-0.992433;1.57839rad)
  sketch-geometry (5):
    g0: LineSegment [constr] StartX=124.5 StartY=65.924 StartZ=0 EndX=124.5 EndY=60.424 EndZ=0
    g1: LineSegment [constr] StartX=124.5 StartY=60.424 StartZ=0 EndX=124.5 EndY=10.424 EndZ=0
    g2: LineSegment [constr] StartX=124.5 StartY=10.424 StartZ=0 EndX=124.5 EndY=4.92404 EndZ=0
    g3: Circle CenterX=124.5 CenterY=60.424 CenterZ=0 NormalX=0 NormalY=0 NormalZ=1 AngleXU=0 Radius=1.3
    g4: Circle CenterX=124.5 CenterY=10.424 CenterZ=0 NormalX=0 NormalY=0 NormalZ=1 AngleXU=0 Radius=1.3
  constraints (12):
    c: Symmetric(g-4,g-4,g0)
    c: Vertical(g0)
    c: Coincident(g1,g0)
    c: Vertical(g1)
    c: Coincident(g2,g1)
    c: Symmetric(g-3,g-3,g2)
    c: DistanceY(g1,g1) = 50
    c: Equal(g0,g2)
    c: Diameter(g3) = 2.6
    c: Coincident(g3,g0)
    c: Diameter(g4) = 2.6
    c: Coincident(g4,g1)
FEATURE [PartDesign::Pocket] Pocket053
  BaseFeature = -> Pad045
  Direction = (-0.173648,0,-0.984808)
  Length = 10
  Length2 = 5
  Placement = pos=(84,1e-15,-1.25) rot=(0.57735,-0.57735,0.57735;4.18879rad)
  Profile = -> Sketch101
  ReferenceAxis = -> Sketch101 [N_Axis]
  Refine = true
  Suppressed = false
  Type = 0
FEATURE [Sketcher::SketchObject] Sketch102
  ArcFitTolerance = 1e-06
  AttachmentSupport = -> [Pocket053]
  ExternalGeometry = -> [Pocket053]
  FullyConstrained = true
  MakeInternals = false
  MapMode = 5
  Placement = pos=(84.1508,1e-15,-0.39495) rot=(-0.086827,0.086827,-0.992433;1.57839rad)
  sketch-geometry (4):
    g0: Circle CenterX=124.5 CenterY=60.424 CenterZ=0 NormalX=0 NormalY=0 NormalZ=1 AngleXU=0 Radius=3.75
    g1: Circle CenterX=124.5 CenterY=10.424 CenterZ=0 NormalX=0 NormalY=0 NormalZ=1 AngleXU=0 Radius=3.75
    g2: Circle CenterX=124.5 CenterY=10.424 CenterZ=0 NormalX=0 NormalY=0 NormalZ=1 AngleXU=0 Radius=1.30001
    g3: Circle CenterX=124.5 CenterY=60.424 CenterZ=0 NormalX=0 NormalY=0 NormalZ=1 AngleXU=0 Radius=1.30001
  constraints (8):
    c: Diameter(g0) = 7.5
    c: Coincident(g0,g-3)
    c: Diameter(g1) = 7.5
    c: Coincident(g1,g-4)
    c: Coincident(g2,g1)
    c: Coincident(g3,g0)
    c: Tangent(g-4,g2)
    c: Tangent(g3,g-3)
FEATURE [PartDesign::Pad] Pad046
  BaseFeature = -> Pocket053
  Direction = (0.173648,0,0.984808)
  Length = 3
  Length2 = 10
  Placement = pos=(84,1e-15,-1.25) rot=(0.57735,-0.57735,0.57735;4.18879rad)
  Profile = -> Sketch102
  ReferenceAxis = -> Sketch102 [N_Axis]
  Refine = true
  Suppressed = false
  Type = 0
FEATURE [PartDesign::Pad] Pad047
  BaseFeature = -> Pad046
  Direction = (0,-1,2e-16)
  Length = 145
  Length2 = 10
  Placement = pos=(84,1e-15,-1.25) rot=(0.57735,-0.57735,0.57735;4.18879rad)
  Profile = -> Pad046 [Face6]
  Refine = true
  Suppressed = false
  Type = 0
FEATURE [Sketcher::SketchObject] Sketch103
  ArcFitTolerance = 1e-06
  AttachmentSupport = -> [Pad047]
  ExternalGeometry = -> [Pad047]
  FullyConstrained = true
  MakeInternals = false
  MapMode = 5
  Placement = pos=(84.1508,1.2e-15,-0.39495) rot=(-0.086827,0.086827,-0.992433;1.57839rad)
  sketch-geometry (11):
    g0: LineSegment [constr] StartX=124.5 StartY=60.424 StartZ=0 EndX=264.5 EndY=60.424 EndZ=0
    g1: LineSegment [constr] StartX=124.5 StartY=10.424 StartZ=0 EndX=264.5 EndY=10.424 EndZ=0
    g2: Circle CenterX=264.5 CenterY=60.424 CenterZ=0 NormalX=0 NormalY=0 NormalZ=1 AngleXU=0 Radius=1.3
    g3: Circle CenterX=264.5 CenterY=10.424 CenterZ=0 NormalX=0 NormalY=0 NormalZ=1 AngleXU=0 Radius=1.3
    g4: LineSegment [constr] StartX=194.5 StartY=60.424 StartZ=0 EndX=194.5 EndY=10.424 EndZ=0
    g5: LineSegment StartX=134.5 StartY=10.424 StartZ=0 EndX=254.5 EndY=10.424 EndZ=0
    g6: LineSegment StartX=254.5 StartY=10.424 StartZ=0 EndX=254.5 EndY=60.424 EndZ=0
    g7: LineSegment StartX=254.5 StartY=60.424 StartZ=0 EndX=134.5 EndY=60.424 EndZ=0
    g8: LineSegment StartX=134.5 StartY=60.424 StartZ=0 EndX=134.5 EndY=10.424 EndZ=0
    g9: GeomPoint [constr] X=194.5 Y=35.424 Z=0
    g10: GeomPoint X=194.5 Y=35.424 Z=0
  constraints (25):
    c: Distance(g0) = 140
    c: Coincident(g0,g-3)
    c: Horizontal(g0)
    c: Distance(g1) = 140
    c: Coincident(g1,g-4)
    c: Horizontal(g1)
    c: Diameter(g2) = 2.6
    c: Coincident(g2,g0)
    c: Diameter(g3) = 2.6
    c: Coincident(g3,g1)
    c: Symmetric(g0,g0,g4)
    c: Symmetric(g1,g1,g4)
    c: Coincident(g5,g6)
    c: Coincident(g6,g7)
    c: Coincident(g7,g8)
    c: Coincident(g8,g5)
    c: Horizontal(g5)
    c: Horizontal(g7)
    c: Vertical(g6)
    c: Vertical(g8)
    c: Symmetric(g7,g5,g9)
    c: Distance(g6,g8) = 120
    c: PointOnObject(g6,g0)
    c: Symmetric(g4,g4,g10)
    c: Coincident(g9,g10)
FEATURE [PartDesign::Pocket] Pocket054
  BaseFeature = -> Pad047
  Direction = (-0.173648,0,-0.984808)
  Length = 15
  Length2 = 5
  Placement = pos=(84,1e-15,-1.25) rot=(0.57735,-0.57735,0.57735;4.18879rad)
  Profile = -> Sketch103
  ReferenceAxis = -> Sketch103 [N_Axis]
  Refine = true
  Suppressed = false
  Type = 0
FEATURE [Sketcher::SketchObject] Sketch104
  ArcFitTolerance = 1e-06
  AttachmentSupport = -> [Pocket054]
  ExternalGeometry = -> [Pocket054]
  FullyConstrained = true
  MakeInternals = false
  MapMode = 5
  Placement = pos=(84.1508,1.2e-15,-0.39495) rot=(-0.086827,0.086827,-0.992433;1.57839rad)
  sketch-geometry (4):
    g0: Circle CenterX=264.5 CenterY=60.424 CenterZ=0 NormalX=0 NormalY=0 NormalZ=1 AngleXU=0 Radius=3.75
    g1: Circle CenterX=264.5 CenterY=10.424 CenterZ=0 NormalX=0 NormalY=0 NormalZ=1 AngleXU=0 Radius=3.75
    g2: Circle CenterX=264.5 CenterY=10.424 CenterZ=0 NormalX=0 NormalY=0 NormalZ=1 AngleXU=0 Radius=1.30001
    g3: Circle CenterX=264.5 CenterY=60.424 CenterZ=0 NormalX=0 NormalY=0 NormalZ=1 AngleXU=0 Radius=1.3
  constraints (8):
    c: Diameter(g0) = 7.5
    c: Coincident(g0,g-3)
    c: Diameter(g1) = 7.5
    c: Coincident(g1,g-4)
    c: Coincident(g2,g1)
    c: Tangent(g2,g-4)
    c: Coincident(g3,g0)
    c: Tangent(g3,g-3)
FEATURE [PartDesign::Pad] Pad048
  BaseFeature = -> Pocket054
  Direction = (0.173648,0,0.984808)
  Length = 3
  Length2 = 10
  Placement = pos=(84,1e-15,-1.25) rot=(0.57735,-0.57735,0.57735;4.18879rad)
  Profile = -> Sketch104
  ReferenceAxis = -> Sketch104 [N_Axis]
  Refine = true
  Suppressed = false
  Type = 0
FEATURE [PartDesign::Chamfer] Chamfer026
  Angle = 45
  Base = -> Pad048 [Edge26,Edge42]
  BaseFeature = -> Pad048
  ChamferType = 0
  FlipDirection = false
  Placement = pos=(84,1e-15,-1.25) rot=(0.57735,-0.57735,0.57735;4.18879rad)
  Refine = true
  Size = 4
  Size2 = 1
  SupportTransform = false
  Suppressed = false
  UseAllEdges = false
FEATURE [PartDesign::Chamfer] Chamfer027
  Angle = 45
  Base = -> Chamfer026 [Edge63,Edge60,Edge61,Edge62]
  BaseFeature = -> Chamfer026
  ChamferType = 0
  FlipDirection = false
  Placement = pos=(84,1e-15,-1.25) rot=(0.57735,-0.57735,0.57735;4.18879rad)
  Refine = true
  Size = 3
  Size2 = 1
  SupportTransform = false
  Suppressed = false
  UseAllEdges = false
FEATURE [Sketcher::SketchObject] Sketch105
  ArcFitTolerance = 1e-06
  AttachmentSupport = -> [Chamfer027]
  ExternalGeometry = -> [CopyChamfer021]
  FullyConstrained = true
  MakeInternals = false
  MapMode = 5
  Placement = pos=(84,1e-15,-1.25) rot=(0.57735,-0.57735,-0.57735;2.0944rad)
  sketch-geometry (3):
    g0: Circle CenterX=117 CenterY=-10 CenterZ=0 NormalX=0 NormalY=0 NormalZ=1 AngleXU=0 Radius=1.3
    g1: Circle CenterX=117 CenterY=-15 CenterZ=0 NormalX=0 NormalY=0 NormalZ=1 AngleXU=0 Radius=1.3
    g2: Circle CenterX=117 CenterY=-20 CenterZ=0 NormalX=0 NormalY=0 NormalZ=1 AngleXU=0 Radius=1.3
  constraints (6):
    c: Coincident(g0,g-3)
    c: Equal(g0,g-3)
    c: Coincident(g1,g-4)
    c: Equal(g1,g-4)
    c: Coincident(g2,g-5)
    c: Equal(g2,g-5)
FEATURE [PartDesign::Pocket] Pocket055
  BaseFeature = -> Chamfer027
  Direction = (1,0,0)
  Length = 5
  Length2 = 5
  Placement = pos=(84,1e-15,-1.25) rot=(0.57735,-0.57735,0.57735;4.18879rad)
  Profile = -> Sketch105
  ReferenceAxis = -> Sketch105 [N_Axis]
  Refine = true
  Suppressed = false
  Type = 0
FEATURE [PartDesign::LinearPattern] LinearPattern003
  BaseFeature = -> Pocket055
  Direction = -> Sketch105 [H_Axis]
  Length = 140
  Mode = 0
  Occurrences = 29
  Offset = 5
  Originals = -> [Pocket055]
  Placement = pos=(84,1e-15,-1.25) rot=(0.57735,-0.57735,0.57735;4.18879rad)
  Refine = true
  Suppressed = false
  TransformMode = 0
FEATURE [PartDesign::Body] Body016  label="Button PCB Mount"
  AllowCompound = false
  Group = -> [DatumPlane017,CopyChamfer021,Sketch099,Pad044,Sketch100,Pad045,Sketch101,Pocket053,Sketch102,Pad046,Pad047,Sketch103,Pocket054,Sketch104,Pad048,Chamfer026,Chamfer027,Sketch105,Pocket055,LinearPattern003]
  Origin = -> Origin016
  Tip = -> LinearPattern003
FEATURE [PartDesign::ShapeBinder] CopyChamfer022
  Placement = pos=(0,1e-15,-1.25) rot=(1,0,0;3.14159rad)
  TraceSupport = false
FEATURE [PartDesign::Plane] DatumPlane018
  AttachmentSupport = -> [CopyChamfer022]
  Length = 287.326
  MapMode = 5
  Placement = pos=(10,1e-15,-1.25) rot=(0.57735,-0.57735,0.57735;4.18879rad)
  ResizeMode = 0
  Width = 80.5759
FEATURE [Sketcher::SketchObject] Sketch106
  ArcFitTolerance = 1e-06
  AttachmentSupport = -> [DatumPlane018]
  ExternalGeometry = -> [CopyChamfer022]
  FullyConstrained = true
  MakeInternals = false
  MapMode = 5
  Placement = pos=(10,1e-15,-1.25) rot=(0.57735,-0.57735,0.57735;4.18879rad)
  sketch-geometry (11):
    g0: LineSegment StartX=119 StartY=30 StartZ=0 EndX=249 EndY=30 EndZ=0
    g1: LineSegment StartX=249 StartY=30 StartZ=0 EndX=249 EndY=27 EndZ=0
    g2: LineSegment StartX=249 StartY=27 StartZ=0 EndX=119 EndY=27 EndZ=0
    g3: LineSegment StartX=119 StartY=27 StartZ=0 EndX=119 EndY=12 EndZ=0
    g4: LineSegment StartX=119 StartY=12 StartZ=0 EndX=104 EndY=12 EndZ=0
    g5: LineSegment StartX=104 StartY=12 StartZ=0 EndX=104 EndY=30 EndZ=0
    g6: LineSegment StartX=104 StartY=30 StartZ=0 EndX=119 EndY=30 EndZ=0
    g7: Circle CenterX=117 CenterY=25 CenterZ=0 NormalX=0 NormalY=0 NormalZ=1 AngleXU=0 Radius=1.3
    g8: Circle CenterX=107 CenterY=25 CenterZ=0 NormalX=0 NormalY=0 NormalZ=1 AngleXU=0 Radius=1.3
    g9: Circle CenterX=107 CenterY=15 CenterZ=0 NormalX=0 NormalY=0 NormalZ=1 AngleXU=0 Radius=1.3
    g10: Circle CenterX=117 CenterY=15 CenterZ=0 NormalX=0 NormalY=0 NormalZ=1 AngleXU=0 Radius=1.3
  constraints (28):
    c: Distance(g0) = 130
    c: Coincident(g0,g-8)
    c: Horizontal(g0)
    c: Distance(g1) = 3
    c: Coincident(g1,g0)
    c: Vertical(g1)
    c: Coincident(g2,g1)
    c: PointOnObject(g2,g-8)
    c: Horizontal(g2)
    c: Distance(g3) = 15
    c: Coincident(g3,g2)
    c: PointOnObject(g3,g-8)
    c: Distance(g4) = 15
    c: Coincident(g4,g3)
    c: Horizontal(g4)
    c: Coincident(g5,g4)
    c: PointOnObject(g5,g-7)
    c: Vertical(g5)
    c: Coincident(g6,g5)
    c: Coincident(g6,g0)
    c: Coincident(g7,g-3)
    c: Equal(g7,g-3)
    c: Coincident(g8,g-5)
    c: Equal(g8,g-5)
    c: Coincident(g9,g-6)
    c: Equal(g9,g-6)
    c: Coincident(g10,g-4)
    c: Equal(g10,g-4)
FEATURE [PartDesign::Pad] Pad049
  Direction = (1,0,0)
  Length = 5
  Length2 = 10
  Placement = pos=(10,1e-15,-1.25) rot=(0.57735,-0.57735,0.57735;4.18879rad)
  Profile = -> Sketch106
  ReferenceAxis = -> Sketch106 [N_Axis]
  Refine = true
  Suppressed = false
  Type = 0
FEATURE [Sketcher::SketchObject] Sketch107
  ArcFitTolerance = 1e-06
  AttachmentSupport = -> [Pad049]
  ExternalGeometry = -> [Pad049]
  FullyConstrained = true
  MakeInternals = false
  MapMode = 5
  Placement = pos=(10,1e-15,-28.25) rot=(0,0,-1;1.5708rad)
  sketch-geometry (6):
    g0: LineSegment [constr] StartX=119 StartY=5 StartZ=0 EndX=164 EndY=5 EndZ=0
    g1: LineSegment [constr] StartX=164 StartY=5 StartZ=0 EndX=234 EndY=5 EndZ=0
    g2: LineSegment [constr] StartX=164 StartY=5 StartZ=0 EndX=164 EndY=-5.06e-14 EndZ=0
    g3: LineSegment [constr] StartX=234 StartY=5 StartZ=0 EndX=234 EndY=-7.46e-14 EndZ=0
    g4: Circle CenterX=164 CenterY=2.5 CenterZ=0 NormalX=0 NormalY=0 NormalZ=1 AngleXU=0 Radius=2.5
    g5: Circle CenterX=234 CenterY=2.5 CenterZ=0 NormalX=0 NormalY=0 NormalZ=1 AngleXU=0 Radius=2.5
  constraints (16):
    c: Distance(g0) = 45
    c: Coincident(g0,g-4)
    c: PointOnObject(g0,g-4)
    c: Distance(g1) = 70
    c: Coincident(g1,g0)
    c: PointOnObject(g1,g-4)
    c: Coincident(g2,g0)
    c: PointOnObject(g2,g-3)
    c: Vertical(g2)
    c: Coincident(g3,g1)
    c: PointOnObject(g3,g-3)
    c: Vertical(g3)
    c: Symmetric(g2,g2,g4)
    c: Tangent(g4,g1)
    c: Symmetric(g3,g3,g5)
    c: Tangent(g5,g1)
FEATURE [PartDesign::Pad] Pad050
  BaseFeature = -> Pad049
  Direction = (0,0,1)
  Length = 5
  Length2 = 10
  Placement = pos=(10,1e-15,-1.25) rot=(0.57735,-0.57735,0.57735;4.18879rad)
  Profile = -> Sketch107
  ReferenceAxis = -> Sketch107 [N_Axis]
  Refine = true
  Suppressed = false
  Type = 0
FEATURE [Sketcher::SketchObject] Sketch108
  ArcFitTolerance = 1e-06
  AttachmentSupport = -> [Pad050]
  ExternalGeometry = -> [Pad050]
  FullyConstrained = true
  MakeInternals = false
  MapMode = 5
  Placement = pos=(10,1e-15,-28.25) rot=(0,0,-1;1.5708rad)
  sketch-geometry (9):
    g0: LineSegment [constr] StartX=164 StartY=2.5 StartZ=0 EndX=164 EndY=82.5 EndZ=0
    g1: LineSegment [constr] StartX=234 StartY=2.5 StartZ=0 EndX=234 EndY=82.5 EndZ=0
    g2: Circle CenterX=164 CenterY=82.5 CenterZ=0 NormalX=0 NormalY=0 NormalZ=1 AngleXU=0 Radius=1.3
    g3: Circle CenterX=234 CenterY=82.5 CenterZ=0 NormalX=0 NormalY=0 NormalZ=1 AngleXU=0 Radius=1.3
    g4: LineSegment [constr] StartX=249 StartY=5 StartZ=0 EndX=249 EndY=85 EndZ=0
    g5: LineSegment StartX=249 StartY=85 StartZ=0 EndX=159 EndY=85 EndZ=0
    g6: LineSegment StartX=159 StartY=85 StartZ=0 EndX=159 EndY=5 EndZ=0
    g7: LineSegment StartX=159 StartY=5 StartZ=0 EndX=249 EndY=5 EndZ=0
    g8: LineSegment StartX=249 StartY=5 StartZ=0 EndX=249 EndY=85 EndZ=0
  constraints (24):
    c: Distance(g0) = 80
    c: Coincident(g0,g-4)
    c: Vertical(g0)
    c: Distance(g1) = 80
    c: Coincident(g1,g-3)
    c: Vertical(g1)
    c: Diameter(g2) = 2.6
    c: Coincident(g2,g0)
    c: Diameter(g3) = 2.6
    c: Coincident(g3,g1)
    c: Distance(g4) = 80
    c: Coincident(g4,g-5)
    c: Vertical(g4)
    c: Coincident(g5,g6)
    c: Coincident(g6,g7)
    c: Coincident(g7,g8)
    c: Coincident(g8,g5)
    c: Horizontal(g5)
    c: Horizontal(g7)
    c: Vertical(g6)
    c: Vertical(g8)
    c: Distance(g6,g8) = 90
    c: Coincident(g5,g4)
    c: PointOnObject(g6,g-6)
FEATURE [PartDesign::Pad] Pad051
  BaseFeature = -> Pad050
  Direction = (0,0,1)
  Length = 3
  Length2 = 10
  Placement = pos=(10,1e-15,-1.25) rot=(0.57735,-0.57735,0.57735;4.18879rad)
  Profile = -> Sketch108
  ReferenceAxis = -> Sketch108 [N_Axis]
  Refine = true
  Reversed = true
  Suppressed = false
  Type = 0
FEATURE [Sketcher::SketchObject] Sketch109
  ArcFitTolerance = 1e-06
  AttachmentSupport = -> [Pad051]
  ExternalGeometry = -> [Pad051]
  FullyConstrained = true
  MakeInternals = false
  MapMode = 5
  Placement = pos=(10,1e-15,-28.25) rot=(0,0,-1;1.5708rad)
  sketch-geometry (4):
    g0: Circle CenterX=164 CenterY=82.5 CenterZ=0 NormalX=0 NormalY=0 NormalZ=1 AngleXU=0 Radius=2.5
    g1: Circle CenterX=234 CenterY=82.5 CenterZ=0 NormalX=0 NormalY=0 NormalZ=1 AngleXU=0 Radius=2.5
    g2: Circle CenterX=234 CenterY=82.5 CenterZ=0 NormalX=0 NormalY=0 NormalZ=1 AngleXU=0 Radius=1.30001
    g3: Circle CenterX=164 CenterY=82.5 CenterZ=0 NormalX=0 NormalY=0 NormalZ=1 AngleXU=0 Radius=1.30001
  constraints (8):
    c: Diameter(g0) = 5
    c: Coincident(g0,g-4)
    c: Diameter(g1) = 5
    c: Coincident(g1,g-3)
    c: Coincident(g2,g1)
    c: Tangent(g2,g-3)
    c: Coincident(g3,g0)
    c: Tangent(g3,g-4)
FEATURE [PartDesign::Pad] Pad052
  BaseFeature = -> Pad051
  Direction = (0,0,1)
  Length = 5
  Length2 = 10
  Placement = pos=(10,1e-15,-1.25) rot=(0.57735,-0.57735,0.57735;4.18879rad)
  Profile = -> Sketch109
  ReferenceAxis = -> Sketch109 [N_Axis]
  Refine = true
  Suppressed = false
  Type = 0
FEATURE [Sketcher::SketchObject] Sketch110
  ArcFitTolerance = 1e-06
  AttachmentSupport = -> [Pad052]
  ExternalGeometry = -> [Pad052]
  FullyConstrained = true
  MakeInternals = false
  MapMode = 5
  Placement = pos=(10,1e-15,-23.25) rot=(0,0,-1;1.5708rad)
  sketch-geometry (2):
    g0: Circle CenterX=164 CenterY=2.5 CenterZ=0 NormalX=0 NormalY=0 NormalZ=1 AngleXU=0 Radius=1.3
    g1: Circle CenterX=234 CenterY=2.5 CenterZ=0 NormalX=0 NormalY=0 NormalZ=1 AngleXU=0 Radius=1.3
  constraints (4):
    c: Diameter(g0) = 2.6
    c: Coincident(g0,g-4)
    c: Diameter(g1) = 2.6
    c: Coincident(g1,g-3)
FEATURE [PartDesign::Pocket] Pocket056
  BaseFeature = -> Pad052
  Direction = (0,0,-1)
  Length = 5
  Length2 = 5
  Placement = pos=(10,1e-15,-1.25) rot=(0.57735,-0.57735,0.57735;4.18879rad)
  Profile = -> Sketch110
  ReferenceAxis = -> Sketch110 [N_Axis]
  Refine = true
  Suppressed = false
  Type = 1
FEATURE [PartDesign::Pocket] Pocket057
  BaseFeature = -> Pocket056
  Direction = (-4e-16,1,-2e-16)
  Length = 11
  Length2 = 5
  Placement = pos=(10,1e-15,-1.25) rot=(0.57735,-0.57735,0.57735;4.18879rad)
  Profile = -> Pocket056 [Face2]
  Refine = true
  Suppressed = false
  Type = 0
FEATURE [PartDesign::Chamfer] Chamfer028
  Angle = 45
  Base = -> Pocket057 [Edge24]
  BaseFeature = -> Pocket057
  ChamferType = 0
  FlipDirection = false
  Placement = pos=(10,1e-15,-1.25) rot=(0.57735,-0.57735,0.57735;4.18879rad)
  Refine = true
  Size = 30
  Size2 = 1
  SupportTransform = false
  Suppressed = false
  UseAllEdges = false
FEATURE [PartDesign::Chamfer] Chamfer029
  Angle = 45
  Base = -> Chamfer028 [Edge6]
  BaseFeature = -> Chamfer028
  ChamferType = 0
  FlipDirection = false
  Placement = pos=(10,1e-15,-1.25) rot=(0.57735,-0.57735,0.57735;4.18879rad)
  Refine = true
  Size = 12
  Size2 = 1
  SupportTransform = false
  Suppressed = false
  UseAllEdges = false
FEATURE [PartDesign::Chamfer] Chamfer030
  Angle = 45
  Base = -> Chamfer029 [Edge23]
  BaseFeature = -> Chamfer029
  ChamferType = 0
  FlipDirection = false
  Placement = pos=(10,1e-15,-1.25) rot=(0.57735,-0.57735,0.57735;4.18879rad)
  Refine = true
  Size = 10
  Size2 = 1
  SupportTransform = false
  Suppressed = false
  UseAllEdges = false
FEATURE [PartDesign::Pad] Pad053
  BaseFeature = -> Chamfer030
  Direction = (0,0,1)
  Length = 10
  Length2 = 10
  Placement = pos=(10,1e-15,-1.25) rot=(0.57735,-0.57735,0.57735;4.18879rad)
  Profile = -> Chamfer030 [Face25,Face23,Face22,Face24]
  Refine = true
  Suppressed = false
  Type = 0
FEATURE [Sketcher::SketchObject] Sketch111
  ArcFitTolerance = 1e-06
  AttachmentSupport = -> [Pad053]
  ExternalGeometry = -> [Pad053]
  FullyConstrained = true
  MakeInternals = false
  MapMode = 5
  Placement = pos=(10,4e-15,-28.25) rot=(0,0,-1;1.5708rad)
  sketch-geometry (6):
    g0: LineSegment [constr] StartX=238 StartY=42.5 StartZ=0 EndX=198 EndY=42.5 EndZ=0
    g1: LineSegment StartX=173 StartY=17.5 StartZ=0 EndX=223 EndY=17.5 EndZ=0
    g2: LineSegment StartX=223 StartY=17.5 StartZ=0 EndX=223 EndY=67.5 EndZ=0
    g3: LineSegment StartX=223 StartY=67.5 StartZ=0 EndX=173 EndY=67.5 EndZ=0
    g4: LineSegment StartX=173 StartY=67.5 StartZ=0 EndX=173 EndY=17.5 EndZ=0
    g5: GeomPoint [constr] X=198 Y=42.5 Z=0
  constraints (15):
    c: Distance(g0) = 40
    c: Symmetric(g-3,g-3,g0)
    c: Horizontal(g0)
    c: Coincident(g1,g2)
    c: Coincident(g2,g3)
    c: Coincident(g3,g4)
    c: Coincident(g4,g1)
    c: Horizontal(g1)
    c: Horizontal(g3)
    c: Vertical(g2)
    c: Vertical(g4)
    c: Symmetric(g3,g1,g5)
    c: Distance(g2,g4) = 50
    c: Distance(g1,g3) = 50
    c: Coincident(g5,g0)
FEATURE [PartDesign::Pocket] Pocket058
  BaseFeature = -> Pad053
  Direction = (0,0,-1)
  Length = 5
  Length2 = 5
  Placement = pos=(10,1e-15,-1.25) rot=(0.57735,-0.57735,0.57735;4.18879rad)
  Profile = -> Sketch111
  ReferenceAxis = -> Sketch111 [N_Axis]
  Refine = true
  Suppressed = false
  Type = 0
FEATURE [PartDesign::Body] Body017  label="V1 Driver PCB Mount"
  AllowCompound = false
  Group = -> [DatumPlane018,CopyChamfer022,Sketch106,Pad049,Sketch107,Pad050,Sketch108,Pad051,Sketch109,Pad052,Sketch110,Pocket056,Pocket057,Chamfer028,Chamfer029,Chamfer030,Pad053,Sketch111,Pocket058]
  Origin = -> Origin017
  Tip = -> Pocket058
